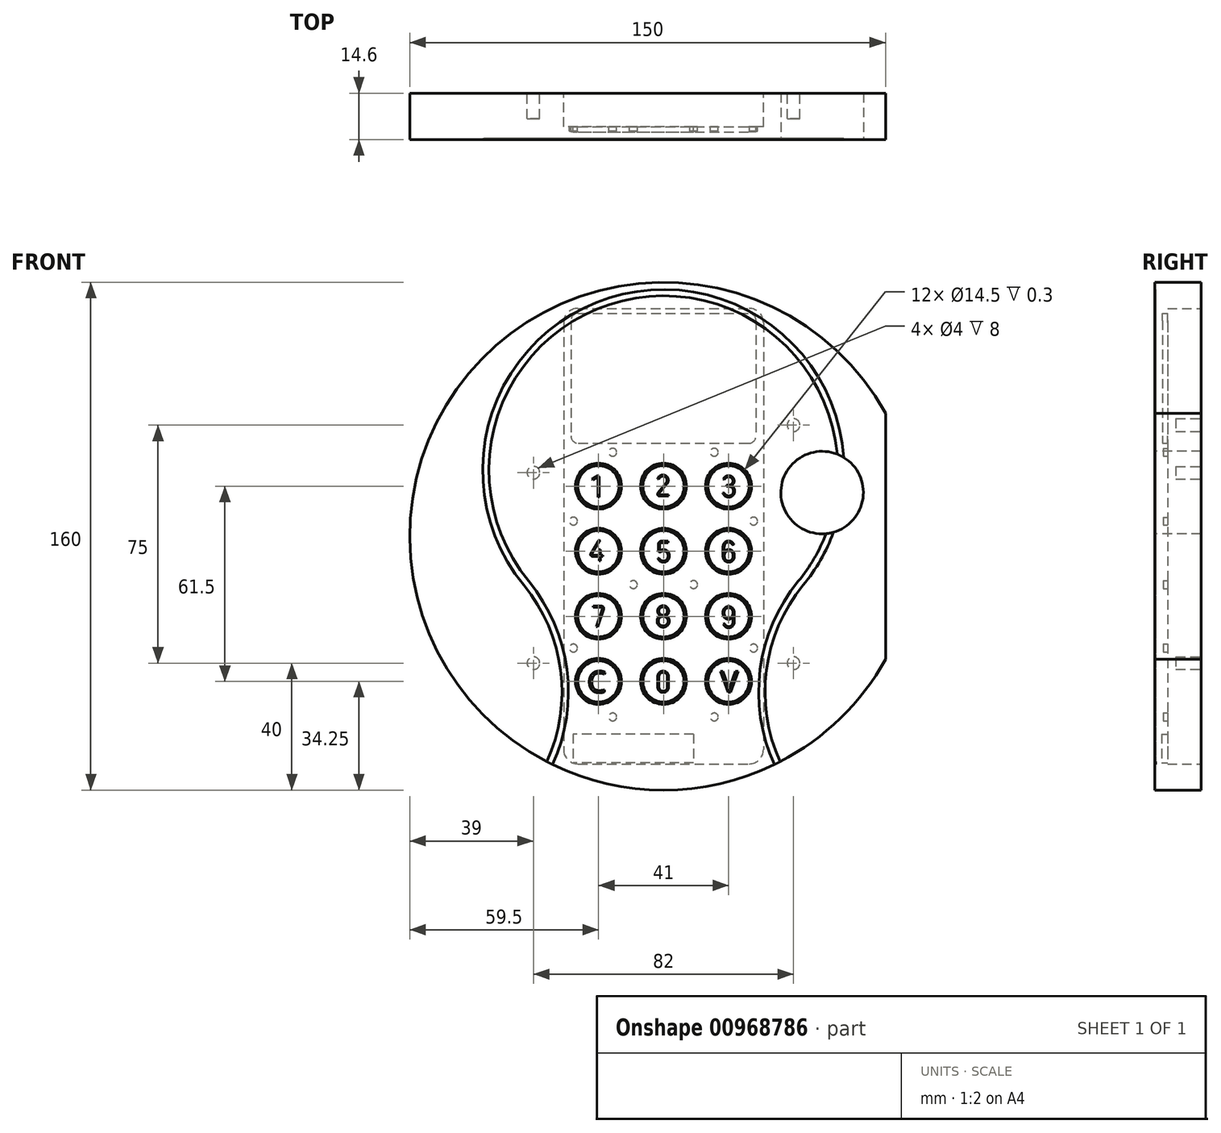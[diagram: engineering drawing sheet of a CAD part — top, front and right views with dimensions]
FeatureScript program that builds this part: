
annotation { "Feature Type Name" : "Feature", "Feature Type Description" : "" }
export const myFeature = defineFeature(function(context is Context, id is Id, definition is map)
    precondition{}
    {
        {
            var Q0;
            Q0=qCreatedBy(makeId("Front.planeOp"),FACE);
            var sketch = newSketch(context, id + "F0", { "sketchPlane" : qUnion([Q0])});
            skArc(sketch, "E0", {"start": v(70, -38.73) * mm, "mid": v(-80, 0) * mm, "end": v(70, 38.73) * mm});
            skLineSegment(sketch, "E1", {"start": v(70, 38.73) * mm, "end": v(70, -38.73) * mm});
            skSolve(sketch);
        }
        {
            var Q0;
            Q0 = qSketchRegion(id + "F0", true);
            extrude(context, id + "F1", {"entities" : qUnion([Q0]), "depth" : 14.6 * mm, "offsetDistance" : 25 * mm});
        }
        {
            var Q0;
            Q0=makeQuery(id+"F1.opExtrude","CAP_FACE",FACE,{"disambiguationData":[OSD([sQuery(id+"F0.wireOp",EDGE,"E0"),sQuery(id+"F0.wireOp",EDGE,"E1")])],"isStart":true});
            var sketch = newSketch(context, id + "F2", { "sketchPlane" : qUnion([Q0])});
            skLineSegment(sketch, "E2.bottom", {"start": v(31.5, 71.75) * mm, "end": v(-31.5, 71.75) * mm});
            skLineSegment(sketch, "E2.top", {"start": v(31.5, -71.75) * mm, "end": v(-31.5, -71.75) * mm});
            skLineSegment(sketch, "E2.left", {"start": v(31.5, 71.75) * mm, "end": v(31.5, -71.75) * mm});
            skLineSegment(sketch, "E2.right", {"start": v(-31.5, 71.75) * mm, "end": v(-31.5, -71.75) * mm});
            skSolve(sketch);
        }
        {
            var Q0;
            Q0 = qSketchRegion(id + "F2", true);
            extrude(context, id + "F3", {"entities" : qUnion([Q0]), "operationType" : NewBodyOperationType.REMOVE, "oppositeDirection" : true, "depth" : 10.6 * mm, "offsetDistance" : 25 * mm});
        }
        {
            var Q0;
            Q0=makeQuery(id+"F3.boolean.opBoolean","COPY",EDGE,{"derivedFrom":makeQuery(id+"F3.opExtrude","SWEPT_EDGE",EDGE,{"disambiguationData":[OSD([sQuery(id+"F2.wireOp",EDGE,"E2.bottom"),sQuery(id+"F2.wireOp",EDGE,"E2.left")])]})});
            var Q1;
            Q1=makeQuery(id+"F3.boolean.opBoolean","COPY",EDGE,{"derivedFrom":makeQuery(id+"F3.opExtrude","SWEPT_EDGE",EDGE,{"disambiguationData":[OSD([sQuery(id+"F2.wireOp",EDGE,"E2.bottom"),sQuery(id+"F2.wireOp",EDGE,"E2.right")])]})});
            var Q2;
            Q2=makeQuery(id+"F3.boolean.opBoolean","COPY",EDGE,{"derivedFrom":makeQuery(id+"F3.opExtrude","SWEPT_EDGE",EDGE,{"disambiguationData":[OSD([sQuery(id+"F2.wireOp",EDGE,"E2.top"),sQuery(id+"F2.wireOp",EDGE,"E2.left")])]})});
            var Q3;
            Q3=makeQuery(id+"F3.boolean.opBoolean","COPY",EDGE,{"derivedFrom":makeQuery(id+"F3.opExtrude","SWEPT_EDGE",EDGE,{"disambiguationData":[OSD([sQuery(id+"F2.wireOp",EDGE,"E2.top"),sQuery(id+"F2.wireOp",EDGE,"E2.right")])]})});
            fillet(context, id + "F4", {"entities" : qUnion([Q0, Q1, Q2, Q3]), "radius" : 4.5 * mm, "tangentPropagation" : true, "allowEdgeOverflow" : false});
        }
        {
            var Q0;
            Q0=makeQuery(id+"F3.boolean.opBoolean","COPY",FACE,{"derivedFrom":makeQuery(id+"F3.opExtrude","CAP_FACE",FACE,{"disambiguationData":[OSD([sQuery(id+"F2.wireOp",EDGE,"E2.bottom"),sQuery(id+"F2.wireOp",EDGE,"E2.top"),sQuery(id+"F2.wireOp",EDGE,"E2.left"),sQuery(id+"F2.wireOp",EDGE,"E2.right")])],"isStart":false})});
            var sketch = newSketch(context, id + "F5", { "sketchPlane" : qUnion([Q0])});
            skLineSegment(sketch, "E3.bottom", {"start": v(29.15, 70.25) * mm, "end": v(-29.15, 70.25) * mm});
            skLineSegment(sketch, "E3.top", {"start": v(29.15, 29.25) * mm, "end": v(-29.15, 29.25) * mm});
            skLineSegment(sketch, "E3.left", {"start": v(29.15, 70.25) * mm, "end": v(29.15, 29.25) * mm});
            skLineSegment(sketch, "E3.right", {"start": v(-29.15, 70.25) * mm, "end": v(-29.15, 29.25) * mm});
            skSolve(sketch);
        }
        {
            var Q0;
            Q0 = qSketchRegion(id + "F5", true);
            extrude(context, id + "F6", {"entities" : qUnion([Q0]), "operationType" : NewBodyOperationType.REMOVE, "oppositeDirection" : true, "depth" : 1.65 * mm, "offsetDistance" : 25 * mm});
        }
        {
            var Q0;
            Q0=makeQuery(id+"F6.boolean.opBoolean","COPY",EDGE,{"derivedFrom":makeQuery(id+"F6.opExtrude","SWEPT_EDGE",EDGE,{"disambiguationData":[OSD([sQuery(id+"F5.wireOp",EDGE,"E3.bottom"),sQuery(id+"F5.wireOp",EDGE,"E3.left")])]})});
            var Q1;
            Q1=makeQuery(id+"F6.boolean.opBoolean","COPY",EDGE,{"derivedFrom":makeQuery(id+"F6.opExtrude","SWEPT_EDGE",EDGE,{"disambiguationData":[OSD([sQuery(id+"F5.wireOp",EDGE,"E3.top"),sQuery(id+"F5.wireOp",EDGE,"E3.left")])]})});
            var Q2;
            Q2=makeQuery(id+"F6.boolean.opBoolean","COPY",EDGE,{"derivedFrom":makeQuery(id+"F6.opExtrude","SWEPT_EDGE",EDGE,{"disambiguationData":[OSD([sQuery(id+"F5.wireOp",EDGE,"E3.bottom"),sQuery(id+"F5.wireOp",EDGE,"E3.right")])]})});
            var Q3;
            Q3=makeQuery(id+"F6.boolean.opBoolean","COPY",EDGE,{"derivedFrom":makeQuery(id+"F6.opExtrude","SWEPT_EDGE",EDGE,{"disambiguationData":[OSD([sQuery(id+"F5.wireOp",EDGE,"E3.top"),sQuery(id+"F5.wireOp",EDGE,"E3.right")])]})});
            fillet(context, id + "F7", {"entities" : qUnion([Q0, Q1, Q2, Q3]), "radius" : 2.3 * mm, "tangentPropagation" : true, "allowEdgeOverflow" : false});
        }
        {
            var Q0;
            Q0=makeQuery(id+"F3.boolean.opBoolean","COPY",FACE,{"derivedFrom":makeQuery(id+"F3.opExtrude","CAP_FACE",FACE,{"disambiguationData":[OSD([sQuery(id+"F2.wireOp",EDGE,"E2.bottom"),sQuery(id+"F2.wireOp",EDGE,"E2.top"),sQuery(id+"F2.wireOp",EDGE,"E2.left"),sQuery(id+"F2.wireOp",EDGE,"E2.right")])],"isStart":false})});
            var sketch = newSketch(context, id + "F8", { "sketchPlane" : qUnion([Q0])});
            skCircle(sketch, "E4", {"center": v(-16, 26.45) * mm, "radius": 1.25 * mm});
            skCircle(sketch, "E5", {"center": v(16, 26.45) * mm, "radius": 1.25 * mm});
            skCircle(sketch, "E6", {"center": v(9.5, -15.25) * mm, "radius": 1.25 * mm});
            skCircle(sketch, "E7", {"center": v(-9.5, -15.25) * mm, "radius": 1.25 * mm});
            skCircle(sketch, "E8", {"center": v(-16, -56.95) * mm, "radius": 1.25 * mm});
            skCircle(sketch, "E9", {"center": v(16, -56.95) * mm, "radius": 1.25 * mm});
            skArc(sketch, "E10", {"start": v(-28.4, 6) * mm, "mid": v(-27.15, 4.75) * mm, "end": v(-28.4, 3.5) * mm});
            skArc(sketch, "E11.MirrorCS", {"start": v(28.4, 6) * mm, "mid": v(27.15, 4.75) * mm, "end": v(28.4, 3.5) * mm});
            skArc(sketch, "E12", {"start": v(-28.4, -34) * mm, "mid": v(-27.15, -35.25) * mm, "end": v(-28.4, -36.5) * mm});
            skArc(sketch, "E13.MirrorCS", {"start": v(28.4, -34) * mm, "mid": v(27.15, -35.25) * mm, "end": v(28.4, -36.5) * mm});
            skArc(sketch, "E14", {"start": v(-28.4, 3.5) * mm, "mid": v(-29.65, 4.75) * mm, "end": v(-28.4, 6) * mm});
            skArc(sketch, "E15", {"start": v(28.4, 6) * mm, "mid": v(29.65, 4.75) * mm, "end": v(28.4, 3.5) * mm});
            skArc(sketch, "E16", {"start": v(28.4, -34) * mm, "mid": v(29.65, -35.25) * mm, "end": v(28.4, -36.5) * mm});
            skArc(sketch, "E17", {"start": v(-28.4, -34) * mm, "mid": v(-29.65, -35.25) * mm, "end": v(-28.4, -36.5) * mm});
            skSolve(sketch);
        }
        {
            var Q0;
            Q0 = qSketchRegion(id + "F8", true);
            extrude(context, id + "F9", {"entities" : qUnion([Q0]), "operationType" : NewBodyOperationType.REMOVE, "oppositeDirection" : true, "depth" : 1.4 * mm, "offsetDistance" : 25 * mm});
        }
        {
            var Q0;
            Q0=makeQuery(id+"F3.boolean.opBoolean","COPY",FACE,{"derivedFrom":makeQuery(id+"F3.opExtrude","CAP_FACE",FACE,{"disambiguationData":[OSD([sQuery(id+"F2.wireOp",EDGE,"E2.bottom"),sQuery(id+"F2.wireOp",EDGE,"E2.top"),sQuery(id+"F2.wireOp",EDGE,"E2.left"),sQuery(id+"F2.wireOp",EDGE,"E2.right")])],"isStart":false})});
            var sketch = newSketch(context, id + "F10", { "sketchPlane" : qUnion([Q0])});
            skLineSegment(sketch, "E18.bottom", {"start": v(-9.5, -62.35) * mm, "end": v(28.5, -62.35) * mm});
            skLineSegment(sketch, "E18.top", {"start": v(-9.5, -71.35) * mm, "end": v(28.5, -71.35) * mm});
            skLineSegment(sketch, "E18.left", {"start": v(-9.5, -62.35) * mm, "end": v(-9.5, -71.35) * mm});
            skLineSegment(sketch, "E18.right", {"start": v(28.5, -62.35) * mm, "end": v(28.5, -71.35) * mm});
            skSolve(sketch);
        }
        {
            var Q0;
            Q0 = qSketchRegion(id + "F10", true);
            extrude(context, id + "F11", {"entities" : qUnion([Q0]), "operationType" : NewBodyOperationType.REMOVE, "oppositeDirection" : true, "depth" : 1.8 * mm, "offsetDistance" : 25 * mm});
        }
        {
            var Q0;
            Q0=makeQuery(id+"F1.opExtrude","CAP_FACE",FACE,{"disambiguationData":[OSD([sQuery(id+"F0.wireOp",EDGE,"E0"),sQuery(id+"F0.wireOp",EDGE,"E1")])],"isStart":false});
            var sketch = newSketch(context, id + "F12", { "sketchPlane" : qUnion([Q0])});
            skCircle(sketch, "E19", {"center": v(-20.5, 15.75) * mm, "radius": 7.25 * mm});
            skCircle(sketch, "E20", {"center": v(0, 15.75) * mm, "radius": 7.25 * mm});
            skCircle(sketch, "E21", {"center": v(20.5, 15.75) * mm, "radius": 7.25 * mm});
            skCircle(sketch, "E22", {"center": v(0, -4.75) * mm, "radius": 7.25 * mm});
            skCircle(sketch, "E23", {"center": v(-20.5, -4.75) * mm, "radius": 7.25 * mm});
            skCircle(sketch, "E24", {"center": v(20.5, -4.75) * mm, "radius": 7.25 * mm});
            skCircle(sketch, "E25", {"center": v(0, -25.25) * mm, "radius": 7.25 * mm});
            skCircle(sketch, "E26", {"center": v(-20.5, -25.25) * mm, "radius": 7.25 * mm});
            skCircle(sketch, "E27", {"center": v(20.5, -25.25) * mm, "radius": 7.25 * mm});
            skCircle(sketch, "E28", {"center": v(0, -45.75) * mm, "radius": 7.25 * mm});
            skCircle(sketch, "E29", {"center": v(-20.5, -45.75) * mm, "radius": 7.25 * mm});
            skCircle(sketch, "E30", {"center": v(20.5, -45.75) * mm, "radius": 7.25 * mm});
            skCircle(sketch, "E31", {"center": v(-20.5, 15.75) * mm, "radius": 6.5 * mm});
            skCircle(sketch, "E32", {"center": v(0, 15.75) * mm, "radius": 6.5 * mm});
            skCircle(sketch, "E33", {"center": v(20.5, 15.75) * mm, "radius": 6.5 * mm});
            skCircle(sketch, "E34", {"center": v(-20.5, -4.75) * mm, "radius": 6.5 * mm});
            skCircle(sketch, "E35", {"center": v(0, -4.75) * mm, "radius": 6.5 * mm});
            skCircle(sketch, "E36", {"center": v(20.5, -4.75) * mm, "radius": 6.5 * mm});
            skCircle(sketch, "E37", {"center": v(-20.5, -25.25) * mm, "radius": 6.5 * mm});
            skCircle(sketch, "E38", {"center": v(0, -25.25) * mm, "radius": 6.5 * mm});
            skCircle(sketch, "E39", {"center": v(20.5, -25.25) * mm, "radius": 6.5 * mm});
            skCircle(sketch, "E40", {"center": v(-20.5, -45.75) * mm, "radius": 6.5 * mm});
            skCircle(sketch, "E41", {"center": v(0, -45.75) * mm, "radius": 6.5 * mm});
            skCircle(sketch, "E42", {"center": v(20.5, -45.75) * mm, "radius": 6.5 * mm});
            skSolve(sketch);
        }
        {
            var Q0;
            Q0 = qSketchRegion(id + "F12", true);
            extrude(context, id + "F13", {"entities" : qUnion([Q0]), "operationType" : NewBodyOperationType.REMOVE, "oppositeDirection" : true, "depth" : 0.3 * mm, "offsetDistance" : 25 * mm});
        }
        {
            var Q0;
            Q0=makeQuery(id+"F13.boolean.opBoolean","SPLIT",FACE,{"disambiguationData":[TD([makeQuery(id+"F13.opExtrude","SWEPT_FACE",FACE,{"disambiguationData":[OSD([sQuery(id+"F12.wireOp",EDGE,"E31")])]})])],"derivedFrom":makeQuery(id+"F1.opExtrude","CAP_FACE",FACE,{"disambiguationData":[OSD([sQuery(id+"F0.wireOp",EDGE,"E0"),sQuery(id+"F0.wireOp",EDGE,"E1")])],"isStart":false})});
            var sketch = newSketch(context, id + "F14", { "sketchPlane" : qUnion([Q0])});
            skLineSegment(sketch, "E43", {"start": v(-20.2, 12.3) * mm, "end": v(-20.6, 12.3) * mm});
            skLineSegment(sketch, "E44", {"start": v(-20.6, 12.3) * mm, "end": v(-20.6, 18.3) * mm});
            skLineSegment(sketch, "E45", {"start": v(-20.6, 18.3) * mm, "end": v(-20.6, 18.36) * mm});
            skLineSegment(sketch, "E46", {"start": v(-20.6, 18.36) * mm, "end": v(-20.62, 18.4) * mm});
            skLineSegment(sketch, "E47", {"start": v(-20.62, 18.4) * mm, "end": v(-20.63, 18.44) * mm});
            skLineSegment(sketch, "E48", {"start": v(-20.63, 18.44) * mm, "end": v(-20.64, 18.47) * mm});
            skLineSegment(sketch, "E49", {"start": v(-20.64, 18.47) * mm, "end": v(-20.66, 18.5) * mm});
            skLineSegment(sketch, "E50", {"start": v(-20.66, 18.5) * mm, "end": v(-20.69, 18.53) * mm});
            skLineSegment(sketch, "E51", {"start": v(-20.69, 18.53) * mm, "end": v(-20.72, 18.55) * mm});
            skLineSegment(sketch, "E52", {"start": v(-20.72, 18.55) * mm, "end": v(-20.75, 18.56) * mm});
            skLineSegment(sketch, "E53", {"start": v(-20.75, 18.56) * mm, "end": v(-20.79, 18.57) * mm});
            skLineSegment(sketch, "E54", {"start": v(-20.79, 18.57) * mm, "end": v(-20.83, 18.57) * mm});
            skLineSegment(sketch, "E55", {"start": v(-20.83, 18.57) * mm, "end": v(-20.85, 18.57) * mm});
            skLineSegment(sketch, "E56", {"start": v(-20.85, 18.57) * mm, "end": v(-20.87, 18.57) * mm});
            skLineSegment(sketch, "E57", {"start": v(-20.87, 18.57) * mm, "end": v(-20.9, 18.56) * mm});
            skLineSegment(sketch, "E58", {"start": v(-20.9, 18.56) * mm, "end": v(-20.91, 18.56) * mm});
            skLineSegment(sketch, "E59", {"start": v(-20.91, 18.56) * mm, "end": v(-20.93, 18.55) * mm});
            skLineSegment(sketch, "E60", {"start": v(-20.93, 18.55) * mm, "end": v(-20.95, 18.54) * mm});
            skLineSegment(sketch, "E61", {"start": v(-20.95, 18.54) * mm, "end": v(-20.98, 18.53) * mm});
            skLineSegment(sketch, "E62", {"start": v(-20.98, 18.53) * mm, "end": v(-21, 18.52) * mm});
            skLineSegment(sketch, "E63", {"start": v(-21, 18.52) * mm, "end": v(-21.02, 18.5) * mm});
            skLineSegment(sketch, "E64", {"start": v(-21.02, 18.5) * mm, "end": v(-21.04, 18.5) * mm});
            skLineSegment(sketch, "E65", {"start": v(-21.04, 18.5) * mm, "end": v(-22.27, 17.72) * mm});
            skLineSegment(sketch, "E66", {"start": v(-22.27, 17.72) * mm, "end": v(-22.5, 18.06) * mm});
            skLineSegment(sketch, "E67", {"start": v(-22.5, 18.06) * mm, "end": v(-21.25, 18.84) * mm});
            skLineSegment(sketch, "E68", {"start": v(-21.25, 18.84) * mm, "end": v(-21.24, 18.85) * mm});
            skLineSegment(sketch, "E69", {"start": v(-21.24, 18.85) * mm, "end": v(-21.23, 18.85) * mm});
            skLineSegment(sketch, "E70", {"start": v(-21.23, 18.85) * mm, "end": v(-21.22, 18.86) * mm});
            skLineSegment(sketch, "E71", {"start": v(-21.22, 18.86) * mm, "end": v(-21.2, 18.87) * mm});
            skLineSegment(sketch, "E72", {"start": v(-21.2, 18.87) * mm, "end": v(-21.19, 18.87) * mm});
            skLineSegment(sketch, "E73", {"start": v(-21.19, 18.87) * mm, "end": v(-21.17, 18.88) * mm});
            skLineSegment(sketch, "E74", {"start": v(-21.17, 18.88) * mm, "end": v(-21.15, 18.9) * mm});
            skLineSegment(sketch, "E75", {"start": v(-21.15, 18.9) * mm, "end": v(-21.13, 18.9) * mm});
            skLineSegment(sketch, "E76", {"start": v(-21.13, 18.9) * mm, "end": v(-21.1, 18.9) * mm});
            skLineSegment(sketch, "E77", {"start": v(-21.1, 18.9) * mm, "end": v(-21.09, 18.92) * mm});
            skLineSegment(sketch, "E78", {"start": v(-21.09, 18.92) * mm, "end": v(-21.06, 18.93) * mm});
            skLineSegment(sketch, "E79", {"start": v(-21.06, 18.93) * mm, "end": v(-21.04, 18.94) * mm});
            skLineSegment(sketch, "E80", {"start": v(-21.04, 18.94) * mm, "end": v(-21.02, 18.95) * mm});
            skLineSegment(sketch, "E81", {"start": v(-21.02, 18.95) * mm, "end": v(-21, 18.95) * mm});
            skLineSegment(sketch, "E82", {"start": v(-21, 18.95) * mm, "end": v(-20.97, 18.96) * mm});
            skLineSegment(sketch, "E83", {"start": v(-20.97, 18.96) * mm, "end": v(-20.94, 18.96) * mm});
            skLineSegment(sketch, "E84", {"start": v(-20.94, 18.96) * mm, "end": v(-20.91, 18.97) * mm});
            skLineSegment(sketch, "E85", {"start": v(-20.91, 18.97) * mm, "end": v(-20.89, 18.97) * mm});
            skLineSegment(sketch, "E86", {"start": v(-20.89, 18.97) * mm, "end": v(-20.86, 18.97) * mm});
            skLineSegment(sketch, "E87", {"start": v(-20.86, 18.97) * mm, "end": v(-20.83, 18.97) * mm});
            skLineSegment(sketch, "E88", {"start": v(-20.83, 18.97) * mm, "end": v(-20.77, 18.97) * mm});
            skLineSegment(sketch, "E89", {"start": v(-20.77, 18.97) * mm, "end": v(-20.72, 18.96) * mm});
            skLineSegment(sketch, "E90", {"start": v(-20.72, 18.96) * mm, "end": v(-20.67, 18.95) * mm});
            skLineSegment(sketch, "E91", {"start": v(-20.67, 18.95) * mm, "end": v(-20.62, 18.94) * mm});
            skLineSegment(sketch, "E92", {"start": v(-20.62, 18.94) * mm, "end": v(-20.58, 18.92) * mm});
            skLineSegment(sketch, "E93", {"start": v(-20.58, 18.92) * mm, "end": v(-20.53, 18.9) * mm});
            skLineSegment(sketch, "E94", {"start": v(-20.53, 18.9) * mm, "end": v(-20.49, 18.88) * mm});
            skLineSegment(sketch, "E95", {"start": v(-20.49, 18.88) * mm, "end": v(-20.45, 18.85) * mm});
            skLineSegment(sketch, "E96", {"start": v(-20.45, 18.85) * mm, "end": v(-20.41, 18.82) * mm});
            skLineSegment(sketch, "E97", {"start": v(-20.41, 18.82) * mm, "end": v(-20.38, 18.79) * mm});
            skLineSegment(sketch, "E98", {"start": v(-20.38, 18.79) * mm, "end": v(-20.34, 18.75) * mm});
            skLineSegment(sketch, "E99", {"start": v(-20.34, 18.75) * mm, "end": v(-20.32, 18.71) * mm});
            skLineSegment(sketch, "E100", {"start": v(-20.32, 18.71) * mm, "end": v(-20.29, 18.67) * mm});
            skLineSegment(sketch, "E101", {"start": v(-20.29, 18.67) * mm, "end": v(-20.27, 18.62) * mm});
            skLineSegment(sketch, "E102", {"start": v(-20.27, 18.62) * mm, "end": v(-20.25, 18.58) * mm});
            skLineSegment(sketch, "E103", {"start": v(-20.25, 18.58) * mm, "end": v(-20.23, 18.53) * mm});
            skLineSegment(sketch, "E104", {"start": v(-20.23, 18.53) * mm, "end": v(-20.22, 18.48) * mm});
            skLineSegment(sketch, "E105", {"start": v(-20.22, 18.48) * mm, "end": v(-20.21, 18.42) * mm});
            skLineSegment(sketch, "E106", {"start": v(-20.21, 18.42) * mm, "end": v(-20.2, 18.36) * mm});
            skLineSegment(sketch, "E107", {"start": v(-20.2, 18.36) * mm, "end": v(-20.2, 18.3) * mm});
            skLineSegment(sketch, "E108", {"start": v(-20.2, 18.3) * mm, "end": v(-20.2, 12.3) * mm});
            skLineSegment(sketch, "E109", {"start": v(-1.2, 12.65) * mm, "end": v(-1.23, 12.65) * mm});
            skLineSegment(sketch, "E110", {"start": v(-1.23, 12.65) * mm, "end": v(-1.26, 12.65) * mm});
            skLineSegment(sketch, "E111", {"start": v(-1.26, 12.65) * mm, "end": v(-1.29, 12.66) * mm});
            skLineSegment(sketch, "E112", {"start": v(-1.29, 12.66) * mm, "end": v(-1.31, 12.66) * mm});
            skLineSegment(sketch, "E113", {"start": v(-1.31, 12.66) * mm, "end": v(-1.34, 12.66) * mm});
            skLineSegment(sketch, "E114", {"start": v(-1.34, 12.66) * mm, "end": v(-1.37, 12.67) * mm});
            skLineSegment(sketch, "E115", {"start": v(-1.37, 12.67) * mm, "end": v(-1.4, 12.67) * mm});
            skLineSegment(sketch, "E116", {"start": v(-1.4, 12.67) * mm, "end": v(-1.42, 12.68) * mm});
            skLineSegment(sketch, "E117", {"start": v(-1.42, 12.68) * mm, "end": v(-1.44, 12.69) * mm});
            skLineSegment(sketch, "E118", {"start": v(-1.44, 12.69) * mm, "end": v(-1.47, 12.7) * mm});
            skLineSegment(sketch, "E119", {"start": v(-1.47, 12.7) * mm, "end": v(-1.5, 12.7) * mm});
            skLineSegment(sketch, "E120", {"start": v(-1.5, 12.7) * mm, "end": v(-1.52, 12.71) * mm});
            skLineSegment(sketch, "E121", {"start": v(-1.52, 12.71) * mm, "end": v(-1.54, 12.72) * mm});
            skLineSegment(sketch, "E122", {"start": v(-1.54, 12.72) * mm, "end": v(-1.56, 12.73) * mm});
            skLineSegment(sketch, "E123", {"start": v(-1.56, 12.73) * mm, "end": v(-1.58, 12.74) * mm});
            skLineSegment(sketch, "E124", {"start": v(-1.58, 12.74) * mm, "end": v(-1.6, 12.76) * mm});
            skLineSegment(sketch, "E125", {"start": v(-1.6, 12.76) * mm, "end": v(-1.63, 12.77) * mm});
            skLineSegment(sketch, "E126", {"start": v(-1.63, 12.77) * mm, "end": v(-1.65, 12.78) * mm});
            skLineSegment(sketch, "E127", {"start": v(-1.65, 12.78) * mm, "end": v(-1.67, 12.8) * mm});
            skLineSegment(sketch, "E128", {"start": v(-1.67, 12.8) * mm, "end": v(-1.68, 12.81) * mm});
            skLineSegment(sketch, "E129", {"start": v(-1.68, 12.81) * mm, "end": v(-1.7, 12.83) * mm});
            skLineSegment(sketch, "E130", {"start": v(-1.7, 12.83) * mm, "end": v(-1.72, 12.85) * mm});
            skLineSegment(sketch, "E131", {"start": v(-1.72, 12.85) * mm, "end": v(-1.73, 12.86) * mm});
            skLineSegment(sketch, "E132", {"start": v(-1.73, 12.86) * mm, "end": v(-1.75, 12.88) * mm});
            skLineSegment(sketch, "E133", {"start": v(-1.75, 12.88) * mm, "end": v(-1.76, 12.9) * mm});
            skLineSegment(sketch, "E134", {"start": v(-1.76, 12.9) * mm, "end": v(-1.78, 12.92) * mm});
            skLineSegment(sketch, "E135", {"start": v(-1.78, 12.92) * mm, "end": v(-1.8, 12.94) * mm});
            skLineSegment(sketch, "E136", {"start": v(-1.8, 12.94) * mm, "end": v(-1.8, 12.96) * mm});
            skLineSegment(sketch, "E137", {"start": v(-1.8, 12.96) * mm, "end": v(-1.82, 12.98) * mm});
            skLineSegment(sketch, "E138", {"start": v(-1.82, 12.98) * mm, "end": v(-1.83, 13) * mm});
            skLineSegment(sketch, "E139", {"start": v(-1.83, 13) * mm, "end": v(-1.84, 13.03) * mm});
            skLineSegment(sketch, "E140", {"start": v(-1.84, 13.03) * mm, "end": v(-1.85, 13.05) * mm});
            skLineSegment(sketch, "E141", {"start": v(-1.85, 13.05) * mm, "end": v(-1.85, 13.07) * mm});
            skLineSegment(sketch, "E142", {"start": v(-1.85, 13.07) * mm, "end": v(-1.86, 13.1) * mm});
            skLineSegment(sketch, "E143", {"start": v(-1.86, 13.1) * mm, "end": v(-1.87, 13.12) * mm});
            skLineSegment(sketch, "E144", {"start": v(-1.87, 13.12) * mm, "end": v(-1.87, 13.14) * mm});
            skLineSegment(sketch, "E145", {"start": v(-1.87, 13.14) * mm, "end": v(-1.87, 13.17) * mm});
            skLineSegment(sketch, "E146", {"start": v(-1.87, 13.17) * mm, "end": v(-1.88, 13.2) * mm});
            skLineSegment(sketch, "E147", {"start": v(-1.88, 13.2) * mm, "end": v(-1.88, 13.22) * mm});
            skLineSegment(sketch, "E148", {"start": v(-1.88, 13.22) * mm, "end": v(-1.88, 13.25) * mm});
            skLineSegment(sketch, "E149", {"start": v(-1.88, 13.25) * mm, "end": v(-1.88, 13.27) * mm});
            skLineSegment(sketch, "E150", {"start": v(-1.88, 13.27) * mm, "end": v(-1.88, 13.29) * mm});
            skLineSegment(sketch, "E151", {"start": v(-1.88, 13.29) * mm, "end": v(-1.88, 13.3) * mm});
            skLineSegment(sketch, "E152", {"start": v(-1.88, 13.3) * mm, "end": v(-1.88, 13.33) * mm});
            skLineSegment(sketch, "E153", {"start": v(-1.88, 13.33) * mm, "end": v(-1.87, 13.35) * mm});
            skLineSegment(sketch, "E154", {"start": v(-1.87, 13.35) * mm, "end": v(-1.87, 13.37) * mm});
            skLineSegment(sketch, "E155", {"start": v(-1.87, 13.37) * mm, "end": v(-1.87, 13.4) * mm});
            skLineSegment(sketch, "E156", {"start": v(-1.87, 13.4) * mm, "end": v(-1.86, 13.41) * mm});
            skLineSegment(sketch, "E157", {"start": v(-1.86, 13.41) * mm, "end": v(-1.86, 13.43) * mm});
            skLineSegment(sketch, "E158", {"start": v(-1.86, 13.43) * mm, "end": v(-1.85, 13.45) * mm});
            skLineSegment(sketch, "E159", {"start": v(-1.85, 13.45) * mm, "end": v(-1.85, 13.47) * mm});
            skLineSegment(sketch, "E160", {"start": v(-1.85, 13.47) * mm, "end": v(-1.84, 13.5) * mm});
            skLineSegment(sketch, "E161", {"start": v(-1.84, 13.5) * mm, "end": v(-1.83, 13.52) * mm});
            skLineSegment(sketch, "E162", {"start": v(-1.83, 13.52) * mm, "end": v(-1.83, 13.54) * mm});
            skLineSegment(sketch, "E163", {"start": v(-1.83, 13.54) * mm, "end": v(-1.82, 13.56) * mm});
            skLineSegment(sketch, "E164", {"start": v(-1.82, 13.56) * mm, "end": v(-1.8, 13.58) * mm});
            skLineSegment(sketch, "E165", {"start": v(-1.8, 13.58) * mm, "end": v(-1.8, 13.6) * mm});
            skLineSegment(sketch, "E166", {"start": v(-1.8, 13.6) * mm, "end": v(-1.78, 13.62) * mm});
            skLineSegment(sketch, "E167", {"start": v(-1.78, 13.62) * mm, "end": v(-1.77, 13.65) * mm});
            skLineSegment(sketch, "E168", {"start": v(-1.77, 13.65) * mm, "end": v(-1.75, 13.67) * mm});
            skLineSegment(sketch, "E169", {"start": v(-1.75, 13.67) * mm, "end": v(0.67, 16.56) * mm});
            skLineSegment(sketch, "E170", {"start": v(0.67, 16.56) * mm, "end": v(0.71, 16.61) * mm});
            skLineSegment(sketch, "E171", {"start": v(0.71, 16.61) * mm, "end": v(0.76, 16.67) * mm});
            skLineSegment(sketch, "E172", {"start": v(0.76, 16.67) * mm, "end": v(0.8, 16.72) * mm});
            skLineSegment(sketch, "E173", {"start": v(0.8, 16.72) * mm, "end": v(0.83, 16.77) * mm});
            skLineSegment(sketch, "E174", {"start": v(0.83, 16.77) * mm, "end": v(0.86, 16.82) * mm});
            skLineSegment(sketch, "E175", {"start": v(0.86, 16.82) * mm, "end": v(0.9, 16.88) * mm});
            skLineSegment(sketch, "E176", {"start": v(0.9, 16.88) * mm, "end": v(0.92, 16.93) * mm});
            skLineSegment(sketch, "E177", {"start": v(0.92, 16.93) * mm, "end": v(0.95, 16.99) * mm});
            skLineSegment(sketch, "E178", {"start": v(0.95, 16.99) * mm, "end": v(0.98, 17.04) * mm});
            skLineSegment(sketch, "E179", {"start": v(0.98, 17.04) * mm, "end": v(1, 17.1) * mm});
            skLineSegment(sketch, "E180", {"start": v(1, 17.1) * mm, "end": v(1.02, 17.15) * mm});
            skLineSegment(sketch, "E181", {"start": v(1.02, 17.15) * mm, "end": v(1.04, 17.2) * mm});
            skLineSegment(sketch, "E182", {"start": v(1.04, 17.2) * mm, "end": v(1.06, 17.26) * mm});
            skLineSegment(sketch, "E183", {"start": v(1.06, 17.26) * mm, "end": v(1.07, 17.31) * mm});
            skLineSegment(sketch, "E184", {"start": v(1.07, 17.31) * mm, "end": v(1.08, 17.36) * mm});
            skLineSegment(sketch, "E185", {"start": v(1.08, 17.36) * mm, "end": v(1.1, 17.42) * mm});
            skLineSegment(sketch, "E186", {"start": v(1.1, 17.42) * mm, "end": v(1.1, 17.47) * mm});
            skLineSegment(sketch, "E187", {"start": v(1.1, 17.47) * mm, "end": v(1.1, 17.52) * mm});
            skLineSegment(sketch, "E188", {"start": v(1.1, 17.52) * mm, "end": v(1.1, 17.56) * mm});
            skLineSegment(sketch, "E189", {"start": v(1.1, 17.56) * mm, "end": v(1.11, 17.61) * mm});
            skLineSegment(sketch, "E190", {"start": v(1.11, 17.61) * mm, "end": v(1.11, 17.67) * mm});
            skLineSegment(sketch, "E191", {"start": v(1.11, 17.67) * mm, "end": v(1.1, 17.73) * mm});
            skLineSegment(sketch, "E192", {"start": v(1.1, 17.73) * mm, "end": v(1.1, 17.78) * mm});
            skLineSegment(sketch, "E193", {"start": v(1.1, 17.78) * mm, "end": v(1.1, 17.84) * mm});
            skLineSegment(sketch, "E194", {"start": v(1.1, 17.84) * mm, "end": v(1.09, 17.9) * mm});
            skLineSegment(sketch, "E195", {"start": v(1.09, 17.9) * mm, "end": v(1.08, 17.94) * mm});
            skLineSegment(sketch, "E196", {"start": v(1.08, 17.94) * mm, "end": v(1.07, 18) * mm});
            skLineSegment(sketch, "E197", {"start": v(1.07, 18) * mm, "end": v(1.05, 18.04) * mm});
            skLineSegment(sketch, "E198", {"start": v(1.05, 18.04) * mm, "end": v(1.04, 18.1) * mm});
            skLineSegment(sketch, "E199", {"start": v(1.04, 18.1) * mm, "end": v(1.02, 18.14) * mm});
            skLineSegment(sketch, "E200", {"start": v(1.02, 18.14) * mm, "end": v(1, 18.19) * mm});
            skLineSegment(sketch, "E201", {"start": v(1, 18.19) * mm, "end": v(0.98, 18.23) * mm});
            skLineSegment(sketch, "E202", {"start": v(0.98, 18.23) * mm, "end": v(0.96, 18.27) * mm});
            skLineSegment(sketch, "E203", {"start": v(0.96, 18.27) * mm, "end": v(0.93, 18.32) * mm});
            skLineSegment(sketch, "E204", {"start": v(0.93, 18.32) * mm, "end": v(0.9, 18.36) * mm});
            skLineSegment(sketch, "E205", {"start": v(0.9, 18.36) * mm, "end": v(0.88, 18.4) * mm});
            skLineSegment(sketch, "E206", {"start": v(0.88, 18.4) * mm, "end": v(0.85, 18.43) * mm});
            skLineSegment(sketch, "E207", {"start": v(0.85, 18.43) * mm, "end": v(0.82, 18.47) * mm});
            skLineSegment(sketch, "E208", {"start": v(0.82, 18.47) * mm, "end": v(0.8, 18.5) * mm});
            skLineSegment(sketch, "E209", {"start": v(0.8, 18.5) * mm, "end": v(0.76, 18.54) * mm});
            skLineSegment(sketch, "E210", {"start": v(0.76, 18.54) * mm, "end": v(0.73, 18.57) * mm});
            skLineSegment(sketch, "E211", {"start": v(0.73, 18.57) * mm, "end": v(0.7, 18.6) * mm});
            skLineSegment(sketch, "E212", {"start": v(0.7, 18.6) * mm, "end": v(0.65, 18.63) * mm});
            skLineSegment(sketch, "E213", {"start": v(0.65, 18.63) * mm, "end": v(0.62, 18.66) * mm});
            skLineSegment(sketch, "E214", {"start": v(0.62, 18.66) * mm, "end": v(0.58, 18.68) * mm});
            skLineSegment(sketch, "E215", {"start": v(0.58, 18.68) * mm, "end": v(0.54, 18.7) * mm});
            skLineSegment(sketch, "E216", {"start": v(0.54, 18.7) * mm, "end": v(0.5, 18.73) * mm});
            skLineSegment(sketch, "E217", {"start": v(0.5, 18.73) * mm, "end": v(0.45, 18.75) * mm});
            skLineSegment(sketch, "E218", {"start": v(0.45, 18.75) * mm, "end": v(0.4, 18.77) * mm});
            skLineSegment(sketch, "E219", {"start": v(0.4, 18.77) * mm, "end": v(0.36, 18.8) * mm});
            skLineSegment(sketch, "E220", {"start": v(0.36, 18.8) * mm, "end": v(0.31, 18.8) * mm});
            skLineSegment(sketch, "E221", {"start": v(0.31, 18.8) * mm, "end": v(0.26, 18.82) * mm});
            skLineSegment(sketch, "E222", {"start": v(0.26, 18.82) * mm, "end": v(0.21, 18.83) * mm});
            skLineSegment(sketch, "E223", {"start": v(0.21, 18.83) * mm, "end": v(0.16, 18.85) * mm});
            skLineSegment(sketch, "E224", {"start": v(0.16, 18.85) * mm, "end": v(0.11, 18.86) * mm});
            skLineSegment(sketch, "E225", {"start": v(0.11, 18.86) * mm, "end": v(0.06, 18.86) * mm});
            skLineSegment(sketch, "E226", {"start": v(0.06, 18.86) * mm, "end": v(0, 18.87) * mm});
            skLineSegment(sketch, "E227", {"start": v(0, 18.87) * mm, "end": v(-0.05, 18.87) * mm});
            skLineSegment(sketch, "E228", {"start": v(-0.05, 18.87) * mm, "end": v(-0.1, 18.88) * mm});
            skLineSegment(sketch, "E229", {"start": v(-0.1, 18.88) * mm, "end": v(-0.16, 18.88) * mm});
            skLineSegment(sketch, "E230", {"start": v(-0.16, 18.88) * mm, "end": v(-0.22, 18.88) * mm});
            skLineSegment(sketch, "E231", {"start": v(-0.22, 18.88) * mm, "end": v(-0.27, 18.88) * mm});
            skLineSegment(sketch, "E232", {"start": v(-0.27, 18.88) * mm, "end": v(-0.32, 18.87) * mm});
            skLineSegment(sketch, "E233", {"start": v(-0.32, 18.87) * mm, "end": v(-0.37, 18.87) * mm});
            skLineSegment(sketch, "E234", {"start": v(-0.37, 18.87) * mm, "end": v(-0.42, 18.86) * mm});
            skLineSegment(sketch, "E235", {"start": v(-0.42, 18.86) * mm, "end": v(-0.46, 18.85) * mm});
            skLineSegment(sketch, "E236", {"start": v(-0.46, 18.85) * mm, "end": v(-0.51, 18.84) * mm});
            skLineSegment(sketch, "E237", {"start": v(-0.51, 18.84) * mm, "end": v(-0.56, 18.83) * mm});
            skLineSegment(sketch, "E238", {"start": v(-0.56, 18.83) * mm, "end": v(-0.6, 18.82) * mm});
            skLineSegment(sketch, "E239", {"start": v(-0.6, 18.82) * mm, "end": v(-0.65, 18.8) * mm});
            skLineSegment(sketch, "E240", {"start": v(-0.65, 18.8) * mm, "end": v(-0.69, 18.79) * mm});
            skLineSegment(sketch, "E241", {"start": v(-0.69, 18.79) * mm, "end": v(-0.73, 18.77) * mm});
            skLineSegment(sketch, "E242", {"start": v(-0.73, 18.77) * mm, "end": v(-0.77, 18.75) * mm});
            skLineSegment(sketch, "E243", {"start": v(-0.77, 18.75) * mm, "end": v(-0.81, 18.73) * mm});
            skLineSegment(sketch, "E244", {"start": v(-0.81, 18.73) * mm, "end": v(-0.85, 18.71) * mm});
            skLineSegment(sketch, "E245", {"start": v(-0.85, 18.71) * mm, "end": v(-0.89, 18.7) * mm});
            skLineSegment(sketch, "E246", {"start": v(-0.89, 18.7) * mm, "end": v(-0.93, 18.67) * mm});
            skLineSegment(sketch, "E247", {"start": v(-0.93, 18.67) * mm, "end": v(-0.96, 18.64) * mm});
            skLineSegment(sketch, "E248", {"start": v(-0.96, 18.64) * mm, "end": v(-1, 18.62) * mm});
            skLineSegment(sketch, "E249", {"start": v(-1, 18.62) * mm, "end": v(-1.04, 18.59) * mm});
            skLineSegment(sketch, "E250", {"start": v(-1.04, 18.59) * mm, "end": v(-1.06, 18.56) * mm});
            skLineSegment(sketch, "E251", {"start": v(-1.06, 18.56) * mm, "end": v(-1.09, 18.54) * mm});
            skLineSegment(sketch, "E252", {"start": v(-1.09, 18.54) * mm, "end": v(-1.11, 18.52) * mm});
            skLineSegment(sketch, "E253", {"start": v(-1.11, 18.52) * mm, "end": v(-1.14, 18.5) * mm});
            skLineSegment(sketch, "E254", {"start": v(-1.14, 18.5) * mm, "end": v(-1.16, 18.47) * mm});
            skLineSegment(sketch, "E255", {"start": v(-1.16, 18.47) * mm, "end": v(-1.18, 18.44) * mm});
            skLineSegment(sketch, "E256", {"start": v(-1.18, 18.44) * mm, "end": v(-1.2, 18.41) * mm});
            skLineSegment(sketch, "E257", {"start": v(-1.2, 18.41) * mm, "end": v(-1.23, 18.38) * mm});
            skLineSegment(sketch, "E258", {"start": v(-1.23, 18.38) * mm, "end": v(-1.25, 18.36) * mm});
            skLineSegment(sketch, "E259", {"start": v(-1.25, 18.36) * mm, "end": v(-1.27, 18.33) * mm});
            skLineSegment(sketch, "E260", {"start": v(-1.27, 18.33) * mm, "end": v(-1.29, 18.3) * mm});
            skLineSegment(sketch, "E261", {"start": v(-1.29, 18.3) * mm, "end": v(-1.3, 18.26) * mm});
            skLineSegment(sketch, "E262", {"start": v(-1.3, 18.26) * mm, "end": v(-1.33, 18.23) * mm});
            skLineSegment(sketch, "E263", {"start": v(-1.33, 18.23) * mm, "end": v(-1.35, 18.2) * mm});
            skLineSegment(sketch, "E264", {"start": v(-1.35, 18.2) * mm, "end": v(-1.37, 18.16) * mm});
            skLineSegment(sketch, "E265", {"start": v(-1.37, 18.16) * mm, "end": v(-1.38, 18.13) * mm});
            skLineSegment(sketch, "E266", {"start": v(-1.38, 18.13) * mm, "end": v(-1.4, 18.1) * mm});
            skLineSegment(sketch, "E267", {"start": v(-1.4, 18.1) * mm, "end": v(-1.42, 18.06) * mm});
            skLineSegment(sketch, "E268", {"start": v(-1.42, 18.06) * mm, "end": v(-1.44, 18.02) * mm});
            skLineSegment(sketch, "E269", {"start": v(-1.44, 18.02) * mm, "end": v(-1.46, 17.98) * mm});
            skLineSegment(sketch, "E270", {"start": v(-1.46, 17.98) * mm, "end": v(-1.83, 18.12) * mm});
            skLineSegment(sketch, "E271", {"start": v(-1.83, 18.12) * mm, "end": v(-1.8, 18.22) * mm});
            skLineSegment(sketch, "E272", {"start": v(-1.8, 18.22) * mm, "end": v(-1.75, 18.31) * mm});
            skLineSegment(sketch, "E273", {"start": v(-1.75, 18.31) * mm, "end": v(-1.7, 18.4) * mm});
            skLineSegment(sketch, "E274", {"start": v(-1.7, 18.4) * mm, "end": v(-1.65, 18.48) * mm});
            skLineSegment(sketch, "E275", {"start": v(-1.65, 18.48) * mm, "end": v(-1.6, 18.56) * mm});
            skLineSegment(sketch, "E276", {"start": v(-1.6, 18.56) * mm, "end": v(-1.54, 18.64) * mm});
            skLineSegment(sketch, "E277", {"start": v(-1.54, 18.64) * mm, "end": v(-1.48, 18.71) * mm});
            skLineSegment(sketch, "E278", {"start": v(-1.48, 18.71) * mm, "end": v(-1.42, 18.78) * mm});
            skLineSegment(sketch, "E279", {"start": v(-1.42, 18.78) * mm, "end": v(-1.35, 18.85) * mm});
            skLineSegment(sketch, "E280", {"start": v(-1.35, 18.85) * mm, "end": v(-1.28, 18.9) * mm});
            skLineSegment(sketch, "E281", {"start": v(-1.28, 18.9) * mm, "end": v(-1.23, 18.94) * mm});
            skLineSegment(sketch, "E282", {"start": v(-1.23, 18.94) * mm, "end": v(-1.19, 18.97) * mm});
            skLineSegment(sketch, "E283", {"start": v(-1.19, 18.97) * mm, "end": v(-1.14, 19) * mm});
            skLineSegment(sketch, "E284", {"start": v(-1.14, 19) * mm, "end": v(-1.1, 19.04) * mm});
            skLineSegment(sketch, "E285", {"start": v(-1.1, 19.04) * mm, "end": v(-1.04, 19.06) * mm});
            skLineSegment(sketch, "E286", {"start": v(-1.04, 19.06) * mm, "end": v(-1, 19.1) * mm});
            skLineSegment(sketch, "E287", {"start": v(-1, 19.1) * mm, "end": v(-0.94, 19.12) * mm});
            skLineSegment(sketch, "E288", {"start": v(-0.94, 19.12) * mm, "end": v(-0.89, 19.14) * mm});
            skLineSegment(sketch, "E289", {"start": v(-0.89, 19.14) * mm, "end": v(-0.83, 19.16) * mm});
            skLineSegment(sketch, "E290", {"start": v(-0.83, 19.16) * mm, "end": v(-0.78, 19.18) * mm});
            skLineSegment(sketch, "E291", {"start": v(-0.78, 19.18) * mm, "end": v(-0.72, 19.2) * mm});
            skLineSegment(sketch, "E292", {"start": v(-0.72, 19.2) * mm, "end": v(-0.66, 19.22) * mm});
            skLineSegment(sketch, "E293", {"start": v(-0.66, 19.22) * mm, "end": v(-0.6, 19.23) * mm});
            skLineSegment(sketch, "E294", {"start": v(-0.6, 19.23) * mm, "end": v(-0.54, 19.24) * mm});
            skLineSegment(sketch, "E295", {"start": v(-0.54, 19.24) * mm, "end": v(-0.48, 19.26) * mm});
            skLineSegment(sketch, "E296", {"start": v(-0.48, 19.26) * mm, "end": v(-0.42, 19.26) * mm});
            skLineSegment(sketch, "E297", {"start": v(-0.42, 19.26) * mm, "end": v(-0.36, 19.27) * mm});
            skLineSegment(sketch, "E298", {"start": v(-0.36, 19.27) * mm, "end": v(-0.3, 19.28) * mm});
            skLineSegment(sketch, "E299", {"start": v(-0.3, 19.28) * mm, "end": v(-0.23, 19.28) * mm});
            skLineSegment(sketch, "E300", {"start": v(-0.23, 19.28) * mm, "end": v(-0.16, 19.28) * mm});
            skLineSegment(sketch, "E301", {"start": v(-0.16, 19.28) * mm, "end": v(-0.09, 19.28) * mm});
            skLineSegment(sketch, "E302", {"start": v(-0.09, 19.28) * mm, "end": v(-0.01, 19.27) * mm});
            skLineSegment(sketch, "E303", {"start": v(-0.01, 19.27) * mm, "end": v(0.06, 19.27) * mm});
            skLineSegment(sketch, "E304", {"start": v(0.06, 19.27) * mm, "end": v(0.13, 19.26) * mm});
            skLineSegment(sketch, "E305", {"start": v(0.13, 19.26) * mm, "end": v(0.2, 19.25) * mm});
            skLineSegment(sketch, "E306", {"start": v(0.2, 19.25) * mm, "end": v(0.27, 19.24) * mm});
            skLineSegment(sketch, "E307", {"start": v(0.27, 19.24) * mm, "end": v(0.33, 19.22) * mm});
            skLineSegment(sketch, "E308", {"start": v(0.33, 19.22) * mm, "end": v(0.4, 19.2) * mm});
            skLineSegment(sketch, "E309", {"start": v(0.4, 19.2) * mm, "end": v(0.46, 19.18) * mm});
            skLineSegment(sketch, "E310", {"start": v(0.46, 19.18) * mm, "end": v(0.53, 19.16) * mm});
            skLineSegment(sketch, "E311", {"start": v(0.53, 19.16) * mm, "end": v(0.59, 19.13) * mm});
            skLineSegment(sketch, "E312", {"start": v(0.59, 19.13) * mm, "end": v(0.65, 19.1) * mm});
            skLineSegment(sketch, "E313", {"start": v(0.65, 19.1) * mm, "end": v(0.7, 19.08) * mm});
            skLineSegment(sketch, "E314", {"start": v(0.7, 19.08) * mm, "end": v(0.76, 19.05) * mm});
            skLineSegment(sketch, "E315", {"start": v(0.76, 19.05) * mm, "end": v(0.82, 19.01) * mm});
            skLineSegment(sketch, "E316", {"start": v(0.82, 19.01) * mm, "end": v(0.87, 18.98) * mm});
            skLineSegment(sketch, "E317", {"start": v(0.87, 18.98) * mm, "end": v(0.92, 18.94) * mm});
            skLineSegment(sketch, "E318", {"start": v(0.92, 18.94) * mm, "end": v(0.97, 18.9) * mm});
            skLineSegment(sketch, "E319", {"start": v(0.97, 18.9) * mm, "end": v(1.01, 18.86) * mm});
            skLineSegment(sketch, "E320", {"start": v(1.01, 18.86) * mm, "end": v(1.06, 18.82) * mm});
            skLineSegment(sketch, "E321", {"start": v(1.06, 18.82) * mm, "end": v(1.1, 18.78) * mm});
            skLineSegment(sketch, "E322", {"start": v(1.1, 18.78) * mm, "end": v(1.14, 18.73) * mm});
            skLineSegment(sketch, "E323", {"start": v(1.14, 18.73) * mm, "end": v(1.18, 18.68) * mm});
            skLineSegment(sketch, "E324", {"start": v(1.18, 18.68) * mm, "end": v(1.22, 18.63) * mm});
            skLineSegment(sketch, "E325", {"start": v(1.22, 18.63) * mm, "end": v(1.25, 18.58) * mm});
            skLineSegment(sketch, "E326", {"start": v(1.25, 18.58) * mm, "end": v(1.29, 18.53) * mm});
            skLineSegment(sketch, "E327", {"start": v(1.29, 18.53) * mm, "end": v(1.32, 18.47) * mm});
            skLineSegment(sketch, "E328", {"start": v(1.32, 18.47) * mm, "end": v(1.35, 18.41) * mm});
            skLineSegment(sketch, "E329", {"start": v(1.35, 18.41) * mm, "end": v(1.37, 18.35) * mm});
            skLineSegment(sketch, "E330", {"start": v(1.37, 18.35) * mm, "end": v(1.4, 18.3) * mm});
            skLineSegment(sketch, "E331", {"start": v(1.4, 18.3) * mm, "end": v(1.42, 18.23) * mm});
            skLineSegment(sketch, "E332", {"start": v(1.42, 18.23) * mm, "end": v(1.44, 18.17) * mm});
            skLineSegment(sketch, "E333", {"start": v(1.44, 18.17) * mm, "end": v(1.46, 18.1) * mm});
            skLineSegment(sketch, "E334", {"start": v(1.46, 18.1) * mm, "end": v(1.47, 18.04) * mm});
            skLineSegment(sketch, "E335", {"start": v(1.47, 18.04) * mm, "end": v(1.49, 17.97) * mm});
            skLineSegment(sketch, "E336", {"start": v(1.49, 17.97) * mm, "end": v(1.5, 17.9) * mm});
            skLineSegment(sketch, "E337", {"start": v(1.5, 17.9) * mm, "end": v(1.5, 17.83) * mm});
            skLineSegment(sketch, "E338", {"start": v(1.5, 17.83) * mm, "end": v(1.51, 17.76) * mm});
            skLineSegment(sketch, "E339", {"start": v(1.51, 17.76) * mm, "end": v(1.52, 17.69) * mm});
            skLineSegment(sketch, "E340", {"start": v(1.52, 17.69) * mm, "end": v(1.52, 17.61) * mm});
            skLineSegment(sketch, "E341", {"start": v(1.52, 17.61) * mm, "end": v(1.52, 17.54) * mm});
            skLineSegment(sketch, "E342", {"start": v(1.52, 17.54) * mm, "end": v(1.51, 17.47) * mm});
            skLineSegment(sketch, "E343", {"start": v(1.51, 17.47) * mm, "end": v(1.5, 17.4) * mm});
            skLineSegment(sketch, "E344", {"start": v(1.5, 17.4) * mm, "end": v(1.5, 17.32) * mm});
            skLineSegment(sketch, "E345", {"start": v(1.5, 17.32) * mm, "end": v(1.48, 17.25) * mm});
            skLineSegment(sketch, "E346", {"start": v(1.48, 17.25) * mm, "end": v(1.46, 17.18) * mm});
            skLineSegment(sketch, "E347", {"start": v(1.46, 17.18) * mm, "end": v(1.44, 17.11) * mm});
            skLineSegment(sketch, "E348", {"start": v(1.44, 17.11) * mm, "end": v(1.42, 17.05) * mm});
            skLineSegment(sketch, "E349", {"start": v(1.42, 17.05) * mm, "end": v(1.4, 16.98) * mm});
            skLineSegment(sketch, "E350", {"start": v(1.4, 16.98) * mm, "end": v(1.37, 16.91) * mm});
            skLineSegment(sketch, "E351", {"start": v(1.37, 16.91) * mm, "end": v(1.34, 16.85) * mm});
            skLineSegment(sketch, "E352", {"start": v(1.34, 16.85) * mm, "end": v(1.3, 16.79) * mm});
            skLineSegment(sketch, "E353", {"start": v(1.3, 16.79) * mm, "end": v(1.27, 16.72) * mm});
            skLineSegment(sketch, "E354", {"start": v(1.27, 16.72) * mm, "end": v(1.24, 16.66) * mm});
            skLineSegment(sketch, "E355", {"start": v(1.24, 16.66) * mm, "end": v(1.2, 16.6) * mm});
            skLineSegment(sketch, "E356", {"start": v(1.2, 16.6) * mm, "end": v(1.16, 16.54) * mm});
            skLineSegment(sketch, "E357", {"start": v(1.16, 16.54) * mm, "end": v(1.12, 16.48) * mm});
            skLineSegment(sketch, "E358", {"start": v(1.12, 16.48) * mm, "end": v(1.07, 16.42) * mm});
            skLineSegment(sketch, "E359", {"start": v(1.07, 16.42) * mm, "end": v(1.03, 16.36) * mm});
            skLineSegment(sketch, "E360", {"start": v(1.03, 16.36) * mm, "end": v(0.98, 16.3) * mm});
            skLineSegment(sketch, "E361", {"start": v(0.98, 16.3) * mm, "end": v(-1.41, 13.44) * mm});
            skLineSegment(sketch, "E362", {"start": v(-1.41, 13.44) * mm, "end": v(-1.42, 13.43) * mm});
            skLineSegment(sketch, "E363", {"start": v(-1.42, 13.43) * mm, "end": v(-1.43, 13.42) * mm});
            skLineSegment(sketch, "E364", {"start": v(-1.43, 13.42) * mm, "end": v(-1.43, 13.4) * mm});
            skLineSegment(sketch, "E365", {"start": v(-1.43, 13.4) * mm, "end": v(-1.44, 13.4) * mm});
            skLineSegment(sketch, "E366", {"start": v(-1.44, 13.4) * mm, "end": v(-1.44, 13.39) * mm});
            skLineSegment(sketch, "E367", {"start": v(-1.44, 13.39) * mm, "end": v(-1.45, 13.38) * mm});
            skLineSegment(sketch, "E368", {"start": v(-1.45, 13.38) * mm, "end": v(-1.45, 13.37) * mm});
            skLineSegment(sketch, "E369", {"start": v(-1.45, 13.37) * mm, "end": v(-1.46, 13.36) * mm});
            skLineSegment(sketch, "E370", {"start": v(-1.46, 13.36) * mm, "end": v(-1.46, 13.35) * mm});
            skLineSegment(sketch, "E371", {"start": v(-1.46, 13.35) * mm, "end": v(-1.46, 13.34) * mm});
            skLineSegment(sketch, "E372", {"start": v(-1.46, 13.34) * mm, "end": v(-1.46, 13.33) * mm});
            skLineSegment(sketch, "E373", {"start": v(-1.46, 13.33) * mm, "end": v(-1.47, 13.32) * mm});
            skLineSegment(sketch, "E374", {"start": v(-1.47, 13.32) * mm, "end": v(-1.47, 13.31) * mm});
            skLineSegment(sketch, "E375", {"start": v(-1.47, 13.31) * mm, "end": v(-1.47, 13.3) * mm});
            skLineSegment(sketch, "E376", {"start": v(-1.47, 13.3) * mm, "end": v(-1.47, 13.3) * mm});
            skLineSegment(sketch, "E377", {"start": v(-1.47, 13.3) * mm, "end": v(-1.47, 13.29) * mm});
            skLineSegment(sketch, "E378", {"start": v(-1.47, 13.29) * mm, "end": v(-1.47, 13.27) * mm});
            skLineSegment(sketch, "E379", {"start": v(-1.47, 13.27) * mm, "end": v(-1.47, 13.26) * mm});
            skLineSegment(sketch, "E380", {"start": v(-1.47, 13.26) * mm, "end": v(-1.47, 13.25) * mm});
            skLineSegment(sketch, "E381", {"start": v(-1.47, 13.25) * mm, "end": v(-1.47, 13.24) * mm});
            skLineSegment(sketch, "E382", {"start": v(-1.47, 13.24) * mm, "end": v(-1.47, 13.22) * mm});
            skLineSegment(sketch, "E383", {"start": v(-1.47, 13.22) * mm, "end": v(-1.47, 13.2) * mm});
            skLineSegment(sketch, "E384", {"start": v(-1.47, 13.2) * mm, "end": v(-1.47, 13.19) * mm});
            skLineSegment(sketch, "E385", {"start": v(-1.47, 13.19) * mm, "end": v(-1.46, 13.17) * mm});
            skLineSegment(sketch, "E386", {"start": v(-1.46, 13.17) * mm, "end": v(-1.45, 13.16) * mm});
            skLineSegment(sketch, "E387", {"start": v(-1.45, 13.16) * mm, "end": v(-1.45, 13.14) * mm});
            skLineSegment(sketch, "E388", {"start": v(-1.45, 13.14) * mm, "end": v(-1.44, 13.13) * mm});
            skLineSegment(sketch, "E389", {"start": v(-1.44, 13.13) * mm, "end": v(-1.42, 13.12) * mm});
            skLineSegment(sketch, "E390", {"start": v(-1.42, 13.12) * mm, "end": v(-1.41, 13.1) * mm});
            skLineSegment(sketch, "E391", {"start": v(-1.41, 13.1) * mm, "end": v(-1.4, 13.1) * mm});
            skLineSegment(sketch, "E392", {"start": v(-1.4, 13.1) * mm, "end": v(-1.38, 13.1) * mm});
            skLineSegment(sketch, "E393", {"start": v(-1.38, 13.1) * mm, "end": v(-1.37, 13.08) * mm});
            skLineSegment(sketch, "E394", {"start": v(-1.37, 13.08) * mm, "end": v(-1.35, 13.08) * mm});
            skLineSegment(sketch, "E395", {"start": v(-1.35, 13.08) * mm, "end": v(-1.33, 13.07) * mm});
            skLineSegment(sketch, "E396", {"start": v(-1.33, 13.07) * mm, "end": v(-1.31, 13.06) * mm});
            skLineSegment(sketch, "E397", {"start": v(-1.31, 13.06) * mm, "end": v(-1.3, 13.06) * mm});
            skLineSegment(sketch, "E398", {"start": v(-1.3, 13.06) * mm, "end": v(-1.27, 13.06) * mm});
            skLineSegment(sketch, "E399", {"start": v(-1.27, 13.06) * mm, "end": v(-1.25, 13.06) * mm});
            skLineSegment(sketch, "E400", {"start": v(-1.25, 13.06) * mm, "end": v(-1.22, 13.05) * mm});
            skLineSegment(sketch, "E401", {"start": v(-1.22, 13.05) * mm, "end": v(-1.2, 13.05) * mm});
            skLineSegment(sketch, "E402", {"start": v(-1.2, 13.05) * mm, "end": v(1.62, 13.06) * mm});
            skLineSegment(sketch, "E403", {"start": v(1.62, 13.06) * mm, "end": v(1.62, 12.66) * mm});
            skLineSegment(sketch, "E404", {"start": v(1.62, 12.66) * mm, "end": v(-1.2, 12.65) * mm});
            skLineSegment(sketch, "E405", {"start": v(20.52, 15.68) * mm, "end": v(19.9, 15.68) * mm});
            skLineSegment(sketch, "E406", {"start": v(19.9, 15.68) * mm, "end": v(19.9, 16.08) * mm});
            skLineSegment(sketch, "E407", {"start": v(19.9, 16.08) * mm, "end": v(20.52, 16.08) * mm});
            skLineSegment(sketch, "E408", {"start": v(20.52, 16.08) * mm, "end": v(20.58, 16.08) * mm});
            skLineSegment(sketch, "E409", {"start": v(20.58, 16.08) * mm, "end": v(20.64, 16.08) * mm});
            skLineSegment(sketch, "E410", {"start": v(20.64, 16.08) * mm, "end": v(20.7, 16.09) * mm});
            skLineSegment(sketch, "E411", {"start": v(20.7, 16.09) * mm, "end": v(20.75, 16.1) * mm});
            skLineSegment(sketch, "E412", {"start": v(20.75, 16.1) * mm, "end": v(20.8, 16.1) * mm});
            skLineSegment(sketch, "E413", {"start": v(20.8, 16.1) * mm, "end": v(20.87, 16.12) * mm});
            skLineSegment(sketch, "E414", {"start": v(20.87, 16.12) * mm, "end": v(20.92, 16.14) * mm});
            skLineSegment(sketch, "E415", {"start": v(20.92, 16.14) * mm, "end": v(20.98, 16.15) * mm});
            skLineSegment(sketch, "E416", {"start": v(20.98, 16.15) * mm, "end": v(21.04, 16.17) * mm});
            skLineSegment(sketch, "E417", {"start": v(21.04, 16.17) * mm, "end": v(21.1, 16.2) * mm});
            skLineSegment(sketch, "E418", {"start": v(21.1, 16.2) * mm, "end": v(21.15, 16.22) * mm});
            skLineSegment(sketch, "E419", {"start": v(21.15, 16.22) * mm, "end": v(21.2, 16.25) * mm});
            skLineSegment(sketch, "E420", {"start": v(21.2, 16.25) * mm, "end": v(21.26, 16.28) * mm});
            skLineSegment(sketch, "E421", {"start": v(21.26, 16.28) * mm, "end": v(21.3, 16.3) * mm});
            skLineSegment(sketch, "E422", {"start": v(21.3, 16.3) * mm, "end": v(21.36, 16.34) * mm});
            skLineSegment(sketch, "E423", {"start": v(21.36, 16.34) * mm, "end": v(21.4, 16.38) * mm});
            skLineSegment(sketch, "E424", {"start": v(21.4, 16.38) * mm, "end": v(21.45, 16.42) * mm});
            skLineSegment(sketch, "E425", {"start": v(21.45, 16.42) * mm, "end": v(21.5, 16.46) * mm});
            skLineSegment(sketch, "E426", {"start": v(21.5, 16.46) * mm, "end": v(21.54, 16.5) * mm});
            skLineSegment(sketch, "E427", {"start": v(21.54, 16.5) * mm, "end": v(21.58, 16.55) * mm});
            skLineSegment(sketch, "E428", {"start": v(21.58, 16.55) * mm, "end": v(21.6, 16.58) * mm});
            skLineSegment(sketch, "E429", {"start": v(21.6, 16.58) * mm, "end": v(21.63, 16.62) * mm});
            skLineSegment(sketch, "E430", {"start": v(21.63, 16.62) * mm, "end": v(21.66, 16.65) * mm});
            skLineSegment(sketch, "E431", {"start": v(21.66, 16.65) * mm, "end": v(21.68, 16.69) * mm});
            skLineSegment(sketch, "E432", {"start": v(21.68, 16.69) * mm, "end": v(21.7, 16.72) * mm});
            skLineSegment(sketch, "E433", {"start": v(21.7, 16.72) * mm, "end": v(21.72, 16.76) * mm});
            skLineSegment(sketch, "E434", {"start": v(21.72, 16.76) * mm, "end": v(21.74, 16.8) * mm});
            skLineSegment(sketch, "E435", {"start": v(21.74, 16.8) * mm, "end": v(21.76, 16.84) * mm});
            skLineSegment(sketch, "E436", {"start": v(21.76, 16.84) * mm, "end": v(21.78, 16.88) * mm});
            skLineSegment(sketch, "E437", {"start": v(21.78, 16.88) * mm, "end": v(21.8, 16.92) * mm});
            skLineSegment(sketch, "E438", {"start": v(21.8, 16.92) * mm, "end": v(21.8, 16.96) * mm});
            skLineSegment(sketch, "E439", {"start": v(21.8, 16.96) * mm, "end": v(21.82, 17) * mm});
            skLineSegment(sketch, "E440", {"start": v(21.82, 17) * mm, "end": v(21.83, 17.05) * mm});
            skLineSegment(sketch, "E441", {"start": v(21.83, 17.05) * mm, "end": v(21.84, 17.09) * mm});
            skLineSegment(sketch, "E442", {"start": v(21.84, 17.09) * mm, "end": v(21.85, 17.13) * mm});
            skLineSegment(sketch, "E443", {"start": v(21.85, 17.13) * mm, "end": v(21.86, 17.18) * mm});
            skLineSegment(sketch, "E444", {"start": v(21.86, 17.18) * mm, "end": v(21.86, 17.22) * mm});
            skLineSegment(sketch, "E445", {"start": v(21.86, 17.22) * mm, "end": v(21.87, 17.27) * mm});
            skLineSegment(sketch, "E446", {"start": v(21.87, 17.27) * mm, "end": v(21.87, 17.32) * mm});
            skLineSegment(sketch, "E447", {"start": v(21.87, 17.32) * mm, "end": v(21.87, 17.36) * mm});
            skLineSegment(sketch, "E448", {"start": v(21.87, 17.36) * mm, "end": v(21.87, 17.42) * mm});
            skLineSegment(sketch, "E449", {"start": v(21.87, 17.42) * mm, "end": v(21.87, 17.48) * mm});
            skLineSegment(sketch, "E450", {"start": v(21.87, 17.48) * mm, "end": v(21.86, 17.54) * mm});
            skLineSegment(sketch, "E451", {"start": v(21.86, 17.54) * mm, "end": v(21.85, 17.6) * mm});
            skLineSegment(sketch, "E452", {"start": v(21.85, 17.6) * mm, "end": v(21.84, 17.65) * mm});
            skLineSegment(sketch, "E453", {"start": v(21.84, 17.65) * mm, "end": v(21.83, 17.7) * mm});
            skLineSegment(sketch, "E454", {"start": v(21.83, 17.7) * mm, "end": v(21.82, 17.76) * mm});
            skLineSegment(sketch, "E455", {"start": v(21.82, 17.76) * mm, "end": v(21.8, 17.81) * mm});
            skLineSegment(sketch, "E456", {"start": v(21.8, 17.81) * mm, "end": v(21.79, 17.86) * mm});
            skLineSegment(sketch, "E457", {"start": v(21.79, 17.86) * mm, "end": v(21.77, 17.91) * mm});
            skLineSegment(sketch, "E458", {"start": v(21.77, 17.91) * mm, "end": v(21.75, 17.96) * mm});
            skLineSegment(sketch, "E459", {"start": v(21.75, 17.96) * mm, "end": v(21.72, 18) * mm});
            skLineSegment(sketch, "E460", {"start": v(21.72, 18) * mm, "end": v(21.7, 18.05) * mm});
            skLineSegment(sketch, "E461", {"start": v(21.7, 18.05) * mm, "end": v(21.67, 18.1) * mm});
            skLineSegment(sketch, "E462", {"start": v(21.67, 18.1) * mm, "end": v(21.65, 18.14) * mm});
            skLineSegment(sketch, "E463", {"start": v(21.65, 18.14) * mm, "end": v(21.62, 18.18) * mm});
            skLineSegment(sketch, "E464", {"start": v(21.62, 18.18) * mm, "end": v(21.58, 18.22) * mm});
            skLineSegment(sketch, "E465", {"start": v(21.58, 18.22) * mm, "end": v(21.55, 18.26) * mm});
            skLineSegment(sketch, "E466", {"start": v(21.55, 18.26) * mm, "end": v(21.51, 18.3) * mm});
            skLineSegment(sketch, "E467", {"start": v(21.51, 18.3) * mm, "end": v(21.48, 18.33) * mm});
            skLineSegment(sketch, "E468", {"start": v(21.48, 18.33) * mm, "end": v(21.44, 18.36) * mm});
            skLineSegment(sketch, "E469", {"start": v(21.44, 18.36) * mm, "end": v(21.4, 18.4) * mm});
            skLineSegment(sketch, "E470", {"start": v(21.4, 18.4) * mm, "end": v(21.37, 18.42) * mm});
            skLineSegment(sketch, "E471", {"start": v(21.37, 18.42) * mm, "end": v(21.33, 18.45) * mm});
            skLineSegment(sketch, "E472", {"start": v(21.33, 18.45) * mm, "end": v(21.29, 18.47) * mm});
            skLineSegment(sketch, "E473", {"start": v(21.29, 18.47) * mm, "end": v(21.24, 18.5) * mm});
            skLineSegment(sketch, "E474", {"start": v(21.24, 18.5) * mm, "end": v(21.2, 18.52) * mm});
            skLineSegment(sketch, "E475", {"start": v(21.2, 18.52) * mm, "end": v(21.16, 18.54) * mm});
            skLineSegment(sketch, "E476", {"start": v(21.16, 18.54) * mm, "end": v(21.1, 18.56) * mm});
            skLineSegment(sketch, "E477", {"start": v(21.1, 18.56) * mm, "end": v(21.06, 18.58) * mm});
            skLineSegment(sketch, "E478", {"start": v(21.06, 18.58) * mm, "end": v(21.01, 18.6) * mm});
            skLineSegment(sketch, "E479", {"start": v(21.01, 18.6) * mm, "end": v(20.96, 18.6) * mm});
            skLineSegment(sketch, "E480", {"start": v(20.96, 18.6) * mm, "end": v(20.91, 18.62) * mm});
            skLineSegment(sketch, "E481", {"start": v(20.91, 18.62) * mm, "end": v(20.86, 18.63) * mm});
            skLineSegment(sketch, "E482", {"start": v(20.86, 18.63) * mm, "end": v(20.8, 18.64) * mm});
            skLineSegment(sketch, "E483", {"start": v(20.8, 18.64) * mm, "end": v(20.75, 18.65) * mm});
            skLineSegment(sketch, "E484", {"start": v(20.75, 18.65) * mm, "end": v(20.7, 18.65) * mm});
            skLineSegment(sketch, "E485", {"start": v(20.7, 18.65) * mm, "end": v(20.64, 18.66) * mm});
            skLineSegment(sketch, "E486", {"start": v(20.64, 18.66) * mm, "end": v(20.58, 18.66) * mm});
            skLineSegment(sketch, "E487", {"start": v(20.58, 18.66) * mm, "end": v(20.52, 18.66) * mm});
            skLineSegment(sketch, "E488", {"start": v(20.52, 18.66) * mm, "end": v(20.47, 18.66) * mm});
            skLineSegment(sketch, "E489", {"start": v(20.47, 18.66) * mm, "end": v(20.43, 18.66) * mm});
            skLineSegment(sketch, "E490", {"start": v(20.43, 18.66) * mm, "end": v(20.38, 18.65) * mm});
            skLineSegment(sketch, "E491", {"start": v(20.38, 18.65) * mm, "end": v(20.33, 18.65) * mm});
            skLineSegment(sketch, "E492", {"start": v(20.33, 18.65) * mm, "end": v(20.3, 18.65) * mm});
            skLineSegment(sketch, "E493", {"start": v(20.3, 18.65) * mm, "end": v(20.25, 18.64) * mm});
            skLineSegment(sketch, "E494", {"start": v(20.25, 18.64) * mm, "end": v(20.2, 18.63) * mm});
            skLineSegment(sketch, "E495", {"start": v(20.2, 18.63) * mm, "end": v(20.16, 18.62) * mm});
            skLineSegment(sketch, "E496", {"start": v(20.16, 18.62) * mm, "end": v(20.12, 18.61) * mm});
            skLineSegment(sketch, "E497", {"start": v(20.12, 18.61) * mm, "end": v(20.08, 18.6) * mm});
            skLineSegment(sketch, "E498", {"start": v(20.08, 18.6) * mm, "end": v(20.04, 18.6) * mm});
            skLineSegment(sketch, "E499", {"start": v(20.04, 18.6) * mm, "end": v(20, 18.58) * mm});
            skLineSegment(sketch, "E500", {"start": v(20, 18.58) * mm, "end": v(19.97, 18.57) * mm});
            skLineSegment(sketch, "E501", {"start": v(19.97, 18.57) * mm, "end": v(19.93, 18.55) * mm});
            skLineSegment(sketch, "E502", {"start": v(19.93, 18.55) * mm, "end": v(19.9, 18.54) * mm});
            skLineSegment(sketch, "E503", {"start": v(19.9, 18.54) * mm, "end": v(19.86, 18.52) * mm});
            skLineSegment(sketch, "E504", {"start": v(19.86, 18.52) * mm, "end": v(19.83, 18.5) * mm});
            skLineSegment(sketch, "E505", {"start": v(19.83, 18.5) * mm, "end": v(19.8, 18.49) * mm});
            skLineSegment(sketch, "E506", {"start": v(19.8, 18.49) * mm, "end": v(19.77, 18.47) * mm});
            skLineSegment(sketch, "E507", {"start": v(19.77, 18.47) * mm, "end": v(19.74, 18.45) * mm});
            skLineSegment(sketch, "E508", {"start": v(19.74, 18.45) * mm, "end": v(19.7, 18.43) * mm});
            skLineSegment(sketch, "E509", {"start": v(19.7, 18.43) * mm, "end": v(19.66, 18.4) * mm});
            skLineSegment(sketch, "E510", {"start": v(19.66, 18.4) * mm, "end": v(19.63, 18.37) * mm});
            skLineSegment(sketch, "E511", {"start": v(19.63, 18.37) * mm, "end": v(19.6, 18.34) * mm});
            skLineSegment(sketch, "E512", {"start": v(19.6, 18.34) * mm, "end": v(19.56, 18.31) * mm});
            skLineSegment(sketch, "E513", {"start": v(19.56, 18.31) * mm, "end": v(19.53, 18.28) * mm});
            skLineSegment(sketch, "E514", {"start": v(19.53, 18.28) * mm, "end": v(19.5, 18.25) * mm});
            skLineSegment(sketch, "E515", {"start": v(19.5, 18.25) * mm, "end": v(19.48, 18.22) * mm});
            skLineSegment(sketch, "E516", {"start": v(19.48, 18.22) * mm, "end": v(19.45, 18.18) * mm});
            skLineSegment(sketch, "E517", {"start": v(19.45, 18.18) * mm, "end": v(19.42, 18.14) * mm});
            skLineSegment(sketch, "E518", {"start": v(19.42, 18.14) * mm, "end": v(19.4, 18.1) * mm});
            skLineSegment(sketch, "E519", {"start": v(19.4, 18.1) * mm, "end": v(19.37, 18.07) * mm});
            skLineSegment(sketch, "E520", {"start": v(19.37, 18.07) * mm, "end": v(19.35, 18.03) * mm});
            skLineSegment(sketch, "E521", {"start": v(19.35, 18.03) * mm, "end": v(19.33, 18) * mm});
            skLineSegment(sketch, "E522", {"start": v(19.33, 18) * mm, "end": v(19.3, 17.96) * mm});
            skLineSegment(sketch, "E523", {"start": v(19.3, 17.96) * mm, "end": v(19.29, 17.93) * mm});
            skLineSegment(sketch, "E524", {"start": v(19.29, 17.93) * mm, "end": v(19.27, 17.9) * mm});
            skLineSegment(sketch, "E525", {"start": v(19.27, 17.9) * mm, "end": v(19.25, 17.86) * mm});
            skLineSegment(sketch, "E526", {"start": v(19.25, 17.86) * mm, "end": v(19.23, 17.82) * mm});
            skLineSegment(sketch, "E527", {"start": v(19.23, 17.82) * mm, "end": v(19.21, 17.79) * mm});
            skLineSegment(sketch, "E528", {"start": v(19.21, 17.79) * mm, "end": v(18.86, 17.96) * mm});
            skLineSegment(sketch, "E529", {"start": v(18.86, 17.96) * mm, "end": v(18.88, 18) * mm});
            skLineSegment(sketch, "E530", {"start": v(18.88, 18) * mm, "end": v(18.9, 18.06) * mm});
            skLineSegment(sketch, "E531", {"start": v(18.9, 18.06) * mm, "end": v(18.93, 18.1) * mm});
            skLineSegment(sketch, "E532", {"start": v(18.93, 18.1) * mm, "end": v(18.96, 18.16) * mm});
            skLineSegment(sketch, "E533", {"start": v(18.96, 18.16) * mm, "end": v(18.98, 18.2) * mm});
            skLineSegment(sketch, "E534", {"start": v(18.98, 18.2) * mm, "end": v(19, 18.25) * mm});
            skLineSegment(sketch, "E535", {"start": v(19, 18.25) * mm, "end": v(19.04, 18.3) * mm});
            skLineSegment(sketch, "E536", {"start": v(19.04, 18.3) * mm, "end": v(19.07, 18.34) * mm});
            skLineSegment(sketch, "E537", {"start": v(19.07, 18.34) * mm, "end": v(19.1, 18.38) * mm});
            skLineSegment(sketch, "E538", {"start": v(19.1, 18.38) * mm, "end": v(19.13, 18.42) * mm});
            skLineSegment(sketch, "E539", {"start": v(19.13, 18.42) * mm, "end": v(19.16, 18.46) * mm});
            skLineSegment(sketch, "E540", {"start": v(19.16, 18.46) * mm, "end": v(19.2, 18.5) * mm});
            skLineSegment(sketch, "E541", {"start": v(19.2, 18.5) * mm, "end": v(19.23, 18.54) * mm});
            skLineSegment(sketch, "E542", {"start": v(19.23, 18.54) * mm, "end": v(19.26, 18.57) * mm});
            skLineSegment(sketch, "E543", {"start": v(19.26, 18.57) * mm, "end": v(19.3, 18.6) * mm});
            skLineSegment(sketch, "E544", {"start": v(19.3, 18.6) * mm, "end": v(19.34, 18.64) * mm});
            skLineSegment(sketch, "E545", {"start": v(19.34, 18.64) * mm, "end": v(19.37, 18.68) * mm});
            skLineSegment(sketch, "E546", {"start": v(19.37, 18.68) * mm, "end": v(19.41, 18.7) * mm});
            skLineSegment(sketch, "E547", {"start": v(19.41, 18.7) * mm, "end": v(19.45, 18.74) * mm});
            skLineSegment(sketch, "E548", {"start": v(19.45, 18.74) * mm, "end": v(19.5, 18.77) * mm});
            skLineSegment(sketch, "E549", {"start": v(19.5, 18.77) * mm, "end": v(19.54, 18.8) * mm});
            skLineSegment(sketch, "E550", {"start": v(19.54, 18.8) * mm, "end": v(19.58, 18.83) * mm});
            skLineSegment(sketch, "E551", {"start": v(19.58, 18.83) * mm, "end": v(19.63, 18.85) * mm});
            skLineSegment(sketch, "E552", {"start": v(19.63, 18.85) * mm, "end": v(19.67, 18.88) * mm});
            skLineSegment(sketch, "E553", {"start": v(19.67, 18.88) * mm, "end": v(19.72, 18.9) * mm});
            skLineSegment(sketch, "E554", {"start": v(19.72, 18.9) * mm, "end": v(19.77, 18.92) * mm});
            skLineSegment(sketch, "E555", {"start": v(19.77, 18.92) * mm, "end": v(19.82, 18.94) * mm});
            skLineSegment(sketch, "E556", {"start": v(19.82, 18.94) * mm, "end": v(19.87, 18.96) * mm});
            skLineSegment(sketch, "E557", {"start": v(19.87, 18.96) * mm, "end": v(19.92, 18.98) * mm});
            skLineSegment(sketch, "E558", {"start": v(19.92, 18.98) * mm, "end": v(19.97, 19) * mm});
            skLineSegment(sketch, "E559", {"start": v(19.97, 19) * mm, "end": v(20.02, 19) * mm});
            skLineSegment(sketch, "E560", {"start": v(20.02, 19) * mm, "end": v(20.08, 19.02) * mm});
            skLineSegment(sketch, "E561", {"start": v(20.08, 19.02) * mm, "end": v(20.13, 19.03) * mm});
            skLineSegment(sketch, "E562", {"start": v(20.13, 19.03) * mm, "end": v(20.18, 19.04) * mm});
            skLineSegment(sketch, "E563", {"start": v(20.18, 19.04) * mm, "end": v(20.24, 19.05) * mm});
            skLineSegment(sketch, "E564", {"start": v(20.24, 19.05) * mm, "end": v(20.3, 19.06) * mm});
            skLineSegment(sketch, "E565", {"start": v(20.3, 19.06) * mm, "end": v(20.35, 19.06) * mm});
            skLineSegment(sketch, "E566", {"start": v(20.35, 19.06) * mm, "end": v(20.4, 19.07) * mm});
            skLineSegment(sketch, "E567", {"start": v(20.4, 19.07) * mm, "end": v(20.46, 19.07) * mm});
            skLineSegment(sketch, "E568", {"start": v(20.46, 19.07) * mm, "end": v(20.52, 19.07) * mm});
            skLineSegment(sketch, "E569", {"start": v(20.52, 19.07) * mm, "end": v(20.6, 19.07) * mm});
            skLineSegment(sketch, "E570", {"start": v(20.6, 19.07) * mm, "end": v(20.67, 19.06) * mm});
            skLineSegment(sketch, "E571", {"start": v(20.67, 19.06) * mm, "end": v(20.75, 19.06) * mm});
            skLineSegment(sketch, "E572", {"start": v(20.75, 19.06) * mm, "end": v(20.82, 19.05) * mm});
            skLineSegment(sketch, "E573", {"start": v(20.82, 19.05) * mm, "end": v(20.9, 19.04) * mm});
            skLineSegment(sketch, "E574", {"start": v(20.9, 19.04) * mm, "end": v(20.96, 19.03) * mm});
            skLineSegment(sketch, "E575", {"start": v(20.96, 19.03) * mm, "end": v(21.03, 19.01) * mm});
            skLineSegment(sketch, "E576", {"start": v(21.03, 19.01) * mm, "end": v(21.1, 19) * mm});
            skLineSegment(sketch, "E577", {"start": v(21.1, 19) * mm, "end": v(21.16, 18.98) * mm});
            skLineSegment(sketch, "E578", {"start": v(21.16, 18.98) * mm, "end": v(21.22, 18.95) * mm});
            skLineSegment(sketch, "E579", {"start": v(21.22, 18.95) * mm, "end": v(21.28, 18.93) * mm});
            skLineSegment(sketch, "E580", {"start": v(21.28, 18.93) * mm, "end": v(21.34, 18.9) * mm});
            skLineSegment(sketch, "E581", {"start": v(21.34, 18.9) * mm, "end": v(21.4, 18.88) * mm});
            skLineSegment(sketch, "E582", {"start": v(21.4, 18.88) * mm, "end": v(21.46, 18.84) * mm});
            skLineSegment(sketch, "E583", {"start": v(21.46, 18.84) * mm, "end": v(21.51, 18.81) * mm});
            skLineSegment(sketch, "E584", {"start": v(21.51, 18.81) * mm, "end": v(21.57, 18.78) * mm});
            skLineSegment(sketch, "E585", {"start": v(21.57, 18.78) * mm, "end": v(21.62, 18.74) * mm});
            skLineSegment(sketch, "E586", {"start": v(21.62, 18.74) * mm, "end": v(21.67, 18.7) * mm});
            skLineSegment(sketch, "E587", {"start": v(21.67, 18.7) * mm, "end": v(21.72, 18.66) * mm});
            skLineSegment(sketch, "E588", {"start": v(21.72, 18.66) * mm, "end": v(21.77, 18.62) * mm});
            skLineSegment(sketch, "E589", {"start": v(21.77, 18.62) * mm, "end": v(21.82, 18.57) * mm});
            skLineSegment(sketch, "E590", {"start": v(21.82, 18.57) * mm, "end": v(21.86, 18.52) * mm});
            skLineSegment(sketch, "E591", {"start": v(21.86, 18.52) * mm, "end": v(21.9, 18.47) * mm});
            skLineSegment(sketch, "E592", {"start": v(21.9, 18.47) * mm, "end": v(21.94, 18.42) * mm});
            skLineSegment(sketch, "E593", {"start": v(21.94, 18.42) * mm, "end": v(21.98, 18.37) * mm});
            skLineSegment(sketch, "E594", {"start": v(21.98, 18.37) * mm, "end": v(22.02, 18.31) * mm});
            skLineSegment(sketch, "E595", {"start": v(22.02, 18.31) * mm, "end": v(22.05, 18.26) * mm});
            skLineSegment(sketch, "E596", {"start": v(22.05, 18.26) * mm, "end": v(22.08, 18.2) * mm});
            skLineSegment(sketch, "E597", {"start": v(22.08, 18.2) * mm, "end": v(22.11, 18.14) * mm});
            skLineSegment(sketch, "E598", {"start": v(22.11, 18.14) * mm, "end": v(22.14, 18.07) * mm});
            skLineSegment(sketch, "E599", {"start": v(22.14, 18.07) * mm, "end": v(22.17, 18) * mm});
            skLineSegment(sketch, "E600", {"start": v(22.17, 18) * mm, "end": v(22.2, 17.94) * mm});
            skLineSegment(sketch, "E601", {"start": v(22.2, 17.94) * mm, "end": v(22.21, 17.87) * mm});
            skLineSegment(sketch, "E602", {"start": v(22.21, 17.87) * mm, "end": v(22.23, 17.8) * mm});
            skLineSegment(sketch, "E603", {"start": v(22.23, 17.8) * mm, "end": v(22.24, 17.74) * mm});
            skLineSegment(sketch, "E604", {"start": v(22.24, 17.74) * mm, "end": v(22.26, 17.66) * mm});
            skLineSegment(sketch, "E605", {"start": v(22.26, 17.66) * mm, "end": v(22.26, 17.6) * mm});
            skLineSegment(sketch, "E606", {"start": v(22.26, 17.6) * mm, "end": v(22.27, 17.52) * mm});
            skLineSegment(sketch, "E607", {"start": v(22.27, 17.52) * mm, "end": v(22.28, 17.44) * mm});
            skLineSegment(sketch, "E608", {"start": v(22.28, 17.44) * mm, "end": v(22.28, 17.36) * mm});
            skLineSegment(sketch, "E609", {"start": v(22.28, 17.36) * mm, "end": v(22.28, 17.3) * mm});
            skLineSegment(sketch, "E610", {"start": v(22.28, 17.3) * mm, "end": v(22.27, 17.24) * mm});
            skLineSegment(sketch, "E611", {"start": v(22.27, 17.24) * mm, "end": v(22.27, 17.18) * mm});
            skLineSegment(sketch, "E612", {"start": v(22.27, 17.18) * mm, "end": v(22.26, 17.12) * mm});
            skLineSegment(sketch, "E613", {"start": v(22.26, 17.12) * mm, "end": v(22.25, 17.07) * mm});
            skLineSegment(sketch, "E614", {"start": v(22.25, 17.07) * mm, "end": v(22.24, 17) * mm});
            skLineSegment(sketch, "E615", {"start": v(22.24, 17) * mm, "end": v(22.23, 16.95) * mm});
            skLineSegment(sketch, "E616", {"start": v(22.23, 16.95) * mm, "end": v(22.2, 16.9) * mm});
            skLineSegment(sketch, "E617", {"start": v(22.2, 16.9) * mm, "end": v(22.2, 16.84) * mm});
            skLineSegment(sketch, "E618", {"start": v(22.2, 16.84) * mm, "end": v(22.17, 16.79) * mm});
            skLineSegment(sketch, "E619", {"start": v(22.17, 16.79) * mm, "end": v(22.15, 16.73) * mm});
            skLineSegment(sketch, "E620", {"start": v(22.15, 16.73) * mm, "end": v(22.13, 16.68) * mm});
            skLineSegment(sketch, "E621", {"start": v(22.13, 16.68) * mm, "end": v(22.1, 16.63) * mm});
            skLineSegment(sketch, "E622", {"start": v(22.1, 16.63) * mm, "end": v(22.08, 16.58) * mm});
            skLineSegment(sketch, "E623", {"start": v(22.08, 16.58) * mm, "end": v(22.05, 16.53) * mm});
            skLineSegment(sketch, "E624", {"start": v(22.05, 16.53) * mm, "end": v(22.02, 16.48) * mm});
            skLineSegment(sketch, "E625", {"start": v(22.02, 16.48) * mm, "end": v(21.99, 16.43) * mm});
            skLineSegment(sketch, "E626", {"start": v(21.99, 16.43) * mm, "end": v(21.95, 16.38) * mm});
            skLineSegment(sketch, "E627", {"start": v(21.95, 16.38) * mm, "end": v(21.92, 16.34) * mm});
            skLineSegment(sketch, "E628", {"start": v(21.92, 16.34) * mm, "end": v(21.88, 16.3) * mm});
            skLineSegment(sketch, "E629", {"start": v(21.88, 16.3) * mm, "end": v(21.83, 16.24) * mm});
            skLineSegment(sketch, "E630", {"start": v(21.83, 16.24) * mm, "end": v(21.77, 16.18) * mm});
            skLineSegment(sketch, "E631", {"start": v(21.77, 16.18) * mm, "end": v(21.72, 16.13) * mm});
            skLineSegment(sketch, "E632", {"start": v(21.72, 16.13) * mm, "end": v(21.66, 16.08) * mm});
            skLineSegment(sketch, "E633", {"start": v(21.66, 16.08) * mm, "end": v(21.6, 16.04) * mm});
            skLineSegment(sketch, "E634", {"start": v(21.6, 16.04) * mm, "end": v(21.54, 16) * mm});
            skLineSegment(sketch, "E635", {"start": v(21.54, 16) * mm, "end": v(21.47, 15.95) * mm});
            skLineSegment(sketch, "E636", {"start": v(21.47, 15.95) * mm, "end": v(21.4, 15.91) * mm});
            skLineSegment(sketch, "E637", {"start": v(21.4, 15.91) * mm, "end": v(21.33, 15.88) * mm});
            skLineSegment(sketch, "E638", {"start": v(21.33, 15.88) * mm, "end": v(21.26, 15.85) * mm});
            skLineSegment(sketch, "E639", {"start": v(21.26, 15.85) * mm, "end": v(21.2, 15.82) * mm});
            skLineSegment(sketch, "E640", {"start": v(21.2, 15.82) * mm, "end": v(21.12, 15.79) * mm});
            skLineSegment(sketch, "E641", {"start": v(21.12, 15.79) * mm, "end": v(21.04, 15.76) * mm});
            skLineSegment(sketch, "E642", {"start": v(21.04, 15.76) * mm, "end": v(20.97, 15.74) * mm});
            skLineSegment(sketch, "E643", {"start": v(20.97, 15.74) * mm, "end": v(20.9, 15.72) * mm});
            skLineSegment(sketch, "E644", {"start": v(20.9, 15.72) * mm, "end": v(20.82, 15.7) * mm});
            skLineSegment(sketch, "E645", {"start": v(20.82, 15.7) * mm, "end": v(20.75, 15.7) * mm});
            skLineSegment(sketch, "E646", {"start": v(20.75, 15.7) * mm, "end": v(20.67, 15.69) * mm});
            skLineSegment(sketch, "E647", {"start": v(20.67, 15.69) * mm, "end": v(20.6, 15.68) * mm});
            skLineSegment(sketch, "E648", {"start": v(20.6, 15.68) * mm, "end": v(20.52, 15.68) * mm});
            skLineSegment(sketch, "E649", {"start": v(20.55, 12.31) * mm, "end": v(20.4, 12.32) * mm});
            skLineSegment(sketch, "E650", {"start": v(20.4, 12.32) * mm, "end": v(20.27, 12.33) * mm});
            skLineSegment(sketch, "E651", {"start": v(20.27, 12.33) * mm, "end": v(20.13, 12.35) * mm});
            skLineSegment(sketch, "E652", {"start": v(20.13, 12.35) * mm, "end": v(20, 12.38) * mm});
            skLineSegment(sketch, "E653", {"start": v(20, 12.38) * mm, "end": v(19.87, 12.42) * mm});
            skLineSegment(sketch, "E654", {"start": v(19.87, 12.42) * mm, "end": v(19.75, 12.47) * mm});
            skLineSegment(sketch, "E655", {"start": v(19.75, 12.47) * mm, "end": v(19.63, 12.52) * mm});
            skLineSegment(sketch, "E656", {"start": v(19.63, 12.52) * mm, "end": v(19.52, 12.58) * mm});
            skLineSegment(sketch, "E657", {"start": v(19.52, 12.58) * mm, "end": v(19.42, 12.66) * mm});
            skLineSegment(sketch, "E658", {"start": v(19.42, 12.66) * mm, "end": v(19.31, 12.74) * mm});
            skLineSegment(sketch, "E659", {"start": v(19.31, 12.74) * mm, "end": v(19.28, 12.77) * mm});
            skLineSegment(sketch, "E660", {"start": v(19.28, 12.77) * mm, "end": v(19.24, 12.8) * mm});
            skLineSegment(sketch, "E661", {"start": v(19.24, 12.8) * mm, "end": v(19.2, 12.83) * mm});
            skLineSegment(sketch, "E662", {"start": v(19.2, 12.83) * mm, "end": v(19.17, 12.87) * mm});
            skLineSegment(sketch, "E663", {"start": v(19.17, 12.87) * mm, "end": v(19.14, 12.9) * mm});
            skLineSegment(sketch, "E664", {"start": v(19.14, 12.9) * mm, "end": v(19.1, 12.94) * mm});
            skLineSegment(sketch, "E665", {"start": v(19.1, 12.94) * mm, "end": v(19.07, 12.98) * mm});
            skLineSegment(sketch, "E666", {"start": v(19.07, 12.98) * mm, "end": v(19.04, 13.02) * mm});
            skLineSegment(sketch, "E667", {"start": v(19.04, 13.02) * mm, "end": v(19, 13.05) * mm});
            skLineSegment(sketch, "E668", {"start": v(19, 13.05) * mm, "end": v(18.98, 13.1) * mm});
            skLineSegment(sketch, "E669", {"start": v(18.98, 13.1) * mm, "end": v(18.95, 13.14) * mm});
            skLineSegment(sketch, "E670", {"start": v(18.95, 13.14) * mm, "end": v(18.92, 13.18) * mm});
            skLineSegment(sketch, "E671", {"start": v(18.92, 13.18) * mm, "end": v(18.89, 13.22) * mm});
            skLineSegment(sketch, "E672", {"start": v(18.89, 13.22) * mm, "end": v(18.86, 13.27) * mm});
            skLineSegment(sketch, "E673", {"start": v(18.86, 13.27) * mm, "end": v(18.83, 13.32) * mm});
            skLineSegment(sketch, "E674", {"start": v(18.83, 13.32) * mm, "end": v(18.8, 13.37) * mm});
            skLineSegment(sketch, "E675", {"start": v(18.8, 13.37) * mm, "end": v(18.77, 13.42) * mm});
            skLineSegment(sketch, "E676", {"start": v(18.77, 13.42) * mm, "end": v(18.75, 13.47) * mm});
            skLineSegment(sketch, "E677", {"start": v(18.75, 13.47) * mm, "end": v(18.72, 13.52) * mm});
            skLineSegment(sketch, "E678", {"start": v(18.72, 13.52) * mm, "end": v(18.7, 13.58) * mm});
            skLineSegment(sketch, "E679", {"start": v(18.7, 13.58) * mm, "end": v(19.06, 13.75) * mm});
            skLineSegment(sketch, "E680", {"start": v(19.06, 13.75) * mm, "end": v(19.08, 13.7) * mm});
            skLineSegment(sketch, "E681", {"start": v(19.08, 13.7) * mm, "end": v(19.1, 13.67) * mm});
            skLineSegment(sketch, "E682", {"start": v(19.1, 13.67) * mm, "end": v(19.12, 13.63) * mm});
            skLineSegment(sketch, "E683", {"start": v(19.12, 13.63) * mm, "end": v(19.14, 13.6) * mm});
            skLineSegment(sketch, "E684", {"start": v(19.14, 13.6) * mm, "end": v(19.16, 13.55) * mm});
            skLineSegment(sketch, "E685", {"start": v(19.16, 13.55) * mm, "end": v(19.19, 13.52) * mm});
            skLineSegment(sketch, "E686", {"start": v(19.19, 13.52) * mm, "end": v(19.21, 13.48) * mm});
            skLineSegment(sketch, "E687", {"start": v(19.21, 13.48) * mm, "end": v(19.24, 13.44) * mm});
            skLineSegment(sketch, "E688", {"start": v(19.24, 13.44) * mm, "end": v(19.26, 13.4) * mm});
            skLineSegment(sketch, "E689", {"start": v(19.26, 13.4) * mm, "end": v(19.3, 13.36) * mm});
            skLineSegment(sketch, "E690", {"start": v(19.3, 13.36) * mm, "end": v(19.32, 13.32) * mm});
            skLineSegment(sketch, "E691", {"start": v(19.32, 13.32) * mm, "end": v(19.35, 13.29) * mm});
            skLineSegment(sketch, "E692", {"start": v(19.35, 13.29) * mm, "end": v(19.38, 13.25) * mm});
            skLineSegment(sketch, "E693", {"start": v(19.38, 13.25) * mm, "end": v(19.4, 13.22) * mm});
            skLineSegment(sketch, "E694", {"start": v(19.4, 13.22) * mm, "end": v(19.44, 13.18) * mm});
            skLineSegment(sketch, "E695", {"start": v(19.44, 13.18) * mm, "end": v(19.47, 13.15) * mm});
            skLineSegment(sketch, "E696", {"start": v(19.47, 13.15) * mm, "end": v(19.5, 13.12) * mm});
            skLineSegment(sketch, "E697", {"start": v(19.5, 13.12) * mm, "end": v(19.53, 13.1) * mm});
            skLineSegment(sketch, "E698", {"start": v(19.53, 13.1) * mm, "end": v(19.56, 13.07) * mm});
            skLineSegment(sketch, "E699", {"start": v(19.56, 13.07) * mm, "end": v(19.59, 13.04) * mm});
            skLineSegment(sketch, "E700", {"start": v(19.59, 13.04) * mm, "end": v(19.67, 12.98) * mm});
            skLineSegment(sketch, "E701", {"start": v(19.67, 12.98) * mm, "end": v(19.75, 12.92) * mm});
            skLineSegment(sketch, "E702", {"start": v(19.75, 12.92) * mm, "end": v(19.84, 12.87) * mm});
            skLineSegment(sketch, "E703", {"start": v(19.84, 12.87) * mm, "end": v(19.94, 12.83) * mm});
            skLineSegment(sketch, "E704", {"start": v(19.94, 12.83) * mm, "end": v(20.03, 12.8) * mm});
            skLineSegment(sketch, "E705", {"start": v(20.03, 12.8) * mm, "end": v(20.13, 12.77) * mm});
            skLineSegment(sketch, "E706", {"start": v(20.13, 12.77) * mm, "end": v(20.23, 12.74) * mm});
            skLineSegment(sketch, "E707", {"start": v(20.23, 12.74) * mm, "end": v(20.34, 12.73) * mm});
            skLineSegment(sketch, "E708", {"start": v(20.34, 12.73) * mm, "end": v(20.44, 12.72) * mm});
            skLineSegment(sketch, "E709", {"start": v(20.44, 12.72) * mm, "end": v(20.55, 12.71) * mm});
            skLineSegment(sketch, "E710", {"start": v(20.55, 12.71) * mm, "end": v(20.62, 12.72) * mm});
            skLineSegment(sketch, "E711", {"start": v(20.62, 12.72) * mm, "end": v(20.7, 12.72) * mm});
            skLineSegment(sketch, "E712", {"start": v(20.7, 12.72) * mm, "end": v(20.76, 12.72) * mm});
            skLineSegment(sketch, "E713", {"start": v(20.76, 12.72) * mm, "end": v(20.82, 12.73) * mm});
            skLineSegment(sketch, "E714", {"start": v(20.82, 12.73) * mm, "end": v(20.89, 12.74) * mm});
            skLineSegment(sketch, "E715", {"start": v(20.89, 12.74) * mm, "end": v(20.95, 12.76) * mm});
            skLineSegment(sketch, "E716", {"start": v(20.95, 12.76) * mm, "end": v(21.01, 12.77) * mm});
            skLineSegment(sketch, "E717", {"start": v(21.01, 12.77) * mm, "end": v(21.07, 12.79) * mm});
            skLineSegment(sketch, "E718", {"start": v(21.07, 12.79) * mm, "end": v(21.13, 12.8) * mm});
            skLineSegment(sketch, "E719", {"start": v(21.13, 12.8) * mm, "end": v(21.2, 12.83) * mm});
            skLineSegment(sketch, "E720", {"start": v(21.2, 12.83) * mm, "end": v(21.25, 12.86) * mm});
            skLineSegment(sketch, "E721", {"start": v(21.25, 12.86) * mm, "end": v(21.3, 12.88) * mm});
            skLineSegment(sketch, "E722", {"start": v(21.3, 12.88) * mm, "end": v(21.36, 12.91) * mm});
            skLineSegment(sketch, "E723", {"start": v(21.36, 12.91) * mm, "end": v(21.4, 12.94) * mm});
            skLineSegment(sketch, "E724", {"start": v(21.4, 12.94) * mm, "end": v(21.46, 12.98) * mm});
            skLineSegment(sketch, "E725", {"start": v(21.46, 12.98) * mm, "end": v(21.5, 13.01) * mm});
            skLineSegment(sketch, "E726", {"start": v(21.5, 13.01) * mm, "end": v(21.55, 13.05) * mm});
            skLineSegment(sketch, "E727", {"start": v(21.55, 13.05) * mm, "end": v(21.6, 13.09) * mm});
            skLineSegment(sketch, "E728", {"start": v(21.6, 13.09) * mm, "end": v(21.64, 13.13) * mm});
            skLineSegment(sketch, "E729", {"start": v(21.64, 13.13) * mm, "end": v(21.68, 13.17) * mm});
            skLineSegment(sketch, "E730", {"start": v(21.68, 13.17) * mm, "end": v(21.71, 13.21) * mm});
            skLineSegment(sketch, "E731", {"start": v(21.71, 13.21) * mm, "end": v(21.75, 13.26) * mm});
            skLineSegment(sketch, "E732", {"start": v(21.75, 13.26) * mm, "end": v(21.78, 13.3) * mm});
            skLineSegment(sketch, "E733", {"start": v(21.78, 13.3) * mm, "end": v(21.81, 13.35) * mm});
            skLineSegment(sketch, "E734", {"start": v(21.81, 13.35) * mm, "end": v(21.84, 13.4) * mm});
            skLineSegment(sketch, "E735", {"start": v(21.84, 13.4) * mm, "end": v(21.87, 13.45) * mm});
            skLineSegment(sketch, "E736", {"start": v(21.87, 13.45) * mm, "end": v(21.89, 13.5) * mm});
            skLineSegment(sketch, "E737", {"start": v(21.89, 13.5) * mm, "end": v(21.91, 13.55) * mm});
            skLineSegment(sketch, "E738", {"start": v(21.91, 13.55) * mm, "end": v(21.93, 13.6) * mm});
            skLineSegment(sketch, "E739", {"start": v(21.93, 13.6) * mm, "end": v(21.95, 13.65) * mm});
            skLineSegment(sketch, "E740", {"start": v(21.95, 13.65) * mm, "end": v(21.96, 13.7) * mm});
            skLineSegment(sketch, "E741", {"start": v(21.96, 13.7) * mm, "end": v(21.98, 13.76) * mm});
            skLineSegment(sketch, "E742", {"start": v(21.98, 13.76) * mm, "end": v(22, 13.82) * mm});
            skLineSegment(sketch, "E743", {"start": v(22, 13.82) * mm, "end": v(22, 13.88) * mm});
            skLineSegment(sketch, "E744", {"start": v(22, 13.88) * mm, "end": v(22.01, 13.94) * mm});
            skLineSegment(sketch, "E745", {"start": v(22.01, 13.94) * mm, "end": v(22.02, 14) * mm});
            skLineSegment(sketch, "E746", {"start": v(22.02, 14) * mm, "end": v(22.02, 14.06) * mm});
            skLineSegment(sketch, "E747", {"start": v(22.02, 14.06) * mm, "end": v(22.03, 14.13) * mm});
            skLineSegment(sketch, "E748", {"start": v(22.03, 14.13) * mm, "end": v(22.03, 14.19) * mm});
            skLineSegment(sketch, "E749", {"start": v(22.03, 14.19) * mm, "end": v(22.03, 14.26) * mm});
            skLineSegment(sketch, "E750", {"start": v(22.03, 14.26) * mm, "end": v(22.03, 14.32) * mm});
            skLineSegment(sketch, "E751", {"start": v(22.03, 14.32) * mm, "end": v(22.03, 14.39) * mm});
            skLineSegment(sketch, "E752", {"start": v(22.03, 14.39) * mm, "end": v(22.02, 14.45) * mm});
            skLineSegment(sketch, "E753", {"start": v(22.02, 14.45) * mm, "end": v(22.01, 14.51) * mm});
            skLineSegment(sketch, "E754", {"start": v(22.01, 14.51) * mm, "end": v(22, 14.57) * mm});
            skLineSegment(sketch, "E755", {"start": v(22, 14.57) * mm, "end": v(22, 14.63) * mm});
            skLineSegment(sketch, "E756", {"start": v(22, 14.63) * mm, "end": v(21.98, 14.69) * mm});
            skLineSegment(sketch, "E757", {"start": v(21.98, 14.69) * mm, "end": v(21.96, 14.74) * mm});
            skLineSegment(sketch, "E758", {"start": v(21.96, 14.74) * mm, "end": v(21.94, 14.8) * mm});
            skLineSegment(sketch, "E759", {"start": v(21.94, 14.8) * mm, "end": v(21.92, 14.85) * mm});
            skLineSegment(sketch, "E760", {"start": v(21.92, 14.85) * mm, "end": v(21.9, 14.9) * mm});
            skLineSegment(sketch, "E761", {"start": v(21.9, 14.9) * mm, "end": v(21.88, 14.95) * mm});
            skLineSegment(sketch, "E762", {"start": v(21.88, 14.95) * mm, "end": v(21.85, 15) * mm});
            skLineSegment(sketch, "E763", {"start": v(21.85, 15) * mm, "end": v(21.83, 15.04) * mm});
            skLineSegment(sketch, "E764", {"start": v(21.83, 15.04) * mm, "end": v(21.8, 15.08) * mm});
            skLineSegment(sketch, "E765", {"start": v(21.8, 15.08) * mm, "end": v(21.77, 15.13) * mm});
            skLineSegment(sketch, "E766", {"start": v(21.77, 15.13) * mm, "end": v(21.74, 15.17) * mm});
            skLineSegment(sketch, "E767", {"start": v(21.74, 15.17) * mm, "end": v(21.7, 15.2) * mm});
            skLineSegment(sketch, "E768", {"start": v(21.7, 15.2) * mm, "end": v(21.67, 15.24) * mm});
            skLineSegment(sketch, "E769", {"start": v(21.67, 15.24) * mm, "end": v(21.63, 15.28) * mm});
            skLineSegment(sketch, "E770", {"start": v(21.63, 15.28) * mm, "end": v(21.6, 15.32) * mm});
            skLineSegment(sketch, "E771", {"start": v(21.6, 15.32) * mm, "end": v(21.55, 15.36) * mm});
            skLineSegment(sketch, "E772", {"start": v(21.55, 15.36) * mm, "end": v(21.5, 15.4) * mm});
            skLineSegment(sketch, "E773", {"start": v(21.5, 15.4) * mm, "end": v(21.45, 15.43) * mm});
            skLineSegment(sketch, "E774", {"start": v(21.45, 15.43) * mm, "end": v(21.4, 15.46) * mm});
            skLineSegment(sketch, "E775", {"start": v(21.4, 15.46) * mm, "end": v(21.35, 15.49) * mm});
            skLineSegment(sketch, "E776", {"start": v(21.35, 15.49) * mm, "end": v(21.3, 15.52) * mm});
            skLineSegment(sketch, "E777", {"start": v(21.3, 15.52) * mm, "end": v(21.25, 15.54) * mm});
            skLineSegment(sketch, "E778", {"start": v(21.25, 15.54) * mm, "end": v(21.2, 15.56) * mm});
            skLineSegment(sketch, "E779", {"start": v(21.2, 15.56) * mm, "end": v(21.14, 15.58) * mm});
            skLineSegment(sketch, "E780", {"start": v(21.14, 15.58) * mm, "end": v(21.08, 15.6) * mm});
            skLineSegment(sketch, "E781", {"start": v(21.08, 15.6) * mm, "end": v(21.02, 15.62) * mm});
            skLineSegment(sketch, "E782", {"start": v(21.02, 15.62) * mm, "end": v(20.97, 15.63) * mm});
            skLineSegment(sketch, "E783", {"start": v(20.97, 15.63) * mm, "end": v(20.9, 15.64) * mm});
            skLineSegment(sketch, "E784", {"start": v(20.9, 15.64) * mm, "end": v(20.85, 15.65) * mm});
            skLineSegment(sketch, "E785", {"start": v(20.85, 15.65) * mm, "end": v(20.8, 15.66) * mm});
            skLineSegment(sketch, "E786", {"start": v(20.8, 15.66) * mm, "end": v(20.73, 15.67) * mm});
            skLineSegment(sketch, "E787", {"start": v(20.73, 15.67) * mm, "end": v(20.67, 15.67) * mm});
            skLineSegment(sketch, "E788", {"start": v(20.67, 15.67) * mm, "end": v(20.61, 15.68) * mm});
            skLineSegment(sketch, "E789", {"start": v(20.61, 15.68) * mm, "end": v(20.55, 15.68) * mm});
            skLineSegment(sketch, "E790", {"start": v(20.55, 15.68) * mm, "end": v(20.55, 16.08) * mm});
            skLineSegment(sketch, "E791", {"start": v(20.55, 16.08) * mm, "end": v(20.6, 16.08) * mm});
            skLineSegment(sketch, "E792", {"start": v(20.6, 16.08) * mm, "end": v(20.63, 16.08) * mm});
            skLineSegment(sketch, "E793", {"start": v(20.63, 16.08) * mm, "end": v(20.67, 16.08) * mm});
            skLineSegment(sketch, "E794", {"start": v(20.67, 16.08) * mm, "end": v(20.71, 16.07) * mm});
            skLineSegment(sketch, "E795", {"start": v(20.71, 16.07) * mm, "end": v(20.75, 16.07) * mm});
            skLineSegment(sketch, "E796", {"start": v(20.75, 16.07) * mm, "end": v(20.8, 16.06) * mm});
            skLineSegment(sketch, "E797", {"start": v(20.8, 16.06) * mm, "end": v(20.83, 16.06) * mm});
            skLineSegment(sketch, "E798", {"start": v(20.83, 16.06) * mm, "end": v(20.87, 16.05) * mm});
            skLineSegment(sketch, "E799", {"start": v(20.87, 16.05) * mm, "end": v(20.91, 16.05) * mm});
            skLineSegment(sketch, "E800", {"start": v(20.91, 16.05) * mm, "end": v(20.95, 16.04) * mm});
            skLineSegment(sketch, "E801", {"start": v(20.95, 16.04) * mm, "end": v(21, 16.03) * mm});
            skLineSegment(sketch, "E802", {"start": v(21, 16.03) * mm, "end": v(21.03, 16.02) * mm});
            skLineSegment(sketch, "E803", {"start": v(21.03, 16.02) * mm, "end": v(21.07, 16.01) * mm});
            skLineSegment(sketch, "E804", {"start": v(21.07, 16.01) * mm, "end": v(21.1, 16) * mm});
            skLineSegment(sketch, "E805", {"start": v(21.1, 16) * mm, "end": v(21.15, 16) * mm});
            skLineSegment(sketch, "E806", {"start": v(21.15, 16) * mm, "end": v(21.18, 15.98) * mm});
            skLineSegment(sketch, "E807", {"start": v(21.18, 15.98) * mm, "end": v(21.22, 15.97) * mm});
            skLineSegment(sketch, "E808", {"start": v(21.22, 15.97) * mm, "end": v(21.26, 15.96) * mm});
            skLineSegment(sketch, "E809", {"start": v(21.26, 15.96) * mm, "end": v(21.3, 15.94) * mm});
            skLineSegment(sketch, "E810", {"start": v(21.3, 15.94) * mm, "end": v(21.33, 15.93) * mm});
            skLineSegment(sketch, "E811", {"start": v(21.33, 15.93) * mm, "end": v(21.37, 15.91) * mm});
            skLineSegment(sketch, "E812", {"start": v(21.37, 15.91) * mm, "end": v(21.4, 15.9) * mm});
            skLineSegment(sketch, "E813", {"start": v(21.4, 15.9) * mm, "end": v(21.44, 15.88) * mm});
            skLineSegment(sketch, "E814", {"start": v(21.44, 15.88) * mm, "end": v(21.48, 15.87) * mm});
            skLineSegment(sketch, "E815", {"start": v(21.48, 15.87) * mm, "end": v(21.51, 15.85) * mm});
            skLineSegment(sketch, "E816", {"start": v(21.51, 15.85) * mm, "end": v(21.55, 15.83) * mm});
            skLineSegment(sketch, "E817", {"start": v(21.55, 15.83) * mm, "end": v(21.58, 15.81) * mm});
            skLineSegment(sketch, "E818", {"start": v(21.58, 15.81) * mm, "end": v(21.62, 15.8) * mm});
            skLineSegment(sketch, "E819", {"start": v(21.62, 15.8) * mm, "end": v(21.65, 15.78) * mm});
            skLineSegment(sketch, "E820", {"start": v(21.65, 15.78) * mm, "end": v(21.68, 15.76) * mm});
            skLineSegment(sketch, "E821", {"start": v(21.68, 15.76) * mm, "end": v(21.71, 15.74) * mm});
            skLineSegment(sketch, "E822", {"start": v(21.71, 15.74) * mm, "end": v(21.74, 15.71) * mm});
            skLineSegment(sketch, "E823", {"start": v(21.74, 15.71) * mm, "end": v(21.77, 15.7) * mm});
            skLineSegment(sketch, "E824", {"start": v(21.77, 15.7) * mm, "end": v(21.8, 15.67) * mm});
            skLineSegment(sketch, "E825", {"start": v(21.8, 15.67) * mm, "end": v(21.83, 15.65) * mm});
            skLineSegment(sketch, "E826", {"start": v(21.83, 15.65) * mm, "end": v(21.86, 15.62) * mm});
            skLineSegment(sketch, "E827", {"start": v(21.86, 15.62) * mm, "end": v(21.89, 15.6) * mm});
            skLineSegment(sketch, "E828", {"start": v(21.89, 15.6) * mm, "end": v(21.92, 15.58) * mm});
            skLineSegment(sketch, "E829", {"start": v(21.92, 15.58) * mm, "end": v(21.94, 15.55) * mm});
            skLineSegment(sketch, "E830", {"start": v(21.94, 15.55) * mm, "end": v(21.97, 15.53) * mm});
            skLineSegment(sketch, "E831", {"start": v(21.97, 15.53) * mm, "end": v(22.06, 15.43) * mm});
            skLineSegment(sketch, "E832", {"start": v(22.06, 15.43) * mm, "end": v(22.14, 15.32) * mm});
            skLineSegment(sketch, "E833", {"start": v(22.14, 15.32) * mm, "end": v(22.2, 15.21) * mm});
            skLineSegment(sketch, "E834", {"start": v(22.2, 15.21) * mm, "end": v(22.27, 15.1) * mm});
            skLineSegment(sketch, "E835", {"start": v(22.27, 15.1) * mm, "end": v(22.32, 14.97) * mm});
            skLineSegment(sketch, "E836", {"start": v(22.32, 14.97) * mm, "end": v(22.36, 14.84) * mm});
            skLineSegment(sketch, "E837", {"start": v(22.36, 14.84) * mm, "end": v(22.4, 14.7) * mm});
            skLineSegment(sketch, "E838", {"start": v(22.4, 14.7) * mm, "end": v(22.41, 14.56) * mm});
            skLineSegment(sketch, "E839", {"start": v(22.41, 14.56) * mm, "end": v(22.43, 14.41) * mm});
            skLineSegment(sketch, "E840", {"start": v(22.43, 14.41) * mm, "end": v(22.43, 14.26) * mm});
            skLineSegment(sketch, "E841", {"start": v(22.43, 14.26) * mm, "end": v(22.43, 14.18) * mm});
            skLineSegment(sketch, "E842", {"start": v(22.43, 14.18) * mm, "end": v(22.43, 14.1) * mm});
            skLineSegment(sketch, "E843", {"start": v(22.43, 14.1) * mm, "end": v(22.42, 14.02) * mm});
            skLineSegment(sketch, "E844", {"start": v(22.42, 14.02) * mm, "end": v(22.42, 13.94) * mm});
            skLineSegment(sketch, "E845", {"start": v(22.42, 13.94) * mm, "end": v(22.4, 13.87) * mm});
            skLineSegment(sketch, "E846", {"start": v(22.4, 13.87) * mm, "end": v(22.4, 13.8) * mm});
            skLineSegment(sketch, "E847", {"start": v(22.4, 13.8) * mm, "end": v(22.38, 13.72) * mm});
            skLineSegment(sketch, "E848", {"start": v(22.38, 13.72) * mm, "end": v(22.36, 13.65) * mm});
            skLineSegment(sketch, "E849", {"start": v(22.36, 13.65) * mm, "end": v(22.34, 13.58) * mm});
            skLineSegment(sketch, "E850", {"start": v(22.34, 13.58) * mm, "end": v(22.32, 13.51) * mm});
            skLineSegment(sketch, "E851", {"start": v(22.32, 13.51) * mm, "end": v(22.3, 13.45) * mm});
            skLineSegment(sketch, "E852", {"start": v(22.3, 13.45) * mm, "end": v(22.27, 13.38) * mm});
            skLineSegment(sketch, "E853", {"start": v(22.27, 13.38) * mm, "end": v(22.24, 13.32) * mm});
            skLineSegment(sketch, "E854", {"start": v(22.24, 13.32) * mm, "end": v(22.21, 13.25) * mm});
            skLineSegment(sketch, "E855", {"start": v(22.21, 13.25) * mm, "end": v(22.18, 13.2) * mm});
            skLineSegment(sketch, "E856", {"start": v(22.18, 13.2) * mm, "end": v(22.15, 13.13) * mm});
            skLineSegment(sketch, "E857", {"start": v(22.15, 13.13) * mm, "end": v(22.1, 13.08) * mm});
            skLineSegment(sketch, "E858", {"start": v(22.1, 13.08) * mm, "end": v(22.07, 13.02) * mm});
            skLineSegment(sketch, "E859", {"start": v(22.07, 13.02) * mm, "end": v(22.03, 12.97) * mm});
            skLineSegment(sketch, "E860", {"start": v(22.03, 12.97) * mm, "end": v(21.99, 12.91) * mm});
            skLineSegment(sketch, "E861", {"start": v(21.99, 12.91) * mm, "end": v(21.93, 12.86) * mm});
            skLineSegment(sketch, "E862", {"start": v(21.93, 12.86) * mm, "end": v(21.88, 12.8) * mm});
            skLineSegment(sketch, "E863", {"start": v(21.88, 12.8) * mm, "end": v(21.83, 12.75) * mm});
            skLineSegment(sketch, "E864", {"start": v(21.83, 12.75) * mm, "end": v(21.77, 12.7) * mm});
            skLineSegment(sketch, "E865", {"start": v(21.77, 12.7) * mm, "end": v(21.7, 12.66) * mm});
            skLineSegment(sketch, "E866", {"start": v(21.7, 12.66) * mm, "end": v(21.64, 12.61) * mm});
            skLineSegment(sketch, "E867", {"start": v(21.64, 12.61) * mm, "end": v(21.58, 12.57) * mm});
            skLineSegment(sketch, "E868", {"start": v(21.58, 12.57) * mm, "end": v(21.51, 12.53) * mm});
            skLineSegment(sketch, "E869", {"start": v(21.51, 12.53) * mm, "end": v(21.44, 12.5) * mm});
            skLineSegment(sketch, "E870", {"start": v(21.44, 12.5) * mm, "end": v(21.37, 12.47) * mm});
            skLineSegment(sketch, "E871", {"start": v(21.37, 12.47) * mm, "end": v(21.3, 12.44) * mm});
            skLineSegment(sketch, "E872", {"start": v(21.3, 12.44) * mm, "end": v(21.22, 12.41) * mm});
            skLineSegment(sketch, "E873", {"start": v(21.22, 12.41) * mm, "end": v(21.14, 12.39) * mm});
            skLineSegment(sketch, "E874", {"start": v(21.14, 12.39) * mm, "end": v(21.06, 12.37) * mm});
            skLineSegment(sketch, "E875", {"start": v(21.06, 12.37) * mm, "end": v(20.98, 12.35) * mm});
            skLineSegment(sketch, "E876", {"start": v(20.98, 12.35) * mm, "end": v(20.9, 12.34) * mm});
            skLineSegment(sketch, "E877", {"start": v(20.9, 12.34) * mm, "end": v(20.82, 12.33) * mm});
            skLineSegment(sketch, "E878", {"start": v(20.82, 12.33) * mm, "end": v(20.73, 12.32) * mm});
            skLineSegment(sketch, "E879", {"start": v(20.73, 12.32) * mm, "end": v(20.64, 12.31) * mm});
            skLineSegment(sketch, "E880", {"start": v(20.64, 12.31) * mm, "end": v(20.55, 12.31) * mm});
            skLineSegment(sketch, "E881", {"start": v(-19.11, -6.36) * mm, "end": v(-22.32, -6.36) * mm});
            skLineSegment(sketch, "E882", {"start": v(-22.32, -6.36) * mm, "end": v(-22.36, -6.35) * mm});
            skLineSegment(sketch, "E883", {"start": v(-22.36, -6.35) * mm, "end": v(-22.4, -6.35) * mm});
            skLineSegment(sketch, "E884", {"start": v(-22.4, -6.35) * mm, "end": v(-22.44, -6.35) * mm});
            skLineSegment(sketch, "E885", {"start": v(-22.44, -6.35) * mm, "end": v(-22.48, -6.34) * mm});
            skLineSegment(sketch, "E886", {"start": v(-22.48, -6.34) * mm, "end": v(-22.52, -6.34) * mm});
            skLineSegment(sketch, "E887", {"start": v(-22.52, -6.34) * mm, "end": v(-22.56, -6.33) * mm});
            skLineSegment(sketch, "E888", {"start": v(-22.56, -6.33) * mm, "end": v(-22.6, -6.32) * mm});
            skLineSegment(sketch, "E889", {"start": v(-22.6, -6.32) * mm, "end": v(-22.63, -6.3) * mm});
            skLineSegment(sketch, "E890", {"start": v(-22.63, -6.3) * mm, "end": v(-22.66, -6.29) * mm});
            skLineSegment(sketch, "E891", {"start": v(-22.66, -6.29) * mm, "end": v(-22.7, -6.27) * mm});
            skLineSegment(sketch, "E892", {"start": v(-22.7, -6.27) * mm, "end": v(-22.72, -6.26) * mm});
            skLineSegment(sketch, "E893", {"start": v(-22.72, -6.26) * mm, "end": v(-22.75, -6.24) * mm});
            skLineSegment(sketch, "E894", {"start": v(-22.75, -6.24) * mm, "end": v(-22.78, -6.22) * mm});
            skLineSegment(sketch, "E895", {"start": v(-22.78, -6.22) * mm, "end": v(-22.8, -6.2) * mm});
            skLineSegment(sketch, "E896", {"start": v(-22.8, -6.2) * mm, "end": v(-22.83, -6.18) * mm});
            skLineSegment(sketch, "E897", {"start": v(-22.83, -6.18) * mm, "end": v(-22.85, -6.16) * mm});
            skLineSegment(sketch, "E898", {"start": v(-22.85, -6.16) * mm, "end": v(-22.88, -6.13) * mm});
            skLineSegment(sketch, "E899", {"start": v(-22.88, -6.13) * mm, "end": v(-22.9, -6.1) * mm});
            skLineSegment(sketch, "E900", {"start": v(-22.9, -6.1) * mm, "end": v(-22.92, -6.08) * mm});
            skLineSegment(sketch, "E901", {"start": v(-22.92, -6.08) * mm, "end": v(-22.94, -6.06) * mm});
            skLineSegment(sketch, "E902", {"start": v(-22.94, -6.06) * mm, "end": v(-22.95, -6.03) * mm});
            skLineSegment(sketch, "E903", {"start": v(-22.95, -6.03) * mm, "end": v(-22.96, -6) * mm});
            skLineSegment(sketch, "E904", {"start": v(-22.96, -6) * mm, "end": v(-22.97, -5.96) * mm});
            skLineSegment(sketch, "E905", {"start": v(-22.97, -5.96) * mm, "end": v(-22.98, -5.93) * mm});
            skLineSegment(sketch, "E906", {"start": v(-22.98, -5.93) * mm, "end": v(-23, -5.9) * mm});
            skLineSegment(sketch, "E907", {"start": v(-23, -5.9) * mm, "end": v(-23, -5.87) * mm});
            skLineSegment(sketch, "E908", {"start": v(-23, -5.87) * mm, "end": v(-23, -5.83) * mm});
            skLineSegment(sketch, "E909", {"start": v(-23, -5.83) * mm, "end": v(-23, -5.8) * mm});
            skLineSegment(sketch, "E910", {"start": v(-23, -5.8) * mm, "end": v(-23, -5.76) * mm});
            skLineSegment(sketch, "E911", {"start": v(-23, -5.76) * mm, "end": v(-23, -5.73) * mm});
            skLineSegment(sketch, "E912", {"start": v(-23, -5.73) * mm, "end": v(-23, -5.69) * mm});
            skLineSegment(sketch, "E913", {"start": v(-23, -5.69) * mm, "end": v(-23, -5.65) * mm});
            skLineSegment(sketch, "E914", {"start": v(-23, -5.65) * mm, "end": v(-22.99, -5.62) * mm});
            skLineSegment(sketch, "E915", {"start": v(-22.99, -5.62) * mm, "end": v(-22.98, -5.58) * mm});
            skLineSegment(sketch, "E916", {"start": v(-22.98, -5.58) * mm, "end": v(-22.97, -5.54) * mm});
            skLineSegment(sketch, "E917", {"start": v(-22.97, -5.54) * mm, "end": v(-22.95, -5.5) * mm});
            skLineSegment(sketch, "E918", {"start": v(-22.95, -5.5) * mm, "end": v(-22.94, -5.47) * mm});
            skLineSegment(sketch, "E919", {"start": v(-22.94, -5.47) * mm, "end": v(-22.92, -5.43) * mm});
            skLineSegment(sketch, "E920", {"start": v(-22.92, -5.43) * mm, "end": v(-22.9, -5.4) * mm});
            skLineSegment(sketch, "E921", {"start": v(-22.9, -5.4) * mm, "end": v(-22.88, -5.36) * mm});
            skLineSegment(sketch, "E922", {"start": v(-22.88, -5.36) * mm, "end": v(-22.86, -5.33) * mm});
            skLineSegment(sketch, "E923", {"start": v(-22.86, -5.33) * mm, "end": v(-22.84, -5.3) * mm});
            skLineSegment(sketch, "E924", {"start": v(-22.84, -5.3) * mm, "end": v(-22.82, -5.26) * mm});
            skLineSegment(sketch, "E925", {"start": v(-22.82, -5.26) * mm, "end": v(-22.8, -5.22) * mm});
            skLineSegment(sketch, "E926", {"start": v(-22.8, -5.22) * mm, "end": v(-22.77, -5.18) * mm});
            skLineSegment(sketch, "E927", {"start": v(-22.77, -5.18) * mm, "end": v(-22.75, -5.14) * mm});
            skLineSegment(sketch, "E928", {"start": v(-22.75, -5.14) * mm, "end": v(-22.72, -5.1) * mm});
            skLineSegment(sketch, "E929", {"start": v(-22.72, -5.1) * mm, "end": v(-22.7, -5.05) * mm});
            skLineSegment(sketch, "E930", {"start": v(-22.7, -5.05) * mm, "end": v(-22.66, -5) * mm});
            skLineSegment(sketch, "E931", {"start": v(-22.66, -5) * mm, "end": v(-22.63, -4.95) * mm});
            skLineSegment(sketch, "E932", {"start": v(-22.63, -4.95) * mm, "end": v(-22.6, -4.9) * mm});
            skLineSegment(sketch, "E933", {"start": v(-22.6, -4.9) * mm, "end": v(-22.57, -4.84) * mm});
            skLineSegment(sketch, "E934", {"start": v(-22.57, -4.84) * mm, "end": v(-22.54, -4.78) * mm});
            skLineSegment(sketch, "E935", {"start": v(-22.54, -4.78) * mm, "end": v(-22.5, -4.73) * mm});
            skLineSegment(sketch, "E936", {"start": v(-22.5, -4.73) * mm, "end": v(-22.47, -4.67) * mm});
            skLineSegment(sketch, "E937", {"start": v(-22.47, -4.67) * mm, "end": v(-22.43, -4.61) * mm});
            skLineSegment(sketch, "E938", {"start": v(-22.43, -4.61) * mm, "end": v(-22.4, -4.55) * mm});
            skLineSegment(sketch, "E939", {"start": v(-22.4, -4.55) * mm, "end": v(-22.36, -4.49) * mm});
            skLineSegment(sketch, "E940", {"start": v(-22.36, -4.49) * mm, "end": v(-22.32, -4.43) * mm});
            skLineSegment(sketch, "E941", {"start": v(-22.32, -4.43) * mm, "end": v(-22.29, -4.36) * mm});
            skLineSegment(sketch, "E942", {"start": v(-22.29, -4.36) * mm, "end": v(-22.25, -4.3) * mm});
            skLineSegment(sketch, "E943", {"start": v(-22.25, -4.3) * mm, "end": v(-22.2, -4.23) * mm});
            skLineSegment(sketch, "E944", {"start": v(-22.2, -4.23) * mm, "end": v(-22.17, -4.17) * mm});
            skLineSegment(sketch, "E945", {"start": v(-22.17, -4.17) * mm, "end": v(-22.13, -4.1) * mm});
            skLineSegment(sketch, "E946", {"start": v(-22.13, -4.1) * mm, "end": v(-22.09, -4.03) * mm});
            skLineSegment(sketch, "E947", {"start": v(-22.09, -4.03) * mm, "end": v(-22.05, -3.96) * mm});
            skLineSegment(sketch, "E948", {"start": v(-22.05, -3.96) * mm, "end": v(-22, -3.9) * mm});
            skLineSegment(sketch, "E949", {"start": v(-22, -3.9) * mm, "end": v(-21.97, -3.83) * mm});
            skLineSegment(sketch, "E950", {"start": v(-21.97, -3.83) * mm, "end": v(-21.92, -3.75) * mm});
            skLineSegment(sketch, "E951", {"start": v(-21.92, -3.75) * mm, "end": v(-21.88, -3.68) * mm});
            skLineSegment(sketch, "E952", {"start": v(-21.88, -3.68) * mm, "end": v(-21.84, -3.61) * mm});
            skLineSegment(sketch, "E953", {"start": v(-21.84, -3.61) * mm, "end": v(-21.8, -3.54) * mm});
            skLineSegment(sketch, "E954", {"start": v(-21.8, -3.54) * mm, "end": v(-21.75, -3.47) * mm});
            skLineSegment(sketch, "E955", {"start": v(-21.75, -3.47) * mm, "end": v(-21.7, -3.4) * mm});
            skLineSegment(sketch, "E956", {"start": v(-21.7, -3.4) * mm, "end": v(-21.67, -3.32) * mm});
            skLineSegment(sketch, "E957", {"start": v(-21.67, -3.32) * mm, "end": v(-21.62, -3.25) * mm});
            skLineSegment(sketch, "E958", {"start": v(-21.62, -3.25) * mm, "end": v(-21.58, -3.18) * mm});
            skLineSegment(sketch, "E959", {"start": v(-21.58, -3.18) * mm, "end": v(-21.54, -3.11) * mm});
            skLineSegment(sketch, "E960", {"start": v(-21.54, -3.11) * mm, "end": v(-21.5, -3.04) * mm});
            skLineSegment(sketch, "E961", {"start": v(-21.5, -3.04) * mm, "end": v(-21.45, -2.97) * mm});
            skLineSegment(sketch, "E962", {"start": v(-21.45, -2.97) * mm, "end": v(-21.41, -2.9) * mm});
            skLineSegment(sketch, "E963", {"start": v(-21.41, -2.9) * mm, "end": v(-21.37, -2.83) * mm});
            skLineSegment(sketch, "E964", {"start": v(-21.37, -2.83) * mm, "end": v(-21.33, -2.76) * mm});
            skLineSegment(sketch, "E965", {"start": v(-21.33, -2.76) * mm, "end": v(-21.29, -2.7) * mm});
            skLineSegment(sketch, "E966", {"start": v(-21.29, -2.7) * mm, "end": v(-21.25, -2.62) * mm});
            skLineSegment(sketch, "E967", {"start": v(-21.25, -2.62) * mm, "end": v(-21.2, -2.56) * mm});
            skLineSegment(sketch, "E968", {"start": v(-21.2, -2.56) * mm, "end": v(-21.17, -2.5) * mm});
            skLineSegment(sketch, "E969", {"start": v(-21.17, -2.5) * mm, "end": v(-21.13, -2.42) * mm});
            skLineSegment(sketch, "E970", {"start": v(-21.13, -2.42) * mm, "end": v(-21.09, -2.36) * mm});
            skLineSegment(sketch, "E971", {"start": v(-21.09, -2.36) * mm, "end": v(-21.05, -2.3) * mm});
            skLineSegment(sketch, "E972", {"start": v(-21.05, -2.3) * mm, "end": v(-21.01, -2.23) * mm});
            skLineSegment(sketch, "E973", {"start": v(-21.01, -2.23) * mm, "end": v(-20.98, -2.17) * mm});
            skLineSegment(sketch, "E974", {"start": v(-20.98, -2.17) * mm, "end": v(-20.94, -2.1) * mm});
            skLineSegment(sketch, "E975", {"start": v(-20.94, -2.1) * mm, "end": v(-20.9, -2.05) * mm});
            skLineSegment(sketch, "E976", {"start": v(-20.9, -2.05) * mm, "end": v(-20.87, -1.99) * mm});
            skLineSegment(sketch, "E977", {"start": v(-20.87, -1.99) * mm, "end": v(-20.84, -1.93) * mm});
            skLineSegment(sketch, "E978", {"start": v(-20.84, -1.93) * mm, "end": v(-20.8, -1.88) * mm});
            skLineSegment(sketch, "E979", {"start": v(-20.8, -1.88) * mm, "end": v(-20.77, -1.82) * mm});
            skLineSegment(sketch, "E980", {"start": v(-20.77, -1.82) * mm, "end": v(-20.74, -1.77) * mm});
            skLineSegment(sketch, "E981", {"start": v(-20.74, -1.77) * mm, "end": v(-20.71, -1.72) * mm});
            skLineSegment(sketch, "E982", {"start": v(-20.71, -1.72) * mm, "end": v(-20.68, -1.67) * mm});
            skLineSegment(sketch, "E983", {"start": v(-20.68, -1.67) * mm, "end": v(-20.65, -1.63) * mm});
            skLineSegment(sketch, "E984", {"start": v(-20.65, -1.63) * mm, "end": v(-20.63, -1.58) * mm});
            skLineSegment(sketch, "E985", {"start": v(-20.63, -1.58) * mm, "end": v(-20.6, -1.54) * mm});
            skLineSegment(sketch, "E986", {"start": v(-20.6, -1.54) * mm, "end": v(-20.58, -1.5) * mm});
            skLineSegment(sketch, "E987", {"start": v(-20.58, -1.5) * mm, "end": v(-20.55, -1.46) * mm});
            skLineSegment(sketch, "E988", {"start": v(-20.55, -1.46) * mm, "end": v(-20.53, -1.42) * mm});
            skLineSegment(sketch, "E989", {"start": v(-20.53, -1.42) * mm, "end": v(-20.51, -1.39) * mm});
            skLineSegment(sketch, "E990", {"start": v(-20.51, -1.39) * mm, "end": v(-20.5, -1.35) * mm});
            skLineSegment(sketch, "E991", {"start": v(-20.5, -1.35) * mm, "end": v(-20.47, -1.32) * mm});
            skLineSegment(sketch, "E992", {"start": v(-20.47, -1.32) * mm, "end": v(-20.46, -1.3) * mm});
            skLineSegment(sketch, "E993", {"start": v(-20.46, -1.3) * mm, "end": v(-20.44, -1.27) * mm});
            skLineSegment(sketch, "E994", {"start": v(-20.44, -1.27) * mm, "end": v(-20.43, -1.25) * mm});
            skLineSegment(sketch, "E995", {"start": v(-20.43, -1.25) * mm, "end": v(-20.41, -1.23) * mm});
            skLineSegment(sketch, "E996", {"start": v(-20.41, -1.23) * mm, "end": v(-20.4, -1.2) * mm});
            skLineSegment(sketch, "E997", {"start": v(-20.4, -1.2) * mm, "end": v(-20.4, -1.2) * mm});
            skLineSegment(sketch, "E998", {"start": v(-20.4, -1.2) * mm, "end": v(-20.39, -1.18) * mm});
            skLineSegment(sketch, "E999", {"start": v(-20.39, -1.18) * mm, "end": v(-20.38, -1.18) * mm});
            skLineSegment(sketch, "E1000", {"start": v(-20.38, -1.18) * mm, "end": v(-20.38, -1.17) * mm});
            skLineSegment(sketch, "E1001", {"start": v(-20.38, -1.17) * mm, "end": v(-20.38, -1.17) * mm});
            skLineSegment(sketch, "E1002", {"start": v(-20.38, -1.17) * mm, "end": v(-20.04, -1.38) * mm});
            skLineSegment(sketch, "E1003", {"start": v(-20.04, -1.38) * mm, "end": v(-20.04, -1.38) * mm});
            skLineSegment(sketch, "E1004", {"start": v(-20.04, -1.38) * mm, "end": v(-20.05, -1.4) * mm});
            skLineSegment(sketch, "E1005", {"start": v(-20.05, -1.4) * mm, "end": v(-20.05, -1.4) * mm});
            skLineSegment(sketch, "E1006", {"start": v(-20.05, -1.4) * mm, "end": v(-20.06, -1.42) * mm});
            skLineSegment(sketch, "E1007", {"start": v(-20.06, -1.42) * mm, "end": v(-20.07, -1.43) * mm});
            skLineSegment(sketch, "E1008", {"start": v(-20.07, -1.43) * mm, "end": v(-20.09, -1.45) * mm});
            skLineSegment(sketch, "E1009", {"start": v(-20.09, -1.45) * mm, "end": v(-20.1, -1.48) * mm});
            skLineSegment(sketch, "E1010", {"start": v(-20.1, -1.48) * mm, "end": v(-20.11, -1.5) * mm});
            skLineSegment(sketch, "E1011", {"start": v(-20.11, -1.5) * mm, "end": v(-20.13, -1.53) * mm});
            skLineSegment(sketch, "E1012", {"start": v(-20.13, -1.53) * mm, "end": v(-20.15, -1.56) * mm});
            skLineSegment(sketch, "E1013", {"start": v(-20.15, -1.56) * mm, "end": v(-20.17, -1.6) * mm});
            skLineSegment(sketch, "E1014", {"start": v(-20.17, -1.6) * mm, "end": v(-20.2, -1.63) * mm});
            skLineSegment(sketch, "E1015", {"start": v(-20.2, -1.63) * mm, "end": v(-20.21, -1.67) * mm});
            skLineSegment(sketch, "E1016", {"start": v(-20.21, -1.67) * mm, "end": v(-20.24, -1.7) * mm});
            skLineSegment(sketch, "E1017", {"start": v(-20.24, -1.7) * mm, "end": v(-20.26, -1.75) * mm});
            skLineSegment(sketch, "E1018", {"start": v(-20.26, -1.75) * mm, "end": v(-20.29, -1.79) * mm});
            skLineSegment(sketch, "E1019", {"start": v(-20.29, -1.79) * mm, "end": v(-20.31, -1.83) * mm});
            skLineSegment(sketch, "E1020", {"start": v(-20.31, -1.83) * mm, "end": v(-20.34, -1.88) * mm});
            skLineSegment(sketch, "E1021", {"start": v(-20.34, -1.88) * mm, "end": v(-20.37, -1.93) * mm});
            skLineSegment(sketch, "E1022", {"start": v(-20.37, -1.93) * mm, "end": v(-20.4, -1.98) * mm});
            skLineSegment(sketch, "E1023", {"start": v(-20.4, -1.98) * mm, "end": v(-20.43, -2.03) * mm});
            skLineSegment(sketch, "E1024", {"start": v(-20.43, -2.03) * mm, "end": v(-20.46, -2.09) * mm});
            skLineSegment(sketch, "E1025", {"start": v(-20.46, -2.09) * mm, "end": v(-20.5, -2.14) * mm});
            skLineSegment(sketch, "E1026", {"start": v(-20.5, -2.14) * mm, "end": v(-20.53, -2.2) * mm});
            skLineSegment(sketch, "E1027", {"start": v(-20.53, -2.2) * mm, "end": v(-20.56, -2.25) * mm});
            skLineSegment(sketch, "E1028", {"start": v(-20.56, -2.25) * mm, "end": v(-20.6, -2.31) * mm});
            skLineSegment(sketch, "E1029", {"start": v(-20.6, -2.31) * mm, "end": v(-20.63, -2.38) * mm});
            skLineSegment(sketch, "E1030", {"start": v(-20.63, -2.38) * mm, "end": v(-20.67, -2.44) * mm});
            skLineSegment(sketch, "E1031", {"start": v(-20.67, -2.44) * mm, "end": v(-20.7, -2.5) * mm});
            skLineSegment(sketch, "E1032", {"start": v(-20.7, -2.5) * mm, "end": v(-20.75, -2.57) * mm});
            skLineSegment(sketch, "E1033", {"start": v(-20.75, -2.57) * mm, "end": v(-20.79, -2.63) * mm});
            skLineSegment(sketch, "E1034", {"start": v(-20.79, -2.63) * mm, "end": v(-20.83, -2.7) * mm});
            skLineSegment(sketch, "E1035", {"start": v(-20.83, -2.7) * mm, "end": v(-20.87, -2.76) * mm});
            skLineSegment(sketch, "E1036", {"start": v(-20.87, -2.76) * mm, "end": v(-20.9, -2.83) * mm});
            skLineSegment(sketch, "E1037", {"start": v(-20.9, -2.83) * mm, "end": v(-20.95, -2.9) * mm});
            skLineSegment(sketch, "E1038", {"start": v(-20.95, -2.9) * mm, "end": v(-20.99, -2.97) * mm});
            skLineSegment(sketch, "E1039", {"start": v(-20.99, -2.97) * mm, "end": v(-21.03, -3.04) * mm});
            skLineSegment(sketch, "E1040", {"start": v(-21.03, -3.04) * mm, "end": v(-21.07, -3.1) * mm});
            skLineSegment(sketch, "E1041", {"start": v(-21.07, -3.1) * mm, "end": v(-21.11, -3.18) * mm});
            skLineSegment(sketch, "E1042", {"start": v(-21.11, -3.18) * mm, "end": v(-21.15, -3.25) * mm});
            skLineSegment(sketch, "E1043", {"start": v(-21.15, -3.25) * mm, "end": v(-21.2, -3.32) * mm});
            skLineSegment(sketch, "E1044", {"start": v(-21.2, -3.32) * mm, "end": v(-21.24, -3.4) * mm});
            skLineSegment(sketch, "E1045", {"start": v(-21.24, -3.4) * mm, "end": v(-21.28, -3.46) * mm});
            skLineSegment(sketch, "E1046", {"start": v(-21.28, -3.46) * mm, "end": v(-21.33, -3.53) * mm});
            skLineSegment(sketch, "E1047", {"start": v(-21.33, -3.53) * mm, "end": v(-21.37, -3.6) * mm});
            skLineSegment(sketch, "E1048", {"start": v(-21.37, -3.6) * mm, "end": v(-21.41, -3.68) * mm});
            skLineSegment(sketch, "E1049", {"start": v(-21.41, -3.68) * mm, "end": v(-21.45, -3.75) * mm});
            skLineSegment(sketch, "E1050", {"start": v(-21.45, -3.75) * mm, "end": v(-21.5, -3.82) * mm});
            skLineSegment(sketch, "E1051", {"start": v(-21.5, -3.82) * mm, "end": v(-21.54, -3.9) * mm});
            skLineSegment(sketch, "E1052", {"start": v(-21.54, -3.9) * mm, "end": v(-21.58, -3.96) * mm});
            skLineSegment(sketch, "E1053", {"start": v(-21.58, -3.96) * mm, "end": v(-21.62, -4.03) * mm});
            skLineSegment(sketch, "E1054", {"start": v(-21.62, -4.03) * mm, "end": v(-21.67, -4.1) * mm});
            skLineSegment(sketch, "E1055", {"start": v(-21.67, -4.1) * mm, "end": v(-21.7, -4.17) * mm});
            skLineSegment(sketch, "E1056", {"start": v(-21.7, -4.17) * mm, "end": v(-21.75, -4.24) * mm});
            skLineSegment(sketch, "E1057", {"start": v(-21.75, -4.24) * mm, "end": v(-21.79, -4.3) * mm});
            skLineSegment(sketch, "E1058", {"start": v(-21.79, -4.3) * mm, "end": v(-21.83, -4.38) * mm});
            skLineSegment(sketch, "E1059", {"start": v(-21.83, -4.38) * mm, "end": v(-21.87, -4.44) * mm});
            skLineSegment(sketch, "E1060", {"start": v(-21.87, -4.44) * mm, "end": v(-21.9, -4.5) * mm});
            skLineSegment(sketch, "E1061", {"start": v(-21.9, -4.5) * mm, "end": v(-21.95, -4.57) * mm});
            skLineSegment(sketch, "E1062", {"start": v(-21.95, -4.57) * mm, "end": v(-21.98, -4.64) * mm});
            skLineSegment(sketch, "E1063", {"start": v(-21.98, -4.64) * mm, "end": v(-22.02, -4.7) * mm});
            skLineSegment(sketch, "E1064", {"start": v(-22.02, -4.7) * mm, "end": v(-22.06, -4.76) * mm});
            skLineSegment(sketch, "E1065", {"start": v(-22.06, -4.76) * mm, "end": v(-22.1, -4.82) * mm});
            skLineSegment(sketch, "E1066", {"start": v(-22.1, -4.82) * mm, "end": v(-22.13, -4.88) * mm});
            skLineSegment(sketch, "E1067", {"start": v(-22.13, -4.88) * mm, "end": v(-22.16, -4.93) * mm});
            skLineSegment(sketch, "E1068", {"start": v(-22.16, -4.93) * mm, "end": v(-22.2, -5) * mm});
            skLineSegment(sketch, "E1069", {"start": v(-22.2, -5) * mm, "end": v(-22.23, -5.05) * mm});
            skLineSegment(sketch, "E1070", {"start": v(-22.23, -5.05) * mm, "end": v(-22.26, -5.1) * mm});
            skLineSegment(sketch, "E1071", {"start": v(-22.26, -5.1) * mm, "end": v(-22.3, -5.15) * mm});
            skLineSegment(sketch, "E1072", {"start": v(-22.3, -5.15) * mm, "end": v(-22.32, -5.2) * mm});
            skLineSegment(sketch, "E1073", {"start": v(-22.32, -5.2) * mm, "end": v(-22.35, -5.25) * mm});
            skLineSegment(sketch, "E1074", {"start": v(-22.35, -5.25) * mm, "end": v(-22.38, -5.3) * mm});
            skLineSegment(sketch, "E1075", {"start": v(-22.38, -5.3) * mm, "end": v(-22.4, -5.34) * mm});
            skLineSegment(sketch, "E1076", {"start": v(-22.4, -5.34) * mm, "end": v(-22.43, -5.39) * mm});
            skLineSegment(sketch, "E1077", {"start": v(-22.43, -5.39) * mm, "end": v(-22.45, -5.43) * mm});
            skLineSegment(sketch, "E1078", {"start": v(-22.45, -5.43) * mm, "end": v(-22.48, -5.46) * mm});
            skLineSegment(sketch, "E1079", {"start": v(-22.48, -5.46) * mm, "end": v(-22.5, -5.5) * mm});
            skLineSegment(sketch, "E1080", {"start": v(-22.5, -5.5) * mm, "end": v(-22.52, -5.53) * mm});
            skLineSegment(sketch, "E1081", {"start": v(-22.52, -5.53) * mm, "end": v(-22.53, -5.57) * mm});
            skLineSegment(sketch, "E1082", {"start": v(-22.53, -5.57) * mm, "end": v(-22.54, -5.58) * mm});
            skLineSegment(sketch, "E1083", {"start": v(-22.54, -5.58) * mm, "end": v(-22.55, -5.6) * mm});
            skLineSegment(sketch, "E1084", {"start": v(-22.55, -5.6) * mm, "end": v(-22.56, -5.62) * mm});
            skLineSegment(sketch, "E1085", {"start": v(-22.56, -5.62) * mm, "end": v(-22.57, -5.63) * mm});
            skLineSegment(sketch, "E1086", {"start": v(-22.57, -5.63) * mm, "end": v(-22.58, -5.65) * mm});
            skLineSegment(sketch, "E1087", {"start": v(-22.58, -5.65) * mm, "end": v(-22.58, -5.66) * mm});
            skLineSegment(sketch, "E1088", {"start": v(-22.58, -5.66) * mm, "end": v(-22.59, -5.68) * mm});
            skLineSegment(sketch, "E1089", {"start": v(-22.59, -5.68) * mm, "end": v(-22.6, -5.7) * mm});
            skLineSegment(sketch, "E1090", {"start": v(-22.6, -5.7) * mm, "end": v(-22.6, -5.7) * mm});
            skLineSegment(sketch, "E1091", {"start": v(-22.6, -5.7) * mm, "end": v(-22.6, -5.72) * mm});
            skLineSegment(sketch, "E1092", {"start": v(-22.6, -5.72) * mm, "end": v(-22.6, -5.74) * mm});
            skLineSegment(sketch, "E1093", {"start": v(-22.6, -5.74) * mm, "end": v(-22.6, -5.75) * mm});
            skLineSegment(sketch, "E1094", {"start": v(-22.6, -5.75) * mm, "end": v(-22.6, -5.77) * mm});
            skLineSegment(sketch, "E1095", {"start": v(-22.6, -5.77) * mm, "end": v(-22.6, -5.78) * mm});
            skLineSegment(sketch, "E1096", {"start": v(-22.6, -5.78) * mm, "end": v(-22.6, -5.8) * mm});
            skLineSegment(sketch, "E1097", {"start": v(-22.6, -5.8) * mm, "end": v(-22.6, -5.8) * mm});
            skLineSegment(sketch, "E1098", {"start": v(-22.6, -5.8) * mm, "end": v(-22.6, -5.82) * mm});
            skLineSegment(sketch, "E1099", {"start": v(-22.6, -5.82) * mm, "end": v(-22.6, -5.83) * mm});
            skLineSegment(sketch, "E1100", {"start": v(-22.6, -5.83) * mm, "end": v(-22.6, -5.84) * mm});
            skLineSegment(sketch, "E1101", {"start": v(-22.6, -5.84) * mm, "end": v(-22.58, -5.85) * mm});
            skLineSegment(sketch, "E1102", {"start": v(-22.58, -5.85) * mm, "end": v(-22.57, -5.87) * mm});
            skLineSegment(sketch, "E1103", {"start": v(-22.57, -5.87) * mm, "end": v(-22.55, -5.89) * mm});
            skLineSegment(sketch, "E1104", {"start": v(-22.55, -5.89) * mm, "end": v(-22.53, -5.9) * mm});
            skLineSegment(sketch, "E1105", {"start": v(-22.53, -5.9) * mm, "end": v(-22.51, -5.92) * mm});
            skLineSegment(sketch, "E1106", {"start": v(-22.51, -5.92) * mm, "end": v(-22.49, -5.93) * mm});
            skLineSegment(sketch, "E1107", {"start": v(-22.49, -5.93) * mm, "end": v(-22.46, -5.94) * mm});
            skLineSegment(sketch, "E1108", {"start": v(-22.46, -5.94) * mm, "end": v(-22.43, -5.94) * mm});
            skLineSegment(sketch, "E1109", {"start": v(-22.43, -5.94) * mm, "end": v(-22.4, -5.95) * mm});
            skLineSegment(sketch, "E1110", {"start": v(-22.4, -5.95) * mm, "end": v(-22.36, -5.95) * mm});
            skLineSegment(sketch, "E1111", {"start": v(-22.36, -5.95) * mm, "end": v(-22.32, -5.95) * mm});
            skLineSegment(sketch, "E1112", {"start": v(-22.32, -5.95) * mm, "end": v(-19.11, -5.95) * mm});
            skLineSegment(sketch, "E1113", {"start": v(-19.11, -5.95) * mm, "end": v(-19.11, -6.36) * mm});
            skLineSegment(sketch, "E1114", {"start": v(-19.83, -7.8) * mm, "end": v(-20.24, -7.8) * mm});
            skLineSegment(sketch, "E1115", {"start": v(-20.24, -7.8) * mm, "end": v(-20.24, -4.2) * mm});
            skLineSegment(sketch, "E1116", {"start": v(-20.24, -4.2) * mm, "end": v(-19.83, -4.2) * mm});
            skLineSegment(sketch, "E1117", {"start": v(-19.83, -4.2) * mm, "end": v(-19.83, -7.8) * mm});
            skLineSegment(sketch, "E1118", {"start": v(-0.02, -8.22) * mm, "end": v(-0.15, -8.21) * mm});
            skLineSegment(sketch, "E1119", {"start": v(-0.15, -8.21) * mm, "end": v(-0.27, -8.2) * mm});
            skLineSegment(sketch, "E1120", {"start": v(-0.27, -8.2) * mm, "end": v(-0.4, -8.18) * mm});
            skLineSegment(sketch, "E1121", {"start": v(-0.4, -8.18) * mm, "end": v(-0.5, -8.16) * mm});
            skLineSegment(sketch, "E1122", {"start": v(-0.5, -8.16) * mm, "end": v(-0.62, -8.13) * mm});
            skLineSegment(sketch, "E1123", {"start": v(-0.62, -8.13) * mm, "end": v(-0.73, -8.09) * mm});
            skLineSegment(sketch, "E1124", {"start": v(-0.73, -8.09) * mm, "end": v(-0.84, -8.04) * mm});
            skLineSegment(sketch, "E1125", {"start": v(-0.84, -8.04) * mm, "end": v(-0.94, -7.98) * mm});
            skLineSegment(sketch, "E1126", {"start": v(-0.94, -7.98) * mm, "end": v(-1.04, -7.92) * mm});
            skLineSegment(sketch, "E1127", {"start": v(-1.04, -7.92) * mm, "end": v(-1.14, -7.85) * mm});
            skLineSegment(sketch, "E1128", {"start": v(-1.14, -7.85) * mm, "end": v(-1.17, -7.82) * mm});
            skLineSegment(sketch, "E1129", {"start": v(-1.17, -7.82) * mm, "end": v(-1.21, -7.8) * mm});
            skLineSegment(sketch, "E1130", {"start": v(-1.21, -7.8) * mm, "end": v(-1.25, -7.76) * mm});
            skLineSegment(sketch, "E1131", {"start": v(-1.25, -7.76) * mm, "end": v(-1.28, -7.73) * mm});
            skLineSegment(sketch, "E1132", {"start": v(-1.28, -7.73) * mm, "end": v(-1.32, -7.7) * mm});
            skLineSegment(sketch, "E1133", {"start": v(-1.32, -7.7) * mm, "end": v(-1.35, -7.66) * mm});
            skLineSegment(sketch, "E1134", {"start": v(-1.35, -7.66) * mm, "end": v(-1.39, -7.62) * mm});
            skLineSegment(sketch, "E1135", {"start": v(-1.39, -7.62) * mm, "end": v(-1.42, -7.58) * mm});
            skLineSegment(sketch, "E1136", {"start": v(-1.42, -7.58) * mm, "end": v(-1.45, -7.54) * mm});
            skLineSegment(sketch, "E1137", {"start": v(-1.45, -7.54) * mm, "end": v(-1.48, -7.5) * mm});
            skLineSegment(sketch, "E1138", {"start": v(-1.48, -7.5) * mm, "end": v(-1.51, -7.46) * mm});
            skLineSegment(sketch, "E1139", {"start": v(-1.51, -7.46) * mm, "end": v(-1.54, -7.42) * mm});
            skLineSegment(sketch, "E1140", {"start": v(-1.54, -7.42) * mm, "end": v(-1.57, -7.37) * mm});
            skLineSegment(sketch, "E1141", {"start": v(-1.57, -7.37) * mm, "end": v(-1.6, -7.33) * mm});
            skLineSegment(sketch, "E1142", {"start": v(-1.6, -7.33) * mm, "end": v(-1.62, -7.29) * mm});
            skLineSegment(sketch, "E1143", {"start": v(-1.62, -7.29) * mm, "end": v(-1.64, -7.25) * mm});
            skLineSegment(sketch, "E1144", {"start": v(-1.64, -7.25) * mm, "end": v(-1.67, -7.2) * mm});
            skLineSegment(sketch, "E1145", {"start": v(-1.67, -7.2) * mm, "end": v(-1.69, -7.16) * mm});
            skLineSegment(sketch, "E1146", {"start": v(-1.69, -7.16) * mm, "end": v(-1.7, -7.11) * mm});
            skLineSegment(sketch, "E1147", {"start": v(-1.7, -7.11) * mm, "end": v(-1.72, -7.07) * mm});
            skLineSegment(sketch, "E1148", {"start": v(-1.72, -7.07) * mm, "end": v(-1.36, -6.92) * mm});
            skLineSegment(sketch, "E1149", {"start": v(-1.36, -6.92) * mm, "end": v(-1.35, -6.94) * mm});
            skLineSegment(sketch, "E1150", {"start": v(-1.35, -6.94) * mm, "end": v(-1.34, -6.96) * mm});
            skLineSegment(sketch, "E1151", {"start": v(-1.34, -6.96) * mm, "end": v(-1.34, -6.98) * mm});
            skLineSegment(sketch, "E1152", {"start": v(-1.34, -6.98) * mm, "end": v(-1.33, -7) * mm});
            skLineSegment(sketch, "E1153", {"start": v(-1.33, -7) * mm, "end": v(-1.32, -7.01) * mm});
            skLineSegment(sketch, "E1154", {"start": v(-1.32, -7.01) * mm, "end": v(-1.31, -7.03) * mm});
            skLineSegment(sketch, "E1155", {"start": v(-1.31, -7.03) * mm, "end": v(-1.3, -7.05) * mm});
            skLineSegment(sketch, "E1156", {"start": v(-1.3, -7.05) * mm, "end": v(-1.3, -7.07) * mm});
            skLineSegment(sketch, "E1157", {"start": v(-1.3, -7.07) * mm, "end": v(-1.28, -7.09) * mm});
            skLineSegment(sketch, "E1158", {"start": v(-1.28, -7.09) * mm, "end": v(-1.27, -7.1) * mm});
            skLineSegment(sketch, "E1159", {"start": v(-1.27, -7.1) * mm, "end": v(-1.26, -7.12) * mm});
            skLineSegment(sketch, "E1160", {"start": v(-1.26, -7.12) * mm, "end": v(-1.25, -7.14) * mm});
            skLineSegment(sketch, "E1161", {"start": v(-1.25, -7.14) * mm, "end": v(-1.24, -7.16) * mm});
            skLineSegment(sketch, "E1162", {"start": v(-1.24, -7.16) * mm, "end": v(-1.22, -7.17) * mm});
            skLineSegment(sketch, "E1163", {"start": v(-1.22, -7.17) * mm, "end": v(-1.21, -7.2) * mm});
            skLineSegment(sketch, "E1164", {"start": v(-1.21, -7.2) * mm, "end": v(-1.2, -7.2) * mm});
            skLineSegment(sketch, "E1165", {"start": v(-1.2, -7.2) * mm, "end": v(-1.19, -7.23) * mm});
            skLineSegment(sketch, "E1166", {"start": v(-1.19, -7.23) * mm, "end": v(-1.17, -7.24) * mm});
            skLineSegment(sketch, "E1167", {"start": v(-1.17, -7.24) * mm, "end": v(-1.16, -7.26) * mm});
            skLineSegment(sketch, "E1168", {"start": v(-1.16, -7.26) * mm, "end": v(-1.15, -7.28) * mm});
            skLineSegment(sketch, "E1169", {"start": v(-1.15, -7.28) * mm, "end": v(-1.14, -7.3) * mm});
            skLineSegment(sketch, "E1170", {"start": v(-1.14, -7.3) * mm, "end": v(-1.12, -7.31) * mm});
            skLineSegment(sketch, "E1171", {"start": v(-1.12, -7.31) * mm, "end": v(-1.11, -7.33) * mm});
            skLineSegment(sketch, "E1172", {"start": v(-1.11, -7.33) * mm, "end": v(-1.1, -7.34) * mm});
            skLineSegment(sketch, "E1173", {"start": v(-1.1, -7.34) * mm, "end": v(-1.08, -7.36) * mm});
            skLineSegment(sketch, "E1174", {"start": v(-1.08, -7.36) * mm, "end": v(-1.07, -7.38) * mm});
            skLineSegment(sketch, "E1175", {"start": v(-1.07, -7.38) * mm, "end": v(-1.06, -7.4) * mm});
            skLineSegment(sketch, "E1176", {"start": v(-1.06, -7.4) * mm, "end": v(-1.04, -7.4) * mm});
            skLineSegment(sketch, "E1177", {"start": v(-1.04, -7.4) * mm, "end": v(-1.03, -7.42) * mm});
            skLineSegment(sketch, "E1178", {"start": v(-1.03, -7.42) * mm, "end": v(-1.01, -7.44) * mm});
            skLineSegment(sketch, "E1179", {"start": v(-1.01, -7.44) * mm, "end": v(-1, -7.45) * mm});
            skLineSegment(sketch, "E1180", {"start": v(-1, -7.45) * mm, "end": v(-0.98, -7.47) * mm});
            skLineSegment(sketch, "E1181", {"start": v(-0.98, -7.47) * mm, "end": v(-0.97, -7.48) * mm});
            skLineSegment(sketch, "E1182", {"start": v(-0.97, -7.48) * mm, "end": v(-0.96, -7.5) * mm});
            skLineSegment(sketch, "E1183", {"start": v(-0.96, -7.5) * mm, "end": v(-0.94, -7.5) * mm});
            skLineSegment(sketch, "E1184", {"start": v(-0.94, -7.5) * mm, "end": v(-0.93, -7.52) * mm});
            skLineSegment(sketch, "E1185", {"start": v(-0.93, -7.52) * mm, "end": v(-0.91, -7.53) * mm});
            skLineSegment(sketch, "E1186", {"start": v(-0.91, -7.53) * mm, "end": v(-0.9, -7.54) * mm});
            skLineSegment(sketch, "E1187", {"start": v(-0.9, -7.54) * mm, "end": v(-0.88, -7.55) * mm});
            skLineSegment(sketch, "E1188", {"start": v(-0.88, -7.55) * mm, "end": v(-0.87, -7.56) * mm});
            skLineSegment(sketch, "E1189", {"start": v(-0.87, -7.56) * mm, "end": v(-0.8, -7.61) * mm});
            skLineSegment(sketch, "E1190", {"start": v(-0.8, -7.61) * mm, "end": v(-0.72, -7.66) * mm});
            skLineSegment(sketch, "E1191", {"start": v(-0.72, -7.66) * mm, "end": v(-0.64, -7.7) * mm});
            skLineSegment(sketch, "E1192", {"start": v(-0.64, -7.7) * mm, "end": v(-0.56, -7.73) * mm});
            skLineSegment(sketch, "E1193", {"start": v(-0.56, -7.73) * mm, "end": v(-0.48, -7.76) * mm});
            skLineSegment(sketch, "E1194", {"start": v(-0.48, -7.76) * mm, "end": v(-0.4, -7.78) * mm});
            skLineSegment(sketch, "E1195", {"start": v(-0.4, -7.78) * mm, "end": v(-0.3, -7.8) * mm});
            skLineSegment(sketch, "E1196", {"start": v(-0.3, -7.8) * mm, "end": v(-0.21, -7.81) * mm});
            skLineSegment(sketch, "E1197", {"start": v(-0.21, -7.81) * mm, "end": v(-0.12, -7.82) * mm});
            skLineSegment(sketch, "E1198", {"start": v(-0.12, -7.82) * mm, "end": v(-0.02, -7.82) * mm});
            skLineSegment(sketch, "E1199", {"start": v(-0.02, -7.82) * mm, "end": v(0.05, -7.82) * mm});
            skLineSegment(sketch, "E1200", {"start": v(0.05, -7.82) * mm, "end": v(0.1, -7.82) * mm});
            skLineSegment(sketch, "E1201", {"start": v(0.1, -7.82) * mm, "end": v(0.17, -7.81) * mm});
            skLineSegment(sketch, "E1202", {"start": v(0.17, -7.81) * mm, "end": v(0.23, -7.8) * mm});
            skLineSegment(sketch, "E1203", {"start": v(0.23, -7.8) * mm, "end": v(0.3, -7.8) * mm});
            skLineSegment(sketch, "E1204", {"start": v(0.3, -7.8) * mm, "end": v(0.35, -7.78) * mm});
            skLineSegment(sketch, "E1205", {"start": v(0.35, -7.78) * mm, "end": v(0.4, -7.77) * mm});
            skLineSegment(sketch, "E1206", {"start": v(0.4, -7.77) * mm, "end": v(0.47, -7.75) * mm});
            skLineSegment(sketch, "E1207", {"start": v(0.47, -7.75) * mm, "end": v(0.52, -7.73) * mm});
            skLineSegment(sketch, "E1208", {"start": v(0.52, -7.73) * mm, "end": v(0.57, -7.7) * mm});
            skLineSegment(sketch, "E1209", {"start": v(0.57, -7.7) * mm, "end": v(0.63, -7.69) * mm});
            skLineSegment(sketch, "E1210", {"start": v(0.63, -7.69) * mm, "end": v(0.68, -7.66) * mm});
            skLineSegment(sketch, "E1211", {"start": v(0.68, -7.66) * mm, "end": v(0.73, -7.64) * mm});
            skLineSegment(sketch, "E1212", {"start": v(0.73, -7.64) * mm, "end": v(0.77, -7.6) * mm});
            skLineSegment(sketch, "E1213", {"start": v(0.77, -7.6) * mm, "end": v(0.82, -7.58) * mm});
            skLineSegment(sketch, "E1214", {"start": v(0.82, -7.58) * mm, "end": v(0.86, -7.54) * mm});
            skLineSegment(sketch, "E1215", {"start": v(0.86, -7.54) * mm, "end": v(0.9, -7.5) * mm});
            skLineSegment(sketch, "E1216", {"start": v(0.9, -7.5) * mm, "end": v(0.95, -7.47) * mm});
            skLineSegment(sketch, "E1217", {"start": v(0.95, -7.47) * mm, "end": v(0.99, -7.44) * mm});
            skLineSegment(sketch, "E1218", {"start": v(0.99, -7.44) * mm, "end": v(1.03, -7.4) * mm});
            skLineSegment(sketch, "E1219", {"start": v(1.03, -7.4) * mm, "end": v(1.06, -7.35) * mm});
            skLineSegment(sketch, "E1220", {"start": v(1.06, -7.35) * mm, "end": v(1.1, -7.31) * mm});
            skLineSegment(sketch, "E1221", {"start": v(1.1, -7.31) * mm, "end": v(1.13, -7.27) * mm});
            skLineSegment(sketch, "E1222", {"start": v(1.13, -7.27) * mm, "end": v(1.16, -7.22) * mm});
            skLineSegment(sketch, "E1223", {"start": v(1.16, -7.22) * mm, "end": v(1.2, -7.17) * mm});
            skLineSegment(sketch, "E1224", {"start": v(1.2, -7.17) * mm, "end": v(1.22, -7.12) * mm});
            skLineSegment(sketch, "E1225", {"start": v(1.22, -7.12) * mm, "end": v(1.25, -7.07) * mm});
            skLineSegment(sketch, "E1226", {"start": v(1.25, -7.07) * mm, "end": v(1.27, -7.02) * mm});
            skLineSegment(sketch, "E1227", {"start": v(1.27, -7.02) * mm, "end": v(1.3, -6.96) * mm});
            skLineSegment(sketch, "E1228", {"start": v(1.3, -6.96) * mm, "end": v(1.32, -6.9) * mm});
            skLineSegment(sketch, "E1229", {"start": v(1.32, -6.9) * mm, "end": v(1.33, -6.85) * mm});
            skLineSegment(sketch, "E1230", {"start": v(1.33, -6.85) * mm, "end": v(1.35, -6.79) * mm});
            skLineSegment(sketch, "E1231", {"start": v(1.35, -6.79) * mm, "end": v(1.37, -6.73) * mm});
            skLineSegment(sketch, "E1232", {"start": v(1.37, -6.73) * mm, "end": v(1.38, -6.66) * mm});
            skLineSegment(sketch, "E1233", {"start": v(1.38, -6.66) * mm, "end": v(1.4, -6.6) * mm});
            skLineSegment(sketch, "E1234", {"start": v(1.4, -6.6) * mm, "end": v(1.4, -6.53) * mm});
            skLineSegment(sketch, "E1235", {"start": v(1.4, -6.53) * mm, "end": v(1.4, -6.47) * mm});
            skLineSegment(sketch, "E1236", {"start": v(1.4, -6.47) * mm, "end": v(1.41, -6.4) * mm});
            skLineSegment(sketch, "E1237", {"start": v(1.41, -6.4) * mm, "end": v(1.42, -6.33) * mm});
            skLineSegment(sketch, "E1238", {"start": v(1.42, -6.33) * mm, "end": v(1.42, -6.26) * mm});
            skLineSegment(sketch, "E1239", {"start": v(1.42, -6.26) * mm, "end": v(1.42, -6.2) * mm});
            skLineSegment(sketch, "E1240", {"start": v(1.42, -6.2) * mm, "end": v(1.42, -6.13) * mm});
            skLineSegment(sketch, "E1241", {"start": v(1.42, -6.13) * mm, "end": v(1.41, -6.06) * mm});
            skLineSegment(sketch, "E1242", {"start": v(1.41, -6.06) * mm, "end": v(1.4, -5.99) * mm});
            skLineSegment(sketch, "E1243", {"start": v(1.4, -5.99) * mm, "end": v(1.4, -5.92) * mm});
            skLineSegment(sketch, "E1244", {"start": v(1.4, -5.92) * mm, "end": v(1.4, -5.85) * mm});
            skLineSegment(sketch, "E1245", {"start": v(1.4, -5.85) * mm, "end": v(1.39, -5.8) * mm});
            skLineSegment(sketch, "E1246", {"start": v(1.39, -5.8) * mm, "end": v(1.38, -5.73) * mm});
            skLineSegment(sketch, "E1247", {"start": v(1.38, -5.73) * mm, "end": v(1.36, -5.67) * mm});
            skLineSegment(sketch, "E1248", {"start": v(1.36, -5.67) * mm, "end": v(1.35, -5.62) * mm});
            skLineSegment(sketch, "E1249", {"start": v(1.35, -5.62) * mm, "end": v(1.33, -5.56) * mm});
            skLineSegment(sketch, "E1250", {"start": v(1.33, -5.56) * mm, "end": v(1.32, -5.51) * mm});
            skLineSegment(sketch, "E1251", {"start": v(1.32, -5.51) * mm, "end": v(1.3, -5.46) * mm});
            skLineSegment(sketch, "E1252", {"start": v(1.3, -5.46) * mm, "end": v(1.28, -5.41) * mm});
            skLineSegment(sketch, "E1253", {"start": v(1.28, -5.41) * mm, "end": v(1.25, -5.36) * mm});
            skLineSegment(sketch, "E1254", {"start": v(1.25, -5.36) * mm, "end": v(1.23, -5.32) * mm});
            skLineSegment(sketch, "E1255", {"start": v(1.23, -5.32) * mm, "end": v(1.2, -5.27) * mm});
            skLineSegment(sketch, "E1256", {"start": v(1.2, -5.27) * mm, "end": v(1.18, -5.23) * mm});
            skLineSegment(sketch, "E1257", {"start": v(1.18, -5.23) * mm, "end": v(1.15, -5.18) * mm});
            skLineSegment(sketch, "E1258", {"start": v(1.15, -5.18) * mm, "end": v(1.12, -5.14) * mm});
            skLineSegment(sketch, "E1259", {"start": v(1.12, -5.14) * mm, "end": v(1.09, -5.1) * mm});
            skLineSegment(sketch, "E1260", {"start": v(1.09, -5.1) * mm, "end": v(1.05, -5.06) * mm});
            skLineSegment(sketch, "E1261", {"start": v(1.05, -5.06) * mm, "end": v(1.02, -5.02) * mm});
            skLineSegment(sketch, "E1262", {"start": v(1.02, -5.02) * mm, "end": v(0.98, -4.98) * mm});
            skLineSegment(sketch, "E1263", {"start": v(0.98, -4.98) * mm, "end": v(0.94, -4.94) * mm});
            skLineSegment(sketch, "E1264", {"start": v(0.94, -4.94) * mm, "end": v(0.9, -4.9) * mm});
            skLineSegment(sketch, "E1265", {"start": v(0.9, -4.9) * mm, "end": v(0.85, -4.87) * mm});
            skLineSegment(sketch, "E1266", {"start": v(0.85, -4.87) * mm, "end": v(0.8, -4.84) * mm});
            skLineSegment(sketch, "E1267", {"start": v(0.8, -4.84) * mm, "end": v(0.76, -4.81) * mm});
            skLineSegment(sketch, "E1268", {"start": v(0.76, -4.81) * mm, "end": v(0.7, -4.79) * mm});
            skLineSegment(sketch, "E1269", {"start": v(0.7, -4.79) * mm, "end": v(0.66, -4.76) * mm});
            skLineSegment(sketch, "E1270", {"start": v(0.66, -4.76) * mm, "end": v(0.6, -4.74) * mm});
            skLineSegment(sketch, "E1271", {"start": v(0.6, -4.74) * mm, "end": v(0.55, -4.72) * mm});
            skLineSegment(sketch, "E1272", {"start": v(0.55, -4.72) * mm, "end": v(0.5, -4.7) * mm});
            skLineSegment(sketch, "E1273", {"start": v(0.5, -4.7) * mm, "end": v(0.43, -4.68) * mm});
            skLineSegment(sketch, "E1274", {"start": v(0.43, -4.68) * mm, "end": v(0.37, -4.67) * mm});
            skLineSegment(sketch, "E1275", {"start": v(0.37, -4.67) * mm, "end": v(0.3, -4.66) * mm});
            skLineSegment(sketch, "E1276", {"start": v(0.3, -4.66) * mm, "end": v(0.24, -4.65) * mm});
            skLineSegment(sketch, "E1277", {"start": v(0.24, -4.65) * mm, "end": v(0.17, -4.65) * mm});
            skLineSegment(sketch, "E1278", {"start": v(0.17, -4.65) * mm, "end": v(0.1, -4.64) * mm});
            skLineSegment(sketch, "E1279", {"start": v(0.1, -4.64) * mm, "end": v(0.03, -4.64) * mm});
            skLineSegment(sketch, "E1280", {"start": v(0.03, -4.64) * mm, "end": v(-0.03, -4.64) * mm});
            skLineSegment(sketch, "E1281", {"start": v(-0.03, -4.64) * mm, "end": v(-0.08, -4.64) * mm});
            skLineSegment(sketch, "E1282", {"start": v(-0.08, -4.64) * mm, "end": v(-0.13, -4.65) * mm});
            skLineSegment(sketch, "E1283", {"start": v(-0.13, -4.65) * mm, "end": v(-0.18, -4.65) * mm});
            skLineSegment(sketch, "E1284", {"start": v(-0.18, -4.65) * mm, "end": v(-0.23, -4.66) * mm});
            skLineSegment(sketch, "E1285", {"start": v(-0.23, -4.66) * mm, "end": v(-0.28, -4.67) * mm});
            skLineSegment(sketch, "E1286", {"start": v(-0.28, -4.67) * mm, "end": v(-0.32, -4.68) * mm});
            skLineSegment(sketch, "E1287", {"start": v(-0.32, -4.68) * mm, "end": v(-0.37, -4.7) * mm});
            skLineSegment(sketch, "E1288", {"start": v(-0.37, -4.7) * mm, "end": v(-0.41, -4.7) * mm});
            skLineSegment(sketch, "E1289", {"start": v(-0.41, -4.7) * mm, "end": v(-0.46, -4.72) * mm});
            skLineSegment(sketch, "E1290", {"start": v(-0.46, -4.72) * mm, "end": v(-0.5, -4.73) * mm});
            skLineSegment(sketch, "E1291", {"start": v(-0.5, -4.73) * mm, "end": v(-0.54, -4.75) * mm});
            skLineSegment(sketch, "E1292", {"start": v(-0.54, -4.75) * mm, "end": v(-0.58, -4.77) * mm});
            skLineSegment(sketch, "E1293", {"start": v(-0.58, -4.77) * mm, "end": v(-0.62, -4.78) * mm});
            skLineSegment(sketch, "E1294", {"start": v(-0.62, -4.78) * mm, "end": v(-0.65, -4.8) * mm});
            skLineSegment(sketch, "E1295", {"start": v(-0.65, -4.8) * mm, "end": v(-0.68, -4.81) * mm});
            skLineSegment(sketch, "E1296", {"start": v(-0.68, -4.81) * mm, "end": v(-0.71, -4.83) * mm});
            skLineSegment(sketch, "E1297", {"start": v(-0.71, -4.83) * mm, "end": v(-0.74, -4.84) * mm});
            skLineSegment(sketch, "E1298", {"start": v(-0.74, -4.84) * mm, "end": v(-0.77, -4.86) * mm});
            skLineSegment(sketch, "E1299", {"start": v(-0.77, -4.86) * mm, "end": v(-0.8, -4.87) * mm});
            skLineSegment(sketch, "E1300", {"start": v(-0.8, -4.87) * mm, "end": v(-0.81, -4.88) * mm});
            skLineSegment(sketch, "E1301", {"start": v(-0.81, -4.88) * mm, "end": v(-0.83, -4.9) * mm});
            skLineSegment(sketch, "E1302", {"start": v(-0.83, -4.9) * mm, "end": v(-0.85, -4.9) * mm});
            skLineSegment(sketch, "E1303", {"start": v(-0.85, -4.9) * mm, "end": v(-0.87, -4.91) * mm});
            skLineSegment(sketch, "E1304", {"start": v(-0.87, -4.91) * mm, "end": v(-0.88, -4.93) * mm});
            skLineSegment(sketch, "E1305", {"start": v(-0.88, -4.93) * mm, "end": v(-0.9, -4.94) * mm});
            skLineSegment(sketch, "E1306", {"start": v(-0.9, -4.94) * mm, "end": v(-0.93, -4.95) * mm});
            skLineSegment(sketch, "E1307", {"start": v(-0.93, -4.95) * mm, "end": v(-0.95, -4.96) * mm});
            skLineSegment(sketch, "E1308", {"start": v(-0.95, -4.96) * mm, "end": v(-0.97, -4.97) * mm});
            skLineSegment(sketch, "E1309", {"start": v(-0.97, -4.97) * mm, "end": v(-1, -4.98) * mm});
            skLineSegment(sketch, "E1310", {"start": v(-1, -4.98) * mm, "end": v(-1.01, -5) * mm});
            skLineSegment(sketch, "E1311", {"start": v(-1.01, -5) * mm, "end": v(-1.03, -5) * mm});
            skLineSegment(sketch, "E1312", {"start": v(-1.03, -5) * mm, "end": v(-1.06, -5.02) * mm});
            skLineSegment(sketch, "E1313", {"start": v(-1.06, -5.02) * mm, "end": v(-1.08, -5.02) * mm});
            skLineSegment(sketch, "E1314", {"start": v(-1.08, -5.02) * mm, "end": v(-1.1, -5.03) * mm});
            skLineSegment(sketch, "E1315", {"start": v(-1.1, -5.03) * mm, "end": v(-1.12, -5.04) * mm});
            skLineSegment(sketch, "E1316", {"start": v(-1.12, -5.04) * mm, "end": v(-1.13, -5.04) * mm});
            skLineSegment(sketch, "E1317", {"start": v(-1.13, -5.04) * mm, "end": v(-1.15, -5.04) * mm});
            skLineSegment(sketch, "E1318", {"start": v(-1.15, -5.04) * mm, "end": v(-1.17, -5.05) * mm});
            skLineSegment(sketch, "E1319", {"start": v(-1.17, -5.05) * mm, "end": v(-1.19, -5.05) * mm});
            skLineSegment(sketch, "E1320", {"start": v(-1.19, -5.05) * mm, "end": v(-1.2, -5.05) * mm});
            skLineSegment(sketch, "E1321", {"start": v(-1.2, -5.05) * mm, "end": v(-1.2, -5.05) * mm});
            skLineSegment(sketch, "E1322", {"start": v(-1.2, -5.05) * mm, "end": v(-1.22, -5.05) * mm});
            skLineSegment(sketch, "E1323", {"start": v(-1.22, -5.05) * mm, "end": v(-1.23, -5.05) * mm});
            skLineSegment(sketch, "E1324", {"start": v(-1.23, -5.05) * mm, "end": v(-1.24, -5.04) * mm});
            skLineSegment(sketch, "E1325", {"start": v(-1.24, -5.04) * mm, "end": v(-1.25, -5.04) * mm});
            skLineSegment(sketch, "E1326", {"start": v(-1.25, -5.04) * mm, "end": v(-1.26, -5.04) * mm});
            skLineSegment(sketch, "E1327", {"start": v(-1.26, -5.04) * mm, "end": v(-1.26, -5.04) * mm});
            skLineSegment(sketch, "E1328", {"start": v(-1.26, -5.04) * mm, "end": v(-1.27, -5.04) * mm});
            skLineSegment(sketch, "E1329", {"start": v(-1.27, -5.04) * mm, "end": v(-1.28, -5.04) * mm});
            skLineSegment(sketch, "E1330", {"start": v(-1.28, -5.04) * mm, "end": v(-1.29, -5.03) * mm});
            skLineSegment(sketch, "E1331", {"start": v(-1.29, -5.03) * mm, "end": v(-1.3, -5.03) * mm});
            skLineSegment(sketch, "E1332", {"start": v(-1.3, -5.03) * mm, "end": v(-1.3, -5.03) * mm});
            skLineSegment(sketch, "E1333", {"start": v(-1.3, -5.03) * mm, "end": v(-1.32, -5.02) * mm});
            skLineSegment(sketch, "E1334", {"start": v(-1.32, -5.02) * mm, "end": v(-1.32, -5.02) * mm});
            skLineSegment(sketch, "E1335", {"start": v(-1.32, -5.02) * mm, "end": v(-1.33, -5.02) * mm});
            skLineSegment(sketch, "E1336", {"start": v(-1.33, -5.02) * mm, "end": v(-1.33, -5.01) * mm});
            skLineSegment(sketch, "E1337", {"start": v(-1.33, -5.01) * mm, "end": v(-1.34, -5) * mm});
            skLineSegment(sketch, "E1338", {"start": v(-1.34, -5) * mm, "end": v(-1.34, -5) * mm});
            skLineSegment(sketch, "E1339", {"start": v(-1.34, -5) * mm, "end": v(-1.35, -5) * mm});
            skLineSegment(sketch, "E1340", {"start": v(-1.35, -5) * mm, "end": v(-1.36, -5) * mm});
            skLineSegment(sketch, "E1341", {"start": v(-1.36, -5) * mm, "end": v(-1.37, -4.99) * mm});
            skLineSegment(sketch, "E1342", {"start": v(-1.37, -4.99) * mm, "end": v(-1.38, -4.98) * mm});
            skLineSegment(sketch, "E1343", {"start": v(-1.38, -4.98) * mm, "end": v(-1.38, -4.98) * mm});
            skLineSegment(sketch, "E1344", {"start": v(-1.38, -4.98) * mm, "end": v(-1.4, -4.97) * mm});
            skLineSegment(sketch, "E1345", {"start": v(-1.4, -4.97) * mm, "end": v(-1.4, -4.96) * mm});
            skLineSegment(sketch, "E1346", {"start": v(-1.4, -4.96) * mm, "end": v(-1.4, -4.96) * mm});
            skLineSegment(sketch, "E1347", {"start": v(-1.4, -4.96) * mm, "end": v(-1.42, -4.95) * mm});
            skLineSegment(sketch, "E1348", {"start": v(-1.42, -4.95) * mm, "end": v(-1.43, -4.94) * mm});
            skLineSegment(sketch, "E1349", {"start": v(-1.43, -4.94) * mm, "end": v(-1.43, -4.93) * mm});
            skLineSegment(sketch, "E1350", {"start": v(-1.43, -4.93) * mm, "end": v(-1.44, -4.92) * mm});
            skLineSegment(sketch, "E1351", {"start": v(-1.44, -4.92) * mm, "end": v(-1.45, -4.91) * mm});
            skLineSegment(sketch, "E1352", {"start": v(-1.45, -4.91) * mm, "end": v(-1.46, -4.9) * mm});
            skLineSegment(sketch, "E1353", {"start": v(-1.46, -4.9) * mm, "end": v(-1.47, -4.9) * mm});
            skLineSegment(sketch, "E1354", {"start": v(-1.47, -4.9) * mm, "end": v(-1.47, -4.88) * mm});
            skLineSegment(sketch, "E1355", {"start": v(-1.47, -4.88) * mm, "end": v(-1.48, -4.87) * mm});
            skLineSegment(sketch, "E1356", {"start": v(-1.48, -4.87) * mm, "end": v(-1.49, -4.86) * mm});
            skLineSegment(sketch, "E1357", {"start": v(-1.49, -4.86) * mm, "end": v(-1.5, -4.85) * mm});
            skLineSegment(sketch, "E1358", {"start": v(-1.5, -4.85) * mm, "end": v(-1.5, -4.83) * mm});
            skLineSegment(sketch, "E1359", {"start": v(-1.5, -4.83) * mm, "end": v(-1.5, -4.82) * mm});
            skLineSegment(sketch, "E1360", {"start": v(-1.5, -4.82) * mm, "end": v(-1.52, -4.8) * mm});
            skLineSegment(sketch, "E1361", {"start": v(-1.52, -4.8) * mm, "end": v(-1.52, -4.8) * mm});
            skLineSegment(sketch, "E1362", {"start": v(-1.52, -4.8) * mm, "end": v(-1.53, -4.78) * mm});
            skLineSegment(sketch, "E1363", {"start": v(-1.53, -4.78) * mm, "end": v(-1.53, -4.76) * mm});
            skLineSegment(sketch, "E1364", {"start": v(-1.53, -4.76) * mm, "end": v(-1.54, -4.75) * mm});
            skLineSegment(sketch, "E1365", {"start": v(-1.54, -4.75) * mm, "end": v(-1.54, -4.73) * mm});
            skLineSegment(sketch, "E1366", {"start": v(-1.54, -4.73) * mm, "end": v(-1.55, -4.71) * mm});
            skLineSegment(sketch, "E1367", {"start": v(-1.55, -4.71) * mm, "end": v(-1.55, -4.7) * mm});
            skLineSegment(sketch, "E1368", {"start": v(-1.55, -4.7) * mm, "end": v(-1.56, -4.67) * mm});
            skLineSegment(sketch, "E1369", {"start": v(-1.56, -4.67) * mm, "end": v(-1.56, -4.65) * mm});
            skLineSegment(sketch, "E1370", {"start": v(-1.56, -4.65) * mm, "end": v(-1.57, -4.63) * mm});
            skLineSegment(sketch, "E1371", {"start": v(-1.57, -4.63) * mm, "end": v(-1.57, -4.61) * mm});
            skLineSegment(sketch, "E1372", {"start": v(-1.57, -4.61) * mm, "end": v(-1.57, -4.59) * mm});
            skLineSegment(sketch, "E1373", {"start": v(-1.57, -4.59) * mm, "end": v(-1.57, -4.57) * mm});
            skLineSegment(sketch, "E1374", {"start": v(-1.57, -4.57) * mm, "end": v(-1.58, -4.54) * mm});
            skLineSegment(sketch, "E1375", {"start": v(-1.58, -4.54) * mm, "end": v(-1.58, -4.52) * mm});
            skLineSegment(sketch, "E1376", {"start": v(-1.58, -4.52) * mm, "end": v(-1.58, -4.5) * mm});
            skLineSegment(sketch, "E1377", {"start": v(-1.58, -4.5) * mm, "end": v(-1.58, -4.47) * mm});
            skLineSegment(sketch, "E1378", {"start": v(-1.58, -4.47) * mm, "end": v(-1.58, -4.44) * mm});
            skLineSegment(sketch, "E1379", {"start": v(-1.58, -4.44) * mm, "end": v(-1.58, -2.4) * mm});
            skLineSegment(sketch, "E1380", {"start": v(-1.58, -2.4) * mm, "end": v(-1.58, -2.37) * mm});
            skLineSegment(sketch, "E1381", {"start": v(-1.58, -2.37) * mm, "end": v(-1.58, -2.34) * mm});
            skLineSegment(sketch, "E1382", {"start": v(-1.58, -2.34) * mm, "end": v(-1.57, -2.3) * mm});
            skLineSegment(sketch, "E1383", {"start": v(-1.57, -2.3) * mm, "end": v(-1.57, -2.27) * mm});
            skLineSegment(sketch, "E1384", {"start": v(-1.57, -2.27) * mm, "end": v(-1.56, -2.24) * mm});
            skLineSegment(sketch, "E1385", {"start": v(-1.56, -2.24) * mm, "end": v(-1.56, -2.21) * mm});
            skLineSegment(sketch, "E1386", {"start": v(-1.56, -2.21) * mm, "end": v(-1.55, -2.18) * mm});
            skLineSegment(sketch, "E1387", {"start": v(-1.55, -2.18) * mm, "end": v(-1.54, -2.15) * mm});
            skLineSegment(sketch, "E1388", {"start": v(-1.54, -2.15) * mm, "end": v(-1.53, -2.12) * mm});
            skLineSegment(sketch, "E1389", {"start": v(-1.53, -2.12) * mm, "end": v(-1.52, -2.1) * mm});
            skLineSegment(sketch, "E1390", {"start": v(-1.52, -2.1) * mm, "end": v(-1.5, -2.06) * mm});
            skLineSegment(sketch, "E1391", {"start": v(-1.5, -2.06) * mm, "end": v(-1.49, -2.03) * mm});
            skLineSegment(sketch, "E1392", {"start": v(-1.49, -2.03) * mm, "end": v(-1.47, -2) * mm});
            skLineSegment(sketch, "E1393", {"start": v(-1.47, -2) * mm, "end": v(-1.46, -1.98) * mm});
            skLineSegment(sketch, "E1394", {"start": v(-1.46, -1.98) * mm, "end": v(-1.44, -1.95) * mm});
            skLineSegment(sketch, "E1395", {"start": v(-1.44, -1.95) * mm, "end": v(-1.42, -1.93) * mm});
            skLineSegment(sketch, "E1396", {"start": v(-1.42, -1.93) * mm, "end": v(-1.4, -1.9) * mm});
            skLineSegment(sketch, "E1397", {"start": v(-1.4, -1.9) * mm, "end": v(-1.39, -1.88) * mm});
            skLineSegment(sketch, "E1398", {"start": v(-1.39, -1.88) * mm, "end": v(-1.36, -1.86) * mm});
            skLineSegment(sketch, "E1399", {"start": v(-1.36, -1.86) * mm, "end": v(-1.34, -1.83) * mm});
            skLineSegment(sketch, "E1400", {"start": v(-1.34, -1.83) * mm, "end": v(-1.32, -1.81) * mm});
            skLineSegment(sketch, "E1401", {"start": v(-1.32, -1.81) * mm, "end": v(-1.3, -1.8) * mm});
            skLineSegment(sketch, "E1402", {"start": v(-1.3, -1.8) * mm, "end": v(-1.27, -1.77) * mm});
            skLineSegment(sketch, "E1403", {"start": v(-1.27, -1.77) * mm, "end": v(-1.25, -1.75) * mm});
            skLineSegment(sketch, "E1404", {"start": v(-1.25, -1.75) * mm, "end": v(-1.22, -1.74) * mm});
            skLineSegment(sketch, "E1405", {"start": v(-1.22, -1.74) * mm, "end": v(-1.2, -1.72) * mm});
            skLineSegment(sketch, "E1406", {"start": v(-1.2, -1.72) * mm, "end": v(-1.17, -1.7) * mm});
            skLineSegment(sketch, "E1407", {"start": v(-1.17, -1.7) * mm, "end": v(-1.14, -1.69) * mm});
            skLineSegment(sketch, "E1408", {"start": v(-1.14, -1.69) * mm, "end": v(-1.11, -1.67) * mm});
            skLineSegment(sketch, "E1409", {"start": v(-1.11, -1.67) * mm, "end": v(-1.08, -1.66) * mm});
            skLineSegment(sketch, "E1410", {"start": v(-1.08, -1.66) * mm, "end": v(-1.06, -1.65) * mm});
            skLineSegment(sketch, "E1411", {"start": v(-1.06, -1.65) * mm, "end": v(-1.02, -1.64) * mm});
            skLineSegment(sketch, "E1412", {"start": v(-1.02, -1.64) * mm, "end": v(-1, -1.63) * mm});
            skLineSegment(sketch, "E1413", {"start": v(-1, -1.63) * mm, "end": v(-0.96, -1.62) * mm});
            skLineSegment(sketch, "E1414", {"start": v(-0.96, -1.62) * mm, "end": v(-0.93, -1.61) * mm});
            skLineSegment(sketch, "E1415", {"start": v(-0.93, -1.61) * mm, "end": v(-0.9, -1.6) * mm});
            skLineSegment(sketch, "E1416", {"start": v(-0.9, -1.6) * mm, "end": v(-0.87, -1.6) * mm});
            skLineSegment(sketch, "E1417", {"start": v(-0.87, -1.6) * mm, "end": v(-0.84, -1.6) * mm});
            skLineSegment(sketch, "E1418", {"start": v(-0.84, -1.6) * mm, "end": v(-0.8, -1.6) * mm});
            skLineSegment(sketch, "E1419", {"start": v(-0.8, -1.6) * mm, "end": v(-0.77, -1.6) * mm});
            skLineSegment(sketch, "E1420", {"start": v(-0.77, -1.6) * mm, "end": v(1.48, -1.6) * mm});
            skLineSegment(sketch, "E1421", {"start": v(1.48, -1.6) * mm, "end": v(1.48, -2) * mm});
            skLineSegment(sketch, "E1422", {"start": v(1.48, -2) * mm, "end": v(-0.77, -2) * mm});
            skLineSegment(sketch, "E1423", {"start": v(-0.77, -2) * mm, "end": v(-0.8, -2) * mm});
            skLineSegment(sketch, "E1424", {"start": v(-0.8, -2) * mm, "end": v(-0.84, -2) * mm});
            skLineSegment(sketch, "E1425", {"start": v(-0.84, -2) * mm, "end": v(-0.87, -2.01) * mm});
            skLineSegment(sketch, "E1426", {"start": v(-0.87, -2.01) * mm, "end": v(-0.9, -2.02) * mm});
            skLineSegment(sketch, "E1427", {"start": v(-0.9, -2.02) * mm, "end": v(-0.93, -2.03) * mm});
            skLineSegment(sketch, "E1428", {"start": v(-0.93, -2.03) * mm, "end": v(-0.96, -2.04) * mm});
            skLineSegment(sketch, "E1429", {"start": v(-0.96, -2.04) * mm, "end": v(-0.99, -2.06) * mm});
            skLineSegment(sketch, "E1430", {"start": v(-0.99, -2.06) * mm, "end": v(-1.01, -2.08) * mm});
            skLineSegment(sketch, "E1431", {"start": v(-1.01, -2.08) * mm, "end": v(-1.04, -2.1) * mm});
            skLineSegment(sketch, "E1432", {"start": v(-1.04, -2.1) * mm, "end": v(-1.06, -2.12) * mm});
            skLineSegment(sketch, "E1433", {"start": v(-1.06, -2.12) * mm, "end": v(-1.08, -2.14) * mm});
            skLineSegment(sketch, "E1434", {"start": v(-1.08, -2.14) * mm, "end": v(-1.1, -2.17) * mm});
            skLineSegment(sketch, "E1435", {"start": v(-1.1, -2.17) * mm, "end": v(-1.12, -2.2) * mm});
            skLineSegment(sketch, "E1436", {"start": v(-1.12, -2.2) * mm, "end": v(-1.13, -2.22) * mm});
            skLineSegment(sketch, "E1437", {"start": v(-1.13, -2.22) * mm, "end": v(-1.14, -2.25) * mm});
            skLineSegment(sketch, "E1438", {"start": v(-1.14, -2.25) * mm, "end": v(-1.15, -2.28) * mm});
            skLineSegment(sketch, "E1439", {"start": v(-1.15, -2.28) * mm, "end": v(-1.16, -2.3) * mm});
            skLineSegment(sketch, "E1440", {"start": v(-1.16, -2.3) * mm, "end": v(-1.17, -2.34) * mm});
            skLineSegment(sketch, "E1441", {"start": v(-1.17, -2.34) * mm, "end": v(-1.17, -2.37) * mm});
            skLineSegment(sketch, "E1442", {"start": v(-1.17, -2.37) * mm, "end": v(-1.17, -2.4) * mm});
            skLineSegment(sketch, "E1443", {"start": v(-1.17, -2.4) * mm, "end": v(-1.17, -4.44) * mm});
            skLineSegment(sketch, "E1444", {"start": v(-1.17, -4.44) * mm, "end": v(-1.17, -4.46) * mm});
            skLineSegment(sketch, "E1445", {"start": v(-1.17, -4.46) * mm, "end": v(-1.17, -4.47) * mm});
            skLineSegment(sketch, "E1446", {"start": v(-1.17, -4.47) * mm, "end": v(-1.17, -4.49) * mm});
            skLineSegment(sketch, "E1447", {"start": v(-1.17, -4.49) * mm, "end": v(-1.17, -4.5) * mm});
            skLineSegment(sketch, "E1448", {"start": v(-1.17, -4.5) * mm, "end": v(-1.17, -4.51) * mm});
            skLineSegment(sketch, "E1449", {"start": v(-1.17, -4.51) * mm, "end": v(-1.17, -4.53) * mm});
            skLineSegment(sketch, "E1450", {"start": v(-1.17, -4.53) * mm, "end": v(-1.17, -4.54) * mm});
            skLineSegment(sketch, "E1451", {"start": v(-1.17, -4.54) * mm, "end": v(-1.17, -4.55) * mm});
            skLineSegment(sketch, "E1452", {"start": v(-1.17, -4.55) * mm, "end": v(-1.17, -4.57) * mm});
            skLineSegment(sketch, "E1453", {"start": v(-1.17, -4.57) * mm, "end": v(-1.17, -4.58) * mm});
            skLineSegment(sketch, "E1454", {"start": v(-1.17, -4.58) * mm, "end": v(-1.16, -4.6) * mm});
            skLineSegment(sketch, "E1455", {"start": v(-1.16, -4.6) * mm, "end": v(-1.16, -4.6) * mm});
            skLineSegment(sketch, "E1456", {"start": v(-1.16, -4.6) * mm, "end": v(-1.16, -4.61) * mm});
            skLineSegment(sketch, "E1457", {"start": v(-1.16, -4.61) * mm, "end": v(-1.16, -4.62) * mm});
            skLineSegment(sketch, "E1458", {"start": v(-1.16, -4.62) * mm, "end": v(-1.15, -4.63) * mm});
            skLineSegment(sketch, "E1459", {"start": v(-1.15, -4.63) * mm, "end": v(-1.15, -4.63) * mm});
            skLineSegment(sketch, "E1460", {"start": v(-1.15, -4.63) * mm, "end": v(-1.15, -4.64) * mm});
            skLineSegment(sketch, "E1461", {"start": v(-1.15, -4.64) * mm, "end": v(-1.14, -4.64) * mm});
            skLineSegment(sketch, "E1462", {"start": v(-1.14, -4.64) * mm, "end": v(-1.14, -4.64) * mm});
            skLineSegment(sketch, "E1463", {"start": v(-1.14, -4.64) * mm, "end": v(-1.13, -4.64) * mm});
            skLineSegment(sketch, "E1464", {"start": v(-1.13, -4.64) * mm, "end": v(-1.13, -4.64) * mm});
            skLineSegment(sketch, "E1465", {"start": v(-1.13, -4.64) * mm, "end": v(-1.12, -4.64) * mm});
            skLineSegment(sketch, "E1466", {"start": v(-1.12, -4.64) * mm, "end": v(-1.11, -4.64) * mm});
            skLineSegment(sketch, "E1467", {"start": v(-1.11, -4.64) * mm, "end": v(-1.1, -4.64) * mm});
            skLineSegment(sketch, "E1468", {"start": v(-1.1, -4.64) * mm, "end": v(-1.1, -4.63) * mm});
            skLineSegment(sketch, "E1469", {"start": v(-1.1, -4.63) * mm, "end": v(-1.1, -4.63) * mm});
            skLineSegment(sketch, "E1470", {"start": v(-1.1, -4.63) * mm, "end": v(-1.09, -4.63) * mm});
            skLineSegment(sketch, "E1471", {"start": v(-1.09, -4.63) * mm, "end": v(-1.08, -4.62) * mm});
            skLineSegment(sketch, "E1472", {"start": v(-1.08, -4.62) * mm, "end": v(-1.08, -4.62) * mm});
            skLineSegment(sketch, "E1473", {"start": v(-1.08, -4.62) * mm, "end": v(-1.07, -4.62) * mm});
            skLineSegment(sketch, "E1474", {"start": v(-1.07, -4.62) * mm, "end": v(-1.06, -4.61) * mm});
            skLineSegment(sketch, "E1475", {"start": v(-1.06, -4.61) * mm, "end": v(-1.05, -4.6) * mm});
            skLineSegment(sketch, "E1476", {"start": v(-1.05, -4.6) * mm, "end": v(-1.05, -4.6) * mm});
            skLineSegment(sketch, "E1477", {"start": v(-1.05, -4.6) * mm, "end": v(-1.04, -4.6) * mm});
            skLineSegment(sketch, "E1478", {"start": v(-1.04, -4.6) * mm, "end": v(-1.03, -4.6) * mm});
            skLineSegment(sketch, "E1479", {"start": v(-1.03, -4.6) * mm, "end": v(-1.03, -4.59) * mm});
            skLineSegment(sketch, "E1480", {"start": v(-1.03, -4.59) * mm, "end": v(-1.02, -4.59) * mm});
            skLineSegment(sketch, "E1481", {"start": v(-1.02, -4.59) * mm, "end": v(-1.02, -4.58) * mm});
            skLineSegment(sketch, "E1482", {"start": v(-1.02, -4.58) * mm, "end": v(-1.01, -4.58) * mm});
            skLineSegment(sketch, "E1483", {"start": v(-1.01, -4.58) * mm, "end": v(-1, -4.56) * mm});
            skLineSegment(sketch, "E1484", {"start": v(-1, -4.56) * mm, "end": v(-0.98, -4.55) * mm});
            skLineSegment(sketch, "E1485", {"start": v(-0.98, -4.55) * mm, "end": v(-0.96, -4.54) * mm});
            skLineSegment(sketch, "E1486", {"start": v(-0.96, -4.54) * mm, "end": v(-0.95, -4.53) * mm});
            skLineSegment(sketch, "E1487", {"start": v(-0.95, -4.53) * mm, "end": v(-0.93, -4.52) * mm});
            skLineSegment(sketch, "E1488", {"start": v(-0.93, -4.52) * mm, "end": v(-0.91, -4.5) * mm});
            skLineSegment(sketch, "E1489", {"start": v(-0.91, -4.5) * mm, "end": v(-0.9, -4.5) * mm});
            skLineSegment(sketch, "E1490", {"start": v(-0.9, -4.5) * mm, "end": v(-0.88, -4.49) * mm});
            skLineSegment(sketch, "E1491", {"start": v(-0.88, -4.49) * mm, "end": v(-0.86, -4.47) * mm});
            skLineSegment(sketch, "E1492", {"start": v(-0.86, -4.47) * mm, "end": v(-0.84, -4.46) * mm});
            skLineSegment(sketch, "E1493", {"start": v(-0.84, -4.46) * mm, "end": v(-0.82, -4.45) * mm});
            skLineSegment(sketch, "E1494", {"start": v(-0.82, -4.45) * mm, "end": v(-0.8, -4.44) * mm});
            skLineSegment(sketch, "E1495", {"start": v(-0.8, -4.44) * mm, "end": v(-0.78, -4.43) * mm});
            skLineSegment(sketch, "E1496", {"start": v(-0.78, -4.43) * mm, "end": v(-0.76, -4.42) * mm});
            skLineSegment(sketch, "E1497", {"start": v(-0.76, -4.42) * mm, "end": v(-0.74, -4.4) * mm});
            skLineSegment(sketch, "E1498", {"start": v(-0.74, -4.4) * mm, "end": v(-0.71, -4.4) * mm});
            skLineSegment(sketch, "E1499", {"start": v(-0.71, -4.4) * mm, "end": v(-0.7, -4.39) * mm});
            skLineSegment(sketch, "E1500", {"start": v(-0.7, -4.39) * mm, "end": v(-0.67, -4.38) * mm});
            skLineSegment(sketch, "E1501", {"start": v(-0.67, -4.38) * mm, "end": v(-0.64, -4.36) * mm});
            skLineSegment(sketch, "E1502", {"start": v(-0.64, -4.36) * mm, "end": v(-0.62, -4.35) * mm});
            skLineSegment(sketch, "E1503", {"start": v(-0.62, -4.35) * mm, "end": v(-0.6, -4.34) * mm});
            skLineSegment(sketch, "E1504", {"start": v(-0.6, -4.34) * mm, "end": v(-0.57, -4.34) * mm});
            skLineSegment(sketch, "E1505", {"start": v(-0.57, -4.34) * mm, "end": v(-0.54, -4.33) * mm});
            skLineSegment(sketch, "E1506", {"start": v(-0.54, -4.33) * mm, "end": v(-0.51, -4.32) * mm});
            skLineSegment(sketch, "E1507", {"start": v(-0.51, -4.32) * mm, "end": v(-0.49, -4.3) * mm});
            skLineSegment(sketch, "E1508", {"start": v(-0.49, -4.3) * mm, "end": v(-0.46, -4.3) * mm});
            skLineSegment(sketch, "E1509", {"start": v(-0.46, -4.3) * mm, "end": v(-0.43, -4.3) * mm});
            skLineSegment(sketch, "E1510", {"start": v(-0.43, -4.3) * mm, "end": v(-0.4, -4.29) * mm});
            skLineSegment(sketch, "E1511", {"start": v(-0.4, -4.29) * mm, "end": v(-0.37, -4.28) * mm});
            skLineSegment(sketch, "E1512", {"start": v(-0.37, -4.28) * mm, "end": v(-0.33, -4.27) * mm});
            skLineSegment(sketch, "E1513", {"start": v(-0.33, -4.27) * mm, "end": v(-0.3, -4.27) * mm});
            skLineSegment(sketch, "E1514", {"start": v(-0.3, -4.27) * mm, "end": v(-0.27, -4.26) * mm});
            skLineSegment(sketch, "E1515", {"start": v(-0.27, -4.26) * mm, "end": v(-0.24, -4.25) * mm});
            skLineSegment(sketch, "E1516", {"start": v(-0.24, -4.25) * mm, "end": v(-0.2, -4.25) * mm});
            skLineSegment(sketch, "E1517", {"start": v(-0.2, -4.25) * mm, "end": v(-0.16, -4.25) * mm});
            skLineSegment(sketch, "E1518", {"start": v(-0.16, -4.25) * mm, "end": v(-0.13, -4.24) * mm});
            skLineSegment(sketch, "E1519", {"start": v(-0.13, -4.24) * mm, "end": v(-0.1, -4.24) * mm});
            skLineSegment(sketch, "E1520", {"start": v(-0.1, -4.24) * mm, "end": v(-0.05, -4.24) * mm});
            skLineSegment(sketch, "E1521", {"start": v(-0.05, -4.24) * mm, "end": v(-0.01, -4.24) * mm});
            skLineSegment(sketch, "E1522", {"start": v(-0.01, -4.24) * mm, "end": v(0.03, -4.24) * mm});
            skLineSegment(sketch, "E1523", {"start": v(0.03, -4.24) * mm, "end": v(0.12, -4.24) * mm});
            skLineSegment(sketch, "E1524", {"start": v(0.12, -4.24) * mm, "end": v(0.21, -4.25) * mm});
            skLineSegment(sketch, "E1525", {"start": v(0.21, -4.25) * mm, "end": v(0.3, -4.25) * mm});
            skLineSegment(sketch, "E1526", {"start": v(0.3, -4.25) * mm, "end": v(0.39, -4.27) * mm});
            skLineSegment(sketch, "E1527", {"start": v(0.39, -4.27) * mm, "end": v(0.47, -4.28) * mm});
            skLineSegment(sketch, "E1528", {"start": v(0.47, -4.28) * mm, "end": v(0.55, -4.3) * mm});
            skLineSegment(sketch, "E1529", {"start": v(0.55, -4.3) * mm, "end": v(0.63, -4.32) * mm});
            skLineSegment(sketch, "E1530", {"start": v(0.63, -4.32) * mm, "end": v(0.7, -4.35) * mm});
            skLineSegment(sketch, "E1531", {"start": v(0.7, -4.35) * mm, "end": v(0.78, -4.38) * mm});
            skLineSegment(sketch, "E1532", {"start": v(0.78, -4.38) * mm, "end": v(0.85, -4.4) * mm});
            skLineSegment(sketch, "E1533", {"start": v(0.85, -4.4) * mm, "end": v(0.92, -4.44) * mm});
            skLineSegment(sketch, "E1534", {"start": v(0.92, -4.44) * mm, "end": v(0.98, -4.48) * mm});
            skLineSegment(sketch, "E1535", {"start": v(0.98, -4.48) * mm, "end": v(1.05, -4.52) * mm});
            skLineSegment(sketch, "E1536", {"start": v(1.05, -4.52) * mm, "end": v(1.1, -4.56) * mm});
            skLineSegment(sketch, "E1537", {"start": v(1.1, -4.56) * mm, "end": v(1.17, -4.61) * mm});
            skLineSegment(sketch, "E1538", {"start": v(1.17, -4.61) * mm, "end": v(1.22, -4.66) * mm});
            skLineSegment(sketch, "E1539", {"start": v(1.22, -4.66) * mm, "end": v(1.28, -4.71) * mm});
            skLineSegment(sketch, "E1540", {"start": v(1.28, -4.71) * mm, "end": v(1.33, -4.77) * mm});
            skLineSegment(sketch, "E1541", {"start": v(1.33, -4.77) * mm, "end": v(1.38, -4.82) * mm});
            skLineSegment(sketch, "E1542", {"start": v(1.38, -4.82) * mm, "end": v(1.43, -4.89) * mm});
            skLineSegment(sketch, "E1543", {"start": v(1.43, -4.89) * mm, "end": v(1.47, -4.94) * mm});
            skLineSegment(sketch, "E1544", {"start": v(1.47, -4.94) * mm, "end": v(1.5, -4.99) * mm});
            skLineSegment(sketch, "E1545", {"start": v(1.5, -4.99) * mm, "end": v(1.54, -5.04) * mm});
            skLineSegment(sketch, "E1546", {"start": v(1.54, -5.04) * mm, "end": v(1.57, -5.1) * mm});
            skLineSegment(sketch, "E1547", {"start": v(1.57, -5.1) * mm, "end": v(1.6, -5.15) * mm});
            skLineSegment(sketch, "E1548", {"start": v(1.6, -5.15) * mm, "end": v(1.63, -5.21) * mm});
            skLineSegment(sketch, "E1549", {"start": v(1.63, -5.21) * mm, "end": v(1.65, -5.27) * mm});
            skLineSegment(sketch, "E1550", {"start": v(1.65, -5.27) * mm, "end": v(1.68, -5.33) * mm});
            skLineSegment(sketch, "E1551", {"start": v(1.68, -5.33) * mm, "end": v(1.7, -5.4) * mm});
            skLineSegment(sketch, "E1552", {"start": v(1.7, -5.4) * mm, "end": v(1.72, -5.46) * mm});
            skLineSegment(sketch, "E1553", {"start": v(1.72, -5.46) * mm, "end": v(1.74, -5.52) * mm});
            skLineSegment(sketch, "E1554", {"start": v(1.74, -5.52) * mm, "end": v(1.75, -5.59) * mm});
            skLineSegment(sketch, "E1555", {"start": v(1.75, -5.59) * mm, "end": v(1.77, -5.66) * mm});
            skLineSegment(sketch, "E1556", {"start": v(1.77, -5.66) * mm, "end": v(1.78, -5.73) * mm});
            skLineSegment(sketch, "E1557", {"start": v(1.78, -5.73) * mm, "end": v(1.8, -5.8) * mm});
            skLineSegment(sketch, "E1558", {"start": v(1.8, -5.8) * mm, "end": v(1.8, -5.88) * mm});
            skLineSegment(sketch, "E1559", {"start": v(1.8, -5.88) * mm, "end": v(1.8, -5.96) * mm});
            skLineSegment(sketch, "E1560", {"start": v(1.8, -5.96) * mm, "end": v(1.81, -6.04) * mm});
            skLineSegment(sketch, "E1561", {"start": v(1.81, -6.04) * mm, "end": v(1.82, -6.12) * mm});
            skLineSegment(sketch, "E1562", {"start": v(1.82, -6.12) * mm, "end": v(1.82, -6.2) * mm});
            skLineSegment(sketch, "E1563", {"start": v(1.82, -6.2) * mm, "end": v(1.82, -6.26) * mm});
            skLineSegment(sketch, "E1564", {"start": v(1.82, -6.26) * mm, "end": v(1.82, -6.34) * mm});
            skLineSegment(sketch, "E1565", {"start": v(1.82, -6.34) * mm, "end": v(1.81, -6.42) * mm});
            skLineSegment(sketch, "E1566", {"start": v(1.81, -6.42) * mm, "end": v(1.8, -6.5) * mm});
            skLineSegment(sketch, "E1567", {"start": v(1.8, -6.5) * mm, "end": v(1.8, -6.58) * mm});
            skLineSegment(sketch, "E1568", {"start": v(1.8, -6.58) * mm, "end": v(1.79, -6.66) * mm});
            skLineSegment(sketch, "E1569", {"start": v(1.79, -6.66) * mm, "end": v(1.77, -6.74) * mm});
            skLineSegment(sketch, "E1570", {"start": v(1.77, -6.74) * mm, "end": v(1.75, -6.81) * mm});
            skLineSegment(sketch, "E1571", {"start": v(1.75, -6.81) * mm, "end": v(1.74, -6.89) * mm});
            skLineSegment(sketch, "E1572", {"start": v(1.74, -6.89) * mm, "end": v(1.71, -6.96) * mm});
            skLineSegment(sketch, "E1573", {"start": v(1.71, -6.96) * mm, "end": v(1.69, -7.03) * mm});
            skLineSegment(sketch, "E1574", {"start": v(1.69, -7.03) * mm, "end": v(1.66, -7.1) * mm});
            skLineSegment(sketch, "E1575", {"start": v(1.66, -7.1) * mm, "end": v(1.63, -7.17) * mm});
            skLineSegment(sketch, "E1576", {"start": v(1.63, -7.17) * mm, "end": v(1.6, -7.24) * mm});
            skLineSegment(sketch, "E1577", {"start": v(1.6, -7.24) * mm, "end": v(1.57, -7.3) * mm});
            skLineSegment(sketch, "E1578", {"start": v(1.57, -7.3) * mm, "end": v(1.53, -7.37) * mm});
            skLineSegment(sketch, "E1579", {"start": v(1.53, -7.37) * mm, "end": v(1.5, -7.43) * mm});
            skLineSegment(sketch, "E1580", {"start": v(1.5, -7.43) * mm, "end": v(1.46, -7.49) * mm});
            skLineSegment(sketch, "E1581", {"start": v(1.46, -7.49) * mm, "end": v(1.41, -7.55) * mm});
            skLineSegment(sketch, "E1582", {"start": v(1.41, -7.55) * mm, "end": v(1.37, -7.6) * mm});
            skLineSegment(sketch, "E1583", {"start": v(1.37, -7.6) * mm, "end": v(1.32, -7.65) * mm});
            skLineSegment(sketch, "E1584", {"start": v(1.32, -7.65) * mm, "end": v(1.27, -7.7) * mm});
            skLineSegment(sketch, "E1585", {"start": v(1.27, -7.7) * mm, "end": v(1.22, -7.76) * mm});
            skLineSegment(sketch, "E1586", {"start": v(1.22, -7.76) * mm, "end": v(1.17, -7.8) * mm});
            skLineSegment(sketch, "E1587", {"start": v(1.17, -7.8) * mm, "end": v(1.12, -7.85) * mm});
            skLineSegment(sketch, "E1588", {"start": v(1.12, -7.85) * mm, "end": v(1.06, -7.89) * mm});
            skLineSegment(sketch, "E1589", {"start": v(1.06, -7.89) * mm, "end": v(1, -7.93) * mm});
            skLineSegment(sketch, "E1590", {"start": v(1, -7.93) * mm, "end": v(0.94, -7.97) * mm});
            skLineSegment(sketch, "E1591", {"start": v(0.94, -7.97) * mm, "end": v(0.88, -8) * mm});
            skLineSegment(sketch, "E1592", {"start": v(0.88, -8) * mm, "end": v(0.81, -8.04) * mm});
            skLineSegment(sketch, "E1593", {"start": v(0.81, -8.04) * mm, "end": v(0.74, -8.07) * mm});
            skLineSegment(sketch, "E1594", {"start": v(0.74, -8.07) * mm, "end": v(0.67, -8.1) * mm});
            skLineSegment(sketch, "E1595", {"start": v(0.67, -8.1) * mm, "end": v(0.6, -8.12) * mm});
            skLineSegment(sketch, "E1596", {"start": v(0.6, -8.12) * mm, "end": v(0.53, -8.14) * mm});
            skLineSegment(sketch, "E1597", {"start": v(0.53, -8.14) * mm, "end": v(0.46, -8.16) * mm});
            skLineSegment(sketch, "E1598", {"start": v(0.46, -8.16) * mm, "end": v(0.38, -8.18) * mm});
            skLineSegment(sketch, "E1599", {"start": v(0.38, -8.18) * mm, "end": v(0.3, -8.2) * mm});
            skLineSegment(sketch, "E1600", {"start": v(0.3, -8.2) * mm, "end": v(0.23, -8.2) * mm});
            skLineSegment(sketch, "E1601", {"start": v(0.23, -8.2) * mm, "end": v(0.15, -8.21) * mm});
            skLineSegment(sketch, "E1602", {"start": v(0.15, -8.21) * mm, "end": v(0.06, -8.22) * mm});
            skLineSegment(sketch, "E1603", {"start": v(0.06, -8.22) * mm, "end": v(-0.02, -8.22) * mm});
            skLineSegment(sketch, "E1604", {"start": v(20.52, -1.48) * mm, "end": v(20.64, -1.49) * mm});
            skLineSegment(sketch, "E1605", {"start": v(20.64, -1.49) * mm, "end": v(20.77, -1.5) * mm});
            skLineSegment(sketch, "E1606", {"start": v(20.77, -1.5) * mm, "end": v(20.9, -1.52) * mm});
            skLineSegment(sketch, "E1607", {"start": v(20.9, -1.52) * mm, "end": v(21, -1.55) * mm});
            skLineSegment(sketch, "E1608", {"start": v(21, -1.55) * mm, "end": v(21.12, -1.58) * mm});
            skLineSegment(sketch, "E1609", {"start": v(21.12, -1.58) * mm, "end": v(21.23, -1.62) * mm});
            skLineSegment(sketch, "E1610", {"start": v(21.23, -1.62) * mm, "end": v(21.33, -1.67) * mm});
            skLineSegment(sketch, "E1611", {"start": v(21.33, -1.67) * mm, "end": v(21.43, -1.73) * mm});
            skLineSegment(sketch, "E1612", {"start": v(21.43, -1.73) * mm, "end": v(21.53, -1.8) * mm});
            skLineSegment(sketch, "E1613", {"start": v(21.53, -1.8) * mm, "end": v(21.62, -1.87) * mm});
            skLineSegment(sketch, "E1614", {"start": v(21.62, -1.87) * mm, "end": v(21.65, -1.9) * mm});
            skLineSegment(sketch, "E1615", {"start": v(21.65, -1.9) * mm, "end": v(21.69, -1.93) * mm});
            skLineSegment(sketch, "E1616", {"start": v(21.69, -1.93) * mm, "end": v(21.72, -1.96) * mm});
            skLineSegment(sketch, "E1617", {"start": v(21.72, -1.96) * mm, "end": v(21.75, -2) * mm});
            skLineSegment(sketch, "E1618", {"start": v(21.75, -2) * mm, "end": v(21.79, -2.03) * mm});
            skLineSegment(sketch, "E1619", {"start": v(21.79, -2.03) * mm, "end": v(21.82, -2.06) * mm});
            skLineSegment(sketch, "E1620", {"start": v(21.82, -2.06) * mm, "end": v(21.85, -2.1) * mm});
            skLineSegment(sketch, "E1621", {"start": v(21.85, -2.1) * mm, "end": v(21.88, -2.14) * mm});
            skLineSegment(sketch, "E1622", {"start": v(21.88, -2.14) * mm, "end": v(21.91, -2.17) * mm});
            skLineSegment(sketch, "E1623", {"start": v(21.91, -2.17) * mm, "end": v(21.94, -2.21) * mm});
            skLineSegment(sketch, "E1624", {"start": v(21.94, -2.21) * mm, "end": v(21.97, -2.25) * mm});
            skLineSegment(sketch, "E1625", {"start": v(21.97, -2.25) * mm, "end": v(22, -2.3) * mm});
            skLineSegment(sketch, "E1626", {"start": v(22, -2.3) * mm, "end": v(22.02, -2.33) * mm});
            skLineSegment(sketch, "E1627", {"start": v(22.02, -2.33) * mm, "end": v(22.04, -2.37) * mm});
            skLineSegment(sketch, "E1628", {"start": v(22.04, -2.37) * mm, "end": v(22.07, -2.41) * mm});
            skLineSegment(sketch, "E1629", {"start": v(22.07, -2.41) * mm, "end": v(22.09, -2.45) * mm});
            skLineSegment(sketch, "E1630", {"start": v(22.09, -2.45) * mm, "end": v(22.1, -2.5) * mm});
            skLineSegment(sketch, "E1631", {"start": v(22.1, -2.5) * mm, "end": v(22.12, -2.53) * mm});
            skLineSegment(sketch, "E1632", {"start": v(22.12, -2.53) * mm, "end": v(22.14, -2.57) * mm});
            skLineSegment(sketch, "E1633", {"start": v(22.14, -2.57) * mm, "end": v(22.15, -2.61) * mm});
            skLineSegment(sketch, "E1634", {"start": v(22.15, -2.61) * mm, "end": v(21.77, -2.78) * mm});
            skLineSegment(sketch, "E1635", {"start": v(21.77, -2.78) * mm, "end": v(21.75, -2.74) * mm});
            skLineSegment(sketch, "E1636", {"start": v(21.75, -2.74) * mm, "end": v(21.74, -2.71) * mm});
            skLineSegment(sketch, "E1637", {"start": v(21.74, -2.71) * mm, "end": v(21.72, -2.68) * mm});
            skLineSegment(sketch, "E1638", {"start": v(21.72, -2.68) * mm, "end": v(21.7, -2.65) * mm});
            skLineSegment(sketch, "E1639", {"start": v(21.7, -2.65) * mm, "end": v(21.69, -2.61) * mm});
            skLineSegment(sketch, "E1640", {"start": v(21.69, -2.61) * mm, "end": v(21.67, -2.58) * mm});
            skLineSegment(sketch, "E1641", {"start": v(21.67, -2.58) * mm, "end": v(21.65, -2.55) * mm});
            skLineSegment(sketch, "E1642", {"start": v(21.65, -2.55) * mm, "end": v(21.63, -2.52) * mm});
            skLineSegment(sketch, "E1643", {"start": v(21.63, -2.52) * mm, "end": v(21.6, -2.49) * mm});
            skLineSegment(sketch, "E1644", {"start": v(21.6, -2.49) * mm, "end": v(21.59, -2.46) * mm});
            skLineSegment(sketch, "E1645", {"start": v(21.59, -2.46) * mm, "end": v(21.56, -2.42) * mm});
            skLineSegment(sketch, "E1646", {"start": v(21.56, -2.42) * mm, "end": v(21.54, -2.4) * mm});
            skLineSegment(sketch, "E1647", {"start": v(21.54, -2.4) * mm, "end": v(21.52, -2.37) * mm});
            skLineSegment(sketch, "E1648", {"start": v(21.52, -2.37) * mm, "end": v(21.5, -2.34) * mm});
            skLineSegment(sketch, "E1649", {"start": v(21.5, -2.34) * mm, "end": v(21.47, -2.31) * mm});
            skLineSegment(sketch, "E1650", {"start": v(21.47, -2.31) * mm, "end": v(21.45, -2.28) * mm});
            skLineSegment(sketch, "E1651", {"start": v(21.45, -2.28) * mm, "end": v(21.42, -2.26) * mm});
            skLineSegment(sketch, "E1652", {"start": v(21.42, -2.26) * mm, "end": v(21.4, -2.23) * mm});
            skLineSegment(sketch, "E1653", {"start": v(21.4, -2.23) * mm, "end": v(21.37, -2.2) * mm});
            skLineSegment(sketch, "E1654", {"start": v(21.37, -2.2) * mm, "end": v(21.34, -2.19) * mm});
            skLineSegment(sketch, "E1655", {"start": v(21.34, -2.19) * mm, "end": v(21.3, -2.16) * mm});
            skLineSegment(sketch, "E1656", {"start": v(21.3, -2.16) * mm, "end": v(21.27, -2.13) * mm});
            skLineSegment(sketch, "E1657", {"start": v(21.27, -2.13) * mm, "end": v(21.24, -2.1) * mm});
            skLineSegment(sketch, "E1658", {"start": v(21.24, -2.1) * mm, "end": v(21.2, -2.09) * mm});
            skLineSegment(sketch, "E1659", {"start": v(21.2, -2.09) * mm, "end": v(21.17, -2.06) * mm});
            skLineSegment(sketch, "E1660", {"start": v(21.17, -2.06) * mm, "end": v(21.13, -2.04) * mm});
            skLineSegment(sketch, "E1661", {"start": v(21.13, -2.04) * mm, "end": v(21.09, -2.02) * mm});
            skLineSegment(sketch, "E1662", {"start": v(21.09, -2.02) * mm, "end": v(21.05, -2) * mm});
            skLineSegment(sketch, "E1663", {"start": v(21.05, -2) * mm, "end": v(21.01, -1.99) * mm});
            skLineSegment(sketch, "E1664", {"start": v(21.01, -1.99) * mm, "end": v(20.97, -1.97) * mm});
            skLineSegment(sketch, "E1665", {"start": v(20.97, -1.97) * mm, "end": v(20.93, -1.95) * mm});
            skLineSegment(sketch, "E1666", {"start": v(20.93, -1.95) * mm, "end": v(20.89, -1.94) * mm});
            skLineSegment(sketch, "E1667", {"start": v(20.89, -1.94) * mm, "end": v(20.84, -1.93) * mm});
            skLineSegment(sketch, "E1668", {"start": v(20.84, -1.93) * mm, "end": v(20.8, -1.92) * mm});
            skLineSegment(sketch, "E1669", {"start": v(20.8, -1.92) * mm, "end": v(20.75, -1.9) * mm});
            skLineSegment(sketch, "E1670", {"start": v(20.75, -1.9) * mm, "end": v(20.7, -1.9) * mm});
            skLineSegment(sketch, "E1671", {"start": v(20.7, -1.9) * mm, "end": v(20.66, -1.9) * mm});
            skLineSegment(sketch, "E1672", {"start": v(20.66, -1.9) * mm, "end": v(20.61, -1.89) * mm});
            skLineSegment(sketch, "E1673", {"start": v(20.61, -1.89) * mm, "end": v(20.56, -1.89) * mm});
            skLineSegment(sketch, "E1674", {"start": v(20.56, -1.89) * mm, "end": v(20.52, -1.89) * mm});
            skLineSegment(sketch, "E1675", {"start": v(20.52, -1.89) * mm, "end": v(20.45, -1.89) * mm});
            skLineSegment(sketch, "E1676", {"start": v(20.45, -1.89) * mm, "end": v(20.4, -1.89) * mm});
            skLineSegment(sketch, "E1677", {"start": v(20.4, -1.89) * mm, "end": v(20.34, -1.9) * mm});
            skLineSegment(sketch, "E1678", {"start": v(20.34, -1.9) * mm, "end": v(20.28, -1.9) * mm});
            skLineSegment(sketch, "E1679", {"start": v(20.28, -1.9) * mm, "end": v(20.22, -1.91) * mm});
            skLineSegment(sketch, "E1680", {"start": v(20.22, -1.91) * mm, "end": v(20.17, -1.93) * mm});
            skLineSegment(sketch, "E1681", {"start": v(20.17, -1.93) * mm, "end": v(20.11, -1.94) * mm});
            skLineSegment(sketch, "E1682", {"start": v(20.11, -1.94) * mm, "end": v(20.06, -1.96) * mm});
            skLineSegment(sketch, "E1683", {"start": v(20.06, -1.96) * mm, "end": v(20, -1.98) * mm});
            skLineSegment(sketch, "E1684", {"start": v(20, -1.98) * mm, "end": v(19.96, -2) * mm});
            skLineSegment(sketch, "E1685", {"start": v(19.96, -2) * mm, "end": v(19.9, -2.02) * mm});
            skLineSegment(sketch, "E1686", {"start": v(19.9, -2.02) * mm, "end": v(19.86, -2.04) * mm});
            skLineSegment(sketch, "E1687", {"start": v(19.86, -2.04) * mm, "end": v(19.81, -2.07) * mm});
            skLineSegment(sketch, "E1688", {"start": v(19.81, -2.07) * mm, "end": v(19.77, -2.1) * mm});
            skLineSegment(sketch, "E1689", {"start": v(19.77, -2.1) * mm, "end": v(19.73, -2.13) * mm});
            skLineSegment(sketch, "E1690", {"start": v(19.73, -2.13) * mm, "end": v(19.68, -2.16) * mm});
            skLineSegment(sketch, "E1691", {"start": v(19.68, -2.16) * mm, "end": v(19.64, -2.2) * mm});
            skLineSegment(sketch, "E1692", {"start": v(19.64, -2.2) * mm, "end": v(19.6, -2.23) * mm});
            skLineSegment(sketch, "E1693", {"start": v(19.6, -2.23) * mm, "end": v(19.57, -2.27) * mm});
            skLineSegment(sketch, "E1694", {"start": v(19.57, -2.27) * mm, "end": v(19.53, -2.3) * mm});
            skLineSegment(sketch, "E1695", {"start": v(19.53, -2.3) * mm, "end": v(19.5, -2.35) * mm});
            skLineSegment(sketch, "E1696", {"start": v(19.5, -2.35) * mm, "end": v(19.46, -2.4) * mm});
            skLineSegment(sketch, "E1697", {"start": v(19.46, -2.4) * mm, "end": v(19.43, -2.44) * mm});
            skLineSegment(sketch, "E1698", {"start": v(19.43, -2.44) * mm, "end": v(19.4, -2.49) * mm});
            skLineSegment(sketch, "E1699", {"start": v(19.4, -2.49) * mm, "end": v(19.37, -2.53) * mm});
            skLineSegment(sketch, "E1700", {"start": v(19.37, -2.53) * mm, "end": v(19.35, -2.58) * mm});
            skLineSegment(sketch, "E1701", {"start": v(19.35, -2.58) * mm, "end": v(19.32, -2.64) * mm});
            skLineSegment(sketch, "E1702", {"start": v(19.32, -2.64) * mm, "end": v(19.3, -2.69) * mm});
            skLineSegment(sketch, "E1703", {"start": v(19.3, -2.69) * mm, "end": v(19.28, -2.74) * mm});
            skLineSegment(sketch, "E1704", {"start": v(19.28, -2.74) * mm, "end": v(19.26, -2.8) * mm});
            skLineSegment(sketch, "E1705", {"start": v(19.26, -2.8) * mm, "end": v(19.24, -2.86) * mm});
            skLineSegment(sketch, "E1706", {"start": v(19.24, -2.86) * mm, "end": v(19.22, -2.92) * mm});
            skLineSegment(sketch, "E1707", {"start": v(19.22, -2.92) * mm, "end": v(19.2, -2.98) * mm});
            skLineSegment(sketch, "E1708", {"start": v(19.2, -2.98) * mm, "end": v(19.2, -3.04) * mm});
            skLineSegment(sketch, "E1709", {"start": v(19.2, -3.04) * mm, "end": v(19.19, -3.1) * mm});
            skLineSegment(sketch, "E1710", {"start": v(19.19, -3.1) * mm, "end": v(19.18, -3.17) * mm});
            skLineSegment(sketch, "E1711", {"start": v(19.18, -3.17) * mm, "end": v(19.17, -3.24) * mm});
            skLineSegment(sketch, "E1712", {"start": v(19.17, -3.24) * mm, "end": v(19.17, -3.3) * mm});
            skLineSegment(sketch, "E1713", {"start": v(19.17, -3.3) * mm, "end": v(19.16, -3.37) * mm});
            skLineSegment(sketch, "E1714", {"start": v(19.16, -3.37) * mm, "end": v(19.16, -3.45) * mm});
            skLineSegment(sketch, "E1715", {"start": v(19.16, -3.45) * mm, "end": v(19.16, -6.2) * mm});
            skLineSegment(sketch, "E1716", {"start": v(19.16, -6.2) * mm, "end": v(18.76, -6.2) * mm});
            skLineSegment(sketch, "E1717", {"start": v(18.76, -6.2) * mm, "end": v(18.76, -3.45) * mm});
            skLineSegment(sketch, "E1718", {"start": v(18.76, -3.45) * mm, "end": v(18.76, -3.36) * mm});
            skLineSegment(sketch, "E1719", {"start": v(18.76, -3.36) * mm, "end": v(18.77, -3.28) * mm});
            skLineSegment(sketch, "E1720", {"start": v(18.77, -3.28) * mm, "end": v(18.77, -3.2) * mm});
            skLineSegment(sketch, "E1721", {"start": v(18.77, -3.2) * mm, "end": v(18.78, -3.12) * mm});
            skLineSegment(sketch, "E1722", {"start": v(18.78, -3.12) * mm, "end": v(18.8, -3.04) * mm});
            skLineSegment(sketch, "E1723", {"start": v(18.8, -3.04) * mm, "end": v(18.8, -2.96) * mm});
            skLineSegment(sketch, "E1724", {"start": v(18.8, -2.96) * mm, "end": v(18.82, -2.89) * mm});
            skLineSegment(sketch, "E1725", {"start": v(18.82, -2.89) * mm, "end": v(18.84, -2.81) * mm});
            skLineSegment(sketch, "E1726", {"start": v(18.84, -2.81) * mm, "end": v(18.86, -2.74) * mm});
            skLineSegment(sketch, "E1727", {"start": v(18.86, -2.74) * mm, "end": v(18.88, -2.67) * mm});
            skLineSegment(sketch, "E1728", {"start": v(18.88, -2.67) * mm, "end": v(18.9, -2.6) * mm});
            skLineSegment(sketch, "E1729", {"start": v(18.9, -2.6) * mm, "end": v(18.93, -2.53) * mm});
            skLineSegment(sketch, "E1730", {"start": v(18.93, -2.53) * mm, "end": v(18.96, -2.46) * mm});
            skLineSegment(sketch, "E1731", {"start": v(18.96, -2.46) * mm, "end": v(19, -2.4) * mm});
            skLineSegment(sketch, "E1732", {"start": v(19, -2.4) * mm, "end": v(19.03, -2.34) * mm});
            skLineSegment(sketch, "E1733", {"start": v(19.03, -2.34) * mm, "end": v(19.06, -2.28) * mm});
            skLineSegment(sketch, "E1734", {"start": v(19.06, -2.28) * mm, "end": v(19.1, -2.22) * mm});
            skLineSegment(sketch, "E1735", {"start": v(19.1, -2.22) * mm, "end": v(19.14, -2.16) * mm});
            skLineSegment(sketch, "E1736", {"start": v(19.14, -2.16) * mm, "end": v(19.18, -2.1) * mm});
            skLineSegment(sketch, "E1737", {"start": v(19.18, -2.1) * mm, "end": v(19.23, -2.05) * mm});
            skLineSegment(sketch, "E1738", {"start": v(19.23, -2.05) * mm, "end": v(19.28, -2) * mm});
            skLineSegment(sketch, "E1739", {"start": v(19.28, -2) * mm, "end": v(19.33, -1.95) * mm});
            skLineSegment(sketch, "E1740", {"start": v(19.33, -1.95) * mm, "end": v(19.38, -1.9) * mm});
            skLineSegment(sketch, "E1741", {"start": v(19.38, -1.9) * mm, "end": v(19.43, -1.85) * mm});
            skLineSegment(sketch, "E1742", {"start": v(19.43, -1.85) * mm, "end": v(19.49, -1.8) * mm});
            skLineSegment(sketch, "E1743", {"start": v(19.49, -1.8) * mm, "end": v(19.55, -1.77) * mm});
            skLineSegment(sketch, "E1744", {"start": v(19.55, -1.77) * mm, "end": v(19.6, -1.73) * mm});
            skLineSegment(sketch, "E1745", {"start": v(19.6, -1.73) * mm, "end": v(19.67, -1.7) * mm});
            skLineSegment(sketch, "E1746", {"start": v(19.67, -1.7) * mm, "end": v(19.73, -1.66) * mm});
            skLineSegment(sketch, "E1747", {"start": v(19.73, -1.66) * mm, "end": v(19.8, -1.63) * mm});
            skLineSegment(sketch, "E1748", {"start": v(19.8, -1.63) * mm, "end": v(19.86, -1.6) * mm});
            skLineSegment(sketch, "E1749", {"start": v(19.86, -1.6) * mm, "end": v(19.92, -1.58) * mm});
            skLineSegment(sketch, "E1750", {"start": v(19.92, -1.58) * mm, "end": v(20, -1.56) * mm});
            skLineSegment(sketch, "E1751", {"start": v(20, -1.56) * mm, "end": v(20.06, -1.54) * mm});
            skLineSegment(sketch, "E1752", {"start": v(20.06, -1.54) * mm, "end": v(20.13, -1.52) * mm});
            skLineSegment(sketch, "E1753", {"start": v(20.13, -1.52) * mm, "end": v(20.2, -1.5) * mm});
            skLineSegment(sketch, "E1754", {"start": v(20.2, -1.5) * mm, "end": v(20.28, -1.5) * mm});
            skLineSegment(sketch, "E1755", {"start": v(20.28, -1.5) * mm, "end": v(20.36, -1.49) * mm});
            skLineSegment(sketch, "E1756", {"start": v(20.36, -1.49) * mm, "end": v(20.44, -1.49) * mm});
            skLineSegment(sketch, "E1757", {"start": v(20.44, -1.49) * mm, "end": v(20.52, -1.48) * mm});
            skLineSegment(sketch, "E1758", {"start": v(20.55, -4.18) * mm, "end": v(20.64, -4.19) * mm});
            skLineSegment(sketch, "E1759", {"start": v(20.64, -4.19) * mm, "end": v(20.72, -4.2) * mm});
            skLineSegment(sketch, "E1760", {"start": v(20.72, -4.2) * mm, "end": v(20.8, -4.2) * mm});
            skLineSegment(sketch, "E1761", {"start": v(20.8, -4.2) * mm, "end": v(20.89, -4.2) * mm});
            skLineSegment(sketch, "E1762", {"start": v(20.89, -4.2) * mm, "end": v(20.96, -4.22) * mm});
            skLineSegment(sketch, "E1763", {"start": v(20.96, -4.22) * mm, "end": v(21.04, -4.24) * mm});
            skLineSegment(sketch, "E1764", {"start": v(21.04, -4.24) * mm, "end": v(21.12, -4.26) * mm});
            skLineSegment(sketch, "E1765", {"start": v(21.12, -4.26) * mm, "end": v(21.19, -4.29) * mm});
            skLineSegment(sketch, "E1766", {"start": v(21.19, -4.29) * mm, "end": v(21.26, -4.31) * mm});
            skLineSegment(sketch, "E1767", {"start": v(21.26, -4.31) * mm, "end": v(21.33, -4.35) * mm});
            skLineSegment(sketch, "E1768", {"start": v(21.33, -4.35) * mm, "end": v(21.4, -4.38) * mm});
            skLineSegment(sketch, "E1769", {"start": v(21.4, -4.38) * mm, "end": v(21.46, -4.41) * mm});
            skLineSegment(sketch, "E1770", {"start": v(21.46, -4.41) * mm, "end": v(21.52, -4.45) * mm});
            skLineSegment(sketch, "E1771", {"start": v(21.52, -4.45) * mm, "end": v(21.58, -4.5) * mm});
            skLineSegment(sketch, "E1772", {"start": v(21.58, -4.5) * mm, "end": v(21.64, -4.54) * mm});
            skLineSegment(sketch, "E1773", {"start": v(21.64, -4.54) * mm, "end": v(21.7, -4.58) * mm});
            skLineSegment(sketch, "E1774", {"start": v(21.7, -4.58) * mm, "end": v(21.75, -4.63) * mm});
            skLineSegment(sketch, "E1775", {"start": v(21.75, -4.63) * mm, "end": v(21.8, -4.68) * mm});
            skLineSegment(sketch, "E1776", {"start": v(21.8, -4.68) * mm, "end": v(21.85, -4.73) * mm});
            skLineSegment(sketch, "E1777", {"start": v(21.85, -4.73) * mm, "end": v(21.9, -4.78) * mm});
            skLineSegment(sketch, "E1778", {"start": v(21.9, -4.78) * mm, "end": v(21.94, -4.84) * mm});
            skLineSegment(sketch, "E1779", {"start": v(21.94, -4.84) * mm, "end": v(21.98, -4.9) * mm});
            skLineSegment(sketch, "E1780", {"start": v(21.98, -4.9) * mm, "end": v(22.02, -4.95) * mm});
            skLineSegment(sketch, "E1781", {"start": v(22.02, -4.95) * mm, "end": v(22.05, -5.01) * mm});
            skLineSegment(sketch, "E1782", {"start": v(22.05, -5.01) * mm, "end": v(22.09, -5.08) * mm});
            skLineSegment(sketch, "E1783", {"start": v(22.09, -5.08) * mm, "end": v(22.12, -5.14) * mm});
            skLineSegment(sketch, "E1784", {"start": v(22.12, -5.14) * mm, "end": v(22.15, -5.2) * mm});
            skLineSegment(sketch, "E1785", {"start": v(22.15, -5.2) * mm, "end": v(22.18, -5.28) * mm});
            skLineSegment(sketch, "E1786", {"start": v(22.18, -5.28) * mm, "end": v(22.2, -5.35) * mm});
            skLineSegment(sketch, "E1787", {"start": v(22.2, -5.35) * mm, "end": v(22.22, -5.42) * mm});
            skLineSegment(sketch, "E1788", {"start": v(22.22, -5.42) * mm, "end": v(22.24, -5.5) * mm});
            skLineSegment(sketch, "E1789", {"start": v(22.24, -5.5) * mm, "end": v(22.26, -5.57) * mm});
            skLineSegment(sketch, "E1790", {"start": v(22.26, -5.57) * mm, "end": v(22.28, -5.65) * mm});
            skLineSegment(sketch, "E1791", {"start": v(22.28, -5.65) * mm, "end": v(22.3, -5.73) * mm});
            skLineSegment(sketch, "E1792", {"start": v(22.3, -5.73) * mm, "end": v(22.3, -5.8) * mm});
            skLineSegment(sketch, "E1793", {"start": v(22.3, -5.8) * mm, "end": v(22.31, -5.88) * mm});
            skLineSegment(sketch, "E1794", {"start": v(22.31, -5.88) * mm, "end": v(22.32, -5.96) * mm});
            skLineSegment(sketch, "E1795", {"start": v(22.32, -5.96) * mm, "end": v(22.33, -6.04) * mm});
            skLineSegment(sketch, "E1796", {"start": v(22.33, -6.04) * mm, "end": v(22.33, -6.12) * mm});
            skLineSegment(sketch, "E1797", {"start": v(22.33, -6.12) * mm, "end": v(22.33, -6.2) * mm});
            skLineSegment(sketch, "E1798", {"start": v(22.33, -6.2) * mm, "end": v(22.33, -6.27) * mm});
            skLineSegment(sketch, "E1799", {"start": v(22.33, -6.27) * mm, "end": v(22.33, -6.34) * mm});
            skLineSegment(sketch, "E1800", {"start": v(22.33, -6.34) * mm, "end": v(22.32, -6.4) * mm});
            skLineSegment(sketch, "E1801", {"start": v(22.32, -6.4) * mm, "end": v(22.32, -6.47) * mm});
            skLineSegment(sketch, "E1802", {"start": v(22.32, -6.47) * mm, "end": v(22.31, -6.53) * mm});
            skLineSegment(sketch, "E1803", {"start": v(22.31, -6.53) * mm, "end": v(22.3, -6.6) * mm});
            skLineSegment(sketch, "E1804", {"start": v(22.3, -6.6) * mm, "end": v(22.3, -6.66) * mm});
            skLineSegment(sketch, "E1805", {"start": v(22.3, -6.66) * mm, "end": v(22.28, -6.73) * mm});
            skLineSegment(sketch, "E1806", {"start": v(22.28, -6.73) * mm, "end": v(22.27, -6.8) * mm});
            skLineSegment(sketch, "E1807", {"start": v(22.27, -6.8) * mm, "end": v(22.25, -6.86) * mm});
            skLineSegment(sketch, "E1808", {"start": v(22.25, -6.86) * mm, "end": v(22.24, -6.92) * mm});
            skLineSegment(sketch, "E1809", {"start": v(22.24, -6.92) * mm, "end": v(22.22, -6.99) * mm});
            skLineSegment(sketch, "E1810", {"start": v(22.22, -6.99) * mm, "end": v(22.2, -7.05) * mm});
            skLineSegment(sketch, "E1811", {"start": v(22.2, -7.05) * mm, "end": v(22.18, -7.1) * mm});
            skLineSegment(sketch, "E1812", {"start": v(22.18, -7.1) * mm, "end": v(22.16, -7.16) * mm});
            skLineSegment(sketch, "E1813", {"start": v(22.16, -7.16) * mm, "end": v(22.13, -7.22) * mm});
            skLineSegment(sketch, "E1814", {"start": v(22.13, -7.22) * mm, "end": v(22.1, -7.28) * mm});
            skLineSegment(sketch, "E1815", {"start": v(22.1, -7.28) * mm, "end": v(22.08, -7.33) * mm});
            skLineSegment(sketch, "E1816", {"start": v(22.08, -7.33) * mm, "end": v(22.05, -7.38) * mm});
            skLineSegment(sketch, "E1817", {"start": v(22.05, -7.38) * mm, "end": v(22.02, -7.43) * mm});
            skLineSegment(sketch, "E1818", {"start": v(22.02, -7.43) * mm, "end": v(21.98, -7.5) * mm});
            skLineSegment(sketch, "E1819", {"start": v(21.98, -7.5) * mm, "end": v(21.93, -7.57) * mm});
            skLineSegment(sketch, "E1820", {"start": v(21.93, -7.57) * mm, "end": v(21.88, -7.64) * mm});
            skLineSegment(sketch, "E1821", {"start": v(21.88, -7.64) * mm, "end": v(21.82, -7.7) * mm});
            skLineSegment(sketch, "E1822", {"start": v(21.82, -7.7) * mm, "end": v(21.76, -7.76) * mm});
            skLineSegment(sketch, "E1823", {"start": v(21.76, -7.76) * mm, "end": v(21.7, -7.81) * mm});
            skLineSegment(sketch, "E1824", {"start": v(21.7, -7.81) * mm, "end": v(21.63, -7.87) * mm});
            skLineSegment(sketch, "E1825", {"start": v(21.63, -7.87) * mm, "end": v(21.57, -7.92) * mm});
            skLineSegment(sketch, "E1826", {"start": v(21.57, -7.92) * mm, "end": v(21.5, -7.96) * mm});
            skLineSegment(sketch, "E1827", {"start": v(21.5, -7.96) * mm, "end": v(21.42, -8) * mm});
            skLineSegment(sketch, "E1828", {"start": v(21.42, -8) * mm, "end": v(21.35, -8.04) * mm});
            skLineSegment(sketch, "E1829", {"start": v(21.35, -8.04) * mm, "end": v(21.27, -8.08) * mm});
            skLineSegment(sketch, "E1830", {"start": v(21.27, -8.08) * mm, "end": v(21.19, -8.11) * mm});
            skLineSegment(sketch, "E1831", {"start": v(21.19, -8.11) * mm, "end": v(21.1, -8.14) * mm});
            skLineSegment(sketch, "E1832", {"start": v(21.1, -8.14) * mm, "end": v(21.02, -8.16) * mm});
            skLineSegment(sketch, "E1833", {"start": v(21.02, -8.16) * mm, "end": v(20.93, -8.18) * mm});
            skLineSegment(sketch, "E1834", {"start": v(20.93, -8.18) * mm, "end": v(20.84, -8.2) * mm});
            skLineSegment(sketch, "E1835", {"start": v(20.84, -8.2) * mm, "end": v(20.74, -8.2) * mm});
            skLineSegment(sketch, "E1836", {"start": v(20.74, -8.2) * mm, "end": v(20.65, -8.21) * mm});
            skLineSegment(sketch, "E1837", {"start": v(20.65, -8.21) * mm, "end": v(20.55, -8.21) * mm});
            skLineSegment(sketch, "E1838", {"start": v(20.55, -8.21) * mm, "end": v(20.47, -8.21) * mm});
            skLineSegment(sketch, "E1839", {"start": v(20.47, -8.21) * mm, "end": v(20.39, -8.2) * mm});
            skLineSegment(sketch, "E1840", {"start": v(20.39, -8.2) * mm, "end": v(20.3, -8.2) * mm});
            skLineSegment(sketch, "E1841", {"start": v(20.3, -8.2) * mm, "end": v(20.23, -8.19) * mm});
            skLineSegment(sketch, "E1842", {"start": v(20.23, -8.19) * mm, "end": v(20.16, -8.18) * mm});
            skLineSegment(sketch, "E1843", {"start": v(20.16, -8.18) * mm, "end": v(20.08, -8.16) * mm});
            skLineSegment(sketch, "E1844", {"start": v(20.08, -8.16) * mm, "end": v(20.01, -8.14) * mm});
            skLineSegment(sketch, "E1845", {"start": v(20.01, -8.14) * mm, "end": v(19.94, -8.12) * mm});
            skLineSegment(sketch, "E1846", {"start": v(19.94, -8.12) * mm, "end": v(19.87, -8.1) * mm});
            skLineSegment(sketch, "E1847", {"start": v(19.87, -8.1) * mm, "end": v(19.8, -8.07) * mm});
            skLineSegment(sketch, "E1848", {"start": v(19.8, -8.07) * mm, "end": v(19.74, -8.03) * mm});
            skLineSegment(sketch, "E1849", {"start": v(19.74, -8.03) * mm, "end": v(19.68, -8) * mm});
            skLineSegment(sketch, "E1850", {"start": v(19.68, -8) * mm, "end": v(19.62, -7.97) * mm});
            skLineSegment(sketch, "E1851", {"start": v(19.62, -7.97) * mm, "end": v(19.56, -7.93) * mm});
            skLineSegment(sketch, "E1852", {"start": v(19.56, -7.93) * mm, "end": v(19.5, -7.89) * mm});
            skLineSegment(sketch, "E1853", {"start": v(19.5, -7.89) * mm, "end": v(19.45, -7.85) * mm});
            skLineSegment(sketch, "E1854", {"start": v(19.45, -7.85) * mm, "end": v(19.4, -7.8) * mm});
            skLineSegment(sketch, "E1855", {"start": v(19.4, -7.8) * mm, "end": v(19.34, -7.76) * mm});
            skLineSegment(sketch, "E1856", {"start": v(19.34, -7.76) * mm, "end": v(19.29, -7.7) * mm});
            skLineSegment(sketch, "E1857", {"start": v(19.29, -7.7) * mm, "end": v(19.24, -7.66) * mm});
            skLineSegment(sketch, "E1858", {"start": v(19.24, -7.66) * mm, "end": v(19.2, -7.6) * mm});
            skLineSegment(sketch, "E1859", {"start": v(19.2, -7.6) * mm, "end": v(19.15, -7.55) * mm});
            skLineSegment(sketch, "E1860", {"start": v(19.15, -7.55) * mm, "end": v(19.11, -7.5) * mm});
            skLineSegment(sketch, "E1861", {"start": v(19.11, -7.5) * mm, "end": v(19.07, -7.43) * mm});
            skLineSegment(sketch, "E1862", {"start": v(19.07, -7.43) * mm, "end": v(19.03, -7.37) * mm});
            skLineSegment(sketch, "E1863", {"start": v(19.03, -7.37) * mm, "end": v(19, -7.3) * mm});
            skLineSegment(sketch, "E1864", {"start": v(19, -7.3) * mm, "end": v(18.97, -7.24) * mm});
            skLineSegment(sketch, "E1865", {"start": v(18.97, -7.24) * mm, "end": v(18.94, -7.17) * mm});
            skLineSegment(sketch, "E1866", {"start": v(18.94, -7.17) * mm, "end": v(18.9, -7.1) * mm});
            skLineSegment(sketch, "E1867", {"start": v(18.9, -7.1) * mm, "end": v(18.88, -7.03) * mm});
            skLineSegment(sketch, "E1868", {"start": v(18.88, -7.03) * mm, "end": v(18.86, -6.95) * mm});
            skLineSegment(sketch, "E1869", {"start": v(18.86, -6.95) * mm, "end": v(18.84, -6.88) * mm});
            skLineSegment(sketch, "E1870", {"start": v(18.84, -6.88) * mm, "end": v(18.82, -6.8) * mm});
            skLineSegment(sketch, "E1871", {"start": v(18.82, -6.8) * mm, "end": v(18.8, -6.72) * mm});
            skLineSegment(sketch, "E1872", {"start": v(18.8, -6.72) * mm, "end": v(18.8, -6.64) * mm});
            skLineSegment(sketch, "E1873", {"start": v(18.8, -6.64) * mm, "end": v(18.78, -6.55) * mm});
            skLineSegment(sketch, "E1874", {"start": v(18.78, -6.55) * mm, "end": v(18.77, -6.47) * mm});
            skLineSegment(sketch, "E1875", {"start": v(18.77, -6.47) * mm, "end": v(18.77, -6.38) * mm});
            skLineSegment(sketch, "E1876", {"start": v(18.77, -6.38) * mm, "end": v(18.76, -6.3) * mm});
            skLineSegment(sketch, "E1877", {"start": v(18.76, -6.3) * mm, "end": v(18.76, -6.2) * mm});
            skLineSegment(sketch, "E1878", {"start": v(18.76, -6.2) * mm, "end": v(18.76, -6.18) * mm});
            skLineSegment(sketch, "E1879", {"start": v(18.76, -6.18) * mm, "end": v(18.76, -6.16) * mm});
            skLineSegment(sketch, "E1880", {"start": v(18.76, -6.16) * mm, "end": v(18.76, -6.14) * mm});
            skLineSegment(sketch, "E1881", {"start": v(18.76, -6.14) * mm, "end": v(18.77, -6.12) * mm});
            skLineSegment(sketch, "E1882", {"start": v(18.77, -6.12) * mm, "end": v(18.77, -6.1) * mm});
            skLineSegment(sketch, "E1883", {"start": v(18.77, -6.1) * mm, "end": v(18.77, -6.07) * mm});
            skLineSegment(sketch, "E1884", {"start": v(18.77, -6.07) * mm, "end": v(18.78, -6.05) * mm});
            skLineSegment(sketch, "E1885", {"start": v(18.78, -6.05) * mm, "end": v(18.78, -6.03) * mm});
            skLineSegment(sketch, "E1886", {"start": v(18.78, -6.03) * mm, "end": v(18.79, -6) * mm});
            skLineSegment(sketch, "E1887", {"start": v(18.79, -6) * mm, "end": v(18.8, -5.98) * mm});
            skLineSegment(sketch, "E1888", {"start": v(18.8, -5.98) * mm, "end": v(18.8, -5.95) * mm});
            skLineSegment(sketch, "E1889", {"start": v(18.8, -5.95) * mm, "end": v(18.8, -5.93) * mm});
            skLineSegment(sketch, "E1890", {"start": v(18.8, -5.93) * mm, "end": v(18.81, -5.9) * mm});
            skLineSegment(sketch, "E1891", {"start": v(18.81, -5.9) * mm, "end": v(18.82, -5.88) * mm});
            skLineSegment(sketch, "E1892", {"start": v(18.82, -5.88) * mm, "end": v(18.82, -5.86) * mm});
            skLineSegment(sketch, "E1893", {"start": v(18.82, -5.86) * mm, "end": v(18.83, -5.83) * mm});
            skLineSegment(sketch, "E1894", {"start": v(18.83, -5.83) * mm, "end": v(18.84, -5.8) * mm});
            skLineSegment(sketch, "E1895", {"start": v(18.84, -5.8) * mm, "end": v(18.85, -5.78) * mm});
            skLineSegment(sketch, "E1896", {"start": v(18.85, -5.78) * mm, "end": v(18.85, -5.76) * mm});
            skLineSegment(sketch, "E1897", {"start": v(18.85, -5.76) * mm, "end": v(18.86, -5.74) * mm});
            skLineSegment(sketch, "E1898", {"start": v(18.86, -5.74) * mm, "end": v(18.87, -5.71) * mm});
            skLineSegment(sketch, "E1899", {"start": v(18.87, -5.71) * mm, "end": v(18.88, -5.7) * mm});
            skLineSegment(sketch, "E1900", {"start": v(18.88, -5.7) * mm, "end": v(18.88, -5.67) * mm});
            skLineSegment(sketch, "E1901", {"start": v(18.88, -5.67) * mm, "end": v(18.9, -5.64) * mm});
            skLineSegment(sketch, "E1902", {"start": v(18.9, -5.64) * mm, "end": v(18.9, -5.62) * mm});
            skLineSegment(sketch, "E1903", {"start": v(18.9, -5.62) * mm, "end": v(18.9, -5.6) * mm});
            skLineSegment(sketch, "E1904", {"start": v(18.9, -5.6) * mm, "end": v(18.92, -5.58) * mm});
            skLineSegment(sketch, "E1905", {"start": v(18.92, -5.58) * mm, "end": v(18.93, -5.56) * mm});
            skLineSegment(sketch, "E1906", {"start": v(18.93, -5.56) * mm, "end": v(18.93, -5.54) * mm});
            skLineSegment(sketch, "E1907", {"start": v(18.93, -5.54) * mm, "end": v(18.94, -5.52) * mm});
            skLineSegment(sketch, "E1908", {"start": v(18.94, -5.52) * mm, "end": v(18.95, -5.5) * mm});
            skLineSegment(sketch, "E1909", {"start": v(18.95, -5.5) * mm, "end": v(18.96, -5.48) * mm});
            skLineSegment(sketch, "E1910", {"start": v(18.96, -5.48) * mm, "end": v(18.96, -5.46) * mm});
            skLineSegment(sketch, "E1911", {"start": v(18.96, -5.46) * mm, "end": v(18.97, -5.44) * mm});
            skLineSegment(sketch, "E1912", {"start": v(18.97, -5.44) * mm, "end": v(18.98, -5.42) * mm});
            skLineSegment(sketch, "E1913", {"start": v(18.98, -5.42) * mm, "end": v(18.98, -5.4) * mm});
            skLineSegment(sketch, "E1914", {"start": v(18.98, -5.4) * mm, "end": v(19, -5.39) * mm});
            skLineSegment(sketch, "E1915", {"start": v(19, -5.39) * mm, "end": v(19, -5.37) * mm});
            skLineSegment(sketch, "E1916", {"start": v(19, -5.37) * mm, "end": v(19, -5.36) * mm});
            skLineSegment(sketch, "E1917", {"start": v(19, -5.36) * mm, "end": v(19, -5.35) * mm});
            skLineSegment(sketch, "E1918", {"start": v(19, -5.35) * mm, "end": v(19.02, -5.3) * mm});
            skLineSegment(sketch, "E1919", {"start": v(19.02, -5.3) * mm, "end": v(19.04, -5.26) * mm});
            skLineSegment(sketch, "E1920", {"start": v(19.04, -5.26) * mm, "end": v(19.06, -5.21) * mm});
            skLineSegment(sketch, "E1921", {"start": v(19.06, -5.21) * mm, "end": v(19.08, -5.17) * mm});
            skLineSegment(sketch, "E1922", {"start": v(19.08, -5.17) * mm, "end": v(19.1, -5.12) * mm});
            skLineSegment(sketch, "E1923", {"start": v(19.1, -5.12) * mm, "end": v(19.12, -5.08) * mm});
            skLineSegment(sketch, "E1924", {"start": v(19.12, -5.08) * mm, "end": v(19.15, -5.03) * mm});
            skLineSegment(sketch, "E1925", {"start": v(19.15, -5.03) * mm, "end": v(19.17, -5) * mm});
            skLineSegment(sketch, "E1926", {"start": v(19.17, -5) * mm, "end": v(19.2, -4.95) * mm});
            skLineSegment(sketch, "E1927", {"start": v(19.2, -4.95) * mm, "end": v(19.23, -4.9) * mm});
            skLineSegment(sketch, "E1928", {"start": v(19.23, -4.9) * mm, "end": v(19.25, -4.86) * mm});
            skLineSegment(sketch, "E1929", {"start": v(19.25, -4.86) * mm, "end": v(19.28, -4.82) * mm});
            skLineSegment(sketch, "E1930", {"start": v(19.28, -4.82) * mm, "end": v(19.32, -4.78) * mm});
            skLineSegment(sketch, "E1931", {"start": v(19.32, -4.78) * mm, "end": v(19.35, -4.75) * mm});
            skLineSegment(sketch, "E1932", {"start": v(19.35, -4.75) * mm, "end": v(19.38, -4.7) * mm});
            skLineSegment(sketch, "E1933", {"start": v(19.38, -4.7) * mm, "end": v(19.42, -4.67) * mm});
            skLineSegment(sketch, "E1934", {"start": v(19.42, -4.67) * mm, "end": v(19.45, -4.64) * mm});
            skLineSegment(sketch, "E1935", {"start": v(19.45, -4.64) * mm, "end": v(19.49, -4.6) * mm});
            skLineSegment(sketch, "E1936", {"start": v(19.49, -4.6) * mm, "end": v(19.53, -4.57) * mm});
            skLineSegment(sketch, "E1937", {"start": v(19.53, -4.57) * mm, "end": v(19.56, -4.53) * mm});
            skLineSegment(sketch, "E1938", {"start": v(19.56, -4.53) * mm, "end": v(19.6, -4.5) * mm});
            skLineSegment(sketch, "E1939", {"start": v(19.6, -4.5) * mm, "end": v(19.65, -4.47) * mm});
            skLineSegment(sketch, "E1940", {"start": v(19.65, -4.47) * mm, "end": v(19.69, -4.44) * mm});
            skLineSegment(sketch, "E1941", {"start": v(19.69, -4.44) * mm, "end": v(19.73, -4.42) * mm});
            skLineSegment(sketch, "E1942", {"start": v(19.73, -4.42) * mm, "end": v(19.78, -4.39) * mm});
            skLineSegment(sketch, "E1943", {"start": v(19.78, -4.39) * mm, "end": v(19.82, -4.36) * mm});
            skLineSegment(sketch, "E1944", {"start": v(19.82, -4.36) * mm, "end": v(19.87, -4.34) * mm});
            skLineSegment(sketch, "E1945", {"start": v(19.87, -4.34) * mm, "end": v(19.91, -4.32) * mm});
            skLineSegment(sketch, "E1946", {"start": v(19.91, -4.32) * mm, "end": v(19.96, -4.3) * mm});
            skLineSegment(sketch, "E1947", {"start": v(19.96, -4.3) * mm, "end": v(20.01, -4.28) * mm});
            skLineSegment(sketch, "E1948", {"start": v(20.01, -4.28) * mm, "end": v(20.06, -4.26) * mm});
            skLineSegment(sketch, "E1949", {"start": v(20.06, -4.26) * mm, "end": v(20.11, -4.24) * mm});
            skLineSegment(sketch, "E1950", {"start": v(20.11, -4.24) * mm, "end": v(20.16, -4.23) * mm});
            skLineSegment(sketch, "E1951", {"start": v(20.16, -4.23) * mm, "end": v(20.21, -4.22) * mm});
            skLineSegment(sketch, "E1952", {"start": v(20.21, -4.22) * mm, "end": v(20.27, -4.2) * mm});
            skLineSegment(sketch, "E1953", {"start": v(20.27, -4.2) * mm, "end": v(20.32, -4.2) * mm});
            skLineSegment(sketch, "E1954", {"start": v(20.32, -4.2) * mm, "end": v(20.38, -4.2) * mm});
            skLineSegment(sketch, "E1955", {"start": v(20.38, -4.2) * mm, "end": v(20.43, -4.19) * mm});
            skLineSegment(sketch, "E1956", {"start": v(20.43, -4.19) * mm, "end": v(20.5, -4.18) * mm});
            skLineSegment(sketch, "E1957", {"start": v(20.5, -4.18) * mm, "end": v(20.55, -4.18) * mm});
            skLineSegment(sketch, "E1958", {"start": v(20.55, -7.81) * mm, "end": v(20.62, -7.8) * mm});
            skLineSegment(sketch, "E1959", {"start": v(20.62, -7.8) * mm, "end": v(20.7, -7.8) * mm});
            skLineSegment(sketch, "E1960", {"start": v(20.7, -7.8) * mm, "end": v(20.76, -7.8) * mm});
            skLineSegment(sketch, "E1961", {"start": v(20.76, -7.8) * mm, "end": v(20.83, -7.79) * mm});
            skLineSegment(sketch, "E1962", {"start": v(20.83, -7.79) * mm, "end": v(20.9, -7.77) * mm});
            skLineSegment(sketch, "E1963", {"start": v(20.9, -7.77) * mm, "end": v(20.96, -7.76) * mm});
            skLineSegment(sketch, "E1964", {"start": v(20.96, -7.76) * mm, "end": v(21.03, -7.74) * mm});
            skLineSegment(sketch, "E1965", {"start": v(21.03, -7.74) * mm, "end": v(21.09, -7.71) * mm});
            skLineSegment(sketch, "E1966", {"start": v(21.09, -7.71) * mm, "end": v(21.15, -7.69) * mm});
            skLineSegment(sketch, "E1967", {"start": v(21.15, -7.69) * mm, "end": v(21.21, -7.66) * mm});
            skLineSegment(sketch, "E1968", {"start": v(21.21, -7.66) * mm, "end": v(21.27, -7.63) * mm});
            skLineSegment(sketch, "E1969", {"start": v(21.27, -7.63) * mm, "end": v(21.32, -7.6) * mm});
            skLineSegment(sketch, "E1970", {"start": v(21.32, -7.6) * mm, "end": v(21.38, -7.56) * mm});
            skLineSegment(sketch, "E1971", {"start": v(21.38, -7.56) * mm, "end": v(21.43, -7.52) * mm});
            skLineSegment(sketch, "E1972", {"start": v(21.43, -7.52) * mm, "end": v(21.48, -7.47) * mm});
            skLineSegment(sketch, "E1973", {"start": v(21.48, -7.47) * mm, "end": v(21.52, -7.43) * mm});
            skLineSegment(sketch, "E1974", {"start": v(21.52, -7.43) * mm, "end": v(21.57, -7.38) * mm});
            skLineSegment(sketch, "E1975", {"start": v(21.57, -7.38) * mm, "end": v(21.6, -7.33) * mm});
            skLineSegment(sketch, "E1976", {"start": v(21.6, -7.33) * mm, "end": v(21.65, -7.27) * mm});
            skLineSegment(sketch, "E1977", {"start": v(21.65, -7.27) * mm, "end": v(21.69, -7.22) * mm});
            skLineSegment(sketch, "E1978", {"start": v(21.69, -7.22) * mm, "end": v(21.71, -7.18) * mm});
            skLineSegment(sketch, "E1979", {"start": v(21.71, -7.18) * mm, "end": v(21.73, -7.14) * mm});
            skLineSegment(sketch, "E1980", {"start": v(21.73, -7.14) * mm, "end": v(21.75, -7.1) * mm});
            skLineSegment(sketch, "E1981", {"start": v(21.75, -7.1) * mm, "end": v(21.77, -7.05) * mm});
            skLineSegment(sketch, "E1982", {"start": v(21.77, -7.05) * mm, "end": v(21.8, -7) * mm});
            skLineSegment(sketch, "E1983", {"start": v(21.8, -7) * mm, "end": v(21.81, -6.96) * mm});
            skLineSegment(sketch, "E1984", {"start": v(21.81, -6.96) * mm, "end": v(21.83, -6.9) * mm});
            skLineSegment(sketch, "E1985", {"start": v(21.83, -6.9) * mm, "end": v(21.84, -6.86) * mm});
            skLineSegment(sketch, "E1986", {"start": v(21.84, -6.86) * mm, "end": v(21.86, -6.8) * mm});
            skLineSegment(sketch, "E1987", {"start": v(21.86, -6.8) * mm, "end": v(21.87, -6.75) * mm});
            skLineSegment(sketch, "E1988", {"start": v(21.87, -6.75) * mm, "end": v(21.88, -6.7) * mm});
            skLineSegment(sketch, "E1989", {"start": v(21.88, -6.7) * mm, "end": v(21.9, -6.64) * mm});
            skLineSegment(sketch, "E1990", {"start": v(21.9, -6.64) * mm, "end": v(21.9, -6.59) * mm});
            skLineSegment(sketch, "E1991", {"start": v(21.9, -6.59) * mm, "end": v(21.91, -6.54) * mm});
            skLineSegment(sketch, "E1992", {"start": v(21.91, -6.54) * mm, "end": v(21.92, -6.48) * mm});
            skLineSegment(sketch, "E1993", {"start": v(21.92, -6.48) * mm, "end": v(21.92, -6.43) * mm});
            skLineSegment(sketch, "E1994", {"start": v(21.92, -6.43) * mm, "end": v(21.93, -6.37) * mm});
            skLineSegment(sketch, "E1995", {"start": v(21.93, -6.37) * mm, "end": v(21.93, -6.32) * mm});
            skLineSegment(sketch, "E1996", {"start": v(21.93, -6.32) * mm, "end": v(21.93, -6.26) * mm});
            skLineSegment(sketch, "E1997", {"start": v(21.93, -6.26) * mm, "end": v(21.93, -6.2) * mm});
            skLineSegment(sketch, "E1998", {"start": v(21.93, -6.2) * mm, "end": v(21.93, -6.13) * mm});
            skLineSegment(sketch, "E1999", {"start": v(21.93, -6.13) * mm, "end": v(21.93, -6.06) * mm});
            skLineSegment(sketch, "E2000", {"start": v(21.93, -6.06) * mm, "end": v(21.92, -6) * mm});
            skLineSegment(sketch, "E2001", {"start": v(21.92, -6) * mm, "end": v(21.92, -5.93) * mm});
            skLineSegment(sketch, "E2002", {"start": v(21.92, -5.93) * mm, "end": v(21.91, -5.86) * mm});
            skLineSegment(sketch, "E2003", {"start": v(21.91, -5.86) * mm, "end": v(21.9, -5.8) * mm});
            skLineSegment(sketch, "E2004", {"start": v(21.9, -5.8) * mm, "end": v(21.89, -5.73) * mm});
            skLineSegment(sketch, "E2005", {"start": v(21.89, -5.73) * mm, "end": v(21.88, -5.67) * mm});
            skLineSegment(sketch, "E2006", {"start": v(21.88, -5.67) * mm, "end": v(21.86, -5.6) * mm});
            skLineSegment(sketch, "E2007", {"start": v(21.86, -5.6) * mm, "end": v(21.84, -5.55) * mm});
            skLineSegment(sketch, "E2008", {"start": v(21.84, -5.55) * mm, "end": v(21.83, -5.49) * mm});
            skLineSegment(sketch, "E2009", {"start": v(21.83, -5.49) * mm, "end": v(21.8, -5.43) * mm});
            skLineSegment(sketch, "E2010", {"start": v(21.8, -5.43) * mm, "end": v(21.78, -5.37) * mm});
            skLineSegment(sketch, "E2011", {"start": v(21.78, -5.37) * mm, "end": v(21.76, -5.32) * mm});
            skLineSegment(sketch, "E2012", {"start": v(21.76, -5.32) * mm, "end": v(21.74, -5.27) * mm});
            skLineSegment(sketch, "E2013", {"start": v(21.74, -5.27) * mm, "end": v(21.7, -5.22) * mm});
            skLineSegment(sketch, "E2014", {"start": v(21.7, -5.22) * mm, "end": v(21.68, -5.17) * mm});
            skLineSegment(sketch, "E2015", {"start": v(21.68, -5.17) * mm, "end": v(21.65, -5.12) * mm});
            skLineSegment(sketch, "E2016", {"start": v(21.65, -5.12) * mm, "end": v(21.62, -5.08) * mm});
            skLineSegment(sketch, "E2017", {"start": v(21.62, -5.08) * mm, "end": v(21.59, -5.04) * mm});
            skLineSegment(sketch, "E2018", {"start": v(21.59, -5.04) * mm, "end": v(21.55, -5) * mm});
            skLineSegment(sketch, "E2019", {"start": v(21.55, -5) * mm, "end": v(21.51, -4.95) * mm});
            skLineSegment(sketch, "E2020", {"start": v(21.51, -4.95) * mm, "end": v(21.47, -4.92) * mm});
            skLineSegment(sketch, "E2021", {"start": v(21.47, -4.92) * mm, "end": v(21.43, -4.88) * mm});
            skLineSegment(sketch, "E2022", {"start": v(21.43, -4.88) * mm, "end": v(21.39, -4.85) * mm});
            skLineSegment(sketch, "E2023", {"start": v(21.39, -4.85) * mm, "end": v(21.34, -4.81) * mm});
            skLineSegment(sketch, "E2024", {"start": v(21.34, -4.81) * mm, "end": v(21.3, -4.78) * mm});
            skLineSegment(sketch, "E2025", {"start": v(21.3, -4.78) * mm, "end": v(21.25, -4.75) * mm});
            skLineSegment(sketch, "E2026", {"start": v(21.25, -4.75) * mm, "end": v(21.2, -4.73) * mm});
            skLineSegment(sketch, "E2027", {"start": v(21.2, -4.73) * mm, "end": v(21.14, -4.7) * mm});
            skLineSegment(sketch, "E2028", {"start": v(21.14, -4.7) * mm, "end": v(21.09, -4.68) * mm});
            skLineSegment(sketch, "E2029", {"start": v(21.09, -4.68) * mm, "end": v(21.04, -4.66) * mm});
            skLineSegment(sketch, "E2030", {"start": v(21.04, -4.66) * mm, "end": v(20.98, -4.64) * mm});
            skLineSegment(sketch, "E2031", {"start": v(20.98, -4.64) * mm, "end": v(20.92, -4.63) * mm});
            skLineSegment(sketch, "E2032", {"start": v(20.92, -4.63) * mm, "end": v(20.86, -4.61) * mm});
            skLineSegment(sketch, "E2033", {"start": v(20.86, -4.61) * mm, "end": v(20.8, -4.6) * mm});
            skLineSegment(sketch, "E2034", {"start": v(20.8, -4.6) * mm, "end": v(20.74, -4.6) * mm});
            skLineSegment(sketch, "E2035", {"start": v(20.74, -4.6) * mm, "end": v(20.68, -4.6) * mm});
            skLineSegment(sketch, "E2036", {"start": v(20.68, -4.6) * mm, "end": v(20.61, -4.59) * mm});
            skLineSegment(sketch, "E2037", {"start": v(20.61, -4.59) * mm, "end": v(20.55, -4.59) * mm});
            skLineSegment(sketch, "E2038", {"start": v(20.55, -4.59) * mm, "end": v(20.49, -4.59) * mm});
            skLineSegment(sketch, "E2039", {"start": v(20.49, -4.59) * mm, "end": v(20.42, -4.6) * mm});
            skLineSegment(sketch, "E2040", {"start": v(20.42, -4.6) * mm, "end": v(20.36, -4.6) * mm});
            skLineSegment(sketch, "E2041", {"start": v(20.36, -4.6) * mm, "end": v(20.3, -4.6) * mm});
            skLineSegment(sketch, "E2042", {"start": v(20.3, -4.6) * mm, "end": v(20.25, -4.62) * mm});
            skLineSegment(sketch, "E2043", {"start": v(20.25, -4.62) * mm, "end": v(20.2, -4.63) * mm});
            skLineSegment(sketch, "E2044", {"start": v(20.2, -4.63) * mm, "end": v(20.14, -4.64) * mm});
            skLineSegment(sketch, "E2045", {"start": v(20.14, -4.64) * mm, "end": v(20.08, -4.66) * mm});
            skLineSegment(sketch, "E2046", {"start": v(20.08, -4.66) * mm, "end": v(20.03, -4.68) * mm});
            skLineSegment(sketch, "E2047", {"start": v(20.03, -4.68) * mm, "end": v(19.98, -4.7) * mm});
            skLineSegment(sketch, "E2048", {"start": v(19.98, -4.7) * mm, "end": v(19.93, -4.73) * mm});
            skLineSegment(sketch, "E2049", {"start": v(19.93, -4.73) * mm, "end": v(19.88, -4.76) * mm});
            skLineSegment(sketch, "E2050", {"start": v(19.88, -4.76) * mm, "end": v(19.83, -4.79) * mm});
            skLineSegment(sketch, "E2051", {"start": v(19.83, -4.79) * mm, "end": v(19.79, -4.82) * mm});
            skLineSegment(sketch, "E2052", {"start": v(19.79, -4.82) * mm, "end": v(19.74, -4.85) * mm});
            skLineSegment(sketch, "E2053", {"start": v(19.74, -4.85) * mm, "end": v(19.7, -4.88) * mm});
            skLineSegment(sketch, "E2054", {"start": v(19.7, -4.88) * mm, "end": v(19.66, -4.92) * mm});
            skLineSegment(sketch, "E2055", {"start": v(19.66, -4.92) * mm, "end": v(19.62, -4.96) * mm});
            skLineSegment(sketch, "E2056", {"start": v(19.62, -4.96) * mm, "end": v(19.58, -5) * mm});
            skLineSegment(sketch, "E2057", {"start": v(19.58, -5) * mm, "end": v(19.54, -5.04) * mm});
            skLineSegment(sketch, "E2058", {"start": v(19.54, -5.04) * mm, "end": v(19.5, -5.08) * mm});
            skLineSegment(sketch, "E2059", {"start": v(19.5, -5.08) * mm, "end": v(19.47, -5.13) * mm});
            skLineSegment(sketch, "E2060", {"start": v(19.47, -5.13) * mm, "end": v(19.44, -5.18) * mm});
            skLineSegment(sketch, "E2061", {"start": v(19.44, -5.18) * mm, "end": v(19.41, -5.22) * mm});
            skLineSegment(sketch, "E2062", {"start": v(19.41, -5.22) * mm, "end": v(19.38, -5.28) * mm});
            skLineSegment(sketch, "E2063", {"start": v(19.38, -5.28) * mm, "end": v(19.36, -5.33) * mm});
            skLineSegment(sketch, "E2064", {"start": v(19.36, -5.33) * mm, "end": v(19.33, -5.38) * mm});
            skLineSegment(sketch, "E2065", {"start": v(19.33, -5.38) * mm, "end": v(19.3, -5.44) * mm});
            skLineSegment(sketch, "E2066", {"start": v(19.3, -5.44) * mm, "end": v(19.28, -5.5) * mm});
            skLineSegment(sketch, "E2067", {"start": v(19.28, -5.5) * mm, "end": v(19.26, -5.55) * mm});
            skLineSegment(sketch, "E2068", {"start": v(19.26, -5.55) * mm, "end": v(19.24, -5.61) * mm});
            skLineSegment(sketch, "E2069", {"start": v(19.24, -5.61) * mm, "end": v(19.23, -5.67) * mm});
            skLineSegment(sketch, "E2070", {"start": v(19.23, -5.67) * mm, "end": v(19.21, -5.74) * mm});
            skLineSegment(sketch, "E2071", {"start": v(19.21, -5.74) * mm, "end": v(19.2, -5.8) * mm});
            skLineSegment(sketch, "E2072", {"start": v(19.2, -5.8) * mm, "end": v(19.19, -5.86) * mm});
            skLineSegment(sketch, "E2073", {"start": v(19.19, -5.86) * mm, "end": v(19.18, -5.93) * mm});
            skLineSegment(sketch, "E2074", {"start": v(19.18, -5.93) * mm, "end": v(19.17, -6) * mm});
            skLineSegment(sketch, "E2075", {"start": v(19.17, -6) * mm, "end": v(19.17, -6.07) * mm});
            skLineSegment(sketch, "E2076", {"start": v(19.17, -6.07) * mm, "end": v(19.16, -6.13) * mm});
            skLineSegment(sketch, "E2077", {"start": v(19.16, -6.13) * mm, "end": v(19.16, -6.2) * mm});
            skLineSegment(sketch, "E2078", {"start": v(19.16, -6.2) * mm, "end": v(19.16, -6.28) * mm});
            skLineSegment(sketch, "E2079", {"start": v(19.16, -6.28) * mm, "end": v(19.17, -6.35) * mm});
            skLineSegment(sketch, "E2080", {"start": v(19.17, -6.35) * mm, "end": v(19.17, -6.42) * mm});
            skLineSegment(sketch, "E2081", {"start": v(19.17, -6.42) * mm, "end": v(19.18, -6.49) * mm});
            skLineSegment(sketch, "E2082", {"start": v(19.18, -6.49) * mm, "end": v(19.19, -6.55) * mm});
            skLineSegment(sketch, "E2083", {"start": v(19.19, -6.55) * mm, "end": v(19.2, -6.62) * mm});
            skLineSegment(sketch, "E2084", {"start": v(19.2, -6.62) * mm, "end": v(19.2, -6.68) * mm});
            skLineSegment(sketch, "E2085", {"start": v(19.2, -6.68) * mm, "end": v(19.22, -6.74) * mm});
            skLineSegment(sketch, "E2086", {"start": v(19.22, -6.74) * mm, "end": v(19.24, -6.8) * mm});
            skLineSegment(sketch, "E2087", {"start": v(19.24, -6.8) * mm, "end": v(19.25, -6.87) * mm});
            skLineSegment(sketch, "E2088", {"start": v(19.25, -6.87) * mm, "end": v(19.27, -6.92) * mm});
            skLineSegment(sketch, "E2089", {"start": v(19.27, -6.92) * mm, "end": v(19.3, -6.98) * mm});
            skLineSegment(sketch, "E2090", {"start": v(19.3, -6.98) * mm, "end": v(19.31, -7.03) * mm});
            skLineSegment(sketch, "E2091", {"start": v(19.31, -7.03) * mm, "end": v(19.34, -7.09) * mm});
            skLineSegment(sketch, "E2092", {"start": v(19.34, -7.09) * mm, "end": v(19.36, -7.14) * mm});
            skLineSegment(sketch, "E2093", {"start": v(19.36, -7.14) * mm, "end": v(19.4, -7.19) * mm});
            skLineSegment(sketch, "E2094", {"start": v(19.4, -7.19) * mm, "end": v(19.42, -7.24) * mm});
            skLineSegment(sketch, "E2095", {"start": v(19.42, -7.24) * mm, "end": v(19.45, -7.28) * mm});
            skLineSegment(sketch, "E2096", {"start": v(19.45, -7.28) * mm, "end": v(19.48, -7.33) * mm});
            skLineSegment(sketch, "E2097", {"start": v(19.48, -7.33) * mm, "end": v(19.52, -7.37) * mm});
            skLineSegment(sketch, "E2098", {"start": v(19.52, -7.37) * mm, "end": v(19.55, -7.4) * mm});
            skLineSegment(sketch, "E2099", {"start": v(19.55, -7.4) * mm, "end": v(19.6, -7.45) * mm});
            skLineSegment(sketch, "E2100", {"start": v(19.6, -7.45) * mm, "end": v(19.63, -7.48) * mm});
            skLineSegment(sketch, "E2101", {"start": v(19.63, -7.48) * mm, "end": v(19.67, -7.52) * mm});
            skLineSegment(sketch, "E2102", {"start": v(19.67, -7.52) * mm, "end": v(19.72, -7.55) * mm});
            skLineSegment(sketch, "E2103", {"start": v(19.72, -7.55) * mm, "end": v(19.76, -7.59) * mm});
            skLineSegment(sketch, "E2104", {"start": v(19.76, -7.59) * mm, "end": v(19.8, -7.62) * mm});
            skLineSegment(sketch, "E2105", {"start": v(19.8, -7.62) * mm, "end": v(19.86, -7.64) * mm});
            skLineSegment(sketch, "E2106", {"start": v(19.86, -7.64) * mm, "end": v(19.9, -7.67) * mm});
            skLineSegment(sketch, "E2107", {"start": v(19.9, -7.67) * mm, "end": v(19.96, -7.7) * mm});
            skLineSegment(sketch, "E2108", {"start": v(19.96, -7.7) * mm, "end": v(20.01, -7.72) * mm});
            skLineSegment(sketch, "E2109", {"start": v(20.01, -7.72) * mm, "end": v(20.06, -7.74) * mm});
            skLineSegment(sketch, "E2110", {"start": v(20.06, -7.74) * mm, "end": v(20.12, -7.75) * mm});
            skLineSegment(sketch, "E2111", {"start": v(20.12, -7.75) * mm, "end": v(20.18, -7.77) * mm});
            skLineSegment(sketch, "E2112", {"start": v(20.18, -7.77) * mm, "end": v(20.24, -7.78) * mm});
            skLineSegment(sketch, "E2113", {"start": v(20.24, -7.78) * mm, "end": v(20.3, -7.8) * mm});
            skLineSegment(sketch, "E2114", {"start": v(20.3, -7.8) * mm, "end": v(20.36, -7.8) * mm});
            skLineSegment(sketch, "E2115", {"start": v(20.36, -7.8) * mm, "end": v(20.42, -7.8) * mm});
            skLineSegment(sketch, "E2116", {"start": v(20.42, -7.8) * mm, "end": v(20.48, -7.81) * mm});
            skLineSegment(sketch, "E2117", {"start": v(20.48, -7.81) * mm, "end": v(20.55, -7.81) * mm});
            skLineSegment(sketch, "E2118", {"start": v(-20.8, -28.6) * mm, "end": v(-21.18, -28.47) * mm});
            skLineSegment(sketch, "E2119", {"start": v(-21.18, -28.47) * mm, "end": v(-19.24, -22.93) * mm});
            skLineSegment(sketch, "E2120", {"start": v(-19.24, -22.93) * mm, "end": v(-19.23, -22.88) * mm});
            skLineSegment(sketch, "E2121", {"start": v(-19.23, -22.88) * mm, "end": v(-19.22, -22.83) * mm});
            skLineSegment(sketch, "E2122", {"start": v(-19.22, -22.83) * mm, "end": v(-19.22, -22.79) * mm});
            skLineSegment(sketch, "E2123", {"start": v(-19.22, -22.79) * mm, "end": v(-19.21, -22.74) * mm});
            skLineSegment(sketch, "E2124", {"start": v(-19.21, -22.74) * mm, "end": v(-19.22, -22.7) * mm});
            skLineSegment(sketch, "E2125", {"start": v(-19.22, -22.7) * mm, "end": v(-19.22, -22.66) * mm});
            skLineSegment(sketch, "E2126", {"start": v(-19.22, -22.66) * mm, "end": v(-19.23, -22.63) * mm});
            skLineSegment(sketch, "E2127", {"start": v(-19.23, -22.63) * mm, "end": v(-19.24, -22.6) * mm});
            skLineSegment(sketch, "E2128", {"start": v(-19.24, -22.6) * mm, "end": v(-19.25, -22.57) * mm});
            skLineSegment(sketch, "E2129", {"start": v(-19.25, -22.57) * mm, "end": v(-19.27, -22.54) * mm});
            skLineSegment(sketch, "E2130", {"start": v(-19.27, -22.54) * mm, "end": v(-19.28, -22.53) * mm});
            skLineSegment(sketch, "E2131", {"start": v(-19.28, -22.53) * mm, "end": v(-19.3, -22.52) * mm});
            skLineSegment(sketch, "E2132", {"start": v(-19.3, -22.52) * mm, "end": v(-19.3, -22.5) * mm});
            skLineSegment(sketch, "E2133", {"start": v(-19.3, -22.5) * mm, "end": v(-19.32, -22.5) * mm});
            skLineSegment(sketch, "E2134", {"start": v(-19.32, -22.5) * mm, "end": v(-19.33, -22.49) * mm});
            skLineSegment(sketch, "E2135", {"start": v(-19.33, -22.49) * mm, "end": v(-19.35, -22.48) * mm});
            skLineSegment(sketch, "E2136", {"start": v(-19.35, -22.48) * mm, "end": v(-19.36, -22.47) * mm});
            skLineSegment(sketch, "E2137", {"start": v(-19.36, -22.47) * mm, "end": v(-19.38, -22.46) * mm});
            skLineSegment(sketch, "E2138", {"start": v(-19.38, -22.46) * mm, "end": v(-19.4, -22.46) * mm});
            skLineSegment(sketch, "E2139", {"start": v(-19.4, -22.46) * mm, "end": v(-19.4, -22.46) * mm});
            skLineSegment(sketch, "E2140", {"start": v(-19.4, -22.46) * mm, "end": v(-19.42, -22.45) * mm});
            skLineSegment(sketch, "E2141", {"start": v(-19.42, -22.45) * mm, "end": v(-19.44, -22.45) * mm});
            skLineSegment(sketch, "E2142", {"start": v(-19.44, -22.45) * mm, "end": v(-19.45, -22.45) * mm});
            skLineSegment(sketch, "E2143", {"start": v(-19.45, -22.45) * mm, "end": v(-19.46, -22.44) * mm});
            skLineSegment(sketch, "E2144", {"start": v(-19.46, -22.44) * mm, "end": v(-19.48, -22.44) * mm});
            skLineSegment(sketch, "E2145", {"start": v(-19.48, -22.44) * mm, "end": v(-19.5, -22.44) * mm});
            skLineSegment(sketch, "E2146", {"start": v(-19.5, -22.44) * mm, "end": v(-19.5, -22.44) * mm});
            skLineSegment(sketch, "E2147", {"start": v(-19.5, -22.44) * mm, "end": v(-19.51, -22.44) * mm});
            skLineSegment(sketch, "E2148", {"start": v(-19.51, -22.44) * mm, "end": v(-19.52, -22.44) * mm});
            skLineSegment(sketch, "E2149", {"start": v(-19.52, -22.44) * mm, "end": v(-19.54, -22.44) * mm});
            skLineSegment(sketch, "E2150", {"start": v(-19.54, -22.44) * mm, "end": v(-22.17, -22.44) * mm});
            skLineSegment(sketch, "E2151", {"start": v(-22.17, -22.44) * mm, "end": v(-22.17, -22.04) * mm});
            skLineSegment(sketch, "E2152", {"start": v(-22.17, -22.04) * mm, "end": v(-19.54, -22.04) * mm});
            skLineSegment(sketch, "E2153", {"start": v(-19.54, -22.04) * mm, "end": v(-19.5, -22.04) * mm});
            skLineSegment(sketch, "E2154", {"start": v(-19.5, -22.04) * mm, "end": v(-19.46, -22.04) * mm});
            skLineSegment(sketch, "E2155", {"start": v(-19.46, -22.04) * mm, "end": v(-19.43, -22.04) * mm});
            skLineSegment(sketch, "E2156", {"start": v(-19.43, -22.04) * mm, "end": v(-19.4, -22.05) * mm});
            skLineSegment(sketch, "E2157", {"start": v(-19.4, -22.05) * mm, "end": v(-19.36, -22.05) * mm});
            skLineSegment(sketch, "E2158", {"start": v(-19.36, -22.05) * mm, "end": v(-19.33, -22.06) * mm});
            skLineSegment(sketch, "E2159", {"start": v(-19.33, -22.06) * mm, "end": v(-19.3, -22.07) * mm});
            skLineSegment(sketch, "E2160", {"start": v(-19.3, -22.07) * mm, "end": v(-19.26, -22.08) * mm});
            skLineSegment(sketch, "E2161", {"start": v(-19.26, -22.08) * mm, "end": v(-19.23, -22.09) * mm});
            skLineSegment(sketch, "E2162", {"start": v(-19.23, -22.09) * mm, "end": v(-19.2, -22.1) * mm});
            skLineSegment(sketch, "E2163", {"start": v(-19.2, -22.1) * mm, "end": v(-19.17, -22.12) * mm});
            skLineSegment(sketch, "E2164", {"start": v(-19.17, -22.12) * mm, "end": v(-19.14, -22.13) * mm});
            skLineSegment(sketch, "E2165", {"start": v(-19.14, -22.13) * mm, "end": v(-19.12, -22.15) * mm});
            skLineSegment(sketch, "E2166", {"start": v(-19.12, -22.15) * mm, "end": v(-19.09, -22.17) * mm});
            skLineSegment(sketch, "E2167", {"start": v(-19.09, -22.17) * mm, "end": v(-19.06, -22.18) * mm});
            skLineSegment(sketch, "E2168", {"start": v(-19.06, -22.18) * mm, "end": v(-19.04, -22.2) * mm});
            skLineSegment(sketch, "E2169", {"start": v(-19.04, -22.2) * mm, "end": v(-19.02, -22.23) * mm});
            skLineSegment(sketch, "E2170", {"start": v(-19.02, -22.23) * mm, "end": v(-19, -22.25) * mm});
            skLineSegment(sketch, "E2171", {"start": v(-19, -22.25) * mm, "end": v(-18.97, -22.27) * mm});
            skLineSegment(sketch, "E2172", {"start": v(-18.97, -22.27) * mm, "end": v(-18.95, -22.3) * mm});
            skLineSegment(sketch, "E2173", {"start": v(-18.95, -22.3) * mm, "end": v(-18.95, -22.3) * mm});
            skLineSegment(sketch, "E2174", {"start": v(-18.95, -22.3) * mm, "end": v(-18.94, -22.32) * mm});
            skLineSegment(sketch, "E2175", {"start": v(-18.94, -22.32) * mm, "end": v(-18.93, -22.33) * mm});
            skLineSegment(sketch, "E2176", {"start": v(-18.93, -22.33) * mm, "end": v(-18.92, -22.34) * mm});
            skLineSegment(sketch, "E2177", {"start": v(-18.92, -22.34) * mm, "end": v(-18.92, -22.35) * mm});
            skLineSegment(sketch, "E2178", {"start": v(-18.92, -22.35) * mm, "end": v(-18.91, -22.37) * mm});
            skLineSegment(sketch, "E2179", {"start": v(-18.91, -22.37) * mm, "end": v(-18.9, -22.38) * mm});
            skLineSegment(sketch, "E2180", {"start": v(-18.9, -22.38) * mm, "end": v(-18.9, -22.4) * mm});
            skLineSegment(sketch, "E2181", {"start": v(-18.9, -22.4) * mm, "end": v(-18.89, -22.4) * mm});
            skLineSegment(sketch, "E2182", {"start": v(-18.89, -22.4) * mm, "end": v(-18.88, -22.42) * mm});
            skLineSegment(sketch, "E2183", {"start": v(-18.88, -22.42) * mm, "end": v(-18.88, -22.43) * mm});
            skLineSegment(sketch, "E2184", {"start": v(-18.88, -22.43) * mm, "end": v(-18.87, -22.45) * mm});
            skLineSegment(sketch, "E2185", {"start": v(-18.87, -22.45) * mm, "end": v(-18.86, -22.46) * mm});
            skLineSegment(sketch, "E2186", {"start": v(-18.86, -22.46) * mm, "end": v(-18.86, -22.48) * mm});
            skLineSegment(sketch, "E2187", {"start": v(-18.86, -22.48) * mm, "end": v(-18.85, -22.5) * mm});
            skLineSegment(sketch, "E2188", {"start": v(-18.85, -22.5) * mm, "end": v(-18.85, -22.5) * mm});
            skLineSegment(sketch, "E2189", {"start": v(-18.85, -22.5) * mm, "end": v(-18.84, -22.53) * mm});
            skLineSegment(sketch, "E2190", {"start": v(-18.84, -22.53) * mm, "end": v(-18.84, -22.54) * mm});
            skLineSegment(sketch, "E2191", {"start": v(-18.84, -22.54) * mm, "end": v(-18.83, -22.56) * mm});
            skLineSegment(sketch, "E2192", {"start": v(-18.83, -22.56) * mm, "end": v(-18.83, -22.58) * mm});
            skLineSegment(sketch, "E2193", {"start": v(-18.83, -22.58) * mm, "end": v(-18.83, -22.6) * mm});
            skLineSegment(sketch, "E2194", {"start": v(-18.83, -22.6) * mm, "end": v(-18.82, -22.62) * mm});
            skLineSegment(sketch, "E2195", {"start": v(-18.82, -22.62) * mm, "end": v(-18.82, -22.64) * mm});
            skLineSegment(sketch, "E2196", {"start": v(-18.82, -22.64) * mm, "end": v(-18.82, -22.66) * mm});
            skLineSegment(sketch, "E2197", {"start": v(-18.82, -22.66) * mm, "end": v(-18.82, -22.68) * mm});
            skLineSegment(sketch, "E2198", {"start": v(-18.82, -22.68) * mm, "end": v(-18.82, -22.7) * mm});
            skLineSegment(sketch, "E2199", {"start": v(-18.82, -22.7) * mm, "end": v(-18.81, -22.72) * mm});
            skLineSegment(sketch, "E2200", {"start": v(-18.81, -22.72) * mm, "end": v(-18.81, -22.74) * mm});
            skLineSegment(sketch, "E2201", {"start": v(-18.81, -22.74) * mm, "end": v(-18.81, -22.76) * mm});
            skLineSegment(sketch, "E2202", {"start": v(-18.81, -22.76) * mm, "end": v(-18.82, -22.79) * mm});
            skLineSegment(sketch, "E2203", {"start": v(-18.82, -22.79) * mm, "end": v(-18.82, -22.81) * mm});
            skLineSegment(sketch, "E2204", {"start": v(-18.82, -22.81) * mm, "end": v(-18.82, -22.83) * mm});
            skLineSegment(sketch, "E2205", {"start": v(-18.82, -22.83) * mm, "end": v(-18.82, -22.86) * mm});
            skLineSegment(sketch, "E2206", {"start": v(-18.82, -22.86) * mm, "end": v(-18.82, -22.88) * mm});
            skLineSegment(sketch, "E2207", {"start": v(-18.82, -22.88) * mm, "end": v(-18.83, -22.9) * mm});
            skLineSegment(sketch, "E2208", {"start": v(-18.83, -22.9) * mm, "end": v(-18.83, -22.93) * mm});
            skLineSegment(sketch, "E2209", {"start": v(-18.83, -22.93) * mm, "end": v(-18.84, -22.96) * mm});
            skLineSegment(sketch, "E2210", {"start": v(-18.84, -22.96) * mm, "end": v(-18.84, -22.99) * mm});
            skLineSegment(sketch, "E2211", {"start": v(-18.84, -22.99) * mm, "end": v(-18.85, -23.01) * mm});
            skLineSegment(sketch, "E2212", {"start": v(-18.85, -23.01) * mm, "end": v(-18.86, -23.04) * mm});
            skLineSegment(sketch, "E2213", {"start": v(-18.86, -23.04) * mm, "end": v(-18.86, -23.05) * mm});
            skLineSegment(sketch, "E2214", {"start": v(-18.86, -23.05) * mm, "end": v(-18.86, -23.06) * mm});
            skLineSegment(sketch, "E2215", {"start": v(-18.86, -23.06) * mm, "end": v(-20.8, -28.6) * mm});
            skLineSegment(sketch, "E2216", {"start": v(-0.1, -25.27) * mm, "end": v(-0.17, -25.26) * mm});
            skLineSegment(sketch, "E2217", {"start": v(-0.17, -25.26) * mm, "end": v(-0.25, -25.26) * mm});
            skLineSegment(sketch, "E2218", {"start": v(-0.25, -25.26) * mm, "end": v(-0.32, -25.25) * mm});
            skLineSegment(sketch, "E2219", {"start": v(-0.32, -25.25) * mm, "end": v(-0.4, -25.25) * mm});
            skLineSegment(sketch, "E2220", {"start": v(-0.4, -25.25) * mm, "end": v(-0.47, -25.23) * mm});
            skLineSegment(sketch, "E2221", {"start": v(-0.47, -25.23) * mm, "end": v(-0.54, -25.22) * mm});
            skLineSegment(sketch, "E2222", {"start": v(-0.54, -25.22) * mm, "end": v(-0.61, -25.2) * mm});
            skLineSegment(sketch, "E2223", {"start": v(-0.61, -25.2) * mm, "end": v(-0.68, -25.18) * mm});
            skLineSegment(sketch, "E2224", {"start": v(-0.68, -25.18) * mm, "end": v(-0.75, -25.16) * mm});
            skLineSegment(sketch, "E2225", {"start": v(-0.75, -25.16) * mm, "end": v(-0.82, -25.14) * mm});
            skLineSegment(sketch, "E2226", {"start": v(-0.82, -25.14) * mm, "end": v(-0.88, -25.11) * mm});
            skLineSegment(sketch, "E2227", {"start": v(-0.88, -25.11) * mm, "end": v(-0.95, -25.08) * mm});
            skLineSegment(sketch, "E2228", {"start": v(-0.95, -25.08) * mm, "end": v(-1.01, -25.05) * mm});
            skLineSegment(sketch, "E2229", {"start": v(-1.01, -25.05) * mm, "end": v(-1.07, -25.02) * mm});
            skLineSegment(sketch, "E2230", {"start": v(-1.07, -25.02) * mm, "end": v(-1.13, -24.98) * mm});
            skLineSegment(sketch, "E2231", {"start": v(-1.13, -24.98) * mm, "end": v(-1.19, -24.94) * mm});
            skLineSegment(sketch, "E2232", {"start": v(-1.19, -24.94) * mm, "end": v(-1.24, -24.9) * mm});
            skLineSegment(sketch, "E2233", {"start": v(-1.24, -24.9) * mm, "end": v(-1.3, -24.86) * mm});
            skLineSegment(sketch, "E2234", {"start": v(-1.3, -24.86) * mm, "end": v(-1.35, -24.82) * mm});
            skLineSegment(sketch, "E2235", {"start": v(-1.35, -24.82) * mm, "end": v(-1.4, -24.77) * mm});
            skLineSegment(sketch, "E2236", {"start": v(-1.4, -24.77) * mm, "end": v(-1.44, -24.72) * mm});
            skLineSegment(sketch, "E2237", {"start": v(-1.44, -24.72) * mm, "end": v(-1.48, -24.67) * mm});
            skLineSegment(sketch, "E2238", {"start": v(-1.48, -24.67) * mm, "end": v(-1.52, -24.63) * mm});
            skLineSegment(sketch, "E2239", {"start": v(-1.52, -24.63) * mm, "end": v(-1.56, -24.58) * mm});
            skLineSegment(sketch, "E2240", {"start": v(-1.56, -24.58) * mm, "end": v(-1.6, -24.53) * mm});
            skLineSegment(sketch, "E2241", {"start": v(-1.6, -24.53) * mm, "end": v(-1.63, -24.47) * mm});
            skLineSegment(sketch, "E2242", {"start": v(-1.63, -24.47) * mm, "end": v(-1.66, -24.42) * mm});
            skLineSegment(sketch, "E2243", {"start": v(-1.66, -24.42) * mm, "end": v(-1.69, -24.36) * mm});
            skLineSegment(sketch, "E2244", {"start": v(-1.69, -24.36) * mm, "end": v(-1.71, -24.3) * mm});
            skLineSegment(sketch, "E2245", {"start": v(-1.71, -24.3) * mm, "end": v(-1.74, -24.25) * mm});
            skLineSegment(sketch, "E2246", {"start": v(-1.74, -24.25) * mm, "end": v(-1.76, -24.2) * mm});
            skLineSegment(sketch, "E2247", {"start": v(-1.76, -24.2) * mm, "end": v(-1.78, -24.13) * mm});
            skLineSegment(sketch, "E2248", {"start": v(-1.78, -24.13) * mm, "end": v(-1.8, -24.07) * mm});
            skLineSegment(sketch, "E2249", {"start": v(-1.8, -24.07) * mm, "end": v(-1.81, -24) * mm});
            skLineSegment(sketch, "E2250", {"start": v(-1.81, -24) * mm, "end": v(-1.82, -23.94) * mm});
            skLineSegment(sketch, "E2251", {"start": v(-1.82, -23.94) * mm, "end": v(-1.84, -23.88) * mm});
            skLineSegment(sketch, "E2252", {"start": v(-1.84, -23.88) * mm, "end": v(-1.84, -23.8) * mm});
            skLineSegment(sketch, "E2253", {"start": v(-1.84, -23.8) * mm, "end": v(-1.85, -23.74) * mm});
            skLineSegment(sketch, "E2254", {"start": v(-1.85, -23.74) * mm, "end": v(-1.85, -23.67) * mm});
            skLineSegment(sketch, "E2255", {"start": v(-1.85, -23.67) * mm, "end": v(-1.85, -23.6) * mm});
            skLineSegment(sketch, "E2256", {"start": v(-1.85, -23.6) * mm, "end": v(-1.85, -23.52) * mm});
            skLineSegment(sketch, "E2257", {"start": v(-1.85, -23.52) * mm, "end": v(-1.85, -23.45) * mm});
            skLineSegment(sketch, "E2258", {"start": v(-1.85, -23.45) * mm, "end": v(-1.84, -23.37) * mm});
            skLineSegment(sketch, "E2259", {"start": v(-1.84, -23.37) * mm, "end": v(-1.83, -23.3) * mm});
            skLineSegment(sketch, "E2260", {"start": v(-1.83, -23.3) * mm, "end": v(-1.82, -23.23) * mm});
            skLineSegment(sketch, "E2261", {"start": v(-1.82, -23.23) * mm, "end": v(-1.8, -23.16) * mm});
            skLineSegment(sketch, "E2262", {"start": v(-1.8, -23.16) * mm, "end": v(-1.78, -23.09) * mm});
            skLineSegment(sketch, "E2263", {"start": v(-1.78, -23.09) * mm, "end": v(-1.76, -23.02) * mm});
            skLineSegment(sketch, "E2264", {"start": v(-1.76, -23.02) * mm, "end": v(-1.74, -22.95) * mm});
            skLineSegment(sketch, "E2265", {"start": v(-1.74, -22.95) * mm, "end": v(-1.71, -22.89) * mm});
            skLineSegment(sketch, "E2266", {"start": v(-1.71, -22.89) * mm, "end": v(-1.68, -22.83) * mm});
            skLineSegment(sketch, "E2267", {"start": v(-1.68, -22.83) * mm, "end": v(-1.65, -22.76) * mm});
            skLineSegment(sketch, "E2268", {"start": v(-1.65, -22.76) * mm, "end": v(-1.61, -22.7) * mm});
            skLineSegment(sketch, "E2269", {"start": v(-1.61, -22.7) * mm, "end": v(-1.58, -22.64) * mm});
            skLineSegment(sketch, "E2270", {"start": v(-1.58, -22.64) * mm, "end": v(-1.54, -22.59) * mm});
            skLineSegment(sketch, "E2271", {"start": v(-1.54, -22.59) * mm, "end": v(-1.5, -22.53) * mm});
            skLineSegment(sketch, "E2272", {"start": v(-1.5, -22.53) * mm, "end": v(-1.45, -22.48) * mm});
            skLineSegment(sketch, "E2273", {"start": v(-1.45, -22.48) * mm, "end": v(-1.4, -22.43) * mm});
            skLineSegment(sketch, "E2274", {"start": v(-1.4, -22.43) * mm, "end": v(-1.36, -22.38) * mm});
            skLineSegment(sketch, "E2275", {"start": v(-1.36, -22.38) * mm, "end": v(-1.3, -22.33) * mm});
            skLineSegment(sketch, "E2276", {"start": v(-1.3, -22.33) * mm, "end": v(-1.26, -22.29) * mm});
            skLineSegment(sketch, "E2277", {"start": v(-1.26, -22.29) * mm, "end": v(-1.21, -22.25) * mm});
            skLineSegment(sketch, "E2278", {"start": v(-1.21, -22.25) * mm, "end": v(-1.16, -22.21) * mm});
            skLineSegment(sketch, "E2279", {"start": v(-1.16, -22.21) * mm, "end": v(-1.1, -22.18) * mm});
            skLineSegment(sketch, "E2280", {"start": v(-1.1, -22.18) * mm, "end": v(-1.06, -22.14) * mm});
            skLineSegment(sketch, "E2281", {"start": v(-1.06, -22.14) * mm, "end": v(-1, -22.11) * mm});
            skLineSegment(sketch, "E2282", {"start": v(-1, -22.11) * mm, "end": v(-0.94, -22.08) * mm});
            skLineSegment(sketch, "E2283", {"start": v(-0.94, -22.08) * mm, "end": v(-0.89, -22.05) * mm});
            skLineSegment(sketch, "E2284", {"start": v(-0.89, -22.05) * mm, "end": v(-0.83, -22.03) * mm});
            skLineSegment(sketch, "E2285", {"start": v(-0.83, -22.03) * mm, "end": v(-0.76, -22) * mm});
            skLineSegment(sketch, "E2286", {"start": v(-0.76, -22) * mm, "end": v(-0.7, -21.98) * mm});
            skLineSegment(sketch, "E2287", {"start": v(-0.7, -21.98) * mm, "end": v(-0.64, -21.96) * mm});
            skLineSegment(sketch, "E2288", {"start": v(-0.64, -21.96) * mm, "end": v(-0.57, -21.95) * mm});
            skLineSegment(sketch, "E2289", {"start": v(-0.57, -21.95) * mm, "end": v(-0.5, -21.93) * mm});
            skLineSegment(sketch, "E2290", {"start": v(-0.5, -21.93) * mm, "end": v(-0.44, -21.92) * mm});
            skLineSegment(sketch, "E2291", {"start": v(-0.44, -21.92) * mm, "end": v(-0.38, -21.91) * mm});
            skLineSegment(sketch, "E2292", {"start": v(-0.38, -21.91) * mm, "end": v(-0.3, -21.9) * mm});
            skLineSegment(sketch, "E2293", {"start": v(-0.3, -21.9) * mm, "end": v(-0.24, -21.9) * mm});
            skLineSegment(sketch, "E2294", {"start": v(-0.24, -21.9) * mm, "end": v(-0.17, -21.9) * mm});
            skLineSegment(sketch, "E2295", {"start": v(-0.17, -21.9) * mm, "end": v(-0.1, -21.9) * mm});
            skLineSegment(sketch, "E2296", {"start": v(-0.1, -21.9) * mm, "end": v(-0.02, -21.9) * mm});
            skLineSegment(sketch, "E2297", {"start": v(-0.02, -21.9) * mm, "end": v(0.05, -21.9) * mm});
            skLineSegment(sketch, "E2298", {"start": v(0.05, -21.9) * mm, "end": v(0.12, -21.9) * mm});
            skLineSegment(sketch, "E2299", {"start": v(0.12, -21.9) * mm, "end": v(0.18, -21.91) * mm});
            skLineSegment(sketch, "E2300", {"start": v(0.18, -21.91) * mm, "end": v(0.25, -21.92) * mm});
            skLineSegment(sketch, "E2301", {"start": v(0.25, -21.92) * mm, "end": v(0.32, -21.93) * mm});
            skLineSegment(sketch, "E2302", {"start": v(0.32, -21.93) * mm, "end": v(0.38, -21.95) * mm});
            skLineSegment(sketch, "E2303", {"start": v(0.38, -21.95) * mm, "end": v(0.45, -21.96) * mm});
            skLineSegment(sketch, "E2304", {"start": v(0.45, -21.96) * mm, "end": v(0.5, -21.98) * mm});
            skLineSegment(sketch, "E2305", {"start": v(0.5, -21.98) * mm, "end": v(0.57, -22) * mm});
            skLineSegment(sketch, "E2306", {"start": v(0.57, -22) * mm, "end": v(0.63, -22.03) * mm});
            skLineSegment(sketch, "E2307", {"start": v(0.63, -22.03) * mm, "end": v(0.7, -22.05) * mm});
            skLineSegment(sketch, "E2308", {"start": v(0.7, -22.05) * mm, "end": v(0.75, -22.08) * mm});
            skLineSegment(sketch, "E2309", {"start": v(0.75, -22.08) * mm, "end": v(0.8, -22.11) * mm});
            skLineSegment(sketch, "E2310", {"start": v(0.8, -22.11) * mm, "end": v(0.86, -22.14) * mm});
            skLineSegment(sketch, "E2311", {"start": v(0.86, -22.14) * mm, "end": v(0.91, -22.18) * mm});
            skLineSegment(sketch, "E2312", {"start": v(0.91, -22.18) * mm, "end": v(0.97, -22.21) * mm});
            skLineSegment(sketch, "E2313", {"start": v(0.97, -22.21) * mm, "end": v(1.02, -22.25) * mm});
            skLineSegment(sketch, "E2314", {"start": v(1.02, -22.25) * mm, "end": v(1.07, -22.3) * mm});
            skLineSegment(sketch, "E2315", {"start": v(1.07, -22.3) * mm, "end": v(1.11, -22.34) * mm});
            skLineSegment(sketch, "E2316", {"start": v(1.11, -22.34) * mm, "end": v(1.16, -22.38) * mm});
            skLineSegment(sketch, "E2317", {"start": v(1.16, -22.38) * mm, "end": v(1.21, -22.43) * mm});
            skLineSegment(sketch, "E2318", {"start": v(1.21, -22.43) * mm, "end": v(1.26, -22.48) * mm});
            skLineSegment(sketch, "E2319", {"start": v(1.26, -22.48) * mm, "end": v(1.3, -22.54) * mm});
            skLineSegment(sketch, "E2320", {"start": v(1.3, -22.54) * mm, "end": v(1.34, -22.6) * mm});
            skLineSegment(sketch, "E2321", {"start": v(1.34, -22.6) * mm, "end": v(1.38, -22.65) * mm});
            skLineSegment(sketch, "E2322", {"start": v(1.38, -22.65) * mm, "end": v(1.42, -22.7) * mm});
            skLineSegment(sketch, "E2323", {"start": v(1.42, -22.7) * mm, "end": v(1.45, -22.77) * mm});
            skLineSegment(sketch, "E2324", {"start": v(1.45, -22.77) * mm, "end": v(1.48, -22.83) * mm});
            skLineSegment(sketch, "E2325", {"start": v(1.48, -22.83) * mm, "end": v(1.51, -22.9) * mm});
            skLineSegment(sketch, "E2326", {"start": v(1.51, -22.9) * mm, "end": v(1.54, -22.96) * mm});
            skLineSegment(sketch, "E2327", {"start": v(1.54, -22.96) * mm, "end": v(1.56, -23.03) * mm});
            skLineSegment(sketch, "E2328", {"start": v(1.56, -23.03) * mm, "end": v(1.58, -23.1) * mm});
            skLineSegment(sketch, "E2329", {"start": v(1.58, -23.1) * mm, "end": v(1.6, -23.16) * mm});
            skLineSegment(sketch, "E2330", {"start": v(1.6, -23.16) * mm, "end": v(1.62, -23.23) * mm});
            skLineSegment(sketch, "E2331", {"start": v(1.62, -23.23) * mm, "end": v(1.63, -23.3) * mm});
            skLineSegment(sketch, "E2332", {"start": v(1.63, -23.3) * mm, "end": v(1.64, -23.38) * mm});
            skLineSegment(sketch, "E2333", {"start": v(1.64, -23.38) * mm, "end": v(1.65, -23.45) * mm});
            skLineSegment(sketch, "E2334", {"start": v(1.65, -23.45) * mm, "end": v(1.65, -23.52) * mm});
            skLineSegment(sketch, "E2335", {"start": v(1.65, -23.52) * mm, "end": v(1.65, -23.6) * mm});
            skLineSegment(sketch, "E2336", {"start": v(1.65, -23.6) * mm, "end": v(1.65, -23.67) * mm});
            skLineSegment(sketch, "E2337", {"start": v(1.65, -23.67) * mm, "end": v(1.65, -23.74) * mm});
            skLineSegment(sketch, "E2338", {"start": v(1.65, -23.74) * mm, "end": v(1.64, -23.8) * mm});
            skLineSegment(sketch, "E2339", {"start": v(1.64, -23.8) * mm, "end": v(1.64, -23.87) * mm});
            skLineSegment(sketch, "E2340", {"start": v(1.64, -23.87) * mm, "end": v(1.62, -23.94) * mm});
            skLineSegment(sketch, "E2341", {"start": v(1.62, -23.94) * mm, "end": v(1.61, -24) * mm});
            skLineSegment(sketch, "E2342", {"start": v(1.61, -24) * mm, "end": v(1.6, -24.07) * mm});
            skLineSegment(sketch, "E2343", {"start": v(1.6, -24.07) * mm, "end": v(1.58, -24.13) * mm});
            skLineSegment(sketch, "E2344", {"start": v(1.58, -24.13) * mm, "end": v(1.56, -24.19) * mm});
            skLineSegment(sketch, "E2345", {"start": v(1.56, -24.19) * mm, "end": v(1.54, -24.25) * mm});
            skLineSegment(sketch, "E2346", {"start": v(1.54, -24.25) * mm, "end": v(1.51, -24.3) * mm});
            skLineSegment(sketch, "E2347", {"start": v(1.51, -24.3) * mm, "end": v(1.49, -24.36) * mm});
            skLineSegment(sketch, "E2348", {"start": v(1.49, -24.36) * mm, "end": v(1.46, -24.42) * mm});
            skLineSegment(sketch, "E2349", {"start": v(1.46, -24.42) * mm, "end": v(1.43, -24.47) * mm});
            skLineSegment(sketch, "E2350", {"start": v(1.43, -24.47) * mm, "end": v(1.4, -24.52) * mm});
            skLineSegment(sketch, "E2351", {"start": v(1.4, -24.52) * mm, "end": v(1.36, -24.57) * mm});
            skLineSegment(sketch, "E2352", {"start": v(1.36, -24.57) * mm, "end": v(1.32, -24.62) * mm});
            skLineSegment(sketch, "E2353", {"start": v(1.32, -24.62) * mm, "end": v(1.29, -24.67) * mm});
            skLineSegment(sketch, "E2354", {"start": v(1.29, -24.67) * mm, "end": v(1.24, -24.72) * mm});
            skLineSegment(sketch, "E2355", {"start": v(1.24, -24.72) * mm, "end": v(1.2, -24.76) * mm});
            skLineSegment(sketch, "E2356", {"start": v(1.2, -24.76) * mm, "end": v(1.15, -24.8) * mm});
            skLineSegment(sketch, "E2357", {"start": v(1.15, -24.8) * mm, "end": v(1.1, -24.85) * mm});
            skLineSegment(sketch, "E2358", {"start": v(1.1, -24.85) * mm, "end": v(1.05, -24.9) * mm});
            skLineSegment(sketch, "E2359", {"start": v(1.05, -24.9) * mm, "end": v(1, -24.94) * mm});
            skLineSegment(sketch, "E2360", {"start": v(1, -24.94) * mm, "end": v(0.94, -24.98) * mm});
            skLineSegment(sketch, "E2361", {"start": v(0.94, -24.98) * mm, "end": v(0.89, -25.01) * mm});
            skLineSegment(sketch, "E2362", {"start": v(0.89, -25.01) * mm, "end": v(0.83, -25.05) * mm});
            skLineSegment(sketch, "E2363", {"start": v(0.83, -25.05) * mm, "end": v(0.77, -25.08) * mm});
            skLineSegment(sketch, "E2364", {"start": v(0.77, -25.08) * mm, "end": v(0.7, -25.1) * mm});
            skLineSegment(sketch, "E2365", {"start": v(0.7, -25.1) * mm, "end": v(0.64, -25.13) * mm});
            skLineSegment(sketch, "E2366", {"start": v(0.64, -25.13) * mm, "end": v(0.57, -25.16) * mm});
            skLineSegment(sketch, "E2367", {"start": v(0.57, -25.16) * mm, "end": v(0.5, -25.18) * mm});
            skLineSegment(sketch, "E2368", {"start": v(0.5, -25.18) * mm, "end": v(0.43, -25.2) * mm});
            skLineSegment(sketch, "E2369", {"start": v(0.43, -25.2) * mm, "end": v(0.36, -25.22) * mm});
            skLineSegment(sketch, "E2370", {"start": v(0.36, -25.22) * mm, "end": v(0.3, -25.23) * mm});
            skLineSegment(sketch, "E2371", {"start": v(0.3, -25.23) * mm, "end": v(0.22, -25.24) * mm});
            skLineSegment(sketch, "E2372", {"start": v(0.22, -25.24) * mm, "end": v(0.14, -25.25) * mm});
            skLineSegment(sketch, "E2373", {"start": v(0.14, -25.25) * mm, "end": v(0.06, -25.26) * mm});
            skLineSegment(sketch, "E2374", {"start": v(0.06, -25.26) * mm, "end": v(-0.02, -25.26) * mm});
            skLineSegment(sketch, "E2375", {"start": v(-0.02, -25.26) * mm, "end": v(-0.1, -25.27) * mm});
            skLineSegment(sketch, "E2376", {"start": v(-0.1, -22.28) * mm, "end": v(-0.15, -22.28) * mm});
            skLineSegment(sketch, "E2377", {"start": v(-0.15, -22.28) * mm, "end": v(-0.2, -22.28) * mm});
            skLineSegment(sketch, "E2378", {"start": v(-0.2, -22.28) * mm, "end": v(-0.26, -22.29) * mm});
            skLineSegment(sketch, "E2379", {"start": v(-0.26, -22.29) * mm, "end": v(-0.31, -22.3) * mm});
            skLineSegment(sketch, "E2380", {"start": v(-0.31, -22.3) * mm, "end": v(-0.36, -22.3) * mm});
            skLineSegment(sketch, "E2381", {"start": v(-0.36, -22.3) * mm, "end": v(-0.41, -22.31) * mm});
            skLineSegment(sketch, "E2382", {"start": v(-0.41, -22.31) * mm, "end": v(-0.46, -22.32) * mm});
            skLineSegment(sketch, "E2383", {"start": v(-0.46, -22.32) * mm, "end": v(-0.51, -22.34) * mm});
            skLineSegment(sketch, "E2384", {"start": v(-0.51, -22.34) * mm, "end": v(-0.56, -22.35) * mm});
            skLineSegment(sketch, "E2385", {"start": v(-0.56, -22.35) * mm, "end": v(-0.61, -22.37) * mm});
            skLineSegment(sketch, "E2386", {"start": v(-0.61, -22.37) * mm, "end": v(-0.66, -22.39) * mm});
            skLineSegment(sketch, "E2387", {"start": v(-0.66, -22.39) * mm, "end": v(-0.7, -22.4) * mm});
            skLineSegment(sketch, "E2388", {"start": v(-0.7, -22.4) * mm, "end": v(-0.75, -22.43) * mm});
            skLineSegment(sketch, "E2389", {"start": v(-0.75, -22.43) * mm, "end": v(-0.8, -22.45) * mm});
            skLineSegment(sketch, "E2390", {"start": v(-0.8, -22.45) * mm, "end": v(-0.83, -22.48) * mm});
            skLineSegment(sketch, "E2391", {"start": v(-0.83, -22.48) * mm, "end": v(-0.87, -22.5) * mm});
            skLineSegment(sketch, "E2392", {"start": v(-0.87, -22.5) * mm, "end": v(-0.91, -22.53) * mm});
            skLineSegment(sketch, "E2393", {"start": v(-0.91, -22.53) * mm, "end": v(-0.95, -22.56) * mm});
            skLineSegment(sketch, "E2394", {"start": v(-0.95, -22.56) * mm, "end": v(-1, -22.59) * mm});
            skLineSegment(sketch, "E2395", {"start": v(-1, -22.59) * mm, "end": v(-1.03, -22.62) * mm});
            skLineSegment(sketch, "E2396", {"start": v(-1.03, -22.62) * mm, "end": v(-1.07, -22.66) * mm});
            skLineSegment(sketch, "E2397", {"start": v(-1.07, -22.66) * mm, "end": v(-1.1, -22.7) * mm});
            skLineSegment(sketch, "E2398", {"start": v(-1.1, -22.7) * mm, "end": v(-1.14, -22.73) * mm});
            skLineSegment(sketch, "E2399", {"start": v(-1.14, -22.73) * mm, "end": v(-1.18, -22.77) * mm});
            skLineSegment(sketch, "E2400", {"start": v(-1.18, -22.77) * mm, "end": v(-1.2, -22.82) * mm});
            skLineSegment(sketch, "E2401", {"start": v(-1.2, -22.82) * mm, "end": v(-1.24, -22.86) * mm});
            skLineSegment(sketch, "E2402", {"start": v(-1.24, -22.86) * mm, "end": v(-1.27, -22.9) * mm});
            skLineSegment(sketch, "E2403", {"start": v(-1.27, -22.9) * mm, "end": v(-1.3, -22.95) * mm});
            skLineSegment(sketch, "E2404", {"start": v(-1.3, -22.95) * mm, "end": v(-1.32, -23) * mm});
            skLineSegment(sketch, "E2405", {"start": v(-1.32, -23) * mm, "end": v(-1.34, -23.05) * mm});
            skLineSegment(sketch, "E2406", {"start": v(-1.34, -23.05) * mm, "end": v(-1.36, -23.1) * mm});
            skLineSegment(sketch, "E2407", {"start": v(-1.36, -23.1) * mm, "end": v(-1.38, -23.15) * mm});
            skLineSegment(sketch, "E2408", {"start": v(-1.38, -23.15) * mm, "end": v(-1.4, -23.2) * mm});
            skLineSegment(sketch, "E2409", {"start": v(-1.4, -23.2) * mm, "end": v(-1.41, -23.26) * mm});
            skLineSegment(sketch, "E2410", {"start": v(-1.41, -23.26) * mm, "end": v(-1.42, -23.31) * mm});
            skLineSegment(sketch, "E2411", {"start": v(-1.42, -23.31) * mm, "end": v(-1.43, -23.37) * mm});
            skLineSegment(sketch, "E2412", {"start": v(-1.43, -23.37) * mm, "end": v(-1.44, -23.43) * mm});
            skLineSegment(sketch, "E2413", {"start": v(-1.44, -23.43) * mm, "end": v(-1.45, -23.48) * mm});
            skLineSegment(sketch, "E2414", {"start": v(-1.45, -23.48) * mm, "end": v(-1.45, -23.54) * mm});
            skLineSegment(sketch, "E2415", {"start": v(-1.45, -23.54) * mm, "end": v(-1.45, -23.6) * mm});
            skLineSegment(sketch, "E2416", {"start": v(-1.45, -23.6) * mm, "end": v(-1.45, -23.66) * mm});
            skLineSegment(sketch, "E2417", {"start": v(-1.45, -23.66) * mm, "end": v(-1.45, -23.71) * mm});
            skLineSegment(sketch, "E2418", {"start": v(-1.45, -23.71) * mm, "end": v(-1.44, -23.77) * mm});
            skLineSegment(sketch, "E2419", {"start": v(-1.44, -23.77) * mm, "end": v(-1.44, -23.82) * mm});
            skLineSegment(sketch, "E2420", {"start": v(-1.44, -23.82) * mm, "end": v(-1.43, -23.87) * mm});
            skLineSegment(sketch, "E2421", {"start": v(-1.43, -23.87) * mm, "end": v(-1.42, -23.92) * mm});
            skLineSegment(sketch, "E2422", {"start": v(-1.42, -23.92) * mm, "end": v(-1.4, -23.97) * mm});
            skLineSegment(sketch, "E2423", {"start": v(-1.4, -23.97) * mm, "end": v(-1.39, -24.02) * mm});
            skLineSegment(sketch, "E2424", {"start": v(-1.39, -24.02) * mm, "end": v(-1.37, -24.07) * mm});
            skLineSegment(sketch, "E2425", {"start": v(-1.37, -24.07) * mm, "end": v(-1.35, -24.12) * mm});
            skLineSegment(sketch, "E2426", {"start": v(-1.35, -24.12) * mm, "end": v(-1.33, -24.17) * mm});
            skLineSegment(sketch, "E2427", {"start": v(-1.33, -24.17) * mm, "end": v(-1.31, -24.21) * mm});
            skLineSegment(sketch, "E2428", {"start": v(-1.31, -24.21) * mm, "end": v(-1.29, -24.26) * mm});
            skLineSegment(sketch, "E2429", {"start": v(-1.29, -24.26) * mm, "end": v(-1.26, -24.3) * mm});
            skLineSegment(sketch, "E2430", {"start": v(-1.26, -24.3) * mm, "end": v(-1.23, -24.35) * mm});
            skLineSegment(sketch, "E2431", {"start": v(-1.23, -24.35) * mm, "end": v(-1.2, -24.39) * mm});
            skLineSegment(sketch, "E2432", {"start": v(-1.2, -24.39) * mm, "end": v(-1.17, -24.43) * mm});
            skLineSegment(sketch, "E2433", {"start": v(-1.17, -24.43) * mm, "end": v(-1.14, -24.46) * mm});
            skLineSegment(sketch, "E2434", {"start": v(-1.14, -24.46) * mm, "end": v(-1.1, -24.5) * mm});
            skLineSegment(sketch, "E2435", {"start": v(-1.1, -24.5) * mm, "end": v(-1.07, -24.54) * mm});
            skLineSegment(sketch, "E2436", {"start": v(-1.07, -24.54) * mm, "end": v(-1.03, -24.57) * mm});
            skLineSegment(sketch, "E2437", {"start": v(-1.03, -24.57) * mm, "end": v(-1, -24.6) * mm});
            skLineSegment(sketch, "E2438", {"start": v(-1, -24.6) * mm, "end": v(-0.95, -24.63) * mm});
            skLineSegment(sketch, "E2439", {"start": v(-0.95, -24.63) * mm, "end": v(-0.91, -24.66) * mm});
            skLineSegment(sketch, "E2440", {"start": v(-0.91, -24.66) * mm, "end": v(-0.87, -24.7) * mm});
            skLineSegment(sketch, "E2441", {"start": v(-0.87, -24.7) * mm, "end": v(-0.82, -24.72) * mm});
            skLineSegment(sketch, "E2442", {"start": v(-0.82, -24.72) * mm, "end": v(-0.78, -24.74) * mm});
            skLineSegment(sketch, "E2443", {"start": v(-0.78, -24.74) * mm, "end": v(-0.73, -24.77) * mm});
            skLineSegment(sketch, "E2444", {"start": v(-0.73, -24.77) * mm, "end": v(-0.68, -24.79) * mm});
            skLineSegment(sketch, "E2445", {"start": v(-0.68, -24.79) * mm, "end": v(-0.63, -24.8) * mm});
            skLineSegment(sketch, "E2446", {"start": v(-0.63, -24.8) * mm, "end": v(-0.58, -24.82) * mm});
            skLineSegment(sketch, "E2447", {"start": v(-0.58, -24.82) * mm, "end": v(-0.53, -24.84) * mm});
            skLineSegment(sketch, "E2448", {"start": v(-0.53, -24.84) * mm, "end": v(-0.48, -24.86) * mm});
            skLineSegment(sketch, "E2449", {"start": v(-0.48, -24.86) * mm, "end": v(-0.43, -24.87) * mm});
            skLineSegment(sketch, "E2450", {"start": v(-0.43, -24.87) * mm, "end": v(-0.37, -24.88) * mm});
            skLineSegment(sketch, "E2451", {"start": v(-0.37, -24.88) * mm, "end": v(-0.32, -24.89) * mm});
            skLineSegment(sketch, "E2452", {"start": v(-0.32, -24.89) * mm, "end": v(-0.26, -24.9) * mm});
            skLineSegment(sketch, "E2453", {"start": v(-0.26, -24.9) * mm, "end": v(-0.2, -24.9) * mm});
            skLineSegment(sketch, "E2454", {"start": v(-0.2, -24.9) * mm, "end": v(-0.15, -24.9) * mm});
            skLineSegment(sketch, "E2455", {"start": v(-0.15, -24.9) * mm, "end": v(-0.1, -24.9) * mm});
            skLineSegment(sketch, "E2456", {"start": v(-0.1, -24.9) * mm, "end": v(-0.04, -24.9) * mm});
            skLineSegment(sketch, "E2457", {"start": v(-0.04, -24.9) * mm, "end": v(0.01, -24.9) * mm});
            skLineSegment(sketch, "E2458", {"start": v(0.01, -24.9) * mm, "end": v(0.07, -24.9) * mm});
            skLineSegment(sketch, "E2459", {"start": v(0.07, -24.9) * mm, "end": v(0.12, -24.89) * mm});
            skLineSegment(sketch, "E2460", {"start": v(0.12, -24.89) * mm, "end": v(0.17, -24.88) * mm});
            skLineSegment(sketch, "E2461", {"start": v(0.17, -24.88) * mm, "end": v(0.23, -24.87) * mm});
            skLineSegment(sketch, "E2462", {"start": v(0.23, -24.87) * mm, "end": v(0.28, -24.86) * mm});
            skLineSegment(sketch, "E2463", {"start": v(0.28, -24.86) * mm, "end": v(0.33, -24.84) * mm});
            skLineSegment(sketch, "E2464", {"start": v(0.33, -24.84) * mm, "end": v(0.38, -24.82) * mm});
            skLineSegment(sketch, "E2465", {"start": v(0.38, -24.82) * mm, "end": v(0.43, -24.8) * mm});
            skLineSegment(sketch, "E2466", {"start": v(0.43, -24.8) * mm, "end": v(0.48, -24.79) * mm});
            skLineSegment(sketch, "E2467", {"start": v(0.48, -24.79) * mm, "end": v(0.53, -24.77) * mm});
            skLineSegment(sketch, "E2468", {"start": v(0.53, -24.77) * mm, "end": v(0.58, -24.74) * mm});
            skLineSegment(sketch, "E2469", {"start": v(0.58, -24.74) * mm, "end": v(0.62, -24.72) * mm});
            skLineSegment(sketch, "E2470", {"start": v(0.62, -24.72) * mm, "end": v(0.67, -24.7) * mm});
            skLineSegment(sketch, "E2471", {"start": v(0.67, -24.7) * mm, "end": v(0.71, -24.66) * mm});
            skLineSegment(sketch, "E2472", {"start": v(0.71, -24.66) * mm, "end": v(0.75, -24.63) * mm});
            skLineSegment(sketch, "E2473", {"start": v(0.75, -24.63) * mm, "end": v(0.8, -24.6) * mm});
            skLineSegment(sketch, "E2474", {"start": v(0.8, -24.6) * mm, "end": v(0.83, -24.57) * mm});
            skLineSegment(sketch, "E2475", {"start": v(0.83, -24.57) * mm, "end": v(0.87, -24.54) * mm});
            skLineSegment(sketch, "E2476", {"start": v(0.87, -24.54) * mm, "end": v(0.9, -24.5) * mm});
            skLineSegment(sketch, "E2477", {"start": v(0.9, -24.5) * mm, "end": v(0.94, -24.46) * mm});
            skLineSegment(sketch, "E2478", {"start": v(0.94, -24.46) * mm, "end": v(0.97, -24.43) * mm});
            skLineSegment(sketch, "E2479", {"start": v(0.97, -24.43) * mm, "end": v(1, -24.39) * mm});
            skLineSegment(sketch, "E2480", {"start": v(1, -24.39) * mm, "end": v(1.03, -24.35) * mm});
            skLineSegment(sketch, "E2481", {"start": v(1.03, -24.35) * mm, "end": v(1.06, -24.3) * mm});
            skLineSegment(sketch, "E2482", {"start": v(1.06, -24.3) * mm, "end": v(1.09, -24.26) * mm});
            skLineSegment(sketch, "E2483", {"start": v(1.09, -24.26) * mm, "end": v(1.1, -24.21) * mm});
            skLineSegment(sketch, "E2484", {"start": v(1.1, -24.21) * mm, "end": v(1.13, -24.17) * mm});
            skLineSegment(sketch, "E2485", {"start": v(1.13, -24.17) * mm, "end": v(1.15, -24.12) * mm});
            skLineSegment(sketch, "E2486", {"start": v(1.15, -24.12) * mm, "end": v(1.17, -24.07) * mm});
            skLineSegment(sketch, "E2487", {"start": v(1.17, -24.07) * mm, "end": v(1.19, -24.02) * mm});
            skLineSegment(sketch, "E2488", {"start": v(1.19, -24.02) * mm, "end": v(1.2, -23.97) * mm});
            skLineSegment(sketch, "E2489", {"start": v(1.2, -23.97) * mm, "end": v(1.22, -23.92) * mm});
            skLineSegment(sketch, "E2490", {"start": v(1.22, -23.92) * mm, "end": v(1.23, -23.87) * mm});
            skLineSegment(sketch, "E2491", {"start": v(1.23, -23.87) * mm, "end": v(1.24, -23.82) * mm});
            skLineSegment(sketch, "E2492", {"start": v(1.24, -23.82) * mm, "end": v(1.24, -23.77) * mm});
            skLineSegment(sketch, "E2493", {"start": v(1.24, -23.77) * mm, "end": v(1.25, -23.71) * mm});
            skLineSegment(sketch, "E2494", {"start": v(1.25, -23.71) * mm, "end": v(1.25, -23.66) * mm});
            skLineSegment(sketch, "E2495", {"start": v(1.25, -23.66) * mm, "end": v(1.25, -23.6) * mm});
            skLineSegment(sketch, "E2496", {"start": v(1.25, -23.6) * mm, "end": v(1.25, -23.54) * mm});
            skLineSegment(sketch, "E2497", {"start": v(1.25, -23.54) * mm, "end": v(1.25, -23.48) * mm});
            skLineSegment(sketch, "E2498", {"start": v(1.25, -23.48) * mm, "end": v(1.24, -23.43) * mm});
            skLineSegment(sketch, "E2499", {"start": v(1.24, -23.43) * mm, "end": v(1.23, -23.37) * mm});
            skLineSegment(sketch, "E2500", {"start": v(1.23, -23.37) * mm, "end": v(1.22, -23.32) * mm});
            skLineSegment(sketch, "E2501", {"start": v(1.22, -23.32) * mm, "end": v(1.21, -23.26) * mm});
            skLineSegment(sketch, "E2502", {"start": v(1.21, -23.26) * mm, "end": v(1.2, -23.2) * mm});
            skLineSegment(sketch, "E2503", {"start": v(1.2, -23.2) * mm, "end": v(1.18, -23.16) * mm});
            skLineSegment(sketch, "E2504", {"start": v(1.18, -23.16) * mm, "end": v(1.16, -23.1) * mm});
            skLineSegment(sketch, "E2505", {"start": v(1.16, -23.1) * mm, "end": v(1.14, -23.05) * mm});
            skLineSegment(sketch, "E2506", {"start": v(1.14, -23.05) * mm, "end": v(1.12, -23) * mm});
            skLineSegment(sketch, "E2507", {"start": v(1.12, -23) * mm, "end": v(1.1, -22.96) * mm});
            skLineSegment(sketch, "E2508", {"start": v(1.1, -22.96) * mm, "end": v(1.07, -22.9) * mm});
            skLineSegment(sketch, "E2509", {"start": v(1.07, -22.9) * mm, "end": v(1.04, -22.86) * mm});
            skLineSegment(sketch, "E2510", {"start": v(1.04, -22.86) * mm, "end": v(1.01, -22.82) * mm});
            skLineSegment(sketch, "E2511", {"start": v(1.01, -22.82) * mm, "end": v(0.98, -22.78) * mm});
            skLineSegment(sketch, "E2512", {"start": v(0.98, -22.78) * mm, "end": v(0.95, -22.74) * mm});
            skLineSegment(sketch, "E2513", {"start": v(0.95, -22.74) * mm, "end": v(0.91, -22.7) * mm});
            skLineSegment(sketch, "E2514", {"start": v(0.91, -22.7) * mm, "end": v(0.88, -22.66) * mm});
            skLineSegment(sketch, "E2515", {"start": v(0.88, -22.66) * mm, "end": v(0.84, -22.63) * mm});
            skLineSegment(sketch, "E2516", {"start": v(0.84, -22.63) * mm, "end": v(0.8, -22.6) * mm});
            skLineSegment(sketch, "E2517", {"start": v(0.8, -22.6) * mm, "end": v(0.76, -22.56) * mm});
            skLineSegment(sketch, "E2518", {"start": v(0.76, -22.56) * mm, "end": v(0.72, -22.54) * mm});
            skLineSegment(sketch, "E2519", {"start": v(0.72, -22.54) * mm, "end": v(0.68, -22.5) * mm});
            skLineSegment(sketch, "E2520", {"start": v(0.68, -22.5) * mm, "end": v(0.64, -22.48) * mm});
            skLineSegment(sketch, "E2521", {"start": v(0.64, -22.48) * mm, "end": v(0.6, -22.46) * mm});
            skLineSegment(sketch, "E2522", {"start": v(0.6, -22.46) * mm, "end": v(0.56, -22.43) * mm});
            skLineSegment(sketch, "E2523", {"start": v(0.56, -22.43) * mm, "end": v(0.51, -22.41) * mm});
            skLineSegment(sketch, "E2524", {"start": v(0.51, -22.41) * mm, "end": v(0.47, -22.4) * mm});
            skLineSegment(sketch, "E2525", {"start": v(0.47, -22.4) * mm, "end": v(0.42, -22.37) * mm});
            skLineSegment(sketch, "E2526", {"start": v(0.42, -22.37) * mm, "end": v(0.37, -22.35) * mm});
            skLineSegment(sketch, "E2527", {"start": v(0.37, -22.35) * mm, "end": v(0.32, -22.34) * mm});
            skLineSegment(sketch, "E2528", {"start": v(0.32, -22.34) * mm, "end": v(0.27, -22.33) * mm});
            skLineSegment(sketch, "E2529", {"start": v(0.27, -22.33) * mm, "end": v(0.22, -22.31) * mm});
            skLineSegment(sketch, "E2530", {"start": v(0.22, -22.31) * mm, "end": v(0.17, -22.3) * mm});
            skLineSegment(sketch, "E2531", {"start": v(0.17, -22.3) * mm, "end": v(0.12, -22.3) * mm});
            skLineSegment(sketch, "E2532", {"start": v(0.12, -22.3) * mm, "end": v(0.07, -22.29) * mm});
            skLineSegment(sketch, "E2533", {"start": v(0.07, -22.29) * mm, "end": v(0.01, -22.28) * mm});
            skLineSegment(sketch, "E2534", {"start": v(0.01, -22.28) * mm, "end": v(-0.04, -22.28) * mm});
            skLineSegment(sketch, "E2535", {"start": v(-0.04, -22.28) * mm, "end": v(-0.1, -22.28) * mm});
            skLineSegment(sketch, "E2536", {"start": v(-0.1, -28.69) * mm, "end": v(-0.18, -28.68) * mm});
            skLineSegment(sketch, "E2537", {"start": v(-0.18, -28.68) * mm, "end": v(-0.25, -28.68) * mm});
            skLineSegment(sketch, "E2538", {"start": v(-0.25, -28.68) * mm, "end": v(-0.33, -28.67) * mm});
            skLineSegment(sketch, "E2539", {"start": v(-0.33, -28.67) * mm, "end": v(-0.4, -28.66) * mm});
            skLineSegment(sketch, "E2540", {"start": v(-0.4, -28.66) * mm, "end": v(-0.49, -28.65) * mm});
            skLineSegment(sketch, "E2541", {"start": v(-0.49, -28.65) * mm, "end": v(-0.56, -28.63) * mm});
            skLineSegment(sketch, "E2542", {"start": v(-0.56, -28.63) * mm, "end": v(-0.63, -28.61) * mm});
            skLineSegment(sketch, "E2543", {"start": v(-0.63, -28.61) * mm, "end": v(-0.7, -28.6) * mm});
            skLineSegment(sketch, "E2544", {"start": v(-0.7, -28.6) * mm, "end": v(-0.78, -28.57) * mm});
            skLineSegment(sketch, "E2545", {"start": v(-0.78, -28.57) * mm, "end": v(-0.85, -28.54) * mm});
            skLineSegment(sketch, "E2546", {"start": v(-0.85, -28.54) * mm, "end": v(-0.92, -28.5) * mm});
            skLineSegment(sketch, "E2547", {"start": v(-0.92, -28.5) * mm, "end": v(-0.99, -28.47) * mm});
            skLineSegment(sketch, "E2548", {"start": v(-0.99, -28.47) * mm, "end": v(-1.05, -28.44) * mm});
            skLineSegment(sketch, "E2549", {"start": v(-1.05, -28.44) * mm, "end": v(-1.12, -28.4) * mm});
            skLineSegment(sketch, "E2550", {"start": v(-1.12, -28.4) * mm, "end": v(-1.18, -28.36) * mm});
            skLineSegment(sketch, "E2551", {"start": v(-1.18, -28.36) * mm, "end": v(-1.24, -28.32) * mm});
            skLineSegment(sketch, "E2552", {"start": v(-1.24, -28.32) * mm, "end": v(-1.3, -28.28) * mm});
            skLineSegment(sketch, "E2553", {"start": v(-1.3, -28.28) * mm, "end": v(-1.36, -28.23) * mm});
            skLineSegment(sketch, "E2554", {"start": v(-1.36, -28.23) * mm, "end": v(-1.41, -28.19) * mm});
            skLineSegment(sketch, "E2555", {"start": v(-1.41, -28.19) * mm, "end": v(-1.47, -28.14) * mm});
            skLineSegment(sketch, "E2556", {"start": v(-1.47, -28.14) * mm, "end": v(-1.52, -28.09) * mm});
            skLineSegment(sketch, "E2557", {"start": v(-1.52, -28.09) * mm, "end": v(-1.57, -28.03) * mm});
            skLineSegment(sketch, "E2558", {"start": v(-1.57, -28.03) * mm, "end": v(-1.61, -27.98) * mm});
            skLineSegment(sketch, "E2559", {"start": v(-1.61, -27.98) * mm, "end": v(-1.66, -27.92) * mm});
            skLineSegment(sketch, "E2560", {"start": v(-1.66, -27.92) * mm, "end": v(-1.7, -27.86) * mm});
            skLineSegment(sketch, "E2561", {"start": v(-1.7, -27.86) * mm, "end": v(-1.74, -27.8) * mm});
            skLineSegment(sketch, "E2562", {"start": v(-1.74, -27.8) * mm, "end": v(-1.78, -27.74) * mm});
            skLineSegment(sketch, "E2563", {"start": v(-1.78, -27.74) * mm, "end": v(-1.82, -27.67) * mm});
            skLineSegment(sketch, "E2564", {"start": v(-1.82, -27.67) * mm, "end": v(-1.85, -27.6) * mm});
            skLineSegment(sketch, "E2565", {"start": v(-1.85, -27.6) * mm, "end": v(-1.88, -27.54) * mm});
            skLineSegment(sketch, "E2566", {"start": v(-1.88, -27.54) * mm, "end": v(-1.91, -27.47) * mm});
            skLineSegment(sketch, "E2567", {"start": v(-1.91, -27.47) * mm, "end": v(-1.94, -27.4) * mm});
            skLineSegment(sketch, "E2568", {"start": v(-1.94, -27.4) * mm, "end": v(-1.96, -27.33) * mm});
            skLineSegment(sketch, "E2569", {"start": v(-1.96, -27.33) * mm, "end": v(-1.98, -27.26) * mm});
            skLineSegment(sketch, "E2570", {"start": v(-1.98, -27.26) * mm, "end": v(-2, -27.18) * mm});
            skLineSegment(sketch, "E2571", {"start": v(-2, -27.18) * mm, "end": v(-2, -27.11) * mm});
            skLineSegment(sketch, "E2572", {"start": v(-2, -27.11) * mm, "end": v(-2.02, -27.04) * mm});
            skLineSegment(sketch, "E2573", {"start": v(-2.02, -27.04) * mm, "end": v(-2.03, -26.96) * mm});
            skLineSegment(sketch, "E2574", {"start": v(-2.03, -26.96) * mm, "end": v(-2.03, -26.88) * mm});
            skLineSegment(sketch, "E2575", {"start": v(-2.03, -26.88) * mm, "end": v(-2.03, -26.8) * mm});
            skLineSegment(sketch, "E2576", {"start": v(-2.03, -26.8) * mm, "end": v(-2.03, -26.73) * mm});
            skLineSegment(sketch, "E2577", {"start": v(-2.03, -26.73) * mm, "end": v(-2.03, -26.65) * mm});
            skLineSegment(sketch, "E2578", {"start": v(-2.03, -26.65) * mm, "end": v(-2.02, -26.57) * mm});
            skLineSegment(sketch, "E2579", {"start": v(-2.02, -26.57) * mm, "end": v(-2.01, -26.49) * mm});
            skLineSegment(sketch, "E2580", {"start": v(-2.01, -26.49) * mm, "end": v(-2, -26.41) * mm});
            skLineSegment(sketch, "E2581", {"start": v(-2, -26.41) * mm, "end": v(-1.99, -26.34) * mm});
            skLineSegment(sketch, "E2582", {"start": v(-1.99, -26.34) * mm, "end": v(-1.97, -26.26) * mm});
            skLineSegment(sketch, "E2583", {"start": v(-1.97, -26.26) * mm, "end": v(-1.95, -26.19) * mm});
            skLineSegment(sketch, "E2584", {"start": v(-1.95, -26.19) * mm, "end": v(-1.92, -26.12) * mm});
            skLineSegment(sketch, "E2585", {"start": v(-1.92, -26.12) * mm, "end": v(-1.9, -26.05) * mm});
            skLineSegment(sketch, "E2586", {"start": v(-1.9, -26.05) * mm, "end": v(-1.87, -25.98) * mm});
            skLineSegment(sketch, "E2587", {"start": v(-1.87, -25.98) * mm, "end": v(-1.84, -25.9) * mm});
            skLineSegment(sketch, "E2588", {"start": v(-1.84, -25.9) * mm, "end": v(-1.8, -25.84) * mm});
            skLineSegment(sketch, "E2589", {"start": v(-1.8, -25.84) * mm, "end": v(-1.77, -25.78) * mm});
            skLineSegment(sketch, "E2590", {"start": v(-1.77, -25.78) * mm, "end": v(-1.73, -25.72) * mm});
            skLineSegment(sketch, "E2591", {"start": v(-1.73, -25.72) * mm, "end": v(-1.69, -25.66) * mm});
            skLineSegment(sketch, "E2592", {"start": v(-1.69, -25.66) * mm, "end": v(-1.64, -25.6) * mm});
            skLineSegment(sketch, "E2593", {"start": v(-1.64, -25.6) * mm, "end": v(-1.6, -25.54) * mm});
            skLineSegment(sketch, "E2594", {"start": v(-1.6, -25.54) * mm, "end": v(-1.55, -25.49) * mm});
            skLineSegment(sketch, "E2595", {"start": v(-1.55, -25.49) * mm, "end": v(-1.5, -25.44) * mm});
            skLineSegment(sketch, "E2596", {"start": v(-1.5, -25.44) * mm, "end": v(-1.44, -25.39) * mm});
            skLineSegment(sketch, "E2597", {"start": v(-1.44, -25.39) * mm, "end": v(-1.38, -25.34) * mm});
            skLineSegment(sketch, "E2598", {"start": v(-1.38, -25.34) * mm, "end": v(-1.33, -25.3) * mm});
            skLineSegment(sketch, "E2599", {"start": v(-1.33, -25.3) * mm, "end": v(-1.27, -25.26) * mm});
            skLineSegment(sketch, "E2600", {"start": v(-1.27, -25.26) * mm, "end": v(-1.2, -25.22) * mm});
            skLineSegment(sketch, "E2601", {"start": v(-1.2, -25.22) * mm, "end": v(-1.14, -25.18) * mm});
            skLineSegment(sketch, "E2602", {"start": v(-1.14, -25.18) * mm, "end": v(-1.07, -25.14) * mm});
            skLineSegment(sketch, "E2603", {"start": v(-1.07, -25.14) * mm, "end": v(-1, -25.11) * mm});
            skLineSegment(sketch, "E2604", {"start": v(-1, -25.11) * mm, "end": v(-0.94, -25.08) * mm});
            skLineSegment(sketch, "E2605", {"start": v(-0.94, -25.08) * mm, "end": v(-0.86, -25.05) * mm});
            skLineSegment(sketch, "E2606", {"start": v(-0.86, -25.05) * mm, "end": v(-0.8, -25.03) * mm});
            skLineSegment(sketch, "E2607", {"start": v(-0.8, -25.03) * mm, "end": v(-0.72, -25) * mm});
            skLineSegment(sketch, "E2608", {"start": v(-0.72, -25) * mm, "end": v(-0.64, -24.99) * mm});
            skLineSegment(sketch, "E2609", {"start": v(-0.64, -24.99) * mm, "end": v(-0.57, -24.97) * mm});
            skLineSegment(sketch, "E2610", {"start": v(-0.57, -24.97) * mm, "end": v(-0.49, -24.95) * mm});
            skLineSegment(sketch, "E2611", {"start": v(-0.49, -24.95) * mm, "end": v(-0.41, -24.94) * mm});
            skLineSegment(sketch, "E2612", {"start": v(-0.41, -24.94) * mm, "end": v(-0.33, -24.93) * mm});
            skLineSegment(sketch, "E2613", {"start": v(-0.33, -24.93) * mm, "end": v(-0.25, -24.93) * mm});
            skLineSegment(sketch, "E2614", {"start": v(-0.25, -24.93) * mm, "end": v(-0.18, -24.92) * mm});
            skLineSegment(sketch, "E2615", {"start": v(-0.18, -24.92) * mm, "end": v(-0.1, -24.92) * mm});
            skLineSegment(sketch, "E2616", {"start": v(-0.1, -24.92) * mm, "end": v(-0.02, -24.92) * mm});
            skLineSegment(sketch, "E2617", {"start": v(-0.02, -24.92) * mm, "end": v(0.06, -24.93) * mm});
            skLineSegment(sketch, "E2618", {"start": v(0.06, -24.93) * mm, "end": v(0.14, -24.93) * mm});
            skLineSegment(sketch, "E2619", {"start": v(0.14, -24.93) * mm, "end": v(0.22, -24.94) * mm});
            skLineSegment(sketch, "E2620", {"start": v(0.22, -24.94) * mm, "end": v(0.3, -24.95) * mm});
            skLineSegment(sketch, "E2621", {"start": v(0.3, -24.95) * mm, "end": v(0.37, -24.97) * mm});
            skLineSegment(sketch, "E2622", {"start": v(0.37, -24.97) * mm, "end": v(0.45, -24.99) * mm});
            skLineSegment(sketch, "E2623", {"start": v(0.45, -24.99) * mm, "end": v(0.52, -25) * mm});
            skLineSegment(sketch, "E2624", {"start": v(0.52, -25) * mm, "end": v(0.6, -25.03) * mm});
            skLineSegment(sketch, "E2625", {"start": v(0.6, -25.03) * mm, "end": v(0.67, -25.05) * mm});
            skLineSegment(sketch, "E2626", {"start": v(0.67, -25.05) * mm, "end": v(0.74, -25.08) * mm});
            skLineSegment(sketch, "E2627", {"start": v(0.74, -25.08) * mm, "end": v(0.81, -25.11) * mm});
            skLineSegment(sketch, "E2628", {"start": v(0.81, -25.11) * mm, "end": v(0.88, -25.14) * mm});
            skLineSegment(sketch, "E2629", {"start": v(0.88, -25.14) * mm, "end": v(0.95, -25.18) * mm});
            skLineSegment(sketch, "E2630", {"start": v(0.95, -25.18) * mm, "end": v(1, -25.22) * mm});
            skLineSegment(sketch, "E2631", {"start": v(1, -25.22) * mm, "end": v(1.07, -25.26) * mm});
            skLineSegment(sketch, "E2632", {"start": v(1.07, -25.26) * mm, "end": v(1.13, -25.3) * mm});
            skLineSegment(sketch, "E2633", {"start": v(1.13, -25.3) * mm, "end": v(1.19, -25.34) * mm});
            skLineSegment(sketch, "E2634", {"start": v(1.19, -25.34) * mm, "end": v(1.24, -25.4) * mm});
            skLineSegment(sketch, "E2635", {"start": v(1.24, -25.4) * mm, "end": v(1.3, -25.44) * mm});
            skLineSegment(sketch, "E2636", {"start": v(1.3, -25.44) * mm, "end": v(1.35, -25.5) * mm});
            skLineSegment(sketch, "E2637", {"start": v(1.35, -25.5) * mm, "end": v(1.4, -25.55) * mm});
            skLineSegment(sketch, "E2638", {"start": v(1.4, -25.55) * mm, "end": v(1.44, -25.6) * mm});
            skLineSegment(sketch, "E2639", {"start": v(1.44, -25.6) * mm, "end": v(1.49, -25.66) * mm});
            skLineSegment(sketch, "E2640", {"start": v(1.49, -25.66) * mm, "end": v(1.53, -25.72) * mm});
            skLineSegment(sketch, "E2641", {"start": v(1.53, -25.72) * mm, "end": v(1.57, -25.78) * mm});
            skLineSegment(sketch, "E2642", {"start": v(1.57, -25.78) * mm, "end": v(1.6, -25.85) * mm});
            skLineSegment(sketch, "E2643", {"start": v(1.6, -25.85) * mm, "end": v(1.64, -25.91) * mm});
            skLineSegment(sketch, "E2644", {"start": v(1.64, -25.91) * mm, "end": v(1.67, -25.98) * mm});
            skLineSegment(sketch, "E2645", {"start": v(1.67, -25.98) * mm, "end": v(1.7, -26.05) * mm});
            skLineSegment(sketch, "E2646", {"start": v(1.7, -26.05) * mm, "end": v(1.72, -26.12) * mm});
            skLineSegment(sketch, "E2647", {"start": v(1.72, -26.12) * mm, "end": v(1.75, -26.2) * mm});
            skLineSegment(sketch, "E2648", {"start": v(1.75, -26.2) * mm, "end": v(1.77, -26.26) * mm});
            skLineSegment(sketch, "E2649", {"start": v(1.77, -26.26) * mm, "end": v(1.78, -26.34) * mm});
            skLineSegment(sketch, "E2650", {"start": v(1.78, -26.34) * mm, "end": v(1.8, -26.41) * mm});
            skLineSegment(sketch, "E2651", {"start": v(1.8, -26.41) * mm, "end": v(1.81, -26.5) * mm});
            skLineSegment(sketch, "E2652", {"start": v(1.81, -26.5) * mm, "end": v(1.82, -26.57) * mm});
            skLineSegment(sketch, "E2653", {"start": v(1.82, -26.57) * mm, "end": v(1.83, -26.65) * mm});
            skLineSegment(sketch, "E2654", {"start": v(1.83, -26.65) * mm, "end": v(1.83, -26.73) * mm});
            skLineSegment(sketch, "E2655", {"start": v(1.83, -26.73) * mm, "end": v(1.83, -26.8) * mm});
            skLineSegment(sketch, "E2656", {"start": v(1.83, -26.8) * mm, "end": v(1.83, -26.88) * mm});
            skLineSegment(sketch, "E2657", {"start": v(1.83, -26.88) * mm, "end": v(1.83, -26.96) * mm});
            skLineSegment(sketch, "E2658", {"start": v(1.83, -26.96) * mm, "end": v(1.82, -27.04) * mm});
            skLineSegment(sketch, "E2659", {"start": v(1.82, -27.04) * mm, "end": v(1.8, -27.11) * mm});
            skLineSegment(sketch, "E2660", {"start": v(1.8, -27.11) * mm, "end": v(1.8, -27.18) * mm});
            skLineSegment(sketch, "E2661", {"start": v(1.8, -27.18) * mm, "end": v(1.78, -27.26) * mm});
            skLineSegment(sketch, "E2662", {"start": v(1.78, -27.26) * mm, "end": v(1.76, -27.33) * mm});
            skLineSegment(sketch, "E2663", {"start": v(1.76, -27.33) * mm, "end": v(1.74, -27.4) * mm});
            skLineSegment(sketch, "E2664", {"start": v(1.74, -27.4) * mm, "end": v(1.71, -27.47) * mm});
            skLineSegment(sketch, "E2665", {"start": v(1.71, -27.47) * mm, "end": v(1.68, -27.54) * mm});
            skLineSegment(sketch, "E2666", {"start": v(1.68, -27.54) * mm, "end": v(1.65, -27.6) * mm});
            skLineSegment(sketch, "E2667", {"start": v(1.65, -27.6) * mm, "end": v(1.62, -27.67) * mm});
            skLineSegment(sketch, "E2668", {"start": v(1.62, -27.67) * mm, "end": v(1.58, -27.74) * mm});
            skLineSegment(sketch, "E2669", {"start": v(1.58, -27.74) * mm, "end": v(1.54, -27.8) * mm});
            skLineSegment(sketch, "E2670", {"start": v(1.54, -27.8) * mm, "end": v(1.5, -27.86) * mm});
            skLineSegment(sketch, "E2671", {"start": v(1.5, -27.86) * mm, "end": v(1.46, -27.92) * mm});
            skLineSegment(sketch, "E2672", {"start": v(1.46, -27.92) * mm, "end": v(1.41, -27.98) * mm});
            skLineSegment(sketch, "E2673", {"start": v(1.41, -27.98) * mm, "end": v(1.37, -28.03) * mm});
            skLineSegment(sketch, "E2674", {"start": v(1.37, -28.03) * mm, "end": v(1.32, -28.09) * mm});
            skLineSegment(sketch, "E2675", {"start": v(1.32, -28.09) * mm, "end": v(1.27, -28.14) * mm});
            skLineSegment(sketch, "E2676", {"start": v(1.27, -28.14) * mm, "end": v(1.21, -28.19) * mm});
            skLineSegment(sketch, "E2677", {"start": v(1.21, -28.19) * mm, "end": v(1.16, -28.23) * mm});
            skLineSegment(sketch, "E2678", {"start": v(1.16, -28.23) * mm, "end": v(1.1, -28.28) * mm});
            skLineSegment(sketch, "E2679", {"start": v(1.1, -28.28) * mm, "end": v(1.04, -28.32) * mm});
            skLineSegment(sketch, "E2680", {"start": v(1.04, -28.32) * mm, "end": v(0.98, -28.36) * mm});
            skLineSegment(sketch, "E2681", {"start": v(0.98, -28.36) * mm, "end": v(0.92, -28.4) * mm});
            skLineSegment(sketch, "E2682", {"start": v(0.92, -28.4) * mm, "end": v(0.85, -28.44) * mm});
            skLineSegment(sketch, "E2683", {"start": v(0.85, -28.44) * mm, "end": v(0.79, -28.47) * mm});
            skLineSegment(sketch, "E2684", {"start": v(0.79, -28.47) * mm, "end": v(0.72, -28.5) * mm});
            skLineSegment(sketch, "E2685", {"start": v(0.72, -28.5) * mm, "end": v(0.65, -28.54) * mm});
            skLineSegment(sketch, "E2686", {"start": v(0.65, -28.54) * mm, "end": v(0.58, -28.57) * mm});
            skLineSegment(sketch, "E2687", {"start": v(0.58, -28.57) * mm, "end": v(0.5, -28.6) * mm});
            skLineSegment(sketch, "E2688", {"start": v(0.5, -28.6) * mm, "end": v(0.44, -28.61) * mm});
            skLineSegment(sketch, "E2689", {"start": v(0.44, -28.61) * mm, "end": v(0.36, -28.63) * mm});
            skLineSegment(sketch, "E2690", {"start": v(0.36, -28.63) * mm, "end": v(0.29, -28.65) * mm});
            skLineSegment(sketch, "E2691", {"start": v(0.29, -28.65) * mm, "end": v(0.21, -28.66) * mm});
            skLineSegment(sketch, "E2692", {"start": v(0.21, -28.66) * mm, "end": v(0.14, -28.67) * mm});
            skLineSegment(sketch, "E2693", {"start": v(0.14, -28.67) * mm, "end": v(0.06, -28.68) * mm});
            skLineSegment(sketch, "E2694", {"start": v(0.06, -28.68) * mm, "end": v(-0.02, -28.68) * mm});
            skLineSegment(sketch, "E2695", {"start": v(-0.02, -28.68) * mm, "end": v(-0.1, -28.69) * mm});
            skLineSegment(sketch, "E2696", {"start": v(-0.1, -25.29) * mm, "end": v(-0.17, -25.3) * mm});
            skLineSegment(sketch, "E2697", {"start": v(-0.17, -25.3) * mm, "end": v(-0.24, -25.3) * mm});
            skLineSegment(sketch, "E2698", {"start": v(-0.24, -25.3) * mm, "end": v(-0.3, -25.3) * mm});
            skLineSegment(sketch, "E2699", {"start": v(-0.3, -25.3) * mm, "end": v(-0.37, -25.3) * mm});
            skLineSegment(sketch, "E2700", {"start": v(-0.37, -25.3) * mm, "end": v(-0.44, -25.32) * mm});
            skLineSegment(sketch, "E2701", {"start": v(-0.44, -25.32) * mm, "end": v(-0.5, -25.33) * mm});
            skLineSegment(sketch, "E2702", {"start": v(-0.5, -25.33) * mm, "end": v(-0.56, -25.35) * mm});
            skLineSegment(sketch, "E2703", {"start": v(-0.56, -25.35) * mm, "end": v(-0.62, -25.36) * mm});
            skLineSegment(sketch, "E2704", {"start": v(-0.62, -25.36) * mm, "end": v(-0.68, -25.38) * mm});
            skLineSegment(sketch, "E2705", {"start": v(-0.68, -25.38) * mm, "end": v(-0.73, -25.4) * mm});
            skLineSegment(sketch, "E2706", {"start": v(-0.73, -25.4) * mm, "end": v(-0.79, -25.43) * mm});
            skLineSegment(sketch, "E2707", {"start": v(-0.79, -25.43) * mm, "end": v(-0.84, -25.46) * mm});
            skLineSegment(sketch, "E2708", {"start": v(-0.84, -25.46) * mm, "end": v(-0.89, -25.48) * mm});
            skLineSegment(sketch, "E2709", {"start": v(-0.89, -25.48) * mm, "end": v(-0.94, -25.51) * mm});
            skLineSegment(sketch, "E2710", {"start": v(-0.94, -25.51) * mm, "end": v(-0.99, -25.54) * mm});
            skLineSegment(sketch, "E2711", {"start": v(-0.99, -25.54) * mm, "end": v(-1.03, -25.58) * mm});
            skLineSegment(sketch, "E2712", {"start": v(-1.03, -25.58) * mm, "end": v(-1.08, -25.6) * mm});
            skLineSegment(sketch, "E2713", {"start": v(-1.08, -25.6) * mm, "end": v(-1.12, -25.64) * mm});
            skLineSegment(sketch, "E2714", {"start": v(-1.12, -25.64) * mm, "end": v(-1.17, -25.68) * mm});
            skLineSegment(sketch, "E2715", {"start": v(-1.17, -25.68) * mm, "end": v(-1.2, -25.72) * mm});
            skLineSegment(sketch, "E2716", {"start": v(-1.2, -25.72) * mm, "end": v(-1.25, -25.76) * mm});
            skLineSegment(sketch, "E2717", {"start": v(-1.25, -25.76) * mm, "end": v(-1.3, -25.8) * mm});
            skLineSegment(sketch, "E2718", {"start": v(-1.3, -25.8) * mm, "end": v(-1.33, -25.85) * mm});
            skLineSegment(sketch, "E2719", {"start": v(-1.33, -25.85) * mm, "end": v(-1.36, -25.9) * mm});
            skLineSegment(sketch, "E2720", {"start": v(-1.36, -25.9) * mm, "end": v(-1.4, -25.94) * mm});
            skLineSegment(sketch, "E2721", {"start": v(-1.4, -25.94) * mm, "end": v(-1.43, -25.99) * mm});
            skLineSegment(sketch, "E2722", {"start": v(-1.43, -25.99) * mm, "end": v(-1.46, -26.04) * mm});
            skLineSegment(sketch, "E2723", {"start": v(-1.46, -26.04) * mm, "end": v(-1.48, -26.1) * mm});
            skLineSegment(sketch, "E2724", {"start": v(-1.48, -26.1) * mm, "end": v(-1.5, -26.15) * mm});
            skLineSegment(sketch, "E2725", {"start": v(-1.5, -26.15) * mm, "end": v(-1.53, -26.2) * mm});
            skLineSegment(sketch, "E2726", {"start": v(-1.53, -26.2) * mm, "end": v(-1.55, -26.26) * mm});
            skLineSegment(sketch, "E2727", {"start": v(-1.55, -26.26) * mm, "end": v(-1.57, -26.31) * mm});
            skLineSegment(sketch, "E2728", {"start": v(-1.57, -26.31) * mm, "end": v(-1.58, -26.37) * mm});
            skLineSegment(sketch, "E2729", {"start": v(-1.58, -26.37) * mm, "end": v(-1.6, -26.43) * mm});
            skLineSegment(sketch, "E2730", {"start": v(-1.6, -26.43) * mm, "end": v(-1.6, -26.5) * mm});
            skLineSegment(sketch, "E2731", {"start": v(-1.6, -26.5) * mm, "end": v(-1.62, -26.55) * mm});
            skLineSegment(sketch, "E2732", {"start": v(-1.62, -26.55) * mm, "end": v(-1.62, -26.62) * mm});
            skLineSegment(sketch, "E2733", {"start": v(-1.62, -26.62) * mm, "end": v(-1.63, -26.68) * mm});
            skLineSegment(sketch, "E2734", {"start": v(-1.63, -26.68) * mm, "end": v(-1.63, -26.74) * mm});
            skLineSegment(sketch, "E2735", {"start": v(-1.63, -26.74) * mm, "end": v(-1.63, -26.8) * mm});
            skLineSegment(sketch, "E2736", {"start": v(-1.63, -26.8) * mm, "end": v(-1.63, -26.87) * mm});
            skLineSegment(sketch, "E2737", {"start": v(-1.63, -26.87) * mm, "end": v(-1.63, -26.93) * mm});
            skLineSegment(sketch, "E2738", {"start": v(-1.63, -26.93) * mm, "end": v(-1.62, -26.99) * mm});
            skLineSegment(sketch, "E2739", {"start": v(-1.62, -26.99) * mm, "end": v(-1.61, -27.05) * mm});
            skLineSegment(sketch, "E2740", {"start": v(-1.61, -27.05) * mm, "end": v(-1.6, -27.1) * mm});
            skLineSegment(sketch, "E2741", {"start": v(-1.6, -27.1) * mm, "end": v(-1.59, -27.16) * mm});
            skLineSegment(sketch, "E2742", {"start": v(-1.59, -27.16) * mm, "end": v(-1.57, -27.22) * mm});
            skLineSegment(sketch, "E2743", {"start": v(-1.57, -27.22) * mm, "end": v(-1.56, -27.27) * mm});
            skLineSegment(sketch, "E2744", {"start": v(-1.56, -27.27) * mm, "end": v(-1.54, -27.33) * mm});
            skLineSegment(sketch, "E2745", {"start": v(-1.54, -27.33) * mm, "end": v(-1.51, -27.38) * mm});
            skLineSegment(sketch, "E2746", {"start": v(-1.51, -27.38) * mm, "end": v(-1.49, -27.44) * mm});
            skLineSegment(sketch, "E2747", {"start": v(-1.49, -27.44) * mm, "end": v(-1.46, -27.49) * mm});
            skLineSegment(sketch, "E2748", {"start": v(-1.46, -27.49) * mm, "end": v(-1.43, -27.54) * mm});
            skLineSegment(sketch, "E2749", {"start": v(-1.43, -27.54) * mm, "end": v(-1.4, -27.59) * mm});
            skLineSegment(sketch, "E2750", {"start": v(-1.4, -27.59) * mm, "end": v(-1.37, -27.63) * mm});
            skLineSegment(sketch, "E2751", {"start": v(-1.37, -27.63) * mm, "end": v(-1.34, -27.68) * mm});
            skLineSegment(sketch, "E2752", {"start": v(-1.34, -27.68) * mm, "end": v(-1.3, -27.73) * mm});
            skLineSegment(sketch, "E2753", {"start": v(-1.3, -27.73) * mm, "end": v(-1.26, -27.77) * mm});
            skLineSegment(sketch, "E2754", {"start": v(-1.26, -27.77) * mm, "end": v(-1.22, -27.81) * mm});
            skLineSegment(sketch, "E2755", {"start": v(-1.22, -27.81) * mm, "end": v(-1.18, -27.85) * mm});
            skLineSegment(sketch, "E2756", {"start": v(-1.18, -27.85) * mm, "end": v(-1.14, -27.9) * mm});
            skLineSegment(sketch, "E2757", {"start": v(-1.14, -27.9) * mm, "end": v(-1.1, -27.93) * mm});
            skLineSegment(sketch, "E2758", {"start": v(-1.1, -27.93) * mm, "end": v(-1.05, -27.97) * mm});
            skLineSegment(sketch, "E2759", {"start": v(-1.05, -27.97) * mm, "end": v(-1, -28) * mm});
            skLineSegment(sketch, "E2760", {"start": v(-1, -28) * mm, "end": v(-0.96, -28.03) * mm});
            skLineSegment(sketch, "E2761", {"start": v(-0.96, -28.03) * mm, "end": v(-0.9, -28.06) * mm});
            skLineSegment(sketch, "E2762", {"start": v(-0.9, -28.06) * mm, "end": v(-0.85, -28.1) * mm});
            skLineSegment(sketch, "E2763", {"start": v(-0.85, -28.1) * mm, "end": v(-0.8, -28.12) * mm});
            skLineSegment(sketch, "E2764", {"start": v(-0.8, -28.12) * mm, "end": v(-0.75, -28.15) * mm});
            skLineSegment(sketch, "E2765", {"start": v(-0.75, -28.15) * mm, "end": v(-0.7, -28.17) * mm});
            skLineSegment(sketch, "E2766", {"start": v(-0.7, -28.17) * mm, "end": v(-0.64, -28.2) * mm});
            skLineSegment(sketch, "E2767", {"start": v(-0.64, -28.2) * mm, "end": v(-0.58, -28.21) * mm});
            skLineSegment(sketch, "E2768", {"start": v(-0.58, -28.21) * mm, "end": v(-0.52, -28.23) * mm});
            skLineSegment(sketch, "E2769", {"start": v(-0.52, -28.23) * mm, "end": v(-0.46, -28.25) * mm});
            skLineSegment(sketch, "E2770", {"start": v(-0.46, -28.25) * mm, "end": v(-0.4, -28.26) * mm});
            skLineSegment(sketch, "E2771", {"start": v(-0.4, -28.26) * mm, "end": v(-0.34, -28.27) * mm});
            skLineSegment(sketch, "E2772", {"start": v(-0.34, -28.27) * mm, "end": v(-0.28, -28.28) * mm});
            skLineSegment(sketch, "E2773", {"start": v(-0.28, -28.28) * mm, "end": v(-0.22, -28.28) * mm});
            skLineSegment(sketch, "E2774", {"start": v(-0.22, -28.28) * mm, "end": v(-0.16, -28.29) * mm});
            skLineSegment(sketch, "E2775", {"start": v(-0.16, -28.29) * mm, "end": v(-0.1, -28.29) * mm});
            skLineSegment(sketch, "E2776", {"start": v(-0.1, -28.29) * mm, "end": v(-0.03, -28.29) * mm});
            skLineSegment(sketch, "E2777", {"start": v(-0.03, -28.29) * mm, "end": v(0.03, -28.28) * mm});
            skLineSegment(sketch, "E2778", {"start": v(0.03, -28.28) * mm, "end": v(0.09, -28.28) * mm});
            skLineSegment(sketch, "E2779", {"start": v(0.09, -28.28) * mm, "end": v(0.15, -28.27) * mm});
            skLineSegment(sketch, "E2780", {"start": v(0.15, -28.27) * mm, "end": v(0.2, -28.26) * mm});
            skLineSegment(sketch, "E2781", {"start": v(0.2, -28.26) * mm, "end": v(0.27, -28.25) * mm});
            skLineSegment(sketch, "E2782", {"start": v(0.27, -28.25) * mm, "end": v(0.33, -28.23) * mm});
            skLineSegment(sketch, "E2783", {"start": v(0.33, -28.23) * mm, "end": v(0.38, -28.21) * mm});
            skLineSegment(sketch, "E2784", {"start": v(0.38, -28.21) * mm, "end": v(0.44, -28.2) * mm});
            skLineSegment(sketch, "E2785", {"start": v(0.44, -28.2) * mm, "end": v(0.5, -28.17) * mm});
            skLineSegment(sketch, "E2786", {"start": v(0.5, -28.17) * mm, "end": v(0.55, -28.15) * mm});
            skLineSegment(sketch, "E2787", {"start": v(0.55, -28.15) * mm, "end": v(0.6, -28.12) * mm});
            skLineSegment(sketch, "E2788", {"start": v(0.6, -28.12) * mm, "end": v(0.66, -28.1) * mm});
            skLineSegment(sketch, "E2789", {"start": v(0.66, -28.1) * mm, "end": v(0.7, -28.06) * mm});
            skLineSegment(sketch, "E2790", {"start": v(0.7, -28.06) * mm, "end": v(0.76, -28.03) * mm});
            skLineSegment(sketch, "E2791", {"start": v(0.76, -28.03) * mm, "end": v(0.8, -28) * mm});
            skLineSegment(sketch, "E2792", {"start": v(0.8, -28) * mm, "end": v(0.85, -27.97) * mm});
            skLineSegment(sketch, "E2793", {"start": v(0.85, -27.97) * mm, "end": v(0.9, -27.93) * mm});
            skLineSegment(sketch, "E2794", {"start": v(0.9, -27.93) * mm, "end": v(0.94, -27.9) * mm});
            skLineSegment(sketch, "E2795", {"start": v(0.94, -27.9) * mm, "end": v(0.98, -27.85) * mm});
            skLineSegment(sketch, "E2796", {"start": v(0.98, -27.85) * mm, "end": v(1.03, -27.81) * mm});
            skLineSegment(sketch, "E2797", {"start": v(1.03, -27.81) * mm, "end": v(1.06, -27.77) * mm});
            skLineSegment(sketch, "E2798", {"start": v(1.06, -27.77) * mm, "end": v(1.1, -27.73) * mm});
            skLineSegment(sketch, "E2799", {"start": v(1.1, -27.73) * mm, "end": v(1.14, -27.68) * mm});
            skLineSegment(sketch, "E2800", {"start": v(1.14, -27.68) * mm, "end": v(1.17, -27.63) * mm});
            skLineSegment(sketch, "E2801", {"start": v(1.17, -27.63) * mm, "end": v(1.2, -27.59) * mm});
            skLineSegment(sketch, "E2802", {"start": v(1.2, -27.59) * mm, "end": v(1.23, -27.54) * mm});
            skLineSegment(sketch, "E2803", {"start": v(1.23, -27.54) * mm, "end": v(1.26, -27.49) * mm});
            skLineSegment(sketch, "E2804", {"start": v(1.26, -27.49) * mm, "end": v(1.29, -27.44) * mm});
            skLineSegment(sketch, "E2805", {"start": v(1.29, -27.44) * mm, "end": v(1.31, -27.38) * mm});
            skLineSegment(sketch, "E2806", {"start": v(1.31, -27.38) * mm, "end": v(1.33, -27.33) * mm});
            skLineSegment(sketch, "E2807", {"start": v(1.33, -27.33) * mm, "end": v(1.36, -27.27) * mm});
            skLineSegment(sketch, "E2808", {"start": v(1.36, -27.27) * mm, "end": v(1.37, -27.22) * mm});
            skLineSegment(sketch, "E2809", {"start": v(1.37, -27.22) * mm, "end": v(1.39, -27.16) * mm});
            skLineSegment(sketch, "E2810", {"start": v(1.39, -27.16) * mm, "end": v(1.4, -27.1) * mm});
            skLineSegment(sketch, "E2811", {"start": v(1.4, -27.1) * mm, "end": v(1.41, -27.05) * mm});
            skLineSegment(sketch, "E2812", {"start": v(1.41, -27.05) * mm, "end": v(1.42, -26.99) * mm});
            skLineSegment(sketch, "E2813", {"start": v(1.42, -26.99) * mm, "end": v(1.43, -26.93) * mm});
            skLineSegment(sketch, "E2814", {"start": v(1.43, -26.93) * mm, "end": v(1.43, -26.87) * mm});
            skLineSegment(sketch, "E2815", {"start": v(1.43, -26.87) * mm, "end": v(1.43, -26.8) * mm});
            skLineSegment(sketch, "E2816", {"start": v(1.43, -26.8) * mm, "end": v(1.43, -26.74) * mm});
            skLineSegment(sketch, "E2817", {"start": v(1.43, -26.74) * mm, "end": v(1.43, -26.68) * mm});
            skLineSegment(sketch, "E2818", {"start": v(1.43, -26.68) * mm, "end": v(1.42, -26.62) * mm});
            skLineSegment(sketch, "E2819", {"start": v(1.42, -26.62) * mm, "end": v(1.42, -26.55) * mm});
            skLineSegment(sketch, "E2820", {"start": v(1.42, -26.55) * mm, "end": v(1.4, -26.5) * mm});
            skLineSegment(sketch, "E2821", {"start": v(1.4, -26.5) * mm, "end": v(1.4, -26.43) * mm});
            skLineSegment(sketch, "E2822", {"start": v(1.4, -26.43) * mm, "end": v(1.38, -26.37) * mm});
            skLineSegment(sketch, "E2823", {"start": v(1.38, -26.37) * mm, "end": v(1.36, -26.31) * mm});
            skLineSegment(sketch, "E2824", {"start": v(1.36, -26.31) * mm, "end": v(1.35, -26.26) * mm});
            skLineSegment(sketch, "E2825", {"start": v(1.35, -26.26) * mm, "end": v(1.33, -26.2) * mm});
            skLineSegment(sketch, "E2826", {"start": v(1.33, -26.2) * mm, "end": v(1.3, -26.15) * mm});
            skLineSegment(sketch, "E2827", {"start": v(1.3, -26.15) * mm, "end": v(1.28, -26.1) * mm});
            skLineSegment(sketch, "E2828", {"start": v(1.28, -26.1) * mm, "end": v(1.25, -26.04) * mm});
            skLineSegment(sketch, "E2829", {"start": v(1.25, -26.04) * mm, "end": v(1.22, -25.99) * mm});
            skLineSegment(sketch, "E2830", {"start": v(1.22, -25.99) * mm, "end": v(1.2, -25.94) * mm});
            skLineSegment(sketch, "E2831", {"start": v(1.2, -25.94) * mm, "end": v(1.16, -25.9) * mm});
            skLineSegment(sketch, "E2832", {"start": v(1.16, -25.9) * mm, "end": v(1.13, -25.85) * mm});
            skLineSegment(sketch, "E2833", {"start": v(1.13, -25.85) * mm, "end": v(1.09, -25.8) * mm});
            skLineSegment(sketch, "E2834", {"start": v(1.09, -25.8) * mm, "end": v(1.05, -25.76) * mm});
            skLineSegment(sketch, "E2835", {"start": v(1.05, -25.76) * mm, "end": v(1, -25.72) * mm});
            skLineSegment(sketch, "E2836", {"start": v(1, -25.72) * mm, "end": v(0.97, -25.68) * mm});
            skLineSegment(sketch, "E2837", {"start": v(0.97, -25.68) * mm, "end": v(0.92, -25.64) * mm});
            skLineSegment(sketch, "E2838", {"start": v(0.92, -25.64) * mm, "end": v(0.88, -25.6) * mm});
            skLineSegment(sketch, "E2839", {"start": v(0.88, -25.6) * mm, "end": v(0.83, -25.58) * mm});
            skLineSegment(sketch, "E2840", {"start": v(0.83, -25.58) * mm, "end": v(0.79, -25.54) * mm});
            skLineSegment(sketch, "E2841", {"start": v(0.79, -25.54) * mm, "end": v(0.74, -25.51) * mm});
            skLineSegment(sketch, "E2842", {"start": v(0.74, -25.51) * mm, "end": v(0.69, -25.48) * mm});
            skLineSegment(sketch, "E2843", {"start": v(0.69, -25.48) * mm, "end": v(0.64, -25.46) * mm});
            skLineSegment(sketch, "E2844", {"start": v(0.64, -25.46) * mm, "end": v(0.59, -25.43) * mm});
            skLineSegment(sketch, "E2845", {"start": v(0.59, -25.43) * mm, "end": v(0.53, -25.4) * mm});
            skLineSegment(sketch, "E2846", {"start": v(0.53, -25.4) * mm, "end": v(0.48, -25.38) * mm});
            skLineSegment(sketch, "E2847", {"start": v(0.48, -25.38) * mm, "end": v(0.42, -25.36) * mm});
            skLineSegment(sketch, "E2848", {"start": v(0.42, -25.36) * mm, "end": v(0.37, -25.35) * mm});
            skLineSegment(sketch, "E2849", {"start": v(0.37, -25.35) * mm, "end": v(0.3, -25.33) * mm});
            skLineSegment(sketch, "E2850", {"start": v(0.3, -25.33) * mm, "end": v(0.24, -25.32) * mm});
            skLineSegment(sketch, "E2851", {"start": v(0.24, -25.32) * mm, "end": v(0.18, -25.3) * mm});
            skLineSegment(sketch, "E2852", {"start": v(0.18, -25.3) * mm, "end": v(0.11, -25.3) * mm});
            skLineSegment(sketch, "E2853", {"start": v(0.11, -25.3) * mm, "end": v(0.05, -25.3) * mm});
            skLineSegment(sketch, "E2854", {"start": v(0.05, -25.3) * mm, "end": v(-0.02, -25.3) * mm});
            skLineSegment(sketch, "E2855", {"start": v(-0.02, -25.3) * mm, "end": v(-0.1, -25.29) * mm});
            skLineSegment(sketch, "E2856", {"start": v(20.55, -28.87) * mm, "end": v(20.42, -28.87) * mm});
            skLineSegment(sketch, "E2857", {"start": v(20.42, -28.87) * mm, "end": v(20.3, -28.86) * mm});
            skLineSegment(sketch, "E2858", {"start": v(20.3, -28.86) * mm, "end": v(20.17, -28.84) * mm});
            skLineSegment(sketch, "E2859", {"start": v(20.17, -28.84) * mm, "end": v(20.05, -28.81) * mm});
            skLineSegment(sketch, "E2860", {"start": v(20.05, -28.81) * mm, "end": v(19.94, -28.78) * mm});
            skLineSegment(sketch, "E2861", {"start": v(19.94, -28.78) * mm, "end": v(19.83, -28.73) * mm});
            skLineSegment(sketch, "E2862", {"start": v(19.83, -28.73) * mm, "end": v(19.73, -28.68) * mm});
            skLineSegment(sketch, "E2863", {"start": v(19.73, -28.68) * mm, "end": v(19.63, -28.63) * mm});
            skLineSegment(sketch, "E2864", {"start": v(19.63, -28.63) * mm, "end": v(19.53, -28.56) * mm});
            skLineSegment(sketch, "E2865", {"start": v(19.53, -28.56) * mm, "end": v(19.44, -28.49) * mm});
            skLineSegment(sketch, "E2866", {"start": v(19.44, -28.49) * mm, "end": v(19.4, -28.46) * mm});
            skLineSegment(sketch, "E2867", {"start": v(19.4, -28.46) * mm, "end": v(19.37, -28.43) * mm});
            skLineSegment(sketch, "E2868", {"start": v(19.37, -28.43) * mm, "end": v(19.34, -28.4) * mm});
            skLineSegment(sketch, "E2869", {"start": v(19.34, -28.4) * mm, "end": v(19.3, -28.36) * mm});
            skLineSegment(sketch, "E2870", {"start": v(19.3, -28.36) * mm, "end": v(19.27, -28.33) * mm});
            skLineSegment(sketch, "E2871", {"start": v(19.27, -28.33) * mm, "end": v(19.24, -28.3) * mm});
            skLineSegment(sketch, "E2872", {"start": v(19.24, -28.3) * mm, "end": v(19.21, -28.26) * mm});
            skLineSegment(sketch, "E2873", {"start": v(19.21, -28.26) * mm, "end": v(19.18, -28.22) * mm});
            skLineSegment(sketch, "E2874", {"start": v(19.18, -28.22) * mm, "end": v(19.15, -28.18) * mm});
            skLineSegment(sketch, "E2875", {"start": v(19.15, -28.18) * mm, "end": v(19.12, -28.14) * mm});
            skLineSegment(sketch, "E2876", {"start": v(19.12, -28.14) * mm, "end": v(19.1, -28.1) * mm});
            skLineSegment(sketch, "E2877", {"start": v(19.1, -28.1) * mm, "end": v(19.07, -28.06) * mm});
            skLineSegment(sketch, "E2878", {"start": v(19.07, -28.06) * mm, "end": v(19.04, -28.02) * mm});
            skLineSegment(sketch, "E2879", {"start": v(19.04, -28.02) * mm, "end": v(19.02, -27.98) * mm});
            skLineSegment(sketch, "E2880", {"start": v(19.02, -27.98) * mm, "end": v(19, -27.94) * mm});
            skLineSegment(sketch, "E2881", {"start": v(19, -27.94) * mm, "end": v(18.97, -27.9) * mm});
            skLineSegment(sketch, "E2882", {"start": v(18.97, -27.9) * mm, "end": v(18.96, -27.86) * mm});
            skLineSegment(sketch, "E2883", {"start": v(18.96, -27.86) * mm, "end": v(18.94, -27.82) * mm});
            skLineSegment(sketch, "E2884", {"start": v(18.94, -27.82) * mm, "end": v(18.92, -27.78) * mm});
            skLineSegment(sketch, "E2885", {"start": v(18.92, -27.78) * mm, "end": v(18.9, -27.74) * mm});
            skLineSegment(sketch, "E2886", {"start": v(18.9, -27.74) * mm, "end": v(19.3, -27.58) * mm});
            skLineSegment(sketch, "E2887", {"start": v(19.3, -27.58) * mm, "end": v(19.3, -27.61) * mm});
            skLineSegment(sketch, "E2888", {"start": v(19.3, -27.61) * mm, "end": v(19.32, -27.65) * mm});
            skLineSegment(sketch, "E2889", {"start": v(19.32, -27.65) * mm, "end": v(19.34, -27.68) * mm});
            skLineSegment(sketch, "E2890", {"start": v(19.34, -27.68) * mm, "end": v(19.36, -27.71) * mm});
            skLineSegment(sketch, "E2891", {"start": v(19.36, -27.71) * mm, "end": v(19.38, -27.74) * mm});
            skLineSegment(sketch, "E2892", {"start": v(19.38, -27.74) * mm, "end": v(19.4, -27.78) * mm});
            skLineSegment(sketch, "E2893", {"start": v(19.4, -27.78) * mm, "end": v(19.41, -27.8) * mm});
            skLineSegment(sketch, "E2894", {"start": v(19.41, -27.8) * mm, "end": v(19.43, -27.84) * mm});
            skLineSegment(sketch, "E2895", {"start": v(19.43, -27.84) * mm, "end": v(19.45, -27.87) * mm});
            skLineSegment(sketch, "E2896", {"start": v(19.45, -27.87) * mm, "end": v(19.47, -27.9) * mm});
            skLineSegment(sketch, "E2897", {"start": v(19.47, -27.9) * mm, "end": v(19.5, -27.93) * mm});
            skLineSegment(sketch, "E2898", {"start": v(19.5, -27.93) * mm, "end": v(19.52, -27.96) * mm});
            skLineSegment(sketch, "E2899", {"start": v(19.52, -27.96) * mm, "end": v(19.54, -27.99) * mm});
            skLineSegment(sketch, "E2900", {"start": v(19.54, -27.99) * mm, "end": v(19.56, -28.02) * mm});
            skLineSegment(sketch, "E2901", {"start": v(19.56, -28.02) * mm, "end": v(19.59, -28.05) * mm});
            skLineSegment(sketch, "E2902", {"start": v(19.59, -28.05) * mm, "end": v(19.61, -28.07) * mm});
            skLineSegment(sketch, "E2903", {"start": v(19.61, -28.07) * mm, "end": v(19.64, -28.1) * mm});
            skLineSegment(sketch, "E2904", {"start": v(19.64, -28.1) * mm, "end": v(19.67, -28.12) * mm});
            skLineSegment(sketch, "E2905", {"start": v(19.67, -28.12) * mm, "end": v(19.7, -28.15) * mm});
            skLineSegment(sketch, "E2906", {"start": v(19.7, -28.15) * mm, "end": v(19.72, -28.17) * mm});
            skLineSegment(sketch, "E2907", {"start": v(19.72, -28.17) * mm, "end": v(19.75, -28.2) * mm});
            skLineSegment(sketch, "E2908", {"start": v(19.75, -28.2) * mm, "end": v(19.79, -28.22) * mm});
            skLineSegment(sketch, "E2909", {"start": v(19.79, -28.22) * mm, "end": v(19.82, -28.25) * mm});
            skLineSegment(sketch, "E2910", {"start": v(19.82, -28.25) * mm, "end": v(19.86, -28.27) * mm});
            skLineSegment(sketch, "E2911", {"start": v(19.86, -28.27) * mm, "end": v(19.9, -28.3) * mm});
            skLineSegment(sketch, "E2912", {"start": v(19.9, -28.3) * mm, "end": v(19.93, -28.31) * mm});
            skLineSegment(sketch, "E2913", {"start": v(19.93, -28.31) * mm, "end": v(19.97, -28.33) * mm});
            skLineSegment(sketch, "E2914", {"start": v(19.97, -28.33) * mm, "end": v(20.01, -28.35) * mm});
            skLineSegment(sketch, "E2915", {"start": v(20.01, -28.35) * mm, "end": v(20.05, -28.37) * mm});
            skLineSegment(sketch, "E2916", {"start": v(20.05, -28.37) * mm, "end": v(20.1, -28.39) * mm});
            skLineSegment(sketch, "E2917", {"start": v(20.1, -28.39) * mm, "end": v(20.13, -28.4) * mm});
            skLineSegment(sketch, "E2918", {"start": v(20.13, -28.4) * mm, "end": v(20.17, -28.42) * mm});
            skLineSegment(sketch, "E2919", {"start": v(20.17, -28.42) * mm, "end": v(20.22, -28.43) * mm});
            skLineSegment(sketch, "E2920", {"start": v(20.22, -28.43) * mm, "end": v(20.26, -28.44) * mm});
            skLineSegment(sketch, "E2921", {"start": v(20.26, -28.44) * mm, "end": v(20.3, -28.45) * mm});
            skLineSegment(sketch, "E2922", {"start": v(20.3, -28.45) * mm, "end": v(20.35, -28.46) * mm});
            skLineSegment(sketch, "E2923", {"start": v(20.35, -28.46) * mm, "end": v(20.4, -28.46) * mm});
            skLineSegment(sketch, "E2924", {"start": v(20.4, -28.46) * mm, "end": v(20.45, -28.47) * mm});
            skLineSegment(sketch, "E2925", {"start": v(20.45, -28.47) * mm, "end": v(20.5, -28.47) * mm});
            skLineSegment(sketch, "E2926", {"start": v(20.5, -28.47) * mm, "end": v(20.55, -28.47) * mm});
            skLineSegment(sketch, "E2927", {"start": v(20.55, -28.47) * mm, "end": v(20.6, -28.47) * mm});
            skLineSegment(sketch, "E2928", {"start": v(20.6, -28.47) * mm, "end": v(20.67, -28.47) * mm});
            skLineSegment(sketch, "E2929", {"start": v(20.67, -28.47) * mm, "end": v(20.73, -28.46) * mm});
            skLineSegment(sketch, "E2930", {"start": v(20.73, -28.46) * mm, "end": v(20.78, -28.45) * mm});
            skLineSegment(sketch, "E2931", {"start": v(20.78, -28.45) * mm, "end": v(20.84, -28.44) * mm});
            skLineSegment(sketch, "E2932", {"start": v(20.84, -28.44) * mm, "end": v(20.9, -28.43) * mm});
            skLineSegment(sketch, "E2933", {"start": v(20.9, -28.43) * mm, "end": v(20.95, -28.42) * mm});
            skLineSegment(sketch, "E2934", {"start": v(20.95, -28.42) * mm, "end": v(21, -28.4) * mm});
            skLineSegment(sketch, "E2935", {"start": v(21, -28.4) * mm, "end": v(21.05, -28.38) * mm});
            skLineSegment(sketch, "E2936", {"start": v(21.05, -28.38) * mm, "end": v(21.1, -28.36) * mm});
            skLineSegment(sketch, "E2937", {"start": v(21.1, -28.36) * mm, "end": v(21.15, -28.34) * mm});
            skLineSegment(sketch, "E2938", {"start": v(21.15, -28.34) * mm, "end": v(21.2, -28.31) * mm});
            skLineSegment(sketch, "E2939", {"start": v(21.2, -28.31) * mm, "end": v(21.25, -28.29) * mm});
            skLineSegment(sketch, "E2940", {"start": v(21.25, -28.29) * mm, "end": v(21.3, -28.26) * mm});
            skLineSegment(sketch, "E2941", {"start": v(21.3, -28.26) * mm, "end": v(21.33, -28.23) * mm});
            skLineSegment(sketch, "E2942", {"start": v(21.33, -28.23) * mm, "end": v(21.38, -28.2) * mm});
            skLineSegment(sketch, "E2943", {"start": v(21.38, -28.2) * mm, "end": v(21.42, -28.16) * mm});
            skLineSegment(sketch, "E2944", {"start": v(21.42, -28.16) * mm, "end": v(21.46, -28.12) * mm});
            skLineSegment(sketch, "E2945", {"start": v(21.46, -28.12) * mm, "end": v(21.5, -28.09) * mm});
            skLineSegment(sketch, "E2946", {"start": v(21.5, -28.09) * mm, "end": v(21.53, -28.05) * mm});
            skLineSegment(sketch, "E2947", {"start": v(21.53, -28.05) * mm, "end": v(21.56, -28) * mm});
            skLineSegment(sketch, "E2948", {"start": v(21.56, -28) * mm, "end": v(21.6, -27.96) * mm});
            skLineSegment(sketch, "E2949", {"start": v(21.6, -27.96) * mm, "end": v(21.63, -27.92) * mm});
            skLineSegment(sketch, "E2950", {"start": v(21.63, -27.92) * mm, "end": v(21.66, -27.87) * mm});
            skLineSegment(sketch, "E2951", {"start": v(21.66, -27.87) * mm, "end": v(21.68, -27.82) * mm});
            skLineSegment(sketch, "E2952", {"start": v(21.68, -27.82) * mm, "end": v(21.71, -27.77) * mm});
            skLineSegment(sketch, "E2953", {"start": v(21.71, -27.77) * mm, "end": v(21.74, -27.72) * mm});
            skLineSegment(sketch, "E2954", {"start": v(21.74, -27.72) * mm, "end": v(21.76, -27.67) * mm});
            skLineSegment(sketch, "E2955", {"start": v(21.76, -27.67) * mm, "end": v(21.78, -27.61) * mm});
            skLineSegment(sketch, "E2956", {"start": v(21.78, -27.61) * mm, "end": v(21.8, -27.55) * mm});
            skLineSegment(sketch, "E2957", {"start": v(21.8, -27.55) * mm, "end": v(21.82, -27.5) * mm});
            skLineSegment(sketch, "E2958", {"start": v(21.82, -27.5) * mm, "end": v(21.84, -27.44) * mm});
            skLineSegment(sketch, "E2959", {"start": v(21.84, -27.44) * mm, "end": v(21.85, -27.38) * mm});
            skLineSegment(sketch, "E2960", {"start": v(21.85, -27.38) * mm, "end": v(21.86, -27.31) * mm});
            skLineSegment(sketch, "E2961", {"start": v(21.86, -27.31) * mm, "end": v(21.87, -27.25) * mm});
            skLineSegment(sketch, "E2962", {"start": v(21.87, -27.25) * mm, "end": v(21.88, -27.18) * mm});
            skLineSegment(sketch, "E2963", {"start": v(21.88, -27.18) * mm, "end": v(21.89, -27.12) * mm});
            skLineSegment(sketch, "E2964", {"start": v(21.89, -27.12) * mm, "end": v(21.9, -27.05) * mm});
            skLineSegment(sketch, "E2965", {"start": v(21.9, -27.05) * mm, "end": v(21.9, -26.98) * mm});
            skLineSegment(sketch, "E2966", {"start": v(21.9, -26.98) * mm, "end": v(21.9, -26.91) * mm});
            skLineSegment(sketch, "E2967", {"start": v(21.9, -26.91) * mm, "end": v(21.9, -24.15) * mm});
            skLineSegment(sketch, "E2968", {"start": v(21.9, -24.15) * mm, "end": v(22.3, -24.15) * mm});
            skLineSegment(sketch, "E2969", {"start": v(22.3, -24.15) * mm, "end": v(22.3, -26.91) * mm});
            skLineSegment(sketch, "E2970", {"start": v(22.3, -26.91) * mm, "end": v(22.3, -27) * mm});
            skLineSegment(sketch, "E2971", {"start": v(22.3, -27) * mm, "end": v(22.3, -27.08) * mm});
            skLineSegment(sketch, "E2972", {"start": v(22.3, -27.08) * mm, "end": v(22.29, -27.16) * mm});
            skLineSegment(sketch, "E2973", {"start": v(22.29, -27.16) * mm, "end": v(22.28, -27.24) * mm});
            skLineSegment(sketch, "E2974", {"start": v(22.28, -27.24) * mm, "end": v(22.27, -27.32) * mm});
            skLineSegment(sketch, "E2975", {"start": v(22.27, -27.32) * mm, "end": v(22.26, -27.4) * mm});
            skLineSegment(sketch, "E2976", {"start": v(22.26, -27.4) * mm, "end": v(22.24, -27.47) * mm});
            skLineSegment(sketch, "E2977", {"start": v(22.24, -27.47) * mm, "end": v(22.22, -27.54) * mm});
            skLineSegment(sketch, "E2978", {"start": v(22.22, -27.54) * mm, "end": v(22.2, -27.62) * mm});
            skLineSegment(sketch, "E2979", {"start": v(22.2, -27.62) * mm, "end": v(22.18, -27.69) * mm});
            skLineSegment(sketch, "E2980", {"start": v(22.18, -27.69) * mm, "end": v(22.16, -27.76) * mm});
            skLineSegment(sketch, "E2981", {"start": v(22.16, -27.76) * mm, "end": v(22.13, -27.83) * mm});
            skLineSegment(sketch, "E2982", {"start": v(22.13, -27.83) * mm, "end": v(22.1, -27.9) * mm});
            skLineSegment(sketch, "E2983", {"start": v(22.1, -27.9) * mm, "end": v(22.07, -27.96) * mm});
            skLineSegment(sketch, "E2984", {"start": v(22.07, -27.96) * mm, "end": v(22.04, -28.02) * mm});
            skLineSegment(sketch, "E2985", {"start": v(22.04, -28.02) * mm, "end": v(22, -28.08) * mm});
            skLineSegment(sketch, "E2986", {"start": v(22, -28.08) * mm, "end": v(21.96, -28.14) * mm});
            skLineSegment(sketch, "E2987", {"start": v(21.96, -28.14) * mm, "end": v(21.92, -28.2) * mm});
            skLineSegment(sketch, "E2988", {"start": v(21.92, -28.2) * mm, "end": v(21.88, -28.25) * mm});
            skLineSegment(sketch, "E2989", {"start": v(21.88, -28.25) * mm, "end": v(21.83, -28.3) * mm});
            skLineSegment(sketch, "E2990", {"start": v(21.83, -28.3) * mm, "end": v(21.78, -28.36) * mm});
            skLineSegment(sketch, "E2991", {"start": v(21.78, -28.36) * mm, "end": v(21.73, -28.4) * mm});
            skLineSegment(sketch, "E2992", {"start": v(21.73, -28.4) * mm, "end": v(21.68, -28.46) * mm});
            skLineSegment(sketch, "E2993", {"start": v(21.68, -28.46) * mm, "end": v(21.63, -28.5) * mm});
            skLineSegment(sketch, "E2994", {"start": v(21.63, -28.5) * mm, "end": v(21.57, -28.55) * mm});
            skLineSegment(sketch, "E2995", {"start": v(21.57, -28.55) * mm, "end": v(21.52, -28.59) * mm});
            skLineSegment(sketch, "E2996", {"start": v(21.52, -28.59) * mm, "end": v(21.46, -28.63) * mm});
            skLineSegment(sketch, "E2997", {"start": v(21.46, -28.63) * mm, "end": v(21.4, -28.66) * mm});
            skLineSegment(sketch, "E2998", {"start": v(21.4, -28.66) * mm, "end": v(21.33, -28.7) * mm});
            skLineSegment(sketch, "E2999", {"start": v(21.33, -28.7) * mm, "end": v(21.27, -28.73) * mm});
            skLineSegment(sketch, "E3000", {"start": v(21.27, -28.73) * mm, "end": v(21.2, -28.75) * mm});
            skLineSegment(sketch, "E3001", {"start": v(21.2, -28.75) * mm, "end": v(21.14, -28.78) * mm});
            skLineSegment(sketch, "E3002", {"start": v(21.14, -28.78) * mm, "end": v(21.07, -28.8) * mm});
            skLineSegment(sketch, "E3003", {"start": v(21.07, -28.8) * mm, "end": v(21, -28.82) * mm});
            skLineSegment(sketch, "E3004", {"start": v(21, -28.82) * mm, "end": v(20.93, -28.84) * mm});
            skLineSegment(sketch, "E3005", {"start": v(20.93, -28.84) * mm, "end": v(20.85, -28.85) * mm});
            skLineSegment(sketch, "E3006", {"start": v(20.85, -28.85) * mm, "end": v(20.78, -28.86) * mm});
            skLineSegment(sketch, "E3007", {"start": v(20.78, -28.86) * mm, "end": v(20.7, -28.87) * mm});
            skLineSegment(sketch, "E3008", {"start": v(20.7, -28.87) * mm, "end": v(20.63, -28.87) * mm});
            skLineSegment(sketch, "E3009", {"start": v(20.63, -28.87) * mm, "end": v(20.55, -28.87) * mm});
            skLineSegment(sketch, "E3010", {"start": v(20.51, -26.17) * mm, "end": v(20.43, -26.17) * mm});
            skLineSegment(sketch, "E3011", {"start": v(20.43, -26.17) * mm, "end": v(20.34, -26.17) * mm});
            skLineSegment(sketch, "E3012", {"start": v(20.34, -26.17) * mm, "end": v(20.26, -26.16) * mm});
            skLineSegment(sketch, "E3013", {"start": v(20.26, -26.16) * mm, "end": v(20.18, -26.15) * mm});
            skLineSegment(sketch, "E3014", {"start": v(20.18, -26.15) * mm, "end": v(20.1, -26.13) * mm});
            skLineSegment(sketch, "E3015", {"start": v(20.1, -26.13) * mm, "end": v(20.02, -26.11) * mm});
            skLineSegment(sketch, "E3016", {"start": v(20.02, -26.11) * mm, "end": v(19.94, -26.1) * mm});
            skLineSegment(sketch, "E3017", {"start": v(19.94, -26.1) * mm, "end": v(19.87, -26.07) * mm});
            skLineSegment(sketch, "E3018", {"start": v(19.87, -26.07) * mm, "end": v(19.8, -26.04) * mm});
            skLineSegment(sketch, "E3019", {"start": v(19.8, -26.04) * mm, "end": v(19.73, -26.01) * mm});
            skLineSegment(sketch, "E3020", {"start": v(19.73, -26.01) * mm, "end": v(19.67, -25.98) * mm});
            skLineSegment(sketch, "E3021", {"start": v(19.67, -25.98) * mm, "end": v(19.6, -25.94) * mm});
            skLineSegment(sketch, "E3022", {"start": v(19.6, -25.94) * mm, "end": v(19.54, -25.9) * mm});
            skLineSegment(sketch, "E3023", {"start": v(19.54, -25.9) * mm, "end": v(19.48, -25.86) * mm});
            skLineSegment(sketch, "E3024", {"start": v(19.48, -25.86) * mm, "end": v(19.42, -25.82) * mm});
            skLineSegment(sketch, "E3025", {"start": v(19.42, -25.82) * mm, "end": v(19.37, -25.78) * mm});
            skLineSegment(sketch, "E3026", {"start": v(19.37, -25.78) * mm, "end": v(19.31, -25.73) * mm});
            skLineSegment(sketch, "E3027", {"start": v(19.31, -25.73) * mm, "end": v(19.26, -25.68) * mm});
            skLineSegment(sketch, "E3028", {"start": v(19.26, -25.68) * mm, "end": v(19.21, -25.63) * mm});
            skLineSegment(sketch, "E3029", {"start": v(19.21, -25.63) * mm, "end": v(19.17, -25.57) * mm});
            skLineSegment(sketch, "E3030", {"start": v(19.17, -25.57) * mm, "end": v(19.12, -25.52) * mm});
            skLineSegment(sketch, "E3031", {"start": v(19.12, -25.52) * mm, "end": v(19.08, -25.46) * mm});
            skLineSegment(sketch, "E3032", {"start": v(19.08, -25.46) * mm, "end": v(19.04, -25.4) * mm});
            skLineSegment(sketch, "E3033", {"start": v(19.04, -25.4) * mm, "end": v(19, -25.34) * mm});
            skLineSegment(sketch, "E3034", {"start": v(19, -25.34) * mm, "end": v(18.97, -25.28) * mm});
            skLineSegment(sketch, "E3035", {"start": v(18.97, -25.28) * mm, "end": v(18.94, -25.21) * mm});
            skLineSegment(sketch, "E3036", {"start": v(18.94, -25.21) * mm, "end": v(18.91, -25.15) * mm});
            skLineSegment(sketch, "E3037", {"start": v(18.91, -25.15) * mm, "end": v(18.88, -25.08) * mm});
            skLineSegment(sketch, "E3038", {"start": v(18.88, -25.08) * mm, "end": v(18.86, -25) * mm});
            skLineSegment(sketch, "E3039", {"start": v(18.86, -25) * mm, "end": v(18.84, -24.93) * mm});
            skLineSegment(sketch, "E3040", {"start": v(18.84, -24.93) * mm, "end": v(18.82, -24.86) * mm});
            skLineSegment(sketch, "E3041", {"start": v(18.82, -24.86) * mm, "end": v(18.8, -24.78) * mm});
            skLineSegment(sketch, "E3042", {"start": v(18.8, -24.78) * mm, "end": v(18.78, -24.7) * mm});
            skLineSegment(sketch, "E3043", {"start": v(18.78, -24.7) * mm, "end": v(18.77, -24.63) * mm});
            skLineSegment(sketch, "E3044", {"start": v(18.77, -24.63) * mm, "end": v(18.76, -24.55) * mm});
            skLineSegment(sketch, "E3045", {"start": v(18.76, -24.55) * mm, "end": v(18.75, -24.47) * mm});
            skLineSegment(sketch, "E3046", {"start": v(18.75, -24.47) * mm, "end": v(18.74, -24.4) * mm});
            skLineSegment(sketch, "E3047", {"start": v(18.74, -24.4) * mm, "end": v(18.74, -24.31) * mm});
            skLineSegment(sketch, "E3048", {"start": v(18.74, -24.31) * mm, "end": v(18.73, -24.23) * mm});
            skLineSegment(sketch, "E3049", {"start": v(18.73, -24.23) * mm, "end": v(18.73, -24.15) * mm});
            skLineSegment(sketch, "E3050", {"start": v(18.73, -24.15) * mm, "end": v(18.73, -24.09) * mm});
            skLineSegment(sketch, "E3051", {"start": v(18.73, -24.09) * mm, "end": v(18.73, -24.02) * mm});
            skLineSegment(sketch, "E3052", {"start": v(18.73, -24.02) * mm, "end": v(18.74, -23.95) * mm});
            skLineSegment(sketch, "E3053", {"start": v(18.74, -23.95) * mm, "end": v(18.74, -23.89) * mm});
            skLineSegment(sketch, "E3054", {"start": v(18.74, -23.89) * mm, "end": v(18.75, -23.82) * mm});
            skLineSegment(sketch, "E3055", {"start": v(18.75, -23.82) * mm, "end": v(18.76, -23.76) * mm});
            skLineSegment(sketch, "E3056", {"start": v(18.76, -23.76) * mm, "end": v(18.77, -23.7) * mm});
            skLineSegment(sketch, "E3057", {"start": v(18.77, -23.7) * mm, "end": v(18.78, -23.63) * mm});
            skLineSegment(sketch, "E3058", {"start": v(18.78, -23.63) * mm, "end": v(18.8, -23.56) * mm});
            skLineSegment(sketch, "E3059", {"start": v(18.8, -23.56) * mm, "end": v(18.8, -23.5) * mm});
            skLineSegment(sketch, "E3060", {"start": v(18.8, -23.5) * mm, "end": v(18.82, -23.43) * mm});
            skLineSegment(sketch, "E3061", {"start": v(18.82, -23.43) * mm, "end": v(18.84, -23.37) * mm});
            skLineSegment(sketch, "E3062", {"start": v(18.84, -23.37) * mm, "end": v(18.86, -23.3) * mm});
            skLineSegment(sketch, "E3063", {"start": v(18.86, -23.3) * mm, "end": v(18.88, -23.25) * mm});
            skLineSegment(sketch, "E3064", {"start": v(18.88, -23.25) * mm, "end": v(18.9, -23.2) * mm});
            skLineSegment(sketch, "E3065", {"start": v(18.9, -23.2) * mm, "end": v(18.93, -23.13) * mm});
            skLineSegment(sketch, "E3066", {"start": v(18.93, -23.13) * mm, "end": v(18.95, -23.08) * mm});
            skLineSegment(sketch, "E3067", {"start": v(18.95, -23.08) * mm, "end": v(18.98, -23.03) * mm});
            skLineSegment(sketch, "E3068", {"start": v(18.98, -23.03) * mm, "end": v(19, -22.97) * mm});
            skLineSegment(sketch, "E3069", {"start": v(19, -22.97) * mm, "end": v(19.04, -22.92) * mm});
            skLineSegment(sketch, "E3070", {"start": v(19.04, -22.92) * mm, "end": v(19.08, -22.85) * mm});
            skLineSegment(sketch, "E3071", {"start": v(19.08, -22.85) * mm, "end": v(19.13, -22.78) * mm});
            skLineSegment(sketch, "E3072", {"start": v(19.13, -22.78) * mm, "end": v(19.19, -22.72) * mm});
            skLineSegment(sketch, "E3073", {"start": v(19.19, -22.72) * mm, "end": v(19.24, -22.66) * mm});
            skLineSegment(sketch, "E3074", {"start": v(19.24, -22.66) * mm, "end": v(19.3, -22.6) * mm});
            skLineSegment(sketch, "E3075", {"start": v(19.3, -22.6) * mm, "end": v(19.36, -22.54) * mm});
            skLineSegment(sketch, "E3076", {"start": v(19.36, -22.54) * mm, "end": v(19.43, -22.49) * mm});
            skLineSegment(sketch, "E3077", {"start": v(19.43, -22.49) * mm, "end": v(19.5, -22.44) * mm});
            skLineSegment(sketch, "E3078", {"start": v(19.5, -22.44) * mm, "end": v(19.56, -22.4) * mm});
            skLineSegment(sketch, "E3079", {"start": v(19.56, -22.4) * mm, "end": v(19.64, -22.35) * mm});
            skLineSegment(sketch, "E3080", {"start": v(19.64, -22.35) * mm, "end": v(19.72, -22.31) * mm});
            skLineSegment(sketch, "E3081", {"start": v(19.72, -22.31) * mm, "end": v(19.8, -22.28) * mm});
            skLineSegment(sketch, "E3082", {"start": v(19.8, -22.28) * mm, "end": v(19.88, -22.24) * mm});
            skLineSegment(sketch, "E3083", {"start": v(19.88, -22.24) * mm, "end": v(19.96, -22.22) * mm});
            skLineSegment(sketch, "E3084", {"start": v(19.96, -22.22) * mm, "end": v(20.05, -22.2) * mm});
            skLineSegment(sketch, "E3085", {"start": v(20.05, -22.2) * mm, "end": v(20.13, -22.18) * mm});
            skLineSegment(sketch, "E3086", {"start": v(20.13, -22.18) * mm, "end": v(20.23, -22.16) * mm});
            skLineSegment(sketch, "E3087", {"start": v(20.23, -22.16) * mm, "end": v(20.32, -22.15) * mm});
            skLineSegment(sketch, "E3088", {"start": v(20.32, -22.15) * mm, "end": v(20.41, -22.14) * mm});
            skLineSegment(sketch, "E3089", {"start": v(20.41, -22.14) * mm, "end": v(20.51, -22.14) * mm});
            skLineSegment(sketch, "E3090", {"start": v(20.51, -22.14) * mm, "end": v(20.6, -22.14) * mm});
            skLineSegment(sketch, "E3091", {"start": v(20.6, -22.14) * mm, "end": v(20.67, -22.15) * mm});
            skLineSegment(sketch, "E3092", {"start": v(20.67, -22.15) * mm, "end": v(20.75, -22.16) * mm});
            skLineSegment(sketch, "E3093", {"start": v(20.75, -22.16) * mm, "end": v(20.83, -22.17) * mm});
            skLineSegment(sketch, "E3094", {"start": v(20.83, -22.17) * mm, "end": v(20.9, -22.18) * mm});
            skLineSegment(sketch, "E3095", {"start": v(20.9, -22.18) * mm, "end": v(20.98, -22.2) * mm});
            skLineSegment(sketch, "E3096", {"start": v(20.98, -22.2) * mm, "end": v(21.05, -22.22) * mm});
            skLineSegment(sketch, "E3097", {"start": v(21.05, -22.22) * mm, "end": v(21.12, -22.24) * mm});
            skLineSegment(sketch, "E3098", {"start": v(21.12, -22.24) * mm, "end": v(21.19, -22.26) * mm});
            skLineSegment(sketch, "E3099", {"start": v(21.19, -22.26) * mm, "end": v(21.25, -22.3) * mm});
            skLineSegment(sketch, "E3100", {"start": v(21.25, -22.3) * mm, "end": v(21.32, -22.32) * mm});
            skLineSegment(sketch, "E3101", {"start": v(21.32, -22.32) * mm, "end": v(21.38, -22.35) * mm});
            skLineSegment(sketch, "E3102", {"start": v(21.38, -22.35) * mm, "end": v(21.44, -22.39) * mm});
            skLineSegment(sketch, "E3103", {"start": v(21.44, -22.39) * mm, "end": v(21.5, -22.43) * mm});
            skLineSegment(sketch, "E3104", {"start": v(21.5, -22.43) * mm, "end": v(21.56, -22.47) * mm});
            skLineSegment(sketch, "E3105", {"start": v(21.56, -22.47) * mm, "end": v(21.62, -22.5) * mm});
            skLineSegment(sketch, "E3106", {"start": v(21.62, -22.5) * mm, "end": v(21.67, -22.55) * mm});
            skLineSegment(sketch, "E3107", {"start": v(21.67, -22.55) * mm, "end": v(21.72, -22.6) * mm});
            skLineSegment(sketch, "E3108", {"start": v(21.72, -22.6) * mm, "end": v(21.77, -22.65) * mm});
            skLineSegment(sketch, "E3109", {"start": v(21.77, -22.65) * mm, "end": v(21.82, -22.7) * mm});
            skLineSegment(sketch, "E3110", {"start": v(21.82, -22.7) * mm, "end": v(21.87, -22.75) * mm});
            skLineSegment(sketch, "E3111", {"start": v(21.87, -22.75) * mm, "end": v(21.9, -22.8) * mm});
            skLineSegment(sketch, "E3112", {"start": v(21.9, -22.8) * mm, "end": v(21.95, -22.86) * mm});
            skLineSegment(sketch, "E3113", {"start": v(21.95, -22.86) * mm, "end": v(21.99, -22.92) * mm});
            skLineSegment(sketch, "E3114", {"start": v(21.99, -22.92) * mm, "end": v(22.03, -22.98) * mm});
            skLineSegment(sketch, "E3115", {"start": v(22.03, -22.98) * mm, "end": v(22.06, -23.05) * mm});
            skLineSegment(sketch, "E3116", {"start": v(22.06, -23.05) * mm, "end": v(22.1, -23.11) * mm});
            skLineSegment(sketch, "E3117", {"start": v(22.1, -23.11) * mm, "end": v(22.12, -23.18) * mm});
            skLineSegment(sketch, "E3118", {"start": v(22.12, -23.18) * mm, "end": v(22.15, -23.25) * mm});
            skLineSegment(sketch, "E3119", {"start": v(22.15, -23.25) * mm, "end": v(22.18, -23.33) * mm});
            skLineSegment(sketch, "E3120", {"start": v(22.18, -23.33) * mm, "end": v(22.2, -23.4) * mm});
            skLineSegment(sketch, "E3121", {"start": v(22.2, -23.4) * mm, "end": v(22.22, -23.48) * mm});
            skLineSegment(sketch, "E3122", {"start": v(22.22, -23.48) * mm, "end": v(22.24, -23.56) * mm});
            skLineSegment(sketch, "E3123", {"start": v(22.24, -23.56) * mm, "end": v(22.26, -23.64) * mm});
            skLineSegment(sketch, "E3124", {"start": v(22.26, -23.64) * mm, "end": v(22.27, -23.72) * mm});
            skLineSegment(sketch, "E3125", {"start": v(22.27, -23.72) * mm, "end": v(22.28, -23.8) * mm});
            skLineSegment(sketch, "E3126", {"start": v(22.28, -23.8) * mm, "end": v(22.29, -23.89) * mm});
            skLineSegment(sketch, "E3127", {"start": v(22.29, -23.89) * mm, "end": v(22.3, -23.97) * mm});
            skLineSegment(sketch, "E3128", {"start": v(22.3, -23.97) * mm, "end": v(22.3, -24.06) * mm});
            skLineSegment(sketch, "E3129", {"start": v(22.3, -24.06) * mm, "end": v(22.3, -24.15) * mm});
            skLineSegment(sketch, "E3130", {"start": v(22.3, -24.15) * mm, "end": v(22.3, -24.17) * mm});
            skLineSegment(sketch, "E3131", {"start": v(22.3, -24.17) * mm, "end": v(22.3, -24.2) * mm});
            skLineSegment(sketch, "E3132", {"start": v(22.3, -24.2) * mm, "end": v(22.3, -24.22) * mm});
            skLineSegment(sketch, "E3133", {"start": v(22.3, -24.22) * mm, "end": v(22.3, -24.24) * mm});
            skLineSegment(sketch, "E3134", {"start": v(22.3, -24.24) * mm, "end": v(22.3, -24.26) * mm});
            skLineSegment(sketch, "E3135", {"start": v(22.3, -24.26) * mm, "end": v(22.29, -24.28) * mm});
            skLineSegment(sketch, "E3136", {"start": v(22.29, -24.28) * mm, "end": v(22.28, -24.3) * mm});
            skLineSegment(sketch, "E3137", {"start": v(22.28, -24.3) * mm, "end": v(22.28, -24.33) * mm});
            skLineSegment(sketch, "E3138", {"start": v(22.28, -24.33) * mm, "end": v(22.28, -24.36) * mm});
            skLineSegment(sketch, "E3139", {"start": v(22.28, -24.36) * mm, "end": v(22.27, -24.38) * mm});
            skLineSegment(sketch, "E3140", {"start": v(22.27, -24.38) * mm, "end": v(22.26, -24.4) * mm});
            skLineSegment(sketch, "E3141", {"start": v(22.26, -24.4) * mm, "end": v(22.26, -24.43) * mm});
            skLineSegment(sketch, "E3142", {"start": v(22.26, -24.43) * mm, "end": v(22.25, -24.46) * mm});
            skLineSegment(sketch, "E3143", {"start": v(22.25, -24.46) * mm, "end": v(22.24, -24.48) * mm});
            skLineSegment(sketch, "E3144", {"start": v(22.24, -24.48) * mm, "end": v(22.24, -24.5) * mm});
            skLineSegment(sketch, "E3145", {"start": v(22.24, -24.5) * mm, "end": v(22.23, -24.53) * mm});
            skLineSegment(sketch, "E3146", {"start": v(22.23, -24.53) * mm, "end": v(22.22, -24.55) * mm});
            skLineSegment(sketch, "E3147", {"start": v(22.22, -24.55) * mm, "end": v(22.22, -24.58) * mm});
            skLineSegment(sketch, "E3148", {"start": v(22.22, -24.58) * mm, "end": v(22.2, -24.6) * mm});
            skLineSegment(sketch, "E3149", {"start": v(22.2, -24.6) * mm, "end": v(22.2, -24.62) * mm});
            skLineSegment(sketch, "E3150", {"start": v(22.2, -24.62) * mm, "end": v(22.2, -24.65) * mm});
            skLineSegment(sketch, "E3151", {"start": v(22.2, -24.65) * mm, "end": v(22.18, -24.67) * mm});
            skLineSegment(sketch, "E3152", {"start": v(22.18, -24.67) * mm, "end": v(22.18, -24.7) * mm});
            skLineSegment(sketch, "E3153", {"start": v(22.18, -24.7) * mm, "end": v(22.17, -24.72) * mm});
            skLineSegment(sketch, "E3154", {"start": v(22.17, -24.72) * mm, "end": v(22.16, -24.74) * mm});
            skLineSegment(sketch, "E3155", {"start": v(22.16, -24.74) * mm, "end": v(22.15, -24.76) * mm});
            skLineSegment(sketch, "E3156", {"start": v(22.15, -24.76) * mm, "end": v(22.14, -24.78) * mm});
            skLineSegment(sketch, "E3157", {"start": v(22.14, -24.78) * mm, "end": v(22.14, -24.8) * mm});
            skLineSegment(sketch, "E3158", {"start": v(22.14, -24.8) * mm, "end": v(22.13, -24.82) * mm});
            skLineSegment(sketch, "E3159", {"start": v(22.13, -24.82) * mm, "end": v(22.12, -24.84) * mm});
            skLineSegment(sketch, "E3160", {"start": v(22.12, -24.84) * mm, "end": v(22.11, -24.86) * mm});
            skLineSegment(sketch, "E3161", {"start": v(22.11, -24.86) * mm, "end": v(22.1, -24.88) * mm});
            skLineSegment(sketch, "E3162", {"start": v(22.1, -24.88) * mm, "end": v(22.1, -24.9) * mm});
            skLineSegment(sketch, "E3163", {"start": v(22.1, -24.9) * mm, "end": v(22.09, -24.92) * mm});
            skLineSegment(sketch, "E3164", {"start": v(22.09, -24.92) * mm, "end": v(22.08, -24.94) * mm});
            skLineSegment(sketch, "E3165", {"start": v(22.08, -24.94) * mm, "end": v(22.08, -24.95) * mm});
            skLineSegment(sketch, "E3166", {"start": v(22.08, -24.95) * mm, "end": v(22.07, -24.97) * mm});
            skLineSegment(sketch, "E3167", {"start": v(22.07, -24.97) * mm, "end": v(22.06, -24.98) * mm});
            skLineSegment(sketch, "E3168", {"start": v(22.06, -24.98) * mm, "end": v(22.06, -25) * mm});
            skLineSegment(sketch, "E3169", {"start": v(22.06, -25) * mm, "end": v(22.05, -25) * mm});
            skLineSegment(sketch, "E3170", {"start": v(22.05, -25) * mm, "end": v(22.04, -25.06) * mm});
            skLineSegment(sketch, "E3171", {"start": v(22.04, -25.06) * mm, "end": v(22.02, -25.1) * mm});
            skLineSegment(sketch, "E3172", {"start": v(22.02, -25.1) * mm, "end": v(22, -25.15) * mm});
            skLineSegment(sketch, "E3173", {"start": v(22, -25.15) * mm, "end": v(21.98, -25.2) * mm});
            skLineSegment(sketch, "E3174", {"start": v(21.98, -25.2) * mm, "end": v(21.96, -25.23) * mm});
            skLineSegment(sketch, "E3175", {"start": v(21.96, -25.23) * mm, "end": v(21.94, -25.28) * mm});
            skLineSegment(sketch, "E3176", {"start": v(21.94, -25.28) * mm, "end": v(21.91, -25.32) * mm});
            skLineSegment(sketch, "E3177", {"start": v(21.91, -25.32) * mm, "end": v(21.89, -25.37) * mm});
            skLineSegment(sketch, "E3178", {"start": v(21.89, -25.37) * mm, "end": v(21.86, -25.4) * mm});
            skLineSegment(sketch, "E3179", {"start": v(21.86, -25.4) * mm, "end": v(21.84, -25.45) * mm});
            skLineSegment(sketch, "E3180", {"start": v(21.84, -25.45) * mm, "end": v(21.8, -25.5) * mm});
            skLineSegment(sketch, "E3181", {"start": v(21.8, -25.5) * mm, "end": v(21.78, -25.53) * mm});
            skLineSegment(sketch, "E3182", {"start": v(21.78, -25.53) * mm, "end": v(21.75, -25.57) * mm});
            skLineSegment(sketch, "E3183", {"start": v(21.75, -25.57) * mm, "end": v(21.71, -25.61) * mm});
            skLineSegment(sketch, "E3184", {"start": v(21.71, -25.61) * mm, "end": v(21.68, -25.65) * mm});
            skLineSegment(sketch, "E3185", {"start": v(21.68, -25.65) * mm, "end": v(21.65, -25.68) * mm});
            skLineSegment(sketch, "E3186", {"start": v(21.65, -25.68) * mm, "end": v(21.61, -25.72) * mm});
            skLineSegment(sketch, "E3187", {"start": v(21.61, -25.72) * mm, "end": v(21.57, -25.75) * mm});
            skLineSegment(sketch, "E3188", {"start": v(21.57, -25.75) * mm, "end": v(21.54, -25.79) * mm});
            skLineSegment(sketch, "E3189", {"start": v(21.54, -25.79) * mm, "end": v(21.5, -25.82) * mm});
            skLineSegment(sketch, "E3190", {"start": v(21.5, -25.82) * mm, "end": v(21.46, -25.85) * mm});
            skLineSegment(sketch, "E3191", {"start": v(21.46, -25.85) * mm, "end": v(21.41, -25.88) * mm});
            skLineSegment(sketch, "E3192", {"start": v(21.41, -25.88) * mm, "end": v(21.37, -25.91) * mm});
            skLineSegment(sketch, "E3193", {"start": v(21.37, -25.91) * mm, "end": v(21.33, -25.94) * mm});
            skLineSegment(sketch, "E3194", {"start": v(21.33, -25.94) * mm, "end": v(21.29, -25.97) * mm});
            skLineSegment(sketch, "E3195", {"start": v(21.29, -25.97) * mm, "end": v(21.24, -26) * mm});
            skLineSegment(sketch, "E3196", {"start": v(21.24, -26) * mm, "end": v(21.2, -26.01) * mm});
            skLineSegment(sketch, "E3197", {"start": v(21.2, -26.01) * mm, "end": v(21.15, -26.04) * mm});
            skLineSegment(sketch, "E3198", {"start": v(21.15, -26.04) * mm, "end": v(21.1, -26.06) * mm});
            skLineSegment(sketch, "E3199", {"start": v(21.1, -26.06) * mm, "end": v(21.05, -26.08) * mm});
            skLineSegment(sketch, "E3200", {"start": v(21.05, -26.08) * mm, "end": v(21, -26.1) * mm});
            skLineSegment(sketch, "E3201", {"start": v(21, -26.1) * mm, "end": v(20.95, -26.11) * mm});
            skLineSegment(sketch, "E3202", {"start": v(20.95, -26.11) * mm, "end": v(20.9, -26.13) * mm});
            skLineSegment(sketch, "E3203", {"start": v(20.9, -26.13) * mm, "end": v(20.85, -26.14) * mm});
            skLineSegment(sketch, "E3204", {"start": v(20.85, -26.14) * mm, "end": v(20.8, -26.15) * mm});
            skLineSegment(sketch, "E3205", {"start": v(20.8, -26.15) * mm, "end": v(20.74, -26.16) * mm});
            skLineSegment(sketch, "E3206", {"start": v(20.74, -26.16) * mm, "end": v(20.68, -26.16) * mm});
            skLineSegment(sketch, "E3207", {"start": v(20.68, -26.16) * mm, "end": v(20.63, -26.17) * mm});
            skLineSegment(sketch, "E3208", {"start": v(20.63, -26.17) * mm, "end": v(20.57, -26.17) * mm});
            skLineSegment(sketch, "E3209", {"start": v(20.57, -26.17) * mm, "end": v(20.51, -26.17) * mm});
            skLineSegment(sketch, "E3210", {"start": v(20.51, -22.54) * mm, "end": v(20.44, -22.55) * mm});
            skLineSegment(sketch, "E3211", {"start": v(20.44, -22.55) * mm, "end": v(20.37, -22.55) * mm});
            skLineSegment(sketch, "E3212", {"start": v(20.37, -22.55) * mm, "end": v(20.3, -22.56) * mm});
            skLineSegment(sketch, "E3213", {"start": v(20.3, -22.56) * mm, "end": v(20.23, -22.57) * mm});
            skLineSegment(sketch, "E3214", {"start": v(20.23, -22.57) * mm, "end": v(20.16, -22.58) * mm});
            skLineSegment(sketch, "E3215", {"start": v(20.16, -22.58) * mm, "end": v(20.1, -22.6) * mm});
            skLineSegment(sketch, "E3216", {"start": v(20.1, -22.6) * mm, "end": v(20.03, -22.62) * mm});
            skLineSegment(sketch, "E3217", {"start": v(20.03, -22.62) * mm, "end": v(19.97, -22.64) * mm});
            skLineSegment(sketch, "E3218", {"start": v(19.97, -22.64) * mm, "end": v(19.91, -22.67) * mm});
            skLineSegment(sketch, "E3219", {"start": v(19.91, -22.67) * mm, "end": v(19.85, -22.7) * mm});
            skLineSegment(sketch, "E3220", {"start": v(19.85, -22.7) * mm, "end": v(19.8, -22.73) * mm});
            skLineSegment(sketch, "E3221", {"start": v(19.8, -22.73) * mm, "end": v(19.74, -22.76) * mm});
            skLineSegment(sketch, "E3222", {"start": v(19.74, -22.76) * mm, "end": v(19.68, -22.8) * mm});
            skLineSegment(sketch, "E3223", {"start": v(19.68, -22.8) * mm, "end": v(19.63, -22.84) * mm});
            skLineSegment(sketch, "E3224", {"start": v(19.63, -22.84) * mm, "end": v(19.58, -22.88) * mm});
            skLineSegment(sketch, "E3225", {"start": v(19.58, -22.88) * mm, "end": v(19.54, -22.93) * mm});
            skLineSegment(sketch, "E3226", {"start": v(19.54, -22.93) * mm, "end": v(19.5, -22.98) * mm});
            skLineSegment(sketch, "E3227", {"start": v(19.5, -22.98) * mm, "end": v(19.45, -23.03) * mm});
            skLineSegment(sketch, "E3228", {"start": v(19.45, -23.03) * mm, "end": v(19.41, -23.08) * mm});
            skLineSegment(sketch, "E3229", {"start": v(19.41, -23.08) * mm, "end": v(19.37, -23.14) * mm});
            skLineSegment(sketch, "E3230", {"start": v(19.37, -23.14) * mm, "end": v(19.35, -23.18) * mm});
            skLineSegment(sketch, "E3231", {"start": v(19.35, -23.18) * mm, "end": v(19.33, -23.22) * mm});
            skLineSegment(sketch, "E3232", {"start": v(19.33, -23.22) * mm, "end": v(19.3, -23.26) * mm});
            skLineSegment(sketch, "E3233", {"start": v(19.3, -23.26) * mm, "end": v(19.29, -23.3) * mm});
            skLineSegment(sketch, "E3234", {"start": v(19.29, -23.3) * mm, "end": v(19.27, -23.35) * mm});
            skLineSegment(sketch, "E3235", {"start": v(19.27, -23.35) * mm, "end": v(19.25, -23.4) * mm});
            skLineSegment(sketch, "E3236", {"start": v(19.25, -23.4) * mm, "end": v(19.23, -23.45) * mm});
            skLineSegment(sketch, "E3237", {"start": v(19.23, -23.45) * mm, "end": v(19.22, -23.5) * mm});
            skLineSegment(sketch, "E3238", {"start": v(19.22, -23.5) * mm, "end": v(19.2, -23.55) * mm});
            skLineSegment(sketch, "E3239", {"start": v(19.2, -23.55) * mm, "end": v(19.2, -23.6) * mm});
            skLineSegment(sketch, "E3240", {"start": v(19.2, -23.6) * mm, "end": v(19.18, -23.66) * mm});
            skLineSegment(sketch, "E3241", {"start": v(19.18, -23.66) * mm, "end": v(19.17, -23.71) * mm});
            skLineSegment(sketch, "E3242", {"start": v(19.17, -23.71) * mm, "end": v(19.16, -23.77) * mm});
            skLineSegment(sketch, "E3243", {"start": v(19.16, -23.77) * mm, "end": v(19.15, -23.82) * mm});
            skLineSegment(sketch, "E3244", {"start": v(19.15, -23.82) * mm, "end": v(19.14, -23.88) * mm});
            skLineSegment(sketch, "E3245", {"start": v(19.14, -23.88) * mm, "end": v(19.14, -23.93) * mm});
            skLineSegment(sketch, "E3246", {"start": v(19.14, -23.93) * mm, "end": v(19.13, -23.99) * mm});
            skLineSegment(sketch, "E3247", {"start": v(19.13, -23.99) * mm, "end": v(19.13, -24.04) * mm});
            skLineSegment(sketch, "E3248", {"start": v(19.13, -24.04) * mm, "end": v(19.13, -24.1) * mm});
            skLineSegment(sketch, "E3249", {"start": v(19.13, -24.1) * mm, "end": v(19.13, -24.15) * mm});
            skLineSegment(sketch, "E3250", {"start": v(19.13, -24.15) * mm, "end": v(19.13, -24.22) * mm});
            skLineSegment(sketch, "E3251", {"start": v(19.13, -24.22) * mm, "end": v(19.13, -24.3) * mm});
            skLineSegment(sketch, "E3252", {"start": v(19.13, -24.3) * mm, "end": v(19.14, -24.36) * mm});
            skLineSegment(sketch, "E3253", {"start": v(19.14, -24.36) * mm, "end": v(19.14, -24.43) * mm});
            skLineSegment(sketch, "E3254", {"start": v(19.14, -24.43) * mm, "end": v(19.15, -24.5) * mm});
            skLineSegment(sketch, "E3255", {"start": v(19.15, -24.5) * mm, "end": v(19.16, -24.56) * mm});
            skLineSegment(sketch, "E3256", {"start": v(19.16, -24.56) * mm, "end": v(19.17, -24.63) * mm});
            skLineSegment(sketch, "E3257", {"start": v(19.17, -24.63) * mm, "end": v(19.18, -24.69) * mm});
            skLineSegment(sketch, "E3258", {"start": v(19.18, -24.69) * mm, "end": v(19.2, -24.75) * mm});
            skLineSegment(sketch, "E3259", {"start": v(19.2, -24.75) * mm, "end": v(19.22, -24.81) * mm});
            skLineSegment(sketch, "E3260", {"start": v(19.22, -24.81) * mm, "end": v(19.23, -24.87) * mm});
            skLineSegment(sketch, "E3261", {"start": v(19.23, -24.87) * mm, "end": v(19.25, -24.93) * mm});
            skLineSegment(sketch, "E3262", {"start": v(19.25, -24.93) * mm, "end": v(19.28, -24.98) * mm});
            skLineSegment(sketch, "E3263", {"start": v(19.28, -24.98) * mm, "end": v(19.3, -25.04) * mm});
            skLineSegment(sketch, "E3264", {"start": v(19.3, -25.04) * mm, "end": v(19.32, -25.09) * mm});
            skLineSegment(sketch, "E3265", {"start": v(19.32, -25.09) * mm, "end": v(19.35, -25.14) * mm});
            skLineSegment(sketch, "E3266", {"start": v(19.35, -25.14) * mm, "end": v(19.38, -25.19) * mm});
            skLineSegment(sketch, "E3267", {"start": v(19.38, -25.19) * mm, "end": v(19.4, -25.23) * mm});
            skLineSegment(sketch, "E3268", {"start": v(19.4, -25.23) * mm, "end": v(19.44, -25.28) * mm});
            skLineSegment(sketch, "E3269", {"start": v(19.44, -25.28) * mm, "end": v(19.47, -25.32) * mm});
            skLineSegment(sketch, "E3270", {"start": v(19.47, -25.32) * mm, "end": v(19.51, -25.36) * mm});
            skLineSegment(sketch, "E3271", {"start": v(19.51, -25.36) * mm, "end": v(19.55, -25.4) * mm});
            skLineSegment(sketch, "E3272", {"start": v(19.55, -25.4) * mm, "end": v(19.6, -25.44) * mm});
            skLineSegment(sketch, "E3273", {"start": v(19.6, -25.44) * mm, "end": v(19.63, -25.48) * mm});
            skLineSegment(sketch, "E3274", {"start": v(19.63, -25.48) * mm, "end": v(19.68, -25.51) * mm});
            skLineSegment(sketch, "E3275", {"start": v(19.68, -25.51) * mm, "end": v(19.72, -25.54) * mm});
            skLineSegment(sketch, "E3276", {"start": v(19.72, -25.54) * mm, "end": v(19.77, -25.57) * mm});
            skLineSegment(sketch, "E3277", {"start": v(19.77, -25.57) * mm, "end": v(19.82, -25.6) * mm});
            skLineSegment(sketch, "E3278", {"start": v(19.82, -25.6) * mm, "end": v(19.87, -25.63) * mm});
            skLineSegment(sketch, "E3279", {"start": v(19.87, -25.63) * mm, "end": v(19.92, -25.65) * mm});
            skLineSegment(sketch, "E3280", {"start": v(19.92, -25.65) * mm, "end": v(19.97, -25.68) * mm});
            skLineSegment(sketch, "E3281", {"start": v(19.97, -25.68) * mm, "end": v(20.03, -25.7) * mm});
            skLineSegment(sketch, "E3282", {"start": v(20.03, -25.7) * mm, "end": v(20.08, -25.71) * mm});
            skLineSegment(sketch, "E3283", {"start": v(20.08, -25.71) * mm, "end": v(20.14, -25.73) * mm});
            skLineSegment(sketch, "E3284", {"start": v(20.14, -25.73) * mm, "end": v(20.2, -25.74) * mm});
            skLineSegment(sketch, "E3285", {"start": v(20.2, -25.74) * mm, "end": v(20.26, -25.75) * mm});
            skLineSegment(sketch, "E3286", {"start": v(20.26, -25.75) * mm, "end": v(20.32, -25.76) * mm});
            skLineSegment(sketch, "E3287", {"start": v(20.32, -25.76) * mm, "end": v(20.38, -25.77) * mm});
            skLineSegment(sketch, "E3288", {"start": v(20.38, -25.77) * mm, "end": v(20.45, -25.77) * mm});
            skLineSegment(sketch, "E3289", {"start": v(20.45, -25.77) * mm, "end": v(20.51, -25.77) * mm});
            skLineSegment(sketch, "E3290", {"start": v(20.51, -25.77) * mm, "end": v(20.57, -25.77) * mm});
            skLineSegment(sketch, "E3291", {"start": v(20.57, -25.77) * mm, "end": v(20.63, -25.77) * mm});
            skLineSegment(sketch, "E3292", {"start": v(20.63, -25.77) * mm, "end": v(20.7, -25.76) * mm});
            skLineSegment(sketch, "E3293", {"start": v(20.7, -25.76) * mm, "end": v(20.75, -25.75) * mm});
            skLineSegment(sketch, "E3294", {"start": v(20.75, -25.75) * mm, "end": v(20.8, -25.74) * mm});
            skLineSegment(sketch, "E3295", {"start": v(20.8, -25.74) * mm, "end": v(20.87, -25.73) * mm});
            skLineSegment(sketch, "E3296", {"start": v(20.87, -25.73) * mm, "end": v(20.92, -25.71) * mm});
            skLineSegment(sketch, "E3297", {"start": v(20.92, -25.71) * mm, "end": v(20.97, -25.7) * mm});
            skLineSegment(sketch, "E3298", {"start": v(20.97, -25.7) * mm, "end": v(21.03, -25.67) * mm});
            skLineSegment(sketch, "E3299", {"start": v(21.03, -25.67) * mm, "end": v(21.08, -25.65) * mm});
            skLineSegment(sketch, "E3300", {"start": v(21.08, -25.65) * mm, "end": v(21.13, -25.63) * mm});
            skLineSegment(sketch, "E3301", {"start": v(21.13, -25.63) * mm, "end": v(21.18, -25.6) * mm});
            skLineSegment(sketch, "E3302", {"start": v(21.18, -25.6) * mm, "end": v(21.23, -25.57) * mm});
            skLineSegment(sketch, "E3303", {"start": v(21.23, -25.57) * mm, "end": v(21.27, -25.54) * mm});
            skLineSegment(sketch, "E3304", {"start": v(21.27, -25.54) * mm, "end": v(21.32, -25.5) * mm});
            skLineSegment(sketch, "E3305", {"start": v(21.32, -25.5) * mm, "end": v(21.36, -25.47) * mm});
            skLineSegment(sketch, "E3306", {"start": v(21.36, -25.47) * mm, "end": v(21.4, -25.44) * mm});
            skLineSegment(sketch, "E3307", {"start": v(21.4, -25.44) * mm, "end": v(21.44, -25.4) * mm});
            skLineSegment(sketch, "E3308", {"start": v(21.44, -25.4) * mm, "end": v(21.48, -25.36) * mm});
            skLineSegment(sketch, "E3309", {"start": v(21.48, -25.36) * mm, "end": v(21.52, -25.32) * mm});
            skLineSegment(sketch, "E3310", {"start": v(21.52, -25.32) * mm, "end": v(21.55, -25.27) * mm});
            skLineSegment(sketch, "E3311", {"start": v(21.55, -25.27) * mm, "end": v(21.59, -25.23) * mm});
            skLineSegment(sketch, "E3312", {"start": v(21.59, -25.23) * mm, "end": v(21.62, -25.18) * mm});
            skLineSegment(sketch, "E3313", {"start": v(21.62, -25.18) * mm, "end": v(21.65, -25.13) * mm});
            skLineSegment(sketch, "E3314", {"start": v(21.65, -25.13) * mm, "end": v(21.68, -25.08) * mm});
            skLineSegment(sketch, "E3315", {"start": v(21.68, -25.08) * mm, "end": v(21.7, -25.03) * mm});
            skLineSegment(sketch, "E3316", {"start": v(21.7, -25.03) * mm, "end": v(21.73, -24.97) * mm});
            skLineSegment(sketch, "E3317", {"start": v(21.73, -24.97) * mm, "end": v(21.76, -24.92) * mm});
            skLineSegment(sketch, "E3318", {"start": v(21.76, -24.92) * mm, "end": v(21.78, -24.86) * mm});
            skLineSegment(sketch, "E3319", {"start": v(21.78, -24.86) * mm, "end": v(21.8, -24.8) * mm});
            skLineSegment(sketch, "E3320", {"start": v(21.8, -24.8) * mm, "end": v(21.82, -24.74) * mm});
            skLineSegment(sketch, "E3321", {"start": v(21.82, -24.74) * mm, "end": v(21.83, -24.68) * mm});
            skLineSegment(sketch, "E3322", {"start": v(21.83, -24.68) * mm, "end": v(21.85, -24.62) * mm});
            skLineSegment(sketch, "E3323", {"start": v(21.85, -24.62) * mm, "end": v(21.86, -24.56) * mm});
            skLineSegment(sketch, "E3324", {"start": v(21.86, -24.56) * mm, "end": v(21.87, -24.5) * mm});
            skLineSegment(sketch, "E3325", {"start": v(21.87, -24.5) * mm, "end": v(21.88, -24.43) * mm});
            skLineSegment(sketch, "E3326", {"start": v(21.88, -24.43) * mm, "end": v(21.89, -24.36) * mm});
            skLineSegment(sketch, "E3327", {"start": v(21.89, -24.36) * mm, "end": v(21.9, -24.3) * mm});
            skLineSegment(sketch, "E3328", {"start": v(21.9, -24.3) * mm, "end": v(21.9, -24.22) * mm});
            skLineSegment(sketch, "E3329", {"start": v(21.9, -24.22) * mm, "end": v(21.9, -24.15) * mm});
            skLineSegment(sketch, "E3330", {"start": v(21.9, -24.15) * mm, "end": v(21.9, -24.08) * mm});
            skLineSegment(sketch, "E3331", {"start": v(21.9, -24.08) * mm, "end": v(21.9, -24) * mm});
            skLineSegment(sketch, "E3332", {"start": v(21.9, -24) * mm, "end": v(21.89, -23.94) * mm});
            skLineSegment(sketch, "E3333", {"start": v(21.89, -23.94) * mm, "end": v(21.88, -23.87) * mm});
            skLineSegment(sketch, "E3334", {"start": v(21.88, -23.87) * mm, "end": v(21.88, -23.8) * mm});
            skLineSegment(sketch, "E3335", {"start": v(21.88, -23.8) * mm, "end": v(21.87, -23.74) * mm});
            skLineSegment(sketch, "E3336", {"start": v(21.87, -23.74) * mm, "end": v(21.85, -23.67) * mm});
            skLineSegment(sketch, "E3337", {"start": v(21.85, -23.67) * mm, "end": v(21.84, -23.61) * mm});
            skLineSegment(sketch, "E3338", {"start": v(21.84, -23.61) * mm, "end": v(21.82, -23.55) * mm});
            skLineSegment(sketch, "E3339", {"start": v(21.82, -23.55) * mm, "end": v(21.8, -23.5) * mm});
            skLineSegment(sketch, "E3340", {"start": v(21.8, -23.5) * mm, "end": v(21.79, -23.43) * mm});
            skLineSegment(sketch, "E3341", {"start": v(21.79, -23.43) * mm, "end": v(21.77, -23.38) * mm});
            skLineSegment(sketch, "E3342", {"start": v(21.77, -23.38) * mm, "end": v(21.75, -23.32) * mm});
            skLineSegment(sketch, "E3343", {"start": v(21.75, -23.32) * mm, "end": v(21.72, -23.27) * mm});
            skLineSegment(sketch, "E3344", {"start": v(21.72, -23.27) * mm, "end": v(21.7, -23.22) * mm});
            skLineSegment(sketch, "E3345", {"start": v(21.7, -23.22) * mm, "end": v(21.67, -23.17) * mm});
            skLineSegment(sketch, "E3346", {"start": v(21.67, -23.17) * mm, "end": v(21.64, -23.12) * mm});
            skLineSegment(sketch, "E3347", {"start": v(21.64, -23.12) * mm, "end": v(21.6, -23.07) * mm});
            skLineSegment(sketch, "E3348", {"start": v(21.6, -23.07) * mm, "end": v(21.58, -23.03) * mm});
            skLineSegment(sketch, "E3349", {"start": v(21.58, -23.03) * mm, "end": v(21.54, -22.99) * mm});
            skLineSegment(sketch, "E3350", {"start": v(21.54, -22.99) * mm, "end": v(21.5, -22.95) * mm});
            skLineSegment(sketch, "E3351", {"start": v(21.5, -22.95) * mm, "end": v(21.47, -22.9) * mm});
            skLineSegment(sketch, "E3352", {"start": v(21.47, -22.9) * mm, "end": v(21.43, -22.87) * mm});
            skLineSegment(sketch, "E3353", {"start": v(21.43, -22.87) * mm, "end": v(21.39, -22.84) * mm});
            skLineSegment(sketch, "E3354", {"start": v(21.39, -22.84) * mm, "end": v(21.35, -22.8) * mm});
            skLineSegment(sketch, "E3355", {"start": v(21.35, -22.8) * mm, "end": v(21.3, -22.77) * mm});
            skLineSegment(sketch, "E3356", {"start": v(21.3, -22.77) * mm, "end": v(21.25, -22.74) * mm});
            skLineSegment(sketch, "E3357", {"start": v(21.25, -22.74) * mm, "end": v(21.2, -22.71) * mm});
            skLineSegment(sketch, "E3358", {"start": v(21.2, -22.71) * mm, "end": v(21.16, -22.69) * mm});
            skLineSegment(sketch, "E3359", {"start": v(21.16, -22.69) * mm, "end": v(21.1, -22.66) * mm});
            skLineSegment(sketch, "E3360", {"start": v(21.1, -22.66) * mm, "end": v(21.05, -22.64) * mm});
            skLineSegment(sketch, "E3361", {"start": v(21.05, -22.64) * mm, "end": v(21, -22.62) * mm});
            skLineSegment(sketch, "E3362", {"start": v(21, -22.62) * mm, "end": v(20.94, -22.6) * mm});
            skLineSegment(sketch, "E3363", {"start": v(20.94, -22.6) * mm, "end": v(20.88, -22.59) * mm});
            skLineSegment(sketch, "E3364", {"start": v(20.88, -22.59) * mm, "end": v(20.82, -22.57) * mm});
            skLineSegment(sketch, "E3365", {"start": v(20.82, -22.57) * mm, "end": v(20.76, -22.56) * mm});
            skLineSegment(sketch, "E3366", {"start": v(20.76, -22.56) * mm, "end": v(20.7, -22.56) * mm});
            skLineSegment(sketch, "E3367", {"start": v(20.7, -22.56) * mm, "end": v(20.64, -22.55) * mm});
            skLineSegment(sketch, "E3368", {"start": v(20.64, -22.55) * mm, "end": v(20.58, -22.55) * mm});
            skLineSegment(sketch, "E3369", {"start": v(20.58, -22.55) * mm, "end": v(20.51, -22.54) * mm});
            skLineSegment(sketch, "E3370", {"start": v(-0.12, -49.24) * mm, "end": v(-0.2, -49.23) * mm});
            skLineSegment(sketch, "E3371", {"start": v(-0.2, -49.23) * mm, "end": v(-0.27, -49.23) * mm});
            skLineSegment(sketch, "E3372", {"start": v(-0.27, -49.23) * mm, "end": v(-0.35, -49.22) * mm});
            skLineSegment(sketch, "E3373", {"start": v(-0.35, -49.22) * mm, "end": v(-0.42, -49.21) * mm});
            skLineSegment(sketch, "E3374", {"start": v(-0.42, -49.21) * mm, "end": v(-0.5, -49.2) * mm});
            skLineSegment(sketch, "E3375", {"start": v(-0.5, -49.2) * mm, "end": v(-0.57, -49.18) * mm});
            skLineSegment(sketch, "E3376", {"start": v(-0.57, -49.18) * mm, "end": v(-0.64, -49.16) * mm});
            skLineSegment(sketch, "E3377", {"start": v(-0.64, -49.16) * mm, "end": v(-0.7, -49.14) * mm});
            skLineSegment(sketch, "E3378", {"start": v(-0.7, -49.14) * mm, "end": v(-0.78, -49.12) * mm});
            skLineSegment(sketch, "E3379", {"start": v(-0.78, -49.12) * mm, "end": v(-0.84, -49.1) * mm});
            skLineSegment(sketch, "E3380", {"start": v(-0.84, -49.1) * mm, "end": v(-0.9, -49.06) * mm});
            skLineSegment(sketch, "E3381", {"start": v(-0.9, -49.06) * mm, "end": v(-0.97, -49.03) * mm});
            skLineSegment(sketch, "E3382", {"start": v(-0.97, -49.03) * mm, "end": v(-1.03, -49) * mm});
            skLineSegment(sketch, "E3383", {"start": v(-1.03, -49) * mm, "end": v(-1.1, -48.95) * mm});
            skLineSegment(sketch, "E3384", {"start": v(-1.1, -48.95) * mm, "end": v(-1.15, -48.91) * mm});
            skLineSegment(sketch, "E3385", {"start": v(-1.15, -48.91) * mm, "end": v(-1.2, -48.87) * mm});
            skLineSegment(sketch, "E3386", {"start": v(-1.2, -48.87) * mm, "end": v(-1.26, -48.82) * mm});
            skLineSegment(sketch, "E3387", {"start": v(-1.26, -48.82) * mm, "end": v(-1.31, -48.77) * mm});
            skLineSegment(sketch, "E3388", {"start": v(-1.31, -48.77) * mm, "end": v(-1.36, -48.72) * mm});
            skLineSegment(sketch, "E3389", {"start": v(-1.36, -48.72) * mm, "end": v(-1.41, -48.67) * mm});
            skLineSegment(sketch, "E3390", {"start": v(-1.41, -48.67) * mm, "end": v(-1.46, -48.61) * mm});
            skLineSegment(sketch, "E3391", {"start": v(-1.46, -48.61) * mm, "end": v(-1.5, -48.56) * mm});
            skLineSegment(sketch, "E3392", {"start": v(-1.5, -48.56) * mm, "end": v(-1.54, -48.5) * mm});
            skLineSegment(sketch, "E3393", {"start": v(-1.54, -48.5) * mm, "end": v(-1.58, -48.44) * mm});
            skLineSegment(sketch, "E3394", {"start": v(-1.58, -48.44) * mm, "end": v(-1.61, -48.38) * mm});
            skLineSegment(sketch, "E3395", {"start": v(-1.61, -48.38) * mm, "end": v(-1.64, -48.32) * mm});
            skLineSegment(sketch, "E3396", {"start": v(-1.64, -48.32) * mm, "end": v(-1.68, -48.25) * mm});
            skLineSegment(sketch, "E3397", {"start": v(-1.68, -48.25) * mm, "end": v(-1.7, -48.18) * mm});
            skLineSegment(sketch, "E3398", {"start": v(-1.7, -48.18) * mm, "end": v(-1.73, -48.12) * mm});
            skLineSegment(sketch, "E3399", {"start": v(-1.73, -48.12) * mm, "end": v(-1.75, -48.05) * mm});
            skLineSegment(sketch, "E3400", {"start": v(-1.75, -48.05) * mm, "end": v(-1.78, -47.98) * mm});
            skLineSegment(sketch, "E3401", {"start": v(-1.78, -47.98) * mm, "end": v(-1.8, -47.9) * mm});
            skLineSegment(sketch, "E3402", {"start": v(-1.8, -47.9) * mm, "end": v(-1.81, -47.83) * mm});
            skLineSegment(sketch, "E3403", {"start": v(-1.81, -47.83) * mm, "end": v(-1.83, -47.75) * mm});
            skLineSegment(sketch, "E3404", {"start": v(-1.83, -47.75) * mm, "end": v(-1.84, -47.68) * mm});
            skLineSegment(sketch, "E3405", {"start": v(-1.84, -47.68) * mm, "end": v(-1.85, -47.6) * mm});
            skLineSegment(sketch, "E3406", {"start": v(-1.85, -47.6) * mm, "end": v(-1.86, -47.52) * mm});
            skLineSegment(sketch, "E3407", {"start": v(-1.86, -47.52) * mm, "end": v(-1.86, -47.44) * mm});
            skLineSegment(sketch, "E3408", {"start": v(-1.86, -47.44) * mm, "end": v(-1.87, -47.36) * mm});
            skLineSegment(sketch, "E3409", {"start": v(-1.87, -47.36) * mm, "end": v(-1.87, -47.27) * mm});
            skLineSegment(sketch, "E3410", {"start": v(-1.87, -47.27) * mm, "end": v(-1.87, -44.45) * mm});
            skLineSegment(sketch, "E3411", {"start": v(-1.87, -44.45) * mm, "end": v(-1.87, -44.37) * mm});
            skLineSegment(sketch, "E3412", {"start": v(-1.87, -44.37) * mm, "end": v(-1.86, -44.29) * mm});
            skLineSegment(sketch, "E3413", {"start": v(-1.86, -44.29) * mm, "end": v(-1.86, -44.2) * mm});
            skLineSegment(sketch, "E3414", {"start": v(-1.86, -44.2) * mm, "end": v(-1.85, -44.13) * mm});
            skLineSegment(sketch, "E3415", {"start": v(-1.85, -44.13) * mm, "end": v(-1.84, -44.05) * mm});
            skLineSegment(sketch, "E3416", {"start": v(-1.84, -44.05) * mm, "end": v(-1.83, -43.97) * mm});
            skLineSegment(sketch, "E3417", {"start": v(-1.83, -43.97) * mm, "end": v(-1.81, -43.9) * mm});
            skLineSegment(sketch, "E3418", {"start": v(-1.81, -43.9) * mm, "end": v(-1.8, -43.82) * mm});
            skLineSegment(sketch, "E3419", {"start": v(-1.8, -43.82) * mm, "end": v(-1.78, -43.75) * mm});
            skLineSegment(sketch, "E3420", {"start": v(-1.78, -43.75) * mm, "end": v(-1.75, -43.68) * mm});
            skLineSegment(sketch, "E3421", {"start": v(-1.75, -43.68) * mm, "end": v(-1.73, -43.61) * mm});
            skLineSegment(sketch, "E3422", {"start": v(-1.73, -43.61) * mm, "end": v(-1.7, -43.54) * mm});
            skLineSegment(sketch, "E3423", {"start": v(-1.7, -43.54) * mm, "end": v(-1.68, -43.48) * mm});
            skLineSegment(sketch, "E3424", {"start": v(-1.68, -43.48) * mm, "end": v(-1.64, -43.41) * mm});
            skLineSegment(sketch, "E3425", {"start": v(-1.64, -43.41) * mm, "end": v(-1.61, -43.35) * mm});
            skLineSegment(sketch, "E3426", {"start": v(-1.61, -43.35) * mm, "end": v(-1.58, -43.29) * mm});
            skLineSegment(sketch, "E3427", {"start": v(-1.58, -43.29) * mm, "end": v(-1.54, -43.23) * mm});
            skLineSegment(sketch, "E3428", {"start": v(-1.54, -43.23) * mm, "end": v(-1.5, -43.17) * mm});
            skLineSegment(sketch, "E3429", {"start": v(-1.5, -43.17) * mm, "end": v(-1.46, -43.12) * mm});
            skLineSegment(sketch, "E3430", {"start": v(-1.46, -43.12) * mm, "end": v(-1.41, -43.06) * mm});
            skLineSegment(sketch, "E3431", {"start": v(-1.41, -43.06) * mm, "end": v(-1.36, -43) * mm});
            skLineSegment(sketch, "E3432", {"start": v(-1.36, -43) * mm, "end": v(-1.31, -42.96) * mm});
            skLineSegment(sketch, "E3433", {"start": v(-1.31, -42.96) * mm, "end": v(-1.26, -42.9) * mm});
            skLineSegment(sketch, "E3434", {"start": v(-1.26, -42.9) * mm, "end": v(-1.2, -42.86) * mm});
            skLineSegment(sketch, "E3435", {"start": v(-1.2, -42.86) * mm, "end": v(-1.15, -42.82) * mm});
            skLineSegment(sketch, "E3436", {"start": v(-1.15, -42.82) * mm, "end": v(-1.1, -42.78) * mm});
            skLineSegment(sketch, "E3437", {"start": v(-1.1, -42.78) * mm, "end": v(-1.03, -42.74) * mm});
            skLineSegment(sketch, "E3438", {"start": v(-1.03, -42.74) * mm, "end": v(-0.97, -42.7) * mm});
            skLineSegment(sketch, "E3439", {"start": v(-0.97, -42.7) * mm, "end": v(-0.9, -42.67) * mm});
            skLineSegment(sketch, "E3440", {"start": v(-0.9, -42.67) * mm, "end": v(-0.84, -42.64) * mm});
            skLineSegment(sketch, "E3441", {"start": v(-0.84, -42.64) * mm, "end": v(-0.78, -42.61) * mm});
            skLineSegment(sketch, "E3442", {"start": v(-0.78, -42.61) * mm, "end": v(-0.7, -42.59) * mm});
            skLineSegment(sketch, "E3443", {"start": v(-0.7, -42.59) * mm, "end": v(-0.64, -42.56) * mm});
            skLineSegment(sketch, "E3444", {"start": v(-0.64, -42.56) * mm, "end": v(-0.57, -42.54) * mm});
            skLineSegment(sketch, "E3445", {"start": v(-0.57, -42.54) * mm, "end": v(-0.5, -42.53) * mm});
            skLineSegment(sketch, "E3446", {"start": v(-0.5, -42.53) * mm, "end": v(-0.42, -42.52) * mm});
            skLineSegment(sketch, "E3447", {"start": v(-0.42, -42.52) * mm, "end": v(-0.35, -42.5) * mm});
            skLineSegment(sketch, "E3448", {"start": v(-0.35, -42.5) * mm, "end": v(-0.27, -42.5) * mm});
            skLineSegment(sketch, "E3449", {"start": v(-0.27, -42.5) * mm, "end": v(-0.2, -42.5) * mm});
            skLineSegment(sketch, "E3450", {"start": v(-0.2, -42.5) * mm, "end": v(-0.12, -42.5) * mm});
            skLineSegment(sketch, "E3451", {"start": v(-0.12, -42.5) * mm, "end": v(-0.04, -42.5) * mm});
            skLineSegment(sketch, "E3452", {"start": v(-0.04, -42.5) * mm, "end": v(0.04, -42.5) * mm});
            skLineSegment(sketch, "E3453", {"start": v(0.04, -42.5) * mm, "end": v(0.12, -42.5) * mm});
            skLineSegment(sketch, "E3454", {"start": v(0.12, -42.5) * mm, "end": v(0.2, -42.52) * mm});
            skLineSegment(sketch, "E3455", {"start": v(0.2, -42.52) * mm, "end": v(0.26, -42.53) * mm});
            skLineSegment(sketch, "E3456", {"start": v(0.26, -42.53) * mm, "end": v(0.34, -42.54) * mm});
            skLineSegment(sketch, "E3457", {"start": v(0.34, -42.54) * mm, "end": v(0.4, -42.56) * mm});
            skLineSegment(sketch, "E3458", {"start": v(0.4, -42.56) * mm, "end": v(0.47, -42.59) * mm});
            skLineSegment(sketch, "E3459", {"start": v(0.47, -42.59) * mm, "end": v(0.54, -42.61) * mm});
            skLineSegment(sketch, "E3460", {"start": v(0.54, -42.61) * mm, "end": v(0.6, -42.64) * mm});
            skLineSegment(sketch, "E3461", {"start": v(0.6, -42.64) * mm, "end": v(0.67, -42.67) * mm});
            skLineSegment(sketch, "E3462", {"start": v(0.67, -42.67) * mm, "end": v(0.73, -42.7) * mm});
            skLineSegment(sketch, "E3463", {"start": v(0.73, -42.7) * mm, "end": v(0.8, -42.74) * mm});
            skLineSegment(sketch, "E3464", {"start": v(0.8, -42.74) * mm, "end": v(0.85, -42.78) * mm});
            skLineSegment(sketch, "E3465", {"start": v(0.85, -42.78) * mm, "end": v(0.91, -42.82) * mm});
            skLineSegment(sketch, "E3466", {"start": v(0.91, -42.82) * mm, "end": v(0.97, -42.86) * mm});
            skLineSegment(sketch, "E3467", {"start": v(0.97, -42.86) * mm, "end": v(1.02, -42.9) * mm});
            skLineSegment(sketch, "E3468", {"start": v(1.02, -42.9) * mm, "end": v(1.08, -42.96) * mm});
            skLineSegment(sketch, "E3469", {"start": v(1.08, -42.96) * mm, "end": v(1.13, -43) * mm});
            skLineSegment(sketch, "E3470", {"start": v(1.13, -43) * mm, "end": v(1.18, -43.06) * mm});
            skLineSegment(sketch, "E3471", {"start": v(1.18, -43.06) * mm, "end": v(1.22, -43.12) * mm});
            skLineSegment(sketch, "E3472", {"start": v(1.22, -43.12) * mm, "end": v(1.27, -43.17) * mm});
            skLineSegment(sketch, "E3473", {"start": v(1.27, -43.17) * mm, "end": v(1.3, -43.23) * mm});
            skLineSegment(sketch, "E3474", {"start": v(1.3, -43.23) * mm, "end": v(1.34, -43.29) * mm});
            skLineSegment(sketch, "E3475", {"start": v(1.34, -43.29) * mm, "end": v(1.38, -43.35) * mm});
            skLineSegment(sketch, "E3476", {"start": v(1.38, -43.35) * mm, "end": v(1.41, -43.41) * mm});
            skLineSegment(sketch, "E3477", {"start": v(1.41, -43.41) * mm, "end": v(1.44, -43.48) * mm});
            skLineSegment(sketch, "E3478", {"start": v(1.44, -43.48) * mm, "end": v(1.47, -43.54) * mm});
            skLineSegment(sketch, "E3479", {"start": v(1.47, -43.54) * mm, "end": v(1.5, -43.61) * mm});
            skLineSegment(sketch, "E3480", {"start": v(1.5, -43.61) * mm, "end": v(1.52, -43.68) * mm});
            skLineSegment(sketch, "E3481", {"start": v(1.52, -43.68) * mm, "end": v(1.54, -43.75) * mm});
            skLineSegment(sketch, "E3482", {"start": v(1.54, -43.75) * mm, "end": v(1.56, -43.82) * mm});
            skLineSegment(sketch, "E3483", {"start": v(1.56, -43.82) * mm, "end": v(1.58, -43.9) * mm});
            skLineSegment(sketch, "E3484", {"start": v(1.58, -43.9) * mm, "end": v(1.6, -43.97) * mm});
            skLineSegment(sketch, "E3485", {"start": v(1.6, -43.97) * mm, "end": v(1.6, -44.05) * mm});
            skLineSegment(sketch, "E3486", {"start": v(1.6, -44.05) * mm, "end": v(1.62, -44.13) * mm});
            skLineSegment(sketch, "E3487", {"start": v(1.62, -44.13) * mm, "end": v(1.63, -44.2) * mm});
            skLineSegment(sketch, "E3488", {"start": v(1.63, -44.2) * mm, "end": v(1.63, -44.29) * mm});
            skLineSegment(sketch, "E3489", {"start": v(1.63, -44.29) * mm, "end": v(1.63, -44.37) * mm});
            skLineSegment(sketch, "E3490", {"start": v(1.63, -44.37) * mm, "end": v(1.64, -44.45) * mm});
            skLineSegment(sketch, "E3491", {"start": v(1.64, -44.45) * mm, "end": v(1.64, -47.27) * mm});
            skLineSegment(sketch, "E3492", {"start": v(1.64, -47.27) * mm, "end": v(1.63, -47.36) * mm});
            skLineSegment(sketch, "E3493", {"start": v(1.63, -47.36) * mm, "end": v(1.63, -47.44) * mm});
            skLineSegment(sketch, "E3494", {"start": v(1.63, -47.44) * mm, "end": v(1.63, -47.52) * mm});
            skLineSegment(sketch, "E3495", {"start": v(1.63, -47.52) * mm, "end": v(1.62, -47.6) * mm});
            skLineSegment(sketch, "E3496", {"start": v(1.62, -47.6) * mm, "end": v(1.6, -47.68) * mm});
            skLineSegment(sketch, "E3497", {"start": v(1.6, -47.68) * mm, "end": v(1.6, -47.75) * mm});
            skLineSegment(sketch, "E3498", {"start": v(1.6, -47.75) * mm, "end": v(1.58, -47.83) * mm});
            skLineSegment(sketch, "E3499", {"start": v(1.58, -47.83) * mm, "end": v(1.56, -47.9) * mm});
            skLineSegment(sketch, "E3500", {"start": v(1.56, -47.9) * mm, "end": v(1.54, -47.98) * mm});
            skLineSegment(sketch, "E3501", {"start": v(1.54, -47.98) * mm, "end": v(1.52, -48.05) * mm});
            skLineSegment(sketch, "E3502", {"start": v(1.52, -48.05) * mm, "end": v(1.5, -48.12) * mm});
            skLineSegment(sketch, "E3503", {"start": v(1.5, -48.12) * mm, "end": v(1.47, -48.18) * mm});
            skLineSegment(sketch, "E3504", {"start": v(1.47, -48.18) * mm, "end": v(1.44, -48.25) * mm});
            skLineSegment(sketch, "E3505", {"start": v(1.44, -48.25) * mm, "end": v(1.41, -48.32) * mm});
            skLineSegment(sketch, "E3506", {"start": v(1.41, -48.32) * mm, "end": v(1.38, -48.38) * mm});
            skLineSegment(sketch, "E3507", {"start": v(1.38, -48.38) * mm, "end": v(1.34, -48.44) * mm});
            skLineSegment(sketch, "E3508", {"start": v(1.34, -48.44) * mm, "end": v(1.3, -48.5) * mm});
            skLineSegment(sketch, "E3509", {"start": v(1.3, -48.5) * mm, "end": v(1.27, -48.56) * mm});
            skLineSegment(sketch, "E3510", {"start": v(1.27, -48.56) * mm, "end": v(1.22, -48.61) * mm});
            skLineSegment(sketch, "E3511", {"start": v(1.22, -48.61) * mm, "end": v(1.18, -48.67) * mm});
            skLineSegment(sketch, "E3512", {"start": v(1.18, -48.67) * mm, "end": v(1.13, -48.72) * mm});
            skLineSegment(sketch, "E3513", {"start": v(1.13, -48.72) * mm, "end": v(1.08, -48.77) * mm});
            skLineSegment(sketch, "E3514", {"start": v(1.08, -48.77) * mm, "end": v(1.02, -48.82) * mm});
            skLineSegment(sketch, "E3515", {"start": v(1.02, -48.82) * mm, "end": v(0.97, -48.87) * mm});
            skLineSegment(sketch, "E3516", {"start": v(0.97, -48.87) * mm, "end": v(0.91, -48.91) * mm});
            skLineSegment(sketch, "E3517", {"start": v(0.91, -48.91) * mm, "end": v(0.85, -48.95) * mm});
            skLineSegment(sketch, "E3518", {"start": v(0.85, -48.95) * mm, "end": v(0.8, -49) * mm});
            skLineSegment(sketch, "E3519", {"start": v(0.8, -49) * mm, "end": v(0.73, -49.03) * mm});
            skLineSegment(sketch, "E3520", {"start": v(0.73, -49.03) * mm, "end": v(0.67, -49.06) * mm});
            skLineSegment(sketch, "E3521", {"start": v(0.67, -49.06) * mm, "end": v(0.6, -49.1) * mm});
            skLineSegment(sketch, "E3522", {"start": v(0.6, -49.1) * mm, "end": v(0.54, -49.12) * mm});
            skLineSegment(sketch, "E3523", {"start": v(0.54, -49.12) * mm, "end": v(0.47, -49.14) * mm});
            skLineSegment(sketch, "E3524", {"start": v(0.47, -49.14) * mm, "end": v(0.4, -49.16) * mm});
            skLineSegment(sketch, "E3525", {"start": v(0.4, -49.16) * mm, "end": v(0.34, -49.18) * mm});
            skLineSegment(sketch, "E3526", {"start": v(0.34, -49.18) * mm, "end": v(0.26, -49.2) * mm});
            skLineSegment(sketch, "E3527", {"start": v(0.26, -49.2) * mm, "end": v(0.2, -49.21) * mm});
            skLineSegment(sketch, "E3528", {"start": v(0.2, -49.21) * mm, "end": v(0.12, -49.22) * mm});
            skLineSegment(sketch, "E3529", {"start": v(0.12, -49.22) * mm, "end": v(0.04, -49.23) * mm});
            skLineSegment(sketch, "E3530", {"start": v(0.04, -49.23) * mm, "end": v(-0.04, -49.23) * mm});
            skLineSegment(sketch, "E3531", {"start": v(-0.04, -49.23) * mm, "end": v(-0.12, -49.24) * mm});
            skLineSegment(sketch, "E3532", {"start": v(-0.12, -42.9) * mm, "end": v(-0.18, -42.9) * mm});
            skLineSegment(sketch, "E3533", {"start": v(-0.18, -42.9) * mm, "end": v(-0.24, -42.9) * mm});
            skLineSegment(sketch, "E3534", {"start": v(-0.24, -42.9) * mm, "end": v(-0.3, -42.9) * mm});
            skLineSegment(sketch, "E3535", {"start": v(-0.3, -42.9) * mm, "end": v(-0.35, -42.91) * mm});
            skLineSegment(sketch, "E3536", {"start": v(-0.35, -42.91) * mm, "end": v(-0.4, -42.92) * mm});
            skLineSegment(sketch, "E3537", {"start": v(-0.4, -42.92) * mm, "end": v(-0.46, -42.93) * mm});
            skLineSegment(sketch, "E3538", {"start": v(-0.46, -42.93) * mm, "end": v(-0.52, -42.95) * mm});
            skLineSegment(sketch, "E3539", {"start": v(-0.52, -42.95) * mm, "end": v(-0.57, -42.96) * mm});
            skLineSegment(sketch, "E3540", {"start": v(-0.57, -42.96) * mm, "end": v(-0.62, -42.98) * mm});
            skLineSegment(sketch, "E3541", {"start": v(-0.62, -42.98) * mm, "end": v(-0.67, -43) * mm});
            skLineSegment(sketch, "E3542", {"start": v(-0.67, -43) * mm, "end": v(-0.72, -43.03) * mm});
            skLineSegment(sketch, "E3543", {"start": v(-0.72, -43.03) * mm, "end": v(-0.77, -43.05) * mm});
            skLineSegment(sketch, "E3544", {"start": v(-0.77, -43.05) * mm, "end": v(-0.81, -43.08) * mm});
            skLineSegment(sketch, "E3545", {"start": v(-0.81, -43.08) * mm, "end": v(-0.86, -43.1) * mm});
            skLineSegment(sketch, "E3546", {"start": v(-0.86, -43.1) * mm, "end": v(-0.9, -43.14) * mm});
            skLineSegment(sketch, "E3547", {"start": v(-0.9, -43.14) * mm, "end": v(-0.94, -43.17) * mm});
            skLineSegment(sketch, "E3548", {"start": v(-0.94, -43.17) * mm, "end": v(-0.99, -43.2) * mm});
            skLineSegment(sketch, "E3549", {"start": v(-0.99, -43.2) * mm, "end": v(-1.02, -43.24) * mm});
            skLineSegment(sketch, "E3550", {"start": v(-1.02, -43.24) * mm, "end": v(-1.06, -43.28) * mm});
            skLineSegment(sketch, "E3551", {"start": v(-1.06, -43.28) * mm, "end": v(-1.1, -43.32) * mm});
            skLineSegment(sketch, "E3552", {"start": v(-1.1, -43.32) * mm, "end": v(-1.13, -43.36) * mm});
            skLineSegment(sketch, "E3553", {"start": v(-1.13, -43.36) * mm, "end": v(-1.17, -43.4) * mm});
            skLineSegment(sketch, "E3554", {"start": v(-1.17, -43.4) * mm, "end": v(-1.2, -43.45) * mm});
            skLineSegment(sketch, "E3555", {"start": v(-1.2, -43.45) * mm, "end": v(-1.23, -43.5) * mm});
            skLineSegment(sketch, "E3556", {"start": v(-1.23, -43.5) * mm, "end": v(-1.26, -43.54) * mm});
            skLineSegment(sketch, "E3557", {"start": v(-1.26, -43.54) * mm, "end": v(-1.28, -43.6) * mm});
            skLineSegment(sketch, "E3558", {"start": v(-1.28, -43.6) * mm, "end": v(-1.3, -43.64) * mm});
            skLineSegment(sketch, "E3559", {"start": v(-1.3, -43.64) * mm, "end": v(-1.33, -43.7) * mm});
            skLineSegment(sketch, "E3560", {"start": v(-1.33, -43.7) * mm, "end": v(-1.35, -43.75) * mm});
            skLineSegment(sketch, "E3561", {"start": v(-1.35, -43.75) * mm, "end": v(-1.37, -43.81) * mm});
            skLineSegment(sketch, "E3562", {"start": v(-1.37, -43.81) * mm, "end": v(-1.39, -43.87) * mm});
            skLineSegment(sketch, "E3563", {"start": v(-1.39, -43.87) * mm, "end": v(-1.4, -43.93) * mm});
            skLineSegment(sketch, "E3564", {"start": v(-1.4, -43.93) * mm, "end": v(-1.42, -43.99) * mm});
            skLineSegment(sketch, "E3565", {"start": v(-1.42, -43.99) * mm, "end": v(-1.43, -44.05) * mm});
            skLineSegment(sketch, "E3566", {"start": v(-1.43, -44.05) * mm, "end": v(-1.44, -44.12) * mm});
            skLineSegment(sketch, "E3567", {"start": v(-1.44, -44.12) * mm, "end": v(-1.45, -44.18) * mm});
            skLineSegment(sketch, "E3568", {"start": v(-1.45, -44.18) * mm, "end": v(-1.46, -44.25) * mm});
            skLineSegment(sketch, "E3569", {"start": v(-1.46, -44.25) * mm, "end": v(-1.46, -44.31) * mm});
            skLineSegment(sketch, "E3570", {"start": v(-1.46, -44.31) * mm, "end": v(-1.46, -44.38) * mm});
            skLineSegment(sketch, "E3571", {"start": v(-1.46, -44.38) * mm, "end": v(-1.47, -44.45) * mm});
            skLineSegment(sketch, "E3572", {"start": v(-1.47, -44.45) * mm, "end": v(-1.47, -47.27) * mm});
            skLineSegment(sketch, "E3573", {"start": v(-1.47, -47.27) * mm, "end": v(-1.46, -47.34) * mm});
            skLineSegment(sketch, "E3574", {"start": v(-1.46, -47.34) * mm, "end": v(-1.46, -47.41) * mm});
            skLineSegment(sketch, "E3575", {"start": v(-1.46, -47.41) * mm, "end": v(-1.46, -47.48) * mm});
            skLineSegment(sketch, "E3576", {"start": v(-1.46, -47.48) * mm, "end": v(-1.45, -47.55) * mm});
            skLineSegment(sketch, "E3577", {"start": v(-1.45, -47.55) * mm, "end": v(-1.44, -47.61) * mm});
            skLineSegment(sketch, "E3578", {"start": v(-1.44, -47.61) * mm, "end": v(-1.43, -47.68) * mm});
            skLineSegment(sketch, "E3579", {"start": v(-1.43, -47.68) * mm, "end": v(-1.42, -47.74) * mm});
            skLineSegment(sketch, "E3580", {"start": v(-1.42, -47.74) * mm, "end": v(-1.4, -47.8) * mm});
            skLineSegment(sketch, "E3581", {"start": v(-1.4, -47.8) * mm, "end": v(-1.39, -47.86) * mm});
            skLineSegment(sketch, "E3582", {"start": v(-1.39, -47.86) * mm, "end": v(-1.37, -47.92) * mm});
            skLineSegment(sketch, "E3583", {"start": v(-1.37, -47.92) * mm, "end": v(-1.35, -47.97) * mm});
            skLineSegment(sketch, "E3584", {"start": v(-1.35, -47.97) * mm, "end": v(-1.33, -48.03) * mm});
            skLineSegment(sketch, "E3585", {"start": v(-1.33, -48.03) * mm, "end": v(-1.3, -48.08) * mm});
            skLineSegment(sketch, "E3586", {"start": v(-1.3, -48.08) * mm, "end": v(-1.28, -48.13) * mm});
            skLineSegment(sketch, "E3587", {"start": v(-1.28, -48.13) * mm, "end": v(-1.26, -48.18) * mm});
            skLineSegment(sketch, "E3588", {"start": v(-1.26, -48.18) * mm, "end": v(-1.23, -48.23) * mm});
            skLineSegment(sketch, "E3589", {"start": v(-1.23, -48.23) * mm, "end": v(-1.2, -48.28) * mm});
            skLineSegment(sketch, "E3590", {"start": v(-1.2, -48.28) * mm, "end": v(-1.17, -48.32) * mm});
            skLineSegment(sketch, "E3591", {"start": v(-1.17, -48.32) * mm, "end": v(-1.13, -48.37) * mm});
            skLineSegment(sketch, "E3592", {"start": v(-1.13, -48.37) * mm, "end": v(-1.1, -48.4) * mm});
            skLineSegment(sketch, "E3593", {"start": v(-1.1, -48.4) * mm, "end": v(-1.06, -48.45) * mm});
            skLineSegment(sketch, "E3594", {"start": v(-1.06, -48.45) * mm, "end": v(-1.02, -48.49) * mm});
            skLineSegment(sketch, "E3595", {"start": v(-1.02, -48.49) * mm, "end": v(-0.99, -48.52) * mm});
            skLineSegment(sketch, "E3596", {"start": v(-0.99, -48.52) * mm, "end": v(-0.94, -48.56) * mm});
            skLineSegment(sketch, "E3597", {"start": v(-0.94, -48.56) * mm, "end": v(-0.9, -48.59) * mm});
            skLineSegment(sketch, "E3598", {"start": v(-0.9, -48.59) * mm, "end": v(-0.86, -48.62) * mm});
            skLineSegment(sketch, "E3599", {"start": v(-0.86, -48.62) * mm, "end": v(-0.81, -48.65) * mm});
            skLineSegment(sketch, "E3600", {"start": v(-0.81, -48.65) * mm, "end": v(-0.77, -48.68) * mm});
            skLineSegment(sketch, "E3601", {"start": v(-0.77, -48.68) * mm, "end": v(-0.72, -48.7) * mm});
            skLineSegment(sketch, "E3602", {"start": v(-0.72, -48.7) * mm, "end": v(-0.67, -48.72) * mm});
            skLineSegment(sketch, "E3603", {"start": v(-0.67, -48.72) * mm, "end": v(-0.62, -48.74) * mm});
            skLineSegment(sketch, "E3604", {"start": v(-0.62, -48.74) * mm, "end": v(-0.57, -48.76) * mm});
            skLineSegment(sketch, "E3605", {"start": v(-0.57, -48.76) * mm, "end": v(-0.52, -48.78) * mm});
            skLineSegment(sketch, "E3606", {"start": v(-0.52, -48.78) * mm, "end": v(-0.46, -48.8) * mm});
            skLineSegment(sketch, "E3607", {"start": v(-0.46, -48.8) * mm, "end": v(-0.4, -48.8) * mm});
            skLineSegment(sketch, "E3608", {"start": v(-0.4, -48.8) * mm, "end": v(-0.35, -48.82) * mm});
            skLineSegment(sketch, "E3609", {"start": v(-0.35, -48.82) * mm, "end": v(-0.3, -48.82) * mm});
            skLineSegment(sketch, "E3610", {"start": v(-0.3, -48.82) * mm, "end": v(-0.24, -48.83) * mm});
            skLineSegment(sketch, "E3611", {"start": v(-0.24, -48.83) * mm, "end": v(-0.18, -48.83) * mm});
            skLineSegment(sketch, "E3612", {"start": v(-0.18, -48.83) * mm, "end": v(-0.12, -48.83) * mm});
            skLineSegment(sketch, "E3613", {"start": v(-0.12, -48.83) * mm, "end": v(-0.06, -48.83) * mm});
            skLineSegment(sketch, "E3614", {"start": v(-0.06, -48.83) * mm, "end": v(0, -48.83) * mm});
            skLineSegment(sketch, "E3615", {"start": v(0, -48.83) * mm, "end": v(0.06, -48.82) * mm});
            skLineSegment(sketch, "E3616", {"start": v(0.06, -48.82) * mm, "end": v(0.12, -48.82) * mm});
            skLineSegment(sketch, "E3617", {"start": v(0.12, -48.82) * mm, "end": v(0.18, -48.8) * mm});
            skLineSegment(sketch, "E3618", {"start": v(0.18, -48.8) * mm, "end": v(0.23, -48.8) * mm});
            skLineSegment(sketch, "E3619", {"start": v(0.23, -48.8) * mm, "end": v(0.29, -48.78) * mm});
            skLineSegment(sketch, "E3620", {"start": v(0.29, -48.78) * mm, "end": v(0.34, -48.76) * mm});
            skLineSegment(sketch, "E3621", {"start": v(0.34, -48.76) * mm, "end": v(0.4, -48.74) * mm});
            skLineSegment(sketch, "E3622", {"start": v(0.4, -48.74) * mm, "end": v(0.44, -48.72) * mm});
            skLineSegment(sketch, "E3623", {"start": v(0.44, -48.72) * mm, "end": v(0.49, -48.7) * mm});
            skLineSegment(sketch, "E3624", {"start": v(0.49, -48.7) * mm, "end": v(0.54, -48.68) * mm});
            skLineSegment(sketch, "E3625", {"start": v(0.54, -48.68) * mm, "end": v(0.58, -48.65) * mm});
            skLineSegment(sketch, "E3626", {"start": v(0.58, -48.65) * mm, "end": v(0.63, -48.62) * mm});
            skLineSegment(sketch, "E3627", {"start": v(0.63, -48.62) * mm, "end": v(0.67, -48.59) * mm});
            skLineSegment(sketch, "E3628", {"start": v(0.67, -48.59) * mm, "end": v(0.71, -48.56) * mm});
            skLineSegment(sketch, "E3629", {"start": v(0.71, -48.56) * mm, "end": v(0.75, -48.52) * mm});
            skLineSegment(sketch, "E3630", {"start": v(0.75, -48.52) * mm, "end": v(0.8, -48.49) * mm});
            skLineSegment(sketch, "E3631", {"start": v(0.8, -48.49) * mm, "end": v(0.83, -48.45) * mm});
            skLineSegment(sketch, "E3632", {"start": v(0.83, -48.45) * mm, "end": v(0.87, -48.4) * mm});
            skLineSegment(sketch, "E3633", {"start": v(0.87, -48.4) * mm, "end": v(0.9, -48.37) * mm});
            skLineSegment(sketch, "E3634", {"start": v(0.9, -48.37) * mm, "end": v(0.93, -48.32) * mm});
            skLineSegment(sketch, "E3635", {"start": v(0.93, -48.32) * mm, "end": v(0.96, -48.28) * mm});
            skLineSegment(sketch, "E3636", {"start": v(0.96, -48.28) * mm, "end": v(1, -48.23) * mm});
            skLineSegment(sketch, "E3637", {"start": v(1, -48.23) * mm, "end": v(1.02, -48.18) * mm});
            skLineSegment(sketch, "E3638", {"start": v(1.02, -48.18) * mm, "end": v(1.05, -48.13) * mm});
            skLineSegment(sketch, "E3639", {"start": v(1.05, -48.13) * mm, "end": v(1.07, -48.08) * mm});
            skLineSegment(sketch, "E3640", {"start": v(1.07, -48.08) * mm, "end": v(1.1, -48.03) * mm});
            skLineSegment(sketch, "E3641", {"start": v(1.1, -48.03) * mm, "end": v(1.12, -47.97) * mm});
            skLineSegment(sketch, "E3642", {"start": v(1.12, -47.97) * mm, "end": v(1.14, -47.92) * mm});
            skLineSegment(sketch, "E3643", {"start": v(1.14, -47.92) * mm, "end": v(1.16, -47.86) * mm});
            skLineSegment(sketch, "E3644", {"start": v(1.16, -47.86) * mm, "end": v(1.17, -47.8) * mm});
            skLineSegment(sketch, "E3645", {"start": v(1.17, -47.8) * mm, "end": v(1.19, -47.74) * mm});
            skLineSegment(sketch, "E3646", {"start": v(1.19, -47.74) * mm, "end": v(1.2, -47.68) * mm});
            skLineSegment(sketch, "E3647", {"start": v(1.2, -47.68) * mm, "end": v(1.21, -47.61) * mm});
            skLineSegment(sketch, "E3648", {"start": v(1.21, -47.61) * mm, "end": v(1.22, -47.55) * mm});
            skLineSegment(sketch, "E3649", {"start": v(1.22, -47.55) * mm, "end": v(1.23, -47.48) * mm});
            skLineSegment(sketch, "E3650", {"start": v(1.23, -47.48) * mm, "end": v(1.23, -47.41) * mm});
            skLineSegment(sketch, "E3651", {"start": v(1.23, -47.41) * mm, "end": v(1.23, -47.34) * mm});
            skLineSegment(sketch, "E3652", {"start": v(1.23, -47.34) * mm, "end": v(1.23, -47.27) * mm});
            skLineSegment(sketch, "E3653", {"start": v(1.23, -47.27) * mm, "end": v(1.23, -44.45) * mm});
            skLineSegment(sketch, "E3654", {"start": v(1.23, -44.45) * mm, "end": v(1.23, -44.38) * mm});
            skLineSegment(sketch, "E3655", {"start": v(1.23, -44.38) * mm, "end": v(1.23, -44.31) * mm});
            skLineSegment(sketch, "E3656", {"start": v(1.23, -44.31) * mm, "end": v(1.23, -44.25) * mm});
            skLineSegment(sketch, "E3657", {"start": v(1.23, -44.25) * mm, "end": v(1.22, -44.18) * mm});
            skLineSegment(sketch, "E3658", {"start": v(1.22, -44.18) * mm, "end": v(1.21, -44.12) * mm});
            skLineSegment(sketch, "E3659", {"start": v(1.21, -44.12) * mm, "end": v(1.2, -44.05) * mm});
            skLineSegment(sketch, "E3660", {"start": v(1.2, -44.05) * mm, "end": v(1.19, -43.99) * mm});
            skLineSegment(sketch, "E3661", {"start": v(1.19, -43.99) * mm, "end": v(1.17, -43.93) * mm});
            skLineSegment(sketch, "E3662", {"start": v(1.17, -43.93) * mm, "end": v(1.16, -43.87) * mm});
            skLineSegment(sketch, "E3663", {"start": v(1.16, -43.87) * mm, "end": v(1.14, -43.81) * mm});
            skLineSegment(sketch, "E3664", {"start": v(1.14, -43.81) * mm, "end": v(1.12, -43.75) * mm});
            skLineSegment(sketch, "E3665", {"start": v(1.12, -43.75) * mm, "end": v(1.1, -43.7) * mm});
            skLineSegment(sketch, "E3666", {"start": v(1.1, -43.7) * mm, "end": v(1.07, -43.64) * mm});
            skLineSegment(sketch, "E3667", {"start": v(1.07, -43.64) * mm, "end": v(1.05, -43.6) * mm});
            skLineSegment(sketch, "E3668", {"start": v(1.05, -43.6) * mm, "end": v(1.02, -43.54) * mm});
            skLineSegment(sketch, "E3669", {"start": v(1.02, -43.54) * mm, "end": v(1, -43.5) * mm});
            skLineSegment(sketch, "E3670", {"start": v(1, -43.5) * mm, "end": v(0.96, -43.45) * mm});
            skLineSegment(sketch, "E3671", {"start": v(0.96, -43.45) * mm, "end": v(0.93, -43.4) * mm});
            skLineSegment(sketch, "E3672", {"start": v(0.93, -43.4) * mm, "end": v(0.9, -43.36) * mm});
            skLineSegment(sketch, "E3673", {"start": v(0.9, -43.36) * mm, "end": v(0.87, -43.32) * mm});
            skLineSegment(sketch, "E3674", {"start": v(0.87, -43.32) * mm, "end": v(0.83, -43.28) * mm});
            skLineSegment(sketch, "E3675", {"start": v(0.83, -43.28) * mm, "end": v(0.8, -43.24) * mm});
            skLineSegment(sketch, "E3676", {"start": v(0.8, -43.24) * mm, "end": v(0.75, -43.2) * mm});
            skLineSegment(sketch, "E3677", {"start": v(0.75, -43.2) * mm, "end": v(0.71, -43.17) * mm});
            skLineSegment(sketch, "E3678", {"start": v(0.71, -43.17) * mm, "end": v(0.67, -43.14) * mm});
            skLineSegment(sketch, "E3679", {"start": v(0.67, -43.14) * mm, "end": v(0.63, -43.1) * mm});
            skLineSegment(sketch, "E3680", {"start": v(0.63, -43.1) * mm, "end": v(0.58, -43.08) * mm});
            skLineSegment(sketch, "E3681", {"start": v(0.58, -43.08) * mm, "end": v(0.54, -43.05) * mm});
            skLineSegment(sketch, "E3682", {"start": v(0.54, -43.05) * mm, "end": v(0.49, -43.03) * mm});
            skLineSegment(sketch, "E3683", {"start": v(0.49, -43.03) * mm, "end": v(0.44, -43) * mm});
            skLineSegment(sketch, "E3684", {"start": v(0.44, -43) * mm, "end": v(0.4, -42.98) * mm});
            skLineSegment(sketch, "E3685", {"start": v(0.4, -42.98) * mm, "end": v(0.34, -42.96) * mm});
            skLineSegment(sketch, "E3686", {"start": v(0.34, -42.96) * mm, "end": v(0.29, -42.95) * mm});
            skLineSegment(sketch, "E3687", {"start": v(0.29, -42.95) * mm, "end": v(0.23, -42.93) * mm});
            skLineSegment(sketch, "E3688", {"start": v(0.23, -42.93) * mm, "end": v(0.18, -42.92) * mm});
            skLineSegment(sketch, "E3689", {"start": v(0.18, -42.92) * mm, "end": v(0.12, -42.91) * mm});
            skLineSegment(sketch, "E3690", {"start": v(0.12, -42.91) * mm, "end": v(0.06, -42.9) * mm});
            skLineSegment(sketch, "E3691", {"start": v(0.06, -42.9) * mm, "end": v(0, -42.9) * mm});
            skLineSegment(sketch, "E3692", {"start": v(0, -42.9) * mm, "end": v(-0.06, -42.9) * mm});
            skLineSegment(sketch, "E3693", {"start": v(-0.06, -42.9) * mm, "end": v(-0.12, -42.9) * mm});
            skSolve(sketch);
        }
        {
            var Q0;
            Q0 = qSketchRegion(id + "F14", true);
            extrude(context, id + "F15", {"entities" : qUnion([Q0]), "operationType" : NewBodyOperationType.REMOVE, "oppositeDirection" : true, "depth" : 0.3 * mm, "offsetDistance" : 25 * mm});
        }
        {
            var Q0;
            Q0=makeQuery(id+"F13.boolean.opBoolean","SPLIT",FACE,{"disambiguationData":[TD([makeQuery(id+"F13.opExtrude","SWEPT_FACE",FACE,{"disambiguationData":[OSD([sQuery(id+"F12.wireOp",EDGE,"E40")])]})])],"derivedFrom":makeQuery(id+"F1.opExtrude","CAP_FACE",FACE,{"disambiguationData":[OSD([sQuery(id+"F0.wireOp",EDGE,"E0"),sQuery(id+"F0.wireOp",EDGE,"E1")])],"isStart":false})});
            var sketch = newSketch(context, id + "F16", { "sketchPlane" : qUnion([Q0])});
            skText(sketch, "E3694", { "text": "C", "fontName": "OpenSans-Regular.ttf"});
            skText(sketch, "E3695", { "text": "V", "fontName": "OpenSans-Regular.ttf"});
            const initialGuessF16  = {"E3694": [-0.02398, -0.04924, 1, 0, 0.00674], "E3695": [0.01792, -0.04924, 1, 0, 0.00674]};
            skSetInitialGuess(sketch, initialGuessF16);
            skSolve(sketch);
        }
        {
            var Q0;
            Q0 = qSketchRegion(id + "F16", true);
            var Q1;
            Q1 = qConstructionFilter(qBodyType(qCreatedBy(id + "F16" ,EDGE), BodyType.WIRE), ConstructionObject.NO);
            extrude(context, id + "F17", {"entities" : qUnion([Q0]), "operationType" : NewBodyOperationType.REMOVE, "surfaceEntities" : qUnion([Q1]), "oppositeDirection" : true, "depth" : 0.3 * mm, "offsetDistance" : 25 * mm});
        }
        {
            var Q0;
            {var subQ0=sQuery(id+"F0.wireOp",EDGE,"E1");var subQ1=sQuery(id+"F0.wireOp",EDGE,"E0");Q0=makeQuery(id+"F13.boolean.opBoolean","SPLIT",FACE,{"disambiguationData":[TD([makeQuery(id+"F1.opExtrude","SWEPT_FACE",FACE,{"disambiguationData":[OSD([subQ1])]})])],"derivedFrom":makeQuery(id+"F1.opExtrude","CAP_FACE",FACE,{"disambiguationData":[OSD([subQ1,subQ0])],"isStart":false})});}
            var sketch = newSketch(context, id + "F18", { "sketchPlane" : qUnion([Q0])});
            skCircle(sketch, "E3696", {"center": v(50, 13.73) * mm, "radius": 13 * mm});
            skSolve(sketch);
        }
        {
            var Q0;
            Q0 = qSketchRegion(id + "F18", true);
            extrude(context, id + "F19", {"entities" : qUnion([Q0]), "operationType" : NewBodyOperationType.REMOVE, "oppositeDirection" : true, "depth" : 14.6 * mm, "offsetDistance" : 25 * mm});
        }
        {
            var Q0;
            {var subQ0=sQuery(id+"F0.wireOp",EDGE,"E1");var subQ1=sQuery(id+"F0.wireOp",EDGE,"E0");Q0=makeQuery(id+"F13.boolean.opBoolean","SPLIT",FACE,{"disambiguationData":[TD([makeQuery(id+"F1.opExtrude","SWEPT_FACE",FACE,{"disambiguationData":[OSD([subQ1])]})])],"derivedFrom":makeQuery(id+"F1.opExtrude","CAP_FACE",FACE,{"disambiguationData":[OSD([subQ1,subQ0])],"isStart":false})});}
            var sketch = newSketch(context, id + "F20", { "sketchPlane" : qUnion([Q0])});
            skArc(sketch, "E3697", {"start": v(-42.5, -14.19) * mm, "mid": v(0, 75.72) * mm, "end": v(42.5, -14.19) * mm});
            skArc(sketch, "E3698", {"start": v(-42.5, -14.19) * mm, "mid": v(-30.46, -41.99) * mm, "end": v(-34.97, -71.95) * mm});
            skArc(sketch, "E3699", {"start": v(42.5, -14.19) * mm, "mid": v(30.46, -41.99) * mm, "end": v(34.97, -71.95) * mm});
            skArc(sketch, "E3700", {"start": v(-44.05, -15.46) * mm, "mid": v(0, 77.72) * mm, "end": v(44.05, -15.46) * mm});
            skArc(sketch, "E3701", {"start": v(-44.05, -15.46) * mm, "mid": v(-32.45, -42.21) * mm, "end": v(-36.76, -71.05) * mm});
            skArc(sketch, "E3702", {"start": v(44.05, -15.46) * mm, "mid": v(32.45, -42.21) * mm, "end": v(36.76, -71.05) * mm});
            skArc(sketch, "E3703", {"start": v(-34.97, -71.95) * mm, "mid": v(-35.87, -71.5) * mm, "end": v(-36.76, -71.05) * mm});
            skArc(sketch, "E3704", {"start": v(34.97, -71.95) * mm, "mid": v(35.87, -71.5) * mm, "end": v(36.76, -71.05) * mm});
            skSolve(sketch);
        }
        {
            var Q0;
            Q0 = qSketchRegion(id + "F20", true);
            extrude(context, id + "F21", {"entities" : qUnion([Q0]), "operationType" : NewBodyOperationType.REMOVE, "oppositeDirection" : true, "depth" : 0.3 * mm, "offsetDistance" : 25 * mm});
        }
        {
            var Q0;
            Q0=makeQuery(id+"F1.opExtrude","CAP_FACE",FACE,{"disambiguationData":[OSD([sQuery(id+"F0.wireOp",EDGE,"E0"),sQuery(id+"F0.wireOp",EDGE,"E1")])],"isStart":true});
            var sketch = newSketch(context, id + "F22", { "sketchPlane" : qUnion([Q0])});
            skCircle(sketch, "E3705", {"center": v(-41, 35) * mm, "radius": 2 * mm});
            skCircle(sketch, "E3706", {"center": v(-41, -40) * mm, "radius": 2 * mm});
            skCircle(sketch, "E3707", {"center": v(41, -40) * mm, "radius": 2 * mm});
            skCircle(sketch, "E3708", {"center": v(41, 20) * mm, "radius": 2 * mm});
            skSolve(sketch);
        }
        {
            var Q0;
            Q0 = qSketchRegion(id + "F22", true);
            extrude(context, id + "F23", {"entities" : qUnion([Q0]), "operationType" : NewBodyOperationType.REMOVE, "oppositeDirection" : true, "depth" : 8 * mm, "offsetDistance" : 25 * mm});
        }
    });
